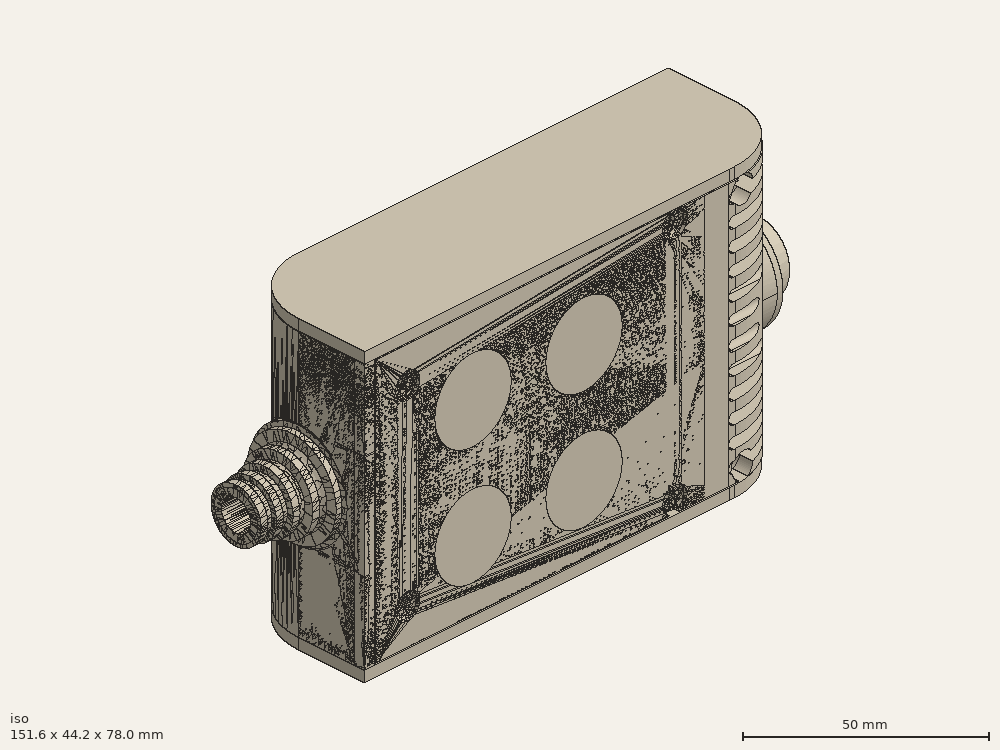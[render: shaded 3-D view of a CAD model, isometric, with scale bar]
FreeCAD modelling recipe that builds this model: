
FCSTD DOCUMENT  (FreeCAD 0.19R0.19.2)
Label: enclosure_184FCStd
License: All rights reserved
LicenseURL: http://en.wikipedia.org/wiki/All_rights_reserved
objects: Part::Revolution×152, Part::MultiFuse×146, Part::Feature×146, Sketcher::SketchObject×84, Part::Cut×70, Part::Cylinder×70, Part::Extrusion×67, Part::Fillet×58, Part::Box×36, App::MeasureDistance×4, PartDesign::Body×2, Image::ImagePlane×1
note: 831 computed .brp shape members not serialized (recipe doc carries the construction recipe); baked Part::Feature solids carry a one-line shape summary decoded from their .brp

FEATURE [Sketcher::SketchObject] Sketch  label="topSketch"
  FullyConstrained = true
  sketch-geometry (20):
    g0: LineSegment StartX=5.21097e-06 StartY=3 StartZ=0 EndX=5.21097e-06 EndY=19 EndZ=0
    g1: ArcOfCircle CenterX=19 CenterY=19 CenterZ=0 NormalX=0 NormalY=0 NormalZ=1 AngleXU=0 Radius=19 StartAngle=1.5708 EndAngle=3.14159
    g2: ArcOfCircle CenterX=19 CenterY=19 CenterZ=0 NormalX=0 NormalY=0 NormalZ=1 AngleXU=0 Radius=16 StartAngle=1.5708 EndAngle=3.14159
    g3: LineSegment StartX=114 StartY=35 StartZ=0 EndX=19 EndY=35 EndZ=0
    g4: LineSegment StartX=5.21097e-06 StartY=3 StartZ=0 EndX=5.21097e-06 EndY=0 EndZ=0
    g5: LineSegment StartX=3 StartY=0 StartZ=0 EndX=5.21097e-06 EndY=0 EndZ=0
    g6: LineSegment StartX=3 StartY=19 StartZ=0 EndX=3 EndY=0 EndZ=0
    g7: LineSegment StartX=19 StartY=38 StartZ=0 EndX=124 EndY=38 EndZ=0
    g8: Circle CenterX=119 CenterY=35 CenterZ=0 NormalX=0 NormalY=0 NormalZ=1 AngleXU=0 Radius=1
    g9: Circle CenterX=121 CenterY=35 CenterZ=0 NormalX=0 NormalY=0 NormalZ=1 AngleXU=0 Radius=1
    g10: Circle CenterX=121 CenterY=33 CenterZ=0 NormalX=0 NormalY=0 NormalZ=1 AngleXU=0 Radius=1
    g11: BSplineCurve PolesCount=3 KnotsCount=2 Degree=2 IsPeriodic=0
    g12: GeomPoint X=119 Y=35 Z=0
    g13: GeomPoint X=121 Y=33 Z=0
    g14: LineSegment StartX=119 StartY=35 StartZ=0 EndX=114 EndY=35 EndZ=0
    g15: ArcOfCircle CenterX=105 CenterY=19 CenterZ=0 NormalX=0 NormalY=0 NormalZ=1 AngleXU=0 Radius=19 StartAngle=5.7297 EndAngle=6.28319
    g16: ArcOfCircle CenterX=105 CenterY=19 CenterZ=0 NormalX=0 NormalY=0 NormalZ=1 AngleXU=0 Radius=16 StartAngle=5.60905 EndAngle=6.28319
    g17: LineSegment StartX=121 StartY=33 StartZ=0 EndX=121 EndY=19 EndZ=0
    g18: LineSegment StartX=124 StartY=38 StartZ=0 EndX=124 EndY=19 EndZ=0
    g19: LineSegment StartX=117.5 StartY=9.01251 StartZ=0 EndX=121.163 EndY=9.0125 EndZ=0
  constraints (46):
    c: Vertical(g0)
    c: Block(g0)
    c: Coincident(g1,g0)
    c: Block(g1)
    c: Coincident(g2,g1)
    c: Block(g2)
    c: Coincident(g3,g2)
    c: Horizontal(g3)
    c: Tangent(g3,g2)
    c: Coincident(g4,g0)
    c: Distance(g4) = 3
    c: Vertical(g4)
    c: Coincident(g5,g4)
    c: Horizontal(g5)
    c: Coincident(g6,g2)
    c: Coincident(g6,g5)
    c: Vertical(g6)
    c: Horizontal(g7)
    c: Distance(g7) = 105
    c: Coincident(g7,g1)
    c: Block(g3)
    c: Weight(g8) = 1
    c: Equal(g8,g9)
    c: Equal(g8,g10)
    c: InternalAlignment(g8,g11)
    c: InternalAlignment(g9,g11)
    c: InternalAlignment(g10,g11)
    c: InternalAlignment(g12,g11)
    c: InternalAlignment(g13,g11)
    c: Block(g11)
    c: Coincident(g14,g11)
    c: Coincident(g14,g3)
    c: Horizontal(g14)
    c: Block(g15)
    c: Coincident(g16,g15)
    c: Block(g16)
    c: Coincident(g17,g11)
    c: Coincident(g17,g16)
    c: Vertical(g17)
    c: Distance(g17) = 14
    c: Coincident(g18,g7)
    c: Coincident(g18,g15)
    c: Vertical(g18)
    c: Distance(g18) = 19
    c: Coincident(g19,g16)
    c: Coincident(g19,g15)
FEATURE [Sketcher::SketchObject] Sketch001  label="bottomSketch"
  FullyConstrained = true
  sketch-geometry (32):
    g0: LineSegment StartX=3.3 StartY=-6.03275e-07 StartZ=0 EndX=98 EndY=-6.03275e-07 EndZ=0
    g1: ArcOfCircle CenterX=98 CenterY=19 CenterZ=0 NormalX=0 NormalY=0 NormalZ=1 AngleXU=0 Radius=19 StartAngle=4.71239 EndAngle=5.71103
    g2: LineSegment StartX=6.3 StartY=8 StartZ=0 EndX=3.3 EndY=8 EndZ=0
    g3: LineSegment StartX=3.3 StartY=8 StartZ=0 EndX=3.3 EndY=-6.03275e-07 EndZ=0
    g4: ArcOfCircle CenterX=8.3 CenterY=5 CenterZ=0 NormalX=0 NormalY=0 NormalZ=1 AngleXU=0 Radius=2 StartAngle=3.14159 EndAngle=4.71239
    g5: LineSegment StartX=6.3 StartY=8 StartZ=0 EndX=6.3 EndY=5 EndZ=0
    g6: ArcOfCircle CenterX=98 CenterY=19 CenterZ=0 NormalX=0 NormalY=0 NormalZ=1 AngleXU=0 Radius=12.7 StartAngle=4.71239 EndAngle=6.28319
    g7: LineSegment StartX=94.7 StartY=3 StartZ=0 EndX=8.3 EndY=3 EndZ=0
    g8-g12: Circle x5 (B-spline internal-alignment scaffolding for g13; pole/knot coordinates omitted)
    g13: BSplineCurve PolesCount=5 KnotsCount=3 Degree=3 IsPeriodic=0
    g14: GeomPoint X=98 Y=6.3 Z=0
    g15: GeomPoint X=96.3938 Y=4.71946 Z=0
    g16: GeomPoint X=94.7 Y=3 Z=0
    g17-g23: Circle x7 (B-spline internal-alignment scaffolding for g24; pole/knot coordinates omitted)
    g24: BSplineCurve PolesCount=7 KnotsCount=5 Degree=3 IsPeriodic=0
    g25-g29: GeomPoint x5 (B-spline internal-alignment scaffolding for g24; pole/knot coordinates omitted)
    g30: ArcOfCircle CenterX=98 CenterY=19 CenterZ=0 NormalX=0 NormalY=0 NormalZ=1 AngleXU=0 Radius=15.7 StartAngle=5.81226 EndAngle=6.28319
    g31: LineSegment StartX=110.7 StartY=19 StartZ=0 EndX=113.7 EndY=19 EndZ=0
  constraints (41):
    c: Horizontal(g0)
    c: Coincident(g1,g0)
    c: Block(g1)
    c: Horizontal(g2)
    c: Distance(g2) = 3
    c: Coincident(g3,g2)
    c: Vertical(g3)
    c: Coincident(g3,g0)
    c: Block(g4)
    c: Block(g2)
    c: Coincident(g5,g2)
    c: Coincident(g5,g4)
    c: Vertical(g5)
    c: Coincident(g6,g1)
    c: Block(g6)
    c: Coincident(g7,g4)
    c: Horizontal(g7)
    c: Block(g0)
    c: Block(g7)
    c: Block(g3)
    c: Coincident(g13,g6)
    c: Weight(g8) = 1
    c: Equal(g8, g9-g12) x4
    c: Coincident(g13,g7)
    c: InternalAlignment(g8-g12 -> g13) x5
    c: InternalAlignment(g14,g13)
    c: InternalAlignment(g15,g13)
    c: InternalAlignment(g16,g13)
    c: Block(g13)
    c: Weight(g17) = 1
    c: Equal(g17, g18-g23) x6
    c: Coincident(g24,g1)
    c: InternalAlignment(g17-g23 -> g24) x7
    c: InternalAlignment(g25-g29 -> g24) x5
    c: Block(g24)
    c: Coincident(g30,g24)
    c: Coincident(g31,g6)
    c: Coincident(g31,g30)
    c: Horizontal(g31)
    c: Block(g31)
    c: Block(g30)
FEATURE [Part::Extrusion] Extrude  label="top"
  Base = -> Sketch
  Dir = (0,0,1)
  DirMode = 2
  FaceMakerClass = Part::FaceMakerBullseye
  LengthFwd = 72
  LengthRev = 0
  Solid = true
  Symmetric = false
FEATURE [Part::Extrusion] Extrude001  label="bottom"
  Base = -> Sketch001
  Dir = (0,0,1)
  DirMode = 2
  FaceMakerClass = Part::FaceMakerBullseye
  LengthFwd = 71.4
  LengthRev = 0
  Placement = pos=(0,0,0.3) rot=(0,0,1;0rad)
  Solid = true
  Symmetric = false
FEATURE [Sketcher::SketchObject] Sketch002  label="topSketch001"
  FullyConstrained = true
  sketch-geometry (8):
    g0: ArcOfCircle CenterX=19 CenterY=19.0975 CenterZ=0 NormalX=0 NormalY=0 NormalZ=1 AngleXU=0 Radius=18.9025 StartAngle=1.5708 EndAngle=3.14674
    g1: LineSegment StartX=0.0977805 StartY=19.0003 StartZ=0 EndX=0.0977805 EndY=0.000251602 EndZ=0
    g2: LineSegment StartX=19 StartY=38 StartZ=0 EndX=124 EndY=38 EndZ=0
    g3: LineSegment StartX=0.0977805 StartY=0.000251602 StartZ=0 EndX=105.098 EndY=0.000251602 EndZ=0
    g4: LineSegment StartX=124 StartY=38 StartZ=0 EndX=125.616 EndY=38 EndZ=0
    g5: LineSegment StartX=105.098 StartY=0.000251602 StartZ=0 EndX=106.713 EndY=0.000251602 EndZ=0
    g6: ArcOfCircle CenterX=106.616 CenterY=19 CenterZ=0 NormalX=0 NormalY=0 NormalZ=1 AngleXU=0 Radius=19 StartAngle=4.71754 EndAngle=6.28319
    g7: LineSegment StartX=125.616 StartY=38 StartZ=0 EndX=125.616 EndY=19 EndZ=0
  constraints (21):
    c: Block(g0)
    c: Coincident(g1,g0)
    c: Vertical(g1)
    c: Horizontal(g2)
    c: Distance(g2) = 105
    c: Coincident(g2,g0)
    c: Distance(g1) = 19
    c: Coincident(g3,g1)
    c: Horizontal(g3)
    c: Distance(g3) = 105
    c: Coincident(g4,g2)
    c: Horizontal(g4)
    c: Distance(g4) = 1.61553
    c: Horizontal(g5)
    c: Equal(g4,g5) = 1.61553
    c: Coincident(g5,g3)
    c: Block(g6)
    c: Coincident(g6,g5)
    c: Coincident(g7,g4)
    c: Coincident(g7,g6)
    c: Vertical(g7)
FEATURE [Part::Extrusion] Extrude002  label="sideA"
  Base = -> Sketch002
  Dir = (0,0,1)
  DirMode = 2
  FaceMakerClass = Part::FaceMakerBullseye
  LengthFwd = 3
  LengthRev = 0
  Placement = pos=(0,0,-3) rot=(0,0,1;0rad)
  Solid = true
  Symmetric = false
FEATURE [Sketcher::SketchObject] Sketch003  label="topSketch002"
  FullyConstrained = true
  sketch-geometry (6):
    g0: LineSegment StartX=19 StartY=38 StartZ=0 EndX=117 EndY=38 EndZ=0
    g1: ArcOfCircle CenterX=19 CenterY=19 CenterZ=0 NormalX=0 NormalY=0 NormalZ=1 AngleXU=0 Radius=19 StartAngle=1.5708 EndAngle=3.14159
    g2: LineSegment StartX=117 StartY=38 StartZ=0 EndX=117 EndY=19 EndZ=0
    g3: LineSegment StartX=98 StartY=1.0161e-12 StartZ=0 EndX=5.22862e-06 EndY=1.0161e-12 EndZ=0
    g4: LineSegment StartX=5.22862e-06 StartY=19 StartZ=0 EndX=5.22862e-06 EndY=1.0161e-12 EndZ=0
    g5: ArcOfCircle CenterX=98 CenterY=19 CenterZ=0 NormalX=0 NormalY=0 NormalZ=1 AngleXU=0 Radius=19 StartAngle=4.71239 EndAngle=6.28319
  constraints (16):
    c: Horizontal(g0)
    c: Distance(g0) = 98
    c: Coincident(g1,g0)
    c: Block(g1)
    c: Coincident(g2,g0)
    c: Vertical(g2)
    c: Distance(g2) = 19
    c: Horizontal(g3)
    c: Coincident(g4,g1)
    c: Vertical(g4)
    c: Coincident(g3,g4)
    c: Block(g3)
    c: Coincident(g5,g2)
    c: Coincident(g5,g3)
    c: Block(g0)
    c: Block(g5)
FEATURE [Sketcher::SketchObject] Sketch004
  FullyConstrained = true
  MapMode = 3
  Placement = pos=(0,0,0) rot=(1,0,0;1.5708rad)
  Support = -> [Extrude]
  sketch-geometry (8):
    g0: Circle CenterX=80.351 CenterY=-67.6202 CenterZ=0 NormalX=0 NormalY=0 NormalZ=1 AngleXU=0 Radius=2
    g1: Circle CenterX=80.351 CenterY=-67.6202 CenterZ=0 NormalX=0 NormalY=0 NormalZ=1 AngleXU=0 Radius=3
    g2: Circle CenterX=80.351 CenterY=-4.92017 CenterZ=0 NormalX=0 NormalY=0 NormalZ=1 AngleXU=0 Radius=2
    g3: Circle CenterX=80.351 CenterY=-4.92017 CenterZ=0 NormalX=0 NormalY=0 NormalZ=1 AngleXU=0 Radius=3
    g4: Circle CenterX=23.851 CenterY=-4.92017 CenterZ=0 NormalX=0 NormalY=0 NormalZ=1 AngleXU=0 Radius=2
    g5: Circle CenterX=23.851 CenterY=-4.92017 CenterZ=0 NormalX=0 NormalY=0 NormalZ=1 AngleXU=0 Radius=3
    g6: Circle CenterX=23.851 CenterY=-67.6202 CenterZ=0 NormalX=0 NormalY=0 NormalZ=1 AngleXU=0 Radius=2
    g7: Circle CenterX=23.851 CenterY=-67.6202 CenterZ=0 NormalX=0 NormalY=0 NormalZ=1 AngleXU=0 Radius=3
  constraints (8):
    c: Block(g3)
    c: Block(g2)
    c: Block(g1)
    c: Block(g0)
    c: Block(g6)
    c: Block(g7)
    c: Block(g4)
    c: Block(g5)
FEATURE [Part::Extrusion] Extrude004
  Base = -> Sketch004
  Dir = (0,-1,2e-16)
  DirMode = 2
  FaceMakerClass = Part::FaceMakerBullseye
  LengthFwd = 6
  LengthRev = 0
  Placement = pos=(0,9,0) rot=(0,0,1;0rad)
  Solid = true
  Symmetric = false
FEATURE [Sketcher::SketchObject] Sketch005
  FullyConstrained = true
  MapMode = 3
  Placement = pos=(0,0,0) rot=(1,0,0;1.5708rad)
  Support = -> [Extrude]
  sketch-geometry (8):
    g0: Circle CenterX=80.351 CenterY=-67.6202 CenterZ=0 NormalX=0 NormalY=0 NormalZ=1 AngleXU=0 Radius=3
    g1: Circle CenterX=80.351 CenterY=-4.92017 CenterZ=0 NormalX=0 NormalY=0 NormalZ=1 AngleXU=0 Radius=3
    g2: Circle CenterX=23.851 CenterY=-4.92017 CenterZ=0 NormalX=0 NormalY=0 NormalZ=1 AngleXU=0 Radius=3
    g3: Circle CenterX=23.851 CenterY=-67.6202 CenterZ=0 NormalX=0 NormalY=0 NormalZ=1 AngleXU=0 Radius=3
    g4: Circle CenterX=23.851 CenterY=-67.6202 CenterZ=0 NormalX=0 NormalY=0 NormalZ=1 AngleXU=0 Radius=5
    g5: Circle CenterX=80.351 CenterY=-67.6202 CenterZ=0 NormalX=0 NormalY=0 NormalZ=1 AngleXU=0 Radius=5
    g6: Circle CenterX=23.851 CenterY=-4.92017 CenterZ=0 NormalX=0 NormalY=0 NormalZ=1 AngleXU=0 Radius=5
    g7: Circle CenterX=80.351 CenterY=-4.92017 CenterZ=0 NormalX=0 NormalY=0 NormalZ=1 AngleXU=0 Radius=5
  constraints (8):
    c: Block(g1)
    c: Block(g0)
    c: Block(g3)
    c: Block(g2)
    c: Block(g5)
    c: Block(g4)
    c: Block(g6)
    c: Block(g7)
FEATURE [Part::Extrusion] Extrude005
  Base = -> Sketch005
  Dir = (0,-1,2e-16)
  DirMode = 2
  FaceMakerClass = Part::FaceMakerBullseye
  LengthFwd = 2
  LengthRev = 0
  Solid = true
  Symmetric = false
FEATURE [Sketcher::SketchObject] Sketch006
  FullyConstrained = true
  MapMode = 3
  Placement = pos=(0,0,0) rot=(1,0,0;1.5708rad)
  sketch-geometry (8):
    g0: Circle CenterX=80.351 CenterY=-67.6202 CenterZ=0 NormalX=0 NormalY=0 NormalZ=1 AngleXU=0 Radius=3
    g1: Circle CenterX=80.351 CenterY=-4.92017 CenterZ=0 NormalX=0 NormalY=0 NormalZ=1 AngleXU=0 Radius=3
    g2: Circle CenterX=23.851 CenterY=-4.92017 CenterZ=0 NormalX=0 NormalY=0 NormalZ=1 AngleXU=0 Radius=3
    g3: Circle CenterX=23.851 CenterY=-67.6202 CenterZ=0 NormalX=0 NormalY=0 NormalZ=1 AngleXU=0 Radius=3
    g4: Circle CenterX=23.851 CenterY=-67.6202 CenterZ=0 NormalX=0 NormalY=0 NormalZ=1 AngleXU=0 Radius=5
    g5: Circle CenterX=80.351 CenterY=-67.6202 CenterZ=0 NormalX=0 NormalY=0 NormalZ=1 AngleXU=0 Radius=5
    g6: Circle CenterX=23.851 CenterY=-4.92017 CenterZ=0 NormalX=0 NormalY=0 NormalZ=1 AngleXU=0 Radius=5
    g7: Circle CenterX=80.351 CenterY=-4.92017 CenterZ=0 NormalX=0 NormalY=0 NormalZ=1 AngleXU=0 Radius=5
  constraints (8):
    c: Block(g1)
    c: Block(g0)
    c: Block(g3)
    c: Block(g2)
    c: Block(g5)
    c: Block(g4)
    c: Block(g6)
    c: Block(g7)
FEATURE [Part::Extrusion] Extrude007
  Base = -> Sketch006
  Dir = (0,-1,2e-16)
  DirMode = 2
  FaceMakerClass = Part::FaceMakerBullseye
  LengthFwd = 2
  LengthRev = 0
  Solid = true
  Symmetric = false
FEATURE [Part::Fillet] Fillet
  Base = -> Extrude007
  Edges = 4 edges r=1.99: [Edge6,Edge12,Edge18,Edge24]
FEATURE [Part::Cut] Cut
  Base = -> Extrude005
  Placement = pos=(0,5,0) rot=(0,0,1;0rad)
  Tool = -> Fillet
FEATURE [Part::MultiFuse] Fusion  label="pCBScrews"
  Placement = pos=(-2.5,0,72.3) rot=(0,0,1;0rad)
  Shapes = -> [Extrude004,Cut]
FEATURE [App::MeasureDistance] Distance  label="Distance: 0.69 mm"
  Distance = 0.685967
  P1 = (24.0138,2.9647,0.3)
  P2 = (23.8901,3,-0.373787)
FEATURE [App::MeasureDistance] Distance001  label="Distance: 0.53 mm"
  Distance = 0.533607
  P1 = (80.2939,3,72.2334)
  P2 = (80.281,2.99661,71.7)
FEATURE [Part::Fillet] Fillet001
  Base = -> Extrude001
  Edges = 1 edges r=2.4: [Edge17]
FEATURE [Part::Fillet] Fillet002  label="bottom001"
  Base = -> Fillet001
  Edges = 1 edges r=2.4: [Edge36]
FEATURE [Part::Fillet] Fillet003  label="top001"
  Base = -> Extrude
  Edges = 1 edges r=2: [Edge1]
FEATURE [Sketcher::SketchObject] Sketch007
  FullyConstrained = true
  sketch-geometry (16):
    g0: LineSegment StartX=4 StartY=0 StartZ=0 EndX=4 EndY=2.4 EndZ=0
    g1: LineSegment StartX=4 StartY=2.4 StartZ=0 EndX=7 EndY=2.4 EndZ=0
    g2: LineSegment StartX=4 StartY=0 StartZ=0 EndX=5.7 EndY=0 EndZ=0
    g3: LineSegment StartX=5.7 StartY=0 StartZ=0 EndX=5.7 EndY=-5.6 EndZ=0
    g4-g8: Circle x5 (B-spline internal-alignment scaffolding for g9; pole/knot coordinates omitted)
    g9: BSplineCurve PolesCount=5 KnotsCount=3 Degree=3 IsPeriodic=0
    g10: GeomPoint X=7 Y=2.4 Z=0
    g11: GeomPoint X=10.4582 Y=-1.55472 Z=0
    g12: GeomPoint X=14 Y=-5.6 Z=0
    g13: LineSegment StartX=14 StartY=-5.6 StartZ=0 EndX=14 EndY=-14.1 EndZ=0
    g14: LineSegment StartX=14 StartY=-14.1 StartZ=0 EndX=6.5 EndY=-14.1 EndZ=0
    g15: LineSegment StartX=5.7 StartY=-5.6 StartZ=0 EndX=6.5 EndY=-14.1 EndZ=0
  constraints (28):
    c: Distance(g0) = 2.4
    c: Vertical(g0)
    c: Block(g0)
    c: Coincident(g1,g0)
    c: Horizontal(g1)
    c: Distance(g1) = 3
    c: Coincident(g2,g0)
    c: Horizontal(g2)
    c: Distance(g2) = 1.7
    c: Coincident(g3,g2)
    c: Vertical(g3)
    c: Distance(g3) = 5.6
    c: Coincident(g9,g1)
    c: Weight(g4) = 1
    c: Equal(g4, g5-g8) x4
    c: InternalAlignment(g4-g8 -> g9) x5
    c: InternalAlignment(g10,g9)
    c: InternalAlignment(g11,g9)
    c: InternalAlignment(g12,g9)
    c: Block(g9)
    c: Coincident(g13,g9)
    c: Vertical(g13)
    c: Distance(g13) = 8.5
    c: Coincident(g14,g13)
    c: Horizontal(g14)
    c: Distance(g14) = 7.5
    c: Coincident(g15,g3)
    c: Coincident(g15,g14)
FEATURE [Part::Feature] Face
  shape: bbox 10 x 16.5 x 2e-07 mm, 1 faces, 0 solids (baked)
FEATURE [Part::Revolution] Revolve  label="plugHousing"
  Angle = 360
  Axis = (0,1,0)
  Base = (0,0,0)
  FaceMakerClass = Part::FaceMakerBullseye
  Placement = pos=(0,0,36.15) rot=(0,0,1;0rad)
  Solid = false
  Source = -> Face
  Symmetric = false
FEATURE [Part::Feature] Face001
  shape: bbox 10 x 16.5 x 2e-07 mm, 1 faces, 0 solids (baked)
FEATURE [Part::Revolution] Revolve001  label="plugHousing001"
  Angle = 360
  Axis = (0,1,0)
  Base = (0,0,0)
  FaceMakerClass = Part::FaceMakerBullseye
  Placement = pos=(0,0,36.15) rot=(0,0,1;0rad)
  Solid = false
  Source = -> Face001
  Symmetric = false
FEATURE [Part::MultiFuse] Fusion001  label="plugHousing002"
  Placement = pos=(0,0,0) rot=(0,0,1;1.5708rad)
  Shapes = -> [Revolve001,Revolve]
FEATURE [Part::Feature] Face002
  shape: bbox 10 x 16.5 x 2e-07 mm, 1 faces, 0 solids (baked)
FEATURE [Part::Revolution] Revolve003  label="plugHousing005"
  Angle = 360
  Axis = (0,1,0)
  Base = (0,0,0)
  FaceMakerClass = Part::FaceMakerBullseye
  Placement = pos=(0,0,36.15) rot=(0,0,1;0rad)
  Solid = false
  Source = -> Face002
  Symmetric = false
FEATURE [Part::Feature] Face003
  shape: bbox 10 x 16.5 x 2e-07 mm, 1 faces, 0 solids (baked)
FEATURE [Part::Revolution] Revolve002  label="plugHousing003"
  Angle = 360
  Axis = (0,1,0)
  Base = (0,0,0)
  FaceMakerClass = Part::FaceMakerBullseye
  Placement = pos=(0,0,36.15) rot=(0,0,1;0rad)
  Solid = false
  Source = -> Face003
  Symmetric = false
FEATURE [Part::MultiFuse] Fusion002  label="plugHousing004"
  Placement = pos=(0,0,0) rot=(0,0,1;1.5708rad)
  Shapes = -> [Revolve002,Revolve003]
FEATURE [Part::MultiFuse] Fusion003  label="plugHousing006"
  Placement = pos=(0,19,0) rot=(0,0,1;3.14159rad)
  Shapes = -> [Fusion002,Fusion001]
FEATURE [Part::Feature] Face004
  shape: bbox 10 x 16.5 x 2e-07 mm, 1 faces, 0 solids (baked)
FEATURE [Part::Revolution] Revolve006  label="plugHousing010"
  Angle = 360
  Axis = (0,1,0)
  Base = (0,0,0)
  FaceMakerClass = Part::FaceMakerBullseye
  Placement = pos=(0,0,36.15) rot=(0,0,1;0rad)
  Solid = false
  Source = -> Face004
  Symmetric = false
FEATURE [Part::Feature] Face005
  shape: bbox 10 x 16.5 x 2e-07 mm, 1 faces, 0 solids (baked)
FEATURE [Part::Revolution] Revolve007  label="plugHousing011"
  Angle = 360
  Axis = (0,1,0)
  Base = (0,0,0)
  FaceMakerClass = Part::FaceMakerBullseye
  Placement = pos=(0,0,36.15) rot=(0,0,1;0rad)
  Solid = false
  Source = -> Face005
  Symmetric = false
FEATURE [Part::Feature] Face006
  shape: bbox 10 x 16.5 x 2e-07 mm, 1 faces, 0 solids (baked)
FEATURE [Part::Revolution] Revolve004  label="plugHousing007"
  Angle = 360
  Axis = (0,1,0)
  Base = (0,0,0)
  FaceMakerClass = Part::FaceMakerBullseye
  Placement = pos=(0,0,36.15) rot=(0,0,1;0rad)
  Solid = false
  Source = -> Face006
  Symmetric = false
FEATURE [Part::MultiFuse] Fusion004  label="plugHousing009"
  Placement = pos=(0,0,0) rot=(0,0,1;1.5708rad)
  Shapes = -> [Revolve004,Revolve007]
FEATURE [Part::Feature] Face007
  shape: bbox 10 x 16.5 x 2e-07 mm, 1 faces, 0 solids (baked)
FEATURE [Part::Revolution] Revolve005  label="plugHousing008"
  Angle = 360
  Axis = (0,1,0)
  Base = (0,0,0)
  FaceMakerClass = Part::FaceMakerBullseye
  Placement = pos=(0,0,36.15) rot=(0,0,1;0rad)
  Solid = false
  Source = -> Face007
  Symmetric = false
FEATURE [Part::MultiFuse] Fusion005  label="plugHousing012"
  Placement = pos=(0,0,0) rot=(0,0,1;1.5708rad)
  Shapes = -> [Revolve006,Revolve005]
FEATURE [Part::MultiFuse] Fusion006  label="plugHousing013"
  Placement = pos=(0,19,0) rot=(0,0,1;3.14159rad)
  Shapes = -> [Fusion005,Fusion004]
FEATURE [Part::MultiFuse] Fusion007  label="plugHousing014"
  Placement = pos=(122.621,0,-0.15) rot=(0,0,1;0rad)
  Shapes = -> [Fusion003,Fusion006]
FEATURE [Part::Cylinder] Cylinder002
  Angle = 360
  AttacherType = Attacher::AttachEngine3D
  Height = 20
  Placement = pos=(0,0,36.15) rot=(0,0,1;0rad)
  Radius = 4
FEATURE [Part::Cylinder] Cylinder003
  Angle = 360
  AttacherType = Attacher::AttachEngine3D
  Height = 10
  Placement = pos=(0,0,36.15) rot=(0,0,1;0rad)
  Radius = 4
FEATURE [Part::MultiFuse] Fusion009  label="removeToCreateHoleForPlugHousing"
  Placement = pos=(70,19,36.15) rot=(0,1,0;1.5708rad)
  Shapes = -> [Cylinder002,Cylinder003]
FEATURE [Part::Cylinder] Cylinder004
  Angle = 360
  AttacherType = Attacher::AttachEngine3D
  Height = 20
  Placement = pos=(0,0,36.15) rot=(0,0,1;0rad)
  Radius = 4
FEATURE [Part::Cylinder] Cylinder005
  Angle = 360
  AttacherType = Attacher::AttachEngine3D
  Height = 10
  Placement = pos=(0,0,36.15) rot=(0,0,1;0rad)
  Radius = 4
FEATURE [Part::MultiFuse] Fusion010  label="removeToCreateHoleForPlugHousing001"
  Placement = pos=(70,19,36.15) rot=(0,1,0;1.5708rad)
  Shapes = -> [Cylinder004,Cylinder005]
FEATURE [Part::Cut] Cut001
  Base = -> Fillet003
  Tool = -> Fusion010
FEATURE [Part::Cut] Cut002  label="Bottom"
  Base = -> Fillet002
  Tool = -> Fusion009
FEATURE [Part::Feature] Face008
  shape: bbox 10 x 16.5 x 2e-07 mm, 1 faces, 0 solids (baked)
FEATURE [Part::Revolution] Revolve011  label="plugHousing021"
  Angle = 360
  Axis = (0,1,0)
  Base = (0,0,0)
  FaceMakerClass = Part::FaceMakerBullseye
  Placement = pos=(0,0,36.15) rot=(0,0,1;0rad)
  Solid = false
  Source = -> Face008
  Symmetric = false
FEATURE [Part::Feature] Face009
  shape: bbox 10 x 16.5 x 2e-07 mm, 1 faces, 0 solids (baked)
FEATURE [Part::Revolution] Revolve012  label="plugHousing022"
  Angle = 360
  Axis = (0,1,0)
  Base = (0,0,0)
  FaceMakerClass = Part::FaceMakerBullseye
  Placement = pos=(0,0,36.15) rot=(0,0,1;0rad)
  Solid = false
  Source = -> Face009
  Symmetric = false
FEATURE [Part::Feature] Face010 .. Face013  x4 (patterned run collapsed; names and placements below)
  shape: bbox 10 x 16.5 x 2e-07 mm, 1 faces, 0 solids (baked)
FEATURE [Part::Revolution] Revolve015  label="plugHousing027"
  Angle = 360
  Axis = (0,1,0)
  Base = (0,0,0)
  FaceMakerClass = Part::FaceMakerBullseye
  Placement = pos=(0,0,36.15) rot=(0,0,1;0rad)
  Solid = false
  Source = -> Face013
  Symmetric = false
FEATURE [Part::Feature] Face014
  shape: bbox 10 x 16.5 x 2e-07 mm, 1 faces, 0 solids (baked)
FEATURE [Part::Feature] Face015
  shape: bbox 10 x 16.5 x 2e-07 mm, 1 faces, 0 solids (baked)
FEATURE [Part::Feature] Face016
  shape: bbox 10 x 16.5 x 2e-07 mm, 1 faces, 0 solids (baked)
FEATURE [Part::Revolution] Revolve019  label="plugHousing033"
  Angle = 360
  Axis = (0,1,0)
  Base = (0,0,0)
  FaceMakerClass = Part::FaceMakerBullseye
  Placement = pos=(0,0,36.15) rot=(0,0,1;0rad)
  Solid = false
  Source = -> Face016
  Symmetric = false
FEATURE [Part::Feature] Face017
  shape: bbox 10 x 16.5 x 2e-07 mm, 1 faces, 0 solids (baked)
FEATURE [Part::Revolution] Revolve020  label="plugHousing034"
  Angle = 360
  Axis = (0,1,0)
  Base = (0,0,0)
  FaceMakerClass = Part::FaceMakerBullseye
  Placement = pos=(0,0,36.15) rot=(0,0,1;0rad)
  Solid = false
  Source = -> Face017
  Symmetric = false
FEATURE [Part::Feature] Face018
  shape: bbox 10 x 16.5 x 2e-07 mm, 1 faces, 0 solids (baked)
FEATURE [Part::Revolution] Revolve016  label="plugHousing030"
  Angle = 360
  Axis = (0,1,0)
  Base = (0,0,0)
  FaceMakerClass = Part::FaceMakerBullseye
  Placement = pos=(0,0,36.15) rot=(0,0,1;0rad)
  Solid = false
  Source = -> Face018
  Symmetric = false
FEATURE [Part::MultiFuse] Fusion020  label="plugHousing038"
  Placement = pos=(0,0,0) rot=(0,0,1;1.5708rad)
  Shapes = -> [Revolve016,Revolve020]
FEATURE [Part::Feature] Face019
  shape: bbox 10 x 16.5 x 2e-07 mm, 1 faces, 0 solids (baked)
FEATURE [Part::Feature] Face020
  shape: bbox 10 x 16.5 x 2e-07 mm, 1 faces, 0 solids (baked)
FEATURE [Part::Revolution] Revolve017  label="plugHousing031"
  Angle = 360
  Axis = (0,1,0)
  Base = (0,0,0)
  FaceMakerClass = Part::FaceMakerBullseye
  Placement = pos=(0,0,36.15) rot=(0,0,1;0rad)
  Solid = false
  Source = -> Face020
  Symmetric = false
FEATURE [Part::MultiFuse] Fusion021  label="plugHousing039"
  Placement = pos=(0,0,0) rot=(0,0,1;1.5708rad)
  Shapes = -> [Revolve019,Revolve017]
FEATURE [Part::MultiFuse] Fusion023  label="plugHousing041"
  Placement = pos=(0,19,0) rot=(0,0,1;3.14159rad)
  Shapes = -> [Fusion021,Fusion020]
FEATURE [Part::Revolution] Revolve022  label="plugHousing043"
  Angle = 360
  Axis = (0,1,0)
  Base = (0,0,0)
  FaceMakerClass = Part::FaceMakerBullseye
  Placement = pos=(0,0,36.15) rot=(0,0,1;0rad)
  Solid = false
  Source = -> Face019
  Symmetric = false
FEATURE [Part::Feature] Face021
  shape: bbox 10 x 16.5 x 2e-07 mm, 1 faces, 0 solids (baked)
FEATURE [Part::Revolution] Revolve023  label="plugHousing044"
  Angle = 360
  Axis = (0,1,0)
  Base = (0,0,0)
  FaceMakerClass = Part::FaceMakerBullseye
  Placement = pos=(0,0,36.15) rot=(0,0,1;0rad)
  Solid = false
  Source = -> Face021
  Symmetric = false
FEATURE [Part::Feature] Face022
  shape: bbox 10 x 16.5 x 2e-07 mm, 1 faces, 0 solids (baked)
FEATURE [Part::Revolution] Revolve018  label="plugHousing032"
  Angle = 360
  Axis = (0,1,0)
  Base = (0,0,0)
  FaceMakerClass = Part::FaceMakerBullseye
  Placement = pos=(0,0,36.15) rot=(0,0,1;0rad)
  Solid = false
  Source = -> Face022
  Symmetric = false
FEATURE [Part::MultiFuse] Fusion022  label="plugHousing040"
  Placement = pos=(0,0,0) rot=(0,0,1;1.5708rad)
  Shapes = -> [Revolve018,Revolve023]
FEATURE [Part::Feature] Face023
  shape: bbox 10 x 16.5 x 2e-07 mm, 1 faces, 0 solids (baked)
FEATURE [Part::Revolution] Revolve021  label="plugHousing035"
  Angle = 360
  Axis = (0,1,0)
  Base = (0,0,0)
  FaceMakerClass = Part::FaceMakerBullseye
  Placement = pos=(0,0,36.15) rot=(0,0,1;0rad)
  Solid = false
  Source = -> Face023
  Symmetric = false
FEATURE [Part::MultiFuse] Fusion018  label="plugHousing036"
  Placement = pos=(0,0,0) rot=(0,0,1;1.5708rad)
  Shapes = -> [Revolve022,Revolve021]
FEATURE [Part::MultiFuse] Fusion019  label="plugHousing037"
  Placement = pos=(0,19,0) rot=(0,0,1;3.14159rad)
  Shapes = -> [Fusion018,Fusion022]
FEATURE [Part::MultiFuse] Fusion024  label="plugHousing042"
  Placement = pos=(122.621,0,-0.15) rot=(0,0,1;0rad)
  Shapes = -> [Fusion023,Fusion019]
FEATURE [Part::Cylinder] Cylinder006
  Angle = 360
  AttacherType = Attacher::AttachEngine3D
  Height = 20
  Placement = pos=(0,0,36.15) rot=(0,0,1;0rad)
  Radius = 14.3
FEATURE [Part::Cylinder] Cylinder007
  Angle = 360
  AttacherType = Attacher::AttachEngine3D
  Height = 10
  Placement = pos=(0,0,36.15) rot=(0,0,1;0rad)
  Radius = 4
FEATURE [Part::MultiFuse] Fusion026  label="removeToCreteHoleForPlugHousing"
  Placement = pos=(70,19,36) rot=(0,1,0;1.5708rad)
  Shapes = -> [Cylinder006,Cylinder007]
FEATURE [Part::Box] Box001  label="Cube001"
  AttacherType = Attacher::AttachEngine3D
  Height = 28
  Length = 3
  Placement = pos=(110.7,19,22) rot=(0,0,1;0rad)
  Width = 15.7
FEATURE [Part::Cut] Cut003  label="top002"
  Base = -> Cut001
  Tool = -> Fusion007
FEATURE [Part::Revolution] Revolve008  label="plugHousing015"
  Angle = 360
  Axis = (0,1,0)
  Base = (0,0,0)
  FaceMakerClass = Part::FaceMakerBullseye
  Placement = pos=(0,0,36.15) rot=(0,0,1;0rad)
  Solid = false
  Source = -> Face010
  Symmetric = false
FEATURE [Part::MultiFuse] Fusion013  label="plugHousing020"
  Placement = pos=(0,0,0) rot=(0,0,1;1.5708rad)
  Shapes = -> [Revolve008,Revolve012]
FEATURE [Part::Cut] Cut004  label="top003"
  Base = -> Cut003
  Placement = pos=(1,0,0) rot=(0,0,1;0rad)
  Tool = -> Fusion026
FEATURE [Part::Cylinder] Cylinder008
  Angle = 360
  AttacherType = Attacher::AttachEngine3D
  Height = 20
  Placement = pos=(0,0,36.15) rot=(0,0,1;0rad)
  Radius = 10.3
FEATURE [Part::Cylinder] Cylinder009
  Angle = 360
  AttacherType = Attacher::AttachEngine3D
  Height = 10
  Placement = pos=(0,0,36.15) rot=(0,0,1;0rad)
  Radius = 4
FEATURE [Part::MultiFuse] Fusion027  label="removeToCreteHoleForPlugHousing001"
  Placement = pos=(70,19,36) rot=(0,1,0;1.5708rad)
  Shapes = -> [Cylinder008,Cylinder009]
FEATURE [Part::Cut] Cut005  label="plugHousingTab"
  Base = -> Box001
  Tool = -> Fusion027
FEATURE [Part::MultiFuse] Fusion028  label="plugHousing045"
  Shapes = -> [Fusion024,Cut005]
FEATURE [Part::Box] Box002  label="Cube002"
  AttacherType = Attacher::AttachEngine3D
  Height = 28.8
  Length = 3
  Placement = pos=(107.3,28,21.6) rot=(0,0,1;0rad)
  Width = 7
FEATURE [Part::Box] Box003  label="Cube003"
  AttacherType = Attacher::AttachEngine3D
  Height = 3
  Length = 6.4
  Placement = pos=(107.3,28,18.6) rot=(0,0,1;0rad)
  Width = 7
FEATURE [Part::Box] Box004  label="Cube004"
  AttacherType = Attacher::AttachEngine3D
  Height = 3
  Length = 6.4
  Placement = pos=(107.3,28,50.4) rot=(0,0,1;0rad)
  Width = 7
FEATURE [Part::MultiFuse] Fusion029  label="plugHousingBracketHolder"
  Shapes = -> [Box004,Box002,Box003]
FEATURE [Part::Cylinder] Cylinder010
  Angle = 360
  AttacherType = Attacher::AttachEngine3D
  Height = 20
  Placement = pos=(0,0,36.15) rot=(0,0,1;0rad)
  Radius = 14.3
FEATURE [Part::Cylinder] Cylinder011
  Angle = 360
  AttacherType = Attacher::AttachEngine3D
  Height = 10
  Placement = pos=(0,0,36.15) rot=(0,0,1;0rad)
  Radius = 4
FEATURE [Part::MultiFuse] Fusion030  label="removeToCreteHoleForPlugHousing002"
  Placement = pos=(70,19,36) rot=(0,1,0;1.5708rad)
  Shapes = -> [Cylinder010,Cylinder011]
FEATURE [Part::Cut] Cut006  label="plugHousingBracketHolder001"
  Base = -> Fusion029
  Tool = -> Fusion030
FEATURE [Part::Cylinder] Cylinder012
  Angle = 360
  AttacherType = Attacher::AttachEngine3D
  Height = 20
  Placement = pos=(0,0,36.15) rot=(0,0,1;0rad)
  Radius = 7
FEATURE [Part::Cylinder] Cylinder013
  Angle = 360
  AttacherType = Attacher::AttachEngine3D
  Height = 10
  Placement = pos=(0,0,36.15) rot=(0,0,1;0rad)
  Radius = 4
FEATURE [Part::MultiFuse] Fusion032  label="removeToCreteHoleForPlugHousing003"
  Placement = pos=(70,19,36) rot=(0,1,0;1.5708rad)
  Shapes = -> [Cylinder012,Cylinder013]
FEATURE [Part::Cut] Cut007  label="bottom002"
  Base = -> Cut002
  Tool = -> Fusion032
FEATURE [Sketcher::SketchObject] Sketch008
  FullyConstrained = true
  sketch-geometry (54):
    g0: LineSegment StartX=-4.2 StartY=0 StartZ=0 EndX=-6.2 EndY=0 EndZ=0
    g1: LineSegment StartX=-14 StartY=-18 StartZ=0 EndX=-14 EndY=-26.5 EndZ=0
    g2: LineSegment StartX=-4.2 StartY=0 StartZ=0 EndX=-4.2 EndY=-13.4877 EndZ=0
    g3: Circle CenterX=-4.2 CenterY=-13.4877 CenterZ=0 NormalX=0 NormalY=0 NormalZ=1 AngleXU=0 Radius=1
    g4: Circle CenterX=-4.2 CenterY=-26.5 CenterZ=0 NormalX=0 NormalY=0 NormalZ=1 AngleXU=0 Radius=1
    g5: Circle CenterX=-8.2 CenterY=-26.5 CenterZ=0 NormalX=0 NormalY=0 NormalZ=1 AngleXU=0 Radius=1
    g6: BSplineCurve PolesCount=3 KnotsCount=2 Degree=2 IsPeriodic=0
    g7: GeomPoint X=-4.2 Y=-13.4877 Z=0
    g8: GeomPoint X=-8.2 Y=-26.5 Z=0
    g9: LineSegment StartX=-14 StartY=-26.5 StartZ=0 EndX=-8.2 EndY=-26.5 EndZ=0
    g10: LineSegment StartX=-10.15 StartY=-12 StartZ=0 EndX=-10.15 EndY=-14 EndZ=0
    g11: LineSegment StartX=-12.8401 StartY=-16 StartZ=0 EndX=-10.1571 EndY=-16 EndZ=0
    g12: LineSegment StartX=-10.15 StartY=-14 StartZ=0 EndX=-8.70761 EndY=-14 EndZ=0
    g13: LineSegment StartX=-12.8401 StartY=-16 StartZ=0 EndX=-12.8401 EndY=-17.6958 EndZ=0
    g14: LineSegment StartX=-10.15 StartY=-12 StartZ=0 EndX=-7.79258 EndY=-12 EndZ=0
    g15: Circle CenterX=-6.2215 CenterY=-2 CenterZ=0 NormalX=0 NormalY=0 NormalZ=1 AngleXU=0 Radius=1
    g16: Circle CenterX=-6.22762 CenterY=-2.58724 CenterZ=0 NormalX=0 NormalY=0 NormalZ=1 AngleXU=0 Radius=1
    g17: Circle CenterX=-6.32538 CenterY=-4 CenterZ=0 NormalX=0 NormalY=0 NormalZ=1 AngleXU=0 Radius=1
    g18: BSplineCurve PolesCount=3 KnotsCount=2 Degree=2 IsPeriodic=0
    g19: GeomPoint X=-6.2215 Y=-2 Z=0
    g20: GeomPoint X=-6.32538 Y=-4 Z=0
    g21: Circle CenterX=-6.48644 CenterY=-5.99526 CenterZ=0 NormalX=0 NormalY=0 NormalZ=1 AngleXU=0 Radius=1
    g22: Circle CenterX=-6.58486 CenterY=-6.99526 CenterZ=0 NormalX=0 NormalY=0 NormalZ=1 AngleXU=0 Radius=1
    g23: Circle CenterX=-6.77343 CenterY=-8 CenterZ=0 NormalX=0 NormalY=0 NormalZ=1 AngleXU=0 Radius=1
    g24: BSplineCurve PolesCount=3 KnotsCount=2 Degree=2 IsPeriodic=0
    g25: GeomPoint X=-6.48644 Y=-5.99526 Z=0
    g26: GeomPoint X=-6.77343 Y=-8 Z=0
    g27: Circle CenterX=-7.19003 CenterY=-10 CenterZ=0 NormalX=0 NormalY=0 NormalZ=1 AngleXU=0 Radius=1
    g28: Circle CenterX=-7.44407 CenterY=-11.0915 CenterZ=0 NormalX=0 NormalY=0 NormalZ=1 AngleXU=0 Radius=1
    g29: Circle CenterX=-7.79258 CenterY=-12 CenterZ=0 NormalX=0 NormalY=0 NormalZ=1 AngleXU=0 Radius=1
    g30: BSplineCurve PolesCount=3 KnotsCount=2 Degree=2 IsPeriodic=0
    g31: GeomPoint X=-7.19003 Y=-10 Z=0
    g32: GeomPoint X=-7.79258 Y=-12 Z=0
    g33: Circle CenterX=-8.70761 CenterY=-14 CenterZ=0 NormalX=0 NormalY=0 NormalZ=1 AngleXU=0 Radius=1
    g34: Circle CenterX=-9.33087 CenterY=-15.1837 CenterZ=0 NormalX=0 NormalY=0 NormalZ=1 AngleXU=0 Radius=1
    g35: Circle CenterX=-10.1571 CenterY=-16 CenterZ=0 NormalX=0 NormalY=0 NormalZ=1 AngleXU=0 Radius=1
    g36: BSplineCurve PolesCount=3 KnotsCount=2 Degree=2 IsPeriodic=0
    g37: GeomPoint X=-8.70761 Y=-14 Z=0
    g38: GeomPoint X=-10.1571 Y=-16 Z=0
    g39: Circle CenterX=-12.8401 CenterY=-17.6958 CenterZ=0 NormalX=0 NormalY=0 NormalZ=1 AngleXU=0 Radius=1
    g40: Circle CenterX=-13.3521 CenterY=-17.9027 CenterZ=0 NormalX=0 NormalY=0 NormalZ=1 AngleXU=0 Radius=1
    g41: Circle CenterX=-14 CenterY=-18 CenterZ=0 NormalX=0 NormalY=0 NormalZ=1 AngleXU=0 Radius=1
    g42: BSplineCurve PolesCount=3 KnotsCount=2 Degree=2 IsPeriodic=0
    g43: GeomPoint X=-12.8401 Y=-17.6958 Z=0
    g44: GeomPoint X=-14 Y=-18 Z=0
    g45: LineSegment StartX=-6.2 StartY=0 StartZ=0 EndX=-7.2 EndY=0 EndZ=0
    g46: LineSegment StartX=-7.2 StartY=0 StartZ=0 EndX=-7.2 EndY=-2 EndZ=0
    g47: LineSegment StartX=-7.2 StartY=-2 StartZ=0 EndX=-6.2215 EndY=-2 EndZ=0
    g48: LineSegment StartX=-6.32538 StartY=-4 StartZ=0 EndX=-7.65538 EndY=-4 EndZ=0
    g49: LineSegment StartX=-7.65538 StartY=-4 StartZ=0 EndX=-7.65538 EndY=-5.99526 EndZ=0
    g50: LineSegment StartX=-7.65538 StartY=-5.99526 StartZ=0 EndX=-6.48644 EndY=-5.99526 EndZ=0
    g51: LineSegment StartX=-6.77343 StartY=-8 StartZ=0 EndX=-8.43343 EndY=-8 EndZ=0
    g52: LineSegment StartX=-8.43343 StartY=-8 StartZ=0 EndX=-8.43343 EndY=-10 EndZ=0
    g53: LineSegment StartX=-8.43343 StartY=-10 StartZ=0 EndX=-7.19003 EndY=-10 EndZ=0
  constraints (112):
    c: Horizontal(g0)
    c: Distance(g0) = 2
    c: Block(g0)
    c: Vertical(g1)
    c: Coincident(g2,g0)
    c: Vertical(g2)
    c: Block(g2)
    c: Coincident(g6,g2)
    c: Weight(g3) = 1
    c: Equal(g3,g4)
    c: Equal(g3,g5)
    c: InternalAlignment(g3,g6)
    c: InternalAlignment(g4,g6)
    c: InternalAlignment(g5,g6)
    c: InternalAlignment(g7,g6)
    c: InternalAlignment(g8,g6)
    c: Block(g6)
    c: Coincident(g9,g1)
    c: Coincident(g9,g6)
    c: Horizontal(g9)
    c: Vertical(g10)
    c: Block(g10)
    c: Horizontal(g11)
    c: Block(g11)
    c: Coincident(g12,g10)
    c: Horizontal(g12)
    c: Block(g12)
    c: Coincident(g13,g11)
    c: Vertical(g13)
    c: Block(g13)
    c: Coincident(g14,g10)
    c: Horizontal(g14)
    c: Block(g14)
    c: Block(g9)
    c: Block(g1)
    c: Weight(g15) = 1
    c: Equal(g15,g16)
    c: Equal(g15,g17)
    c: InternalAlignment(g15,g18)
    c: InternalAlignment(g16,g18)
    c: InternalAlignment(g17,g18)
    c: InternalAlignment(g19,g18)
    c: InternalAlignment(g20,g18)
    c: Weight(g21) = 1
    c: Equal(g21,g22)
    c: Equal(g21,g23)
    c: InternalAlignment(g21,g24)
    c: InternalAlignment(g22,g24)
    c: InternalAlignment(g23,g24)
    c: InternalAlignment(g25,g24)
    c: InternalAlignment(g26,g24)
    c: Weight(g27) = 1
    c: Equal(g27,g28)
    c: Equal(g27,g29)
    c: Coincident(g30,g14)
    c: InternalAlignment(g27,g30)
    c: InternalAlignment(g28,g30)
    c: InternalAlignment(g29,g30)
    c: InternalAlignment(g31,g30)
    c: InternalAlignment(g32,g30)
    c: Coincident(g36,g12)
    c: Weight(g33) = 1
    c: Equal(g33,g34)
    c: Equal(g33,g35)
    c: Coincident(g36,g11)
    c: InternalAlignment(g33,g36)
    c: InternalAlignment(g34,g36)
    c: InternalAlignment(g35,g36)
    c: InternalAlignment(g37,g36)
    c: InternalAlignment(g38,g36)
    c: Coincident(g42,g13)
    c: Weight(g39) = 1
    c: Equal(g39,g40)
    c: Equal(g39,g41)
    c: Coincident(g42,g1)
    c: InternalAlignment(g39,g42)
    c: InternalAlignment(g40,g42)
    c: InternalAlignment(g41,g42)
    c: InternalAlignment(g43,g42)
    c: InternalAlignment(g44,g42)
    c: Block(g18)
    c: Block(g24)
    c: Block(g30)
    c: Block(g36)
    c: Block(g42)
    c: Horizontal(g45)
    c: Coincident(g45,g0)
    c: Vertical(g46)
    c: Coincident(g46,g45)
    c: Coincident(g47,g46)
    c: Coincident(g47,g18)
    c: Horizontal(g47)
    c: Block(g46)
    c: Coincident(g48,g18)
    c: Horizontal(g48)
    c: Distance(g48) = 1.33
    c: Vertical(g49)
    c: Coincident(g49,g48)
    c: Coincident(g50,g49)
    c: Coincident(g50,g24)
    c: Horizontal(g50)
    c: Tangent(g50,g22)
    c: Horizontal(g51)
    c: Coincident(g51,g24)
    c: Block(g51)
    c: Vertical(g52)
    c: Block(g52)
    c: Coincident(g52,g51)
    c: Coincident(g53,g52)
    c: Coincident(g53,g30)
    c: Horizontal(g53)
    c: Distance(g1) = 8.5
FEATURE [Part::Feature] Face024
  shape: bbox 9.8 x 26.5 x 2e-07 mm, 1 faces, 0 solids (baked)
FEATURE [Part::Revolution] Revolve024
  Angle = 360
  Axis = (0,1,0)
  Base = (0,0,0)
  FaceMakerClass = Part::FaceMakerBullseye
  Placement = pos=(0,0,0) rot=(0,0,1;1.5708rad)
  Solid = false
  Source = -> Face024
  Symmetric = false
FEATURE [Part::Feature] Face025
  shape: bbox 9.8 x 26.5 x 2e-07 mm, 1 faces, 0 solids (baked)
FEATURE [Part::Revolution] Revolve025
  Angle = 360
  Axis = (0,1,0)
  Base = (0,0,0)
  FaceMakerClass = Part::FaceMakerBullseye
  Placement = pos=(0,0,0) rot=(0,0,1;1.5708rad)
  Solid = false
  Source = -> Face025
  Symmetric = false
FEATURE [Part::MultiFuse] Fusion033
  Placement = pos=(-18,19,36) rot=(0,0,1;0rad)
  Shapes = -> [Revolve025,Revolve024]
FEATURE [Part::Cylinder] Cylinder014
  Angle = 360
  AttacherType = Attacher::AttachEngine3D
  Height = 20
  Placement = pos=(0,0,36.15) rot=(0,0,1;0rad)
  Radius = 14.3
FEATURE [Part::Cylinder] Cylinder015
  Angle = 360
  AttacherType = Attacher::AttachEngine3D
  Height = 10
  Placement = pos=(0,0,36.15) rot=(0,0,1;0rad)
  Radius = 4
FEATURE [Part::MultiFuse] Fusion034  label="removeToCreteHoleForPlugHousing004"
  Placement = pos=(-42,19,36) rot=(0,1,0;1.5708rad)
  Shapes = -> [Cylinder014,Cylinder015]
FEATURE [Part::Cut] Cut008  label="top004"
  Base = -> Cut004
  Placement = pos=(-1,0,0) rot=(0,0,1;0rad)
  Tool = -> Fusion034
FEATURE [Part::Box] Box005  label="Cube005"
  AttacherType = Attacher::AttachEngine3D
  Height = 28
  Length = 3
  Placement = pos=(110.7,19,22) rot=(0,0,1;0rad)
  Width = 15.7
FEATURE [Part::Cylinder] Cylinder016
  Angle = 360
  AttacherType = Attacher::AttachEngine3D
  Height = 10
  Placement = pos=(0,0,36.15) rot=(0,0,1;0rad)
  Radius = 4
FEATURE [Part::Cylinder] Cylinder017
  Angle = 360
  AttacherType = Attacher::AttachEngine3D
  Height = 20
  Placement = pos=(0,0,36.15) rot=(0,0,1;0rad)
  Radius = 10.3
FEATURE [Part::MultiFuse] Fusion035  label="removeToCreteHoleForPlugHousing005"
  Placement = pos=(70,19,36) rot=(0,1,0;1.5708rad)
  Shapes = -> [Cylinder017,Cylinder016]
FEATURE [Part::Cut] Cut009  label="plugHousingTab001"
  Base = -> Box005
  Placement = pos=(-107.4,-14,0) rot=(0,0,1;0rad)
  Tool = -> Fusion035
FEATURE [Part::Box] Box006  label="Cube006"
  AttacherType = Attacher::AttachEngine3D
  Height = 28
  Length = 3
  Placement = pos=(110.7,19,22) rot=(0,0,1;0rad)
  Width = 15.7
FEATURE [Part::Cylinder] Cylinder018
  Angle = 360
  AttacherType = Attacher::AttachEngine3D
  Height = 10
  Placement = pos=(0,0,36.15) rot=(0,0,1;0rad)
  Radius = 4
FEATURE [Part::Cylinder] Cylinder019
  Angle = 360
  AttacherType = Attacher::AttachEngine3D
  Height = 20
  Placement = pos=(0,0,36.15) rot=(0,0,1;0rad)
  Radius = 10.3
FEATURE [Part::MultiFuse] Fusion036  label="removeToCreteHoleForPlugHousing006"
  Placement = pos=(70,19,36) rot=(0,1,0;1.5708rad)
  Shapes = -> [Cylinder019,Cylinder018]
FEATURE [Part::Cut] Cut010  label="plugHousingTab002"
  Base = -> Box006
  Placement = pos=(-107.4,-14,0) rot=(0,0,1;0rad)
  Tool = -> Fusion036
FEATURE [Part::MultiFuse] Fusion037
  Placement = pos=(9.6,23,0) rot=(0,0,1;3.14159rad)
  Shapes = -> [Cut009,Cut010]
FEATURE [Part::Box] Box  label="Cube"
  AttacherType = Attacher::AttachEngine3D
  Height = 10
  Length = 3
  Placement = pos=(3.3,4,12) rot=(0,0,1;0rad)
  Width = 10
FEATURE [Part::Fillet] Fillet004
  Base = -> Fusion028
  Edges = 1 edges r=2: [Edge25]
FEATURE [Part::Fillet] Fillet005  label="plugHousing046"
  Base = -> Fillet004
  Edges = 1 edges r=2: [Edge8]
FEATURE [Part::Fillet] Fillet006
  Base = -> Box
  Edges = 1 edges r=2: [Edge11]
FEATURE [Part::Box] Box007  label="Cube007"
  AttacherType = Attacher::AttachEngine3D
  Height = 10
  Length = 3
  Placement = pos=(3.3,4,50) rot=(0,0,1;0rad)
  Width = 10
FEATURE [Part::Fillet] Fillet007
  Base = -> Box007
  Edges = 1 edges r=2: [Edge12]
FEATURE [Part::Box] Box008  label="Cube008"
  AttacherType = Attacher::AttachEngine3D
  Height = 28
  Length = 4
  Placement = pos=(5,0,22) rot=(0,0,1;0rad)
  Width = 10
FEATURE [Part::Fillet] Fillet008
  Base = -> Box008
  Edges = 1 edges r=1: [Edge7]
FEATURE [Part::Fillet] Fillet009
  Base = -> Fillet008
  Edges = 1 edges r=2: [Edge5]
FEATURE [Part::Fillet] Fillet010
  Base = -> Fillet009
  Edges = 1 edges r=2: [Edge2]
FEATURE [Sketcher::SketchObject] Sketch009  label="topSketch003"
  FullyConstrained = true
  sketch-geometry (4):
    g0: LineSegment StartX=16.8446 StartY=31.512 StartZ=0 EndX=16.3251 EndY=34.4666 EndZ=0
    g1: ArcOfCircle CenterX=19 CenterY=19.2524 CenterZ=0 NormalX=0 NormalY=0 NormalZ=1 AngleXU=0 Radius=15.4476 StartAngle=1.74483 EndAngle=2.72717
    g2: ArcOfCircle CenterX=19 CenterY=19.2524 CenterZ=0 NormalX=0 NormalY=0 NormalZ=1 AngleXU=0 Radius=12.4476 StartAngle=1.74483 EndAngle=2.73189
    g3: LineSegment StartX=4.86004 StartY=25.4725 StartZ=0 EndX=7.58253 EndY=24.2107 EndZ=0
  constraints (7):
    c: Block(g0)
    c: Coincident(g1,g0)
    c: Coincident(g2,g0)
    c: Coincident(g3,g1)
    c: Coincident(g3,g2)
    c: Block(g1)
    c: Block(g2)
FEATURE [Part::Extrusion] Extrude008
  Base = -> Sketch009
  Dir = (0,0,1)
  DirMode = 2
  FaceMakerClass = Part::FaceMakerBullseye
  LengthFwd = 10
  LengthRev = 0
  Placement = pos=(0,0,31) rot=(0,0,1;0rad)
  Solid = true
  Symmetric = false
FEATURE [Part::Cylinder] Cylinder020
  Angle = 360
  AttacherType = Attacher::AttachEngine3D
  Height = 20
  Placement = pos=(0,0,36.15) rot=(0,0,1;0rad)
  Radius = 8.2
FEATURE [Part::Cylinder] Cylinder021
  Angle = 360
  AttacherType = Attacher::AttachEngine3D
  Height = 10
  Placement = pos=(0,0,36.15) rot=(0,0,1;0rad)
  Radius = 4
FEATURE [Part::MultiFuse] Fusion038  label="removeToCreteHoleForPlugHousing007"
  Placement = pos=(-42,19,36) rot=(0,1,0;1.5708rad)
  Shapes = -> [Cylinder020,Cylinder021]
FEATURE [Part::Cut] Cut011
  Base = -> Extrude008
  Tool = -> Fusion038
FEATURE [Part::Fillet] Fillet011
  Base = -> Cut011
  Edges = 1 edges r=2: [Edge1]
FEATURE [Part::Fillet] Fillet012
  Base = -> Fillet011
  Edges = 1 edges r=2.5: [Edge1]
FEATURE [Part::Fillet] Fillet013
  Base = -> Fillet012
  Edges = 1 edges r=2.5: [Edge2]
FEATURE [Part::Box] Box010  label="Cube010"
  AttacherType = Attacher::AttachEngine3D
  Height = 16
  Length = 8
  Placement = pos=(12.7,31.52,28) rot=(0,0,1;0rad)
  Width = 4
FEATURE [Sketcher::SketchObject] Sketch010  label="topSketch004"
  FullyConstrained = true
  sketch-geometry (4):
    g0: LineSegment StartX=16.8446 StartY=31.512 StartZ=0 EndX=16.3251 EndY=34.4666 EndZ=0
    g1: ArcOfCircle CenterX=19 CenterY=19.2524 CenterZ=0 NormalX=0 NormalY=0 NormalZ=1 AngleXU=0 Radius=15.4476 StartAngle=1.74483 EndAngle=2.72717
    g2: ArcOfCircle CenterX=19 CenterY=19.2524 CenterZ=0 NormalX=0 NormalY=0 NormalZ=1 AngleXU=0 Radius=12.4476 StartAngle=1.74483 EndAngle=2.73189
    g3: LineSegment StartX=4.86004 StartY=25.4725 StartZ=0 EndX=7.58253 EndY=24.2107 EndZ=0
  constraints (7):
    c: Block(g0)
    c: Coincident(g1,g0)
    c: Coincident(g2,g0)
    c: Coincident(g3,g1)
    c: Coincident(g3,g2)
    c: Block(g1)
    c: Block(g2)
FEATURE [Part::Cylinder] Cylinder022
  Angle = 360
  AttacherType = Attacher::AttachEngine3D
  Height = 10
  Placement = pos=(0,0,36.15) rot=(0,0,1;0rad)
  Radius = 4
FEATURE [Sketcher::SketchObject] Sketch011  label="topSketch005"
  FullyConstrained = true
  sketch-geometry (4):
    g0: LineSegment StartX=16.8446 StartY=31.512 StartZ=0 EndX=16.3251 EndY=34.4666 EndZ=0
    g1: ArcOfCircle CenterX=19 CenterY=19.2524 CenterZ=0 NormalX=0 NormalY=0 NormalZ=1 AngleXU=0 Radius=15.4476 StartAngle=1.74483 EndAngle=2.72717
    g2: ArcOfCircle CenterX=19 CenterY=19.2524 CenterZ=0 NormalX=0 NormalY=0 NormalZ=1 AngleXU=0 Radius=12.4476 StartAngle=1.74483 EndAngle=2.73189
    g3: LineSegment StartX=4.86004 StartY=25.4725 StartZ=0 EndX=7.58253 EndY=24.2107 EndZ=0
  constraints (7):
    c: Block(g0)
    c: Coincident(g1,g0)
    c: Coincident(g2,g0)
    c: Coincident(g3,g1)
    c: Coincident(g3,g2)
    c: Block(g1)
    c: Block(g2)
FEATURE [Part::Extrusion] Extrude010
  Base = -> Sketch011
  Dir = (0,0,1)
  DirMode = 2
  FaceMakerClass = Part::FaceMakerBullseye
  LengthFwd = 10.6
  LengthRev = 0
  Placement = pos=(0,0,31) rot=(0,0,1;0rad)
  Solid = true
  Symmetric = false
FEATURE [Part::Cylinder] Cylinder023
  Angle = 360
  AttacherType = Attacher::AttachEngine3D
  Height = 20
  Placement = pos=(0,0,36.15) rot=(0,0,1;0rad)
  Radius = 8.2
FEATURE [Part::MultiFuse] Fusion039  label="removeToCreteHoleForPlugHousing008"
  Placement = pos=(-42,19,36) rot=(0,1,0;1.5708rad)
  Shapes = -> [Cylinder023,Cylinder022]
FEATURE [Part::Cut] Cut012
  Base = -> Extrude010
  Placement = pos=(0,0,-0.3) rot=(0,0,1;0rad)
  Tool = -> Fusion039
FEATURE [Part::Cut] Cut013
  Base = -> Box010
  Tool = -> Cut012
FEATURE [Part::Fillet] Fillet014
  Base = -> Cut013
  Edges = 1 edges r=0.7: [Edge13]
FEATURE [Part::Fillet] Fillet015
  Base = -> Fillet014
  Edges = 1 edges r=0.7: [Edge13]
FEATURE [Part::Fillet] Fillet016
  Base = -> Fillet015
  Edges = 1 edges r=0.7: [Edge16]
FEATURE [Part::Fillet] Fillet017
  Base = -> Fillet016
  Edges = 1 edges r=0.7: [Edge11]
FEATURE [Part::Fillet] Fillet018
  Base = -> Fillet017
  Edges = 1 edges r=0.7: [Edge10]
FEATURE [Part::Fillet] Fillet019
  Base = -> Fillet018
  Edges = 1 edges r=1.2: [Edge5]
FEATURE [Part::Fillet] Fillet020
  Base = -> Fillet019
  Edges = 1 edges r=1.2: [Edge12]
FEATURE [Part::Fillet] Fillet021
  Base = -> Fillet020
  Edges = 1 edges r=2: [Edge1]
  Placement = pos=(0.3,0,0) rot=(0,0,1;0rad)
FEATURE [Part::MultiFuse] Fusion040  label="top005"
  Shapes = -> [Cut008,Fillet021]
FEATURE [Part::MultiFuse] Fusion041  label="wireHolder"
  Shapes = -> [Fusion033,Fillet013]
FEATURE [Part::MultiFuse] Fusion042
  Shapes = -> [Fillet007,Fusion041]
FEATURE [Part::MultiFuse] Fusion043  label="wireHolder001"
  Shapes = -> [Fusion042,Fillet010]
FEATURE [Part::MultiFuse] Fusion044  label="wireHolder002"
  Shapes = -> [Fillet006,Fusion037,Fusion043]
FEATURE [Part::Feature] Face026
  shape: bbox 11 x 6 x 2e-07 mm, 1 faces, 0 solids (baked)
FEATURE [Part::Revolution] Revolve026
  Angle = 360
  Axis = (0,1,0)
  Base = (0,0,0)
  FaceMakerClass = Part::FaceMakerBullseye
  Placement = pos=(30.3,-1,19.7) rot=(0,0,1;0rad)
  Solid = false
  Source = -> Face026
  Symmetric = false
FEATURE [Sketcher::SketchObject] Sketch013  label="topSketch006"
  FullyConstrained = true
  sketch-geometry (13):
    g0: LineSegment StartX=117 StartY=19 StartZ=0 EndX=117 EndY=38 EndZ=0
    g1: ArcOfCircle CenterX=98 CenterY=19 CenterZ=0 NormalX=0 NormalY=0 NormalZ=1 AngleXU=0 Radius=19 StartAngle=5.7297 EndAngle=6.28319
    g2: LineSegment StartX=0 StartY=3 StartZ=0 EndX=0 EndY=19 EndZ=0
    g3: LineSegment StartX=19 StartY=38 StartZ=0 EndX=117 EndY=38 EndZ=0
    g4: ArcOfCircle CenterX=19 CenterY=19 CenterZ=0 NormalX=0 NormalY=0 NormalZ=1 AngleXU=0 Radius=19 StartAngle=1.5708 EndAngle=3.14159
    g5: ArcOfCircle CenterX=19 CenterY=19 CenterZ=0 NormalX=0 NormalY=0 NormalZ=1 AngleXU=0 Radius=16 StartAngle=1.5708 EndAngle=3.14159
    g6: ArcOfCircle CenterX=98 CenterY=19 CenterZ=0 NormalX=0 NormalY=0 NormalZ=1 AngleXU=0 Radius=16 StartAngle=5.60905 EndAngle=6.28319
    g7: LineSegment StartX=114 StartY=19 StartZ=0 EndX=114 EndY=35 EndZ=0
    g8: LineSegment StartX=110.5 StartY=9.01251 StartZ=0 EndX=114.163 EndY=9.01251 EndZ=0
    g9: LineSegment StartX=114 StartY=35 StartZ=0 EndX=19 EndY=35 EndZ=0
    g10: LineSegment StartX=0 StartY=3 StartZ=0 EndX=0 EndY=0 EndZ=0
    g11: LineSegment StartX=3 StartY=0 StartZ=0 EndX=0 EndY=0 EndZ=0
    g12: LineSegment StartX=3 StartY=19 StartZ=0 EndX=3 EndY=0 EndZ=0
  constraints (33):
    c: Vertical(g0)
    c: Distance(g0) = 19
    c: Block(g0)
    c: Coincident(g1,g0)
    c: Block(g1)
    c: Vertical(g2)
    c: Block(g2)
    c: Coincident(g3,g0)
    c: Horizontal(g3)
    c: Distance(g3) = 98
    c: Coincident(g4,g3)
    c: Coincident(g4,g2)
    c: Block(g4)
    c: Coincident(g5,g4)
    c: Coincident(g6,g1)
    c: Block(g6)
    c: Block(g5)
    c: Coincident(g7,g6)
    c: Vertical(g7)
    c: Coincident(g8,g6)
    c: Coincident(g8,g1)
    c: Coincident(g9,g7)
    c: Coincident(g9,g5)
    c: Horizontal(g9)
    c: Tangent(g9,g5)
    c: Coincident(g10,g2)
    c: Distance(g10) = 3
    c: Vertical(g10)
    c: Coincident(g11,g10)
    c: Horizontal(g11)
    c: Coincident(g12,g5)
    c: Coincident(g12,g11)
    c: Vertical(g12)
FEATURE [Part::Extrusion] Extrude011  label="top006"
  Base = -> Sketch013
  Dir = (0,0,1)
  DirMode = 2
  FaceMakerClass = Part::FaceMakerBullseye
  LengthFwd = 72
  LengthRev = 0
  Solid = true
  Symmetric = false
FEATURE [Sketcher::SketchObject] Sketch014
  FullyConstrained = true
  MapMode = 3
  Placement = pos=(0,0,0) rot=(1,0,0;1.5708rad)
  Support = -> [Extrude011]
  sketch-geometry (8):
    g0: Circle CenterX=80.351 CenterY=-67.6202 CenterZ=0 NormalX=0 NormalY=0 NormalZ=1 AngleXU=0 Radius=2
    g1: Circle CenterX=80.351 CenterY=-67.6202 CenterZ=0 NormalX=0 NormalY=0 NormalZ=1 AngleXU=0 Radius=3
    g2: Circle CenterX=80.351 CenterY=-4.92017 CenterZ=0 NormalX=0 NormalY=0 NormalZ=1 AngleXU=0 Radius=2
    g3: Circle CenterX=80.351 CenterY=-4.92017 CenterZ=0 NormalX=0 NormalY=0 NormalZ=1 AngleXU=0 Radius=3
    g4: Circle CenterX=23.851 CenterY=-4.92017 CenterZ=0 NormalX=0 NormalY=0 NormalZ=1 AngleXU=0 Radius=2
    g5: Circle CenterX=23.851 CenterY=-4.92017 CenterZ=0 NormalX=0 NormalY=0 NormalZ=1 AngleXU=0 Radius=3
    g6: Circle CenterX=23.851 CenterY=-67.6202 CenterZ=0 NormalX=0 NormalY=0 NormalZ=1 AngleXU=0 Radius=2
    g7: Circle CenterX=23.851 CenterY=-67.6202 CenterZ=0 NormalX=0 NormalY=0 NormalZ=1 AngleXU=0 Radius=3
  constraints (8):
    c: Block(g3)
    c: Block(g2)
    c: Block(g1)
    c: Block(g0)
    c: Block(g6)
    c: Block(g7)
    c: Block(g4)
    c: Block(g5)
FEATURE [Part::Feature] Face027
  shape: bbox 11 x 6 x 2e-07 mm, 1 faces, 0 solids (baked)
FEATURE [Part::Revolution] Revolve027
  Angle = 360
  Axis = (0,1,0)
  Base = (0,0,0)
  FaceMakerClass = Part::FaceMakerBullseye
  Placement = pos=(30.3,-1,51.7) rot=(0,0,1;0rad)
  Solid = false
  Source = -> Face027
  Symmetric = false
FEATURE [Part::Feature] Face028
  shape: bbox 11 x 6 x 2e-07 mm, 1 faces, 0 solids (baked)
FEATURE [Part::Revolution] Revolve028
  Angle = 360
  Axis = (0,1,0)
  Base = (0,0,0)
  FaceMakerClass = Part::FaceMakerBullseye
  Placement = pos=(62.3,-1,19.7) rot=(0,0,1;0rad)
  Solid = false
  Source = -> Face028
  Symmetric = false
FEATURE [Part::Feature] Face029
  shape: bbox 11 x 6 x 2e-07 mm, 1 faces, 0 solids (baked)
FEATURE [Part::Revolution] Revolve029
  Angle = 360
  Axis = (0,1,0)
  Base = (0,0,0)
  FaceMakerClass = Part::FaceMakerBullseye
  Placement = pos=(62.3,-1,51.7) rot=(0,0,1;0rad)
  Solid = false
  Source = -> Face029
  Symmetric = false
FEATURE [Part::Feature] Wire
  shape: bbox 11 x 5.2 x 2e-07 mm, 0 faces, 0 solids (baked)
FEATURE [Part::Revolution] Revolve030
  Angle = 360
  Axis = (0,1,0)
  Base = (0,0,0)
  FaceMakerClass = Part::FaceMakerBullseye
  Placement = pos=(30.3,38,19.7) rot=(0,0,1;0rad)
  Solid = true
  Source = -> Wire
  Symmetric = false
FEATURE [Part::Feature] Wire001
  shape: bbox 11 x 5.2 x 2e-07 mm, 0 faces, 0 solids (baked)
FEATURE [Part::Revolution] Revolve031
  Angle = 360
  Axis = (0,1,0)
  Base = (0,0,0)
  FaceMakerClass = Part::FaceMakerBullseye
  Placement = pos=(30.3,38,51.7) rot=(0,0,1;0rad)
  Solid = true
  Source = -> Wire001
  Symmetric = false
FEATURE [Part::Feature] Wire002
  shape: bbox 11 x 5.2 x 2e-07 mm, 0 faces, 0 solids (baked)
FEATURE [Part::Revolution] Revolve032
  Angle = 360
  Axis = (0,1,0)
  Base = (0,0,0)
  FaceMakerClass = Part::FaceMakerBullseye
  Placement = pos=(62.3,38,51.7) rot=(0,0,1;0rad)
  Solid = true
  Source = -> Wire002
  Symmetric = false
FEATURE [Part::Feature] Wire003
  shape: bbox 11 x 5.2 x 2e-07 mm, 0 faces, 0 solids (baked)
FEATURE [Part::Revolution] Revolve033
  Angle = 360
  Axis = (0,1,0)
  Base = (0,0,0)
  FaceMakerClass = Part::FaceMakerBullseye
  Placement = pos=(62.3,38,19.7) rot=(0,0,1;0rad)
  Solid = true
  Source = -> Wire003
  Symmetric = false
FEATURE [Part::MultiFuse] Fusion045  label="altRandScrewHousing"
  Shapes = -> [Revolve029,Revolve027,Revolve028,Revolve026]
FEATURE [Part::MultiFuse] Fusion046  label="fanScrewHousing"
  Shapes = -> [Revolve033,Revolve032,Revolve031,Revolve030]
FEATURE [Sketcher::SketchObject] Sketch015
  FullyConstrained = true
  sketch-geometry (17):
    g0: Circle CenterX=-3.5 CenterY=23.5 CenterZ=0 NormalX=0 NormalY=0 NormalZ=1 AngleXU=0 Radius=1
    g1: Circle CenterX=-1 CenterY=15.25 CenterZ=0 NormalX=0 NormalY=0 NormalZ=1 AngleXU=0 Radius=1
    g2: Circle CenterX=-3.5 CenterY=7 CenterZ=0 NormalX=0 NormalY=0 NormalZ=1 AngleXU=0 Radius=1
    g3: BSplineCurve PolesCount=3 KnotsCount=2 Degree=2 IsPeriodic=0
    g4: GeomPoint X=-3.5 Y=23.5 Z=0
    g5: GeomPoint X=-3.5 Y=7 Z=0
    g6: Circle CenterX=-4.8 CenterY=30.5 CenterZ=0 NormalX=0 NormalY=0 NormalZ=1 AngleXU=0 Radius=1
    g7: Circle CenterX=-3.5 CenterY=30.5 CenterZ=0 NormalX=0 NormalY=0 NormalZ=1 AngleXU=0 Radius=1
    g8: Circle CenterX=-3.5 CenterY=29.2 CenterZ=0 NormalX=0 NormalY=0 NormalZ=1 AngleXU=0 Radius=1
    g9: BSplineCurve PolesCount=3 KnotsCount=2 Degree=2 IsPeriodic=0
    g10: GeomPoint X=-4.8 Y=30.5 Z=0
    g11: GeomPoint X=-3.5 Y=29.2 Z=0
    g12: LineSegment StartX=-3.5 StartY=29.2 StartZ=0 EndX=-3.5 EndY=23.5 EndZ=0
    g13: LineSegment StartX=-4.8 StartY=30.5 StartZ=0 EndX=0 EndY=30.5 EndZ=0
    g14: LineSegment StartX=-3.5 StartY=0.3 StartZ=0 EndX=0 EndY=0.3 EndZ=0
    g15: LineSegment StartX=-3.5 StartY=0.3 StartZ=0 EndX=-3.5 EndY=7 EndZ=0
    g16: LineSegment StartX=0 StartY=0.3 StartZ=0 EndX=0 EndY=30.5 EndZ=0
  constraints (33):
    c: Weight(g0) = 1
    c: Equal(g0,g1)
    c: Equal(g0,g2)
    c: InternalAlignment(g0,g3)
    c: InternalAlignment(g1,g3)
    c: InternalAlignment(g2,g3)
    c: InternalAlignment(g4,g3)
    c: InternalAlignment(g5,g3)
    c: Block(g3)
    c: Weight(g6) = 1
    c: Equal(g6,g7)
    c: Equal(g6,g8)
    c: InternalAlignment(g6,g9)
    c: InternalAlignment(g7,g9)
    c: InternalAlignment(g8,g9)
    c: InternalAlignment(g10,g9)
    c: InternalAlignment(g11,g9)
    c: Block(g9)
    c: Coincident(g12,g9)
    c: Coincident(g12,g3)
    c: Vertical(g12)
    c: Coincident(g13,g9)
    c: Horizontal(g13)
    c: Distance(g13) = 4.8
    c: Horizontal(g14)
    c: Block(g14)
    c: Coincident(g15,g14)
    c: Coincident(g15,g3)
    c: Vertical(g15)
    c: Coincident(g16,g14)
    c: Coincident(g16,g13)
    c: Vertical(g16)
    c: Tangent(g16,g1)
FEATURE [Sketcher::SketchObject] Sketch016
  FullyConstrained = true
  sketch-geometry (16):
    g0: Circle CenterX=-3.5 CenterY=23.5 CenterZ=0 NormalX=0 NormalY=0 NormalZ=1 AngleXU=0 Radius=1
    g1: Circle CenterX=-1 CenterY=15.25 CenterZ=0 NormalX=0 NormalY=0 NormalZ=1 AngleXU=0 Radius=1
    g2: Circle CenterX=-3.5 CenterY=7 CenterZ=0 NormalX=0 NormalY=0 NormalZ=1 AngleXU=0 Radius=1
    g3: BSplineCurve PolesCount=3 KnotsCount=2 Degree=2 IsPeriodic=0
    g4: GeomPoint X=-3.5 Y=23.5 Z=0
    g5: GeomPoint X=-3.5 Y=7 Z=0
    g6: LineSegment StartX=-3.5 StartY=28.2 StartZ=0 EndX=-3.5 EndY=23.5 EndZ=0
    g7: LineSegment StartX=0 StartY=29.5 StartZ=0 EndX=0 EndY=30 EndZ=0
    g8: LineSegment StartX=-3.5 StartY=28.2 StartZ=0 EndX=-3.5 EndY=30 EndZ=0
    g9: LineSegment StartX=0 StartY=30 StartZ=0 EndX=0 EndY=30.5 EndZ=0
    g10: LineSegment StartX=0 StartY=30.5 StartZ=0 EndX=-3.5 EndY=30.5 EndZ=0
    g11: LineSegment StartX=-3.5 StartY=30.5 StartZ=0 EndX=-3.5 EndY=30 EndZ=0
    g12: LineSegment StartX=0 StartY=29.5 StartZ=0 EndX=0 EndY=5 EndZ=0
    g13: LineSegment StartX=-3.5 StartY=0.3 StartZ=0 EndX=-3.5 EndY=7 EndZ=0
    g14: LineSegment StartX=-3.5 StartY=0.3 StartZ=0 EndX=0 EndY=0.3 EndZ=0
    g15: LineSegment StartX=0 StartY=5 StartZ=0 EndX=0 EndY=0.3 EndZ=0
  constraints (39):
    c: Weight(g0) = 1
    c: Equal(g0,g1)
    c: Equal(g0,g2)
    c: InternalAlignment(g0,g3)
    c: InternalAlignment(g1,g3)
    c: InternalAlignment(g2,g3)
    c: InternalAlignment(g4,g3)
    c: InternalAlignment(g5,g3)
    c: Block(g3)
    c: Coincident(g6,g3)
    c: Vertical(g6)
    c: Vertical(g7)
    c: Distance(g7) = 0.5
    c: Coincident(g8,g6)
    c: Vertical(g8)
    c: Block(g6)
    c: Block(g7)
    c: Vertical(g9)
    c: Equal(g7,g9) = 0.5
    c: Block(g9)
    c: Coincident(g9,g7)
    c: Horizontal(g10)
    c: Coincident(g10,g9)
    c: Coincident(g11,g10)
    c: Coincident(g11,g8)
    c: Vertical(g11)
    c: Block(g11)
    c: Coincident(g12,g7)
    c: Vertical(g12)
    c: Coincident(g13,g3)
    c: Vertical(g13)
    c: Distance(g13) = 6.7
    c: Coincident(g14,g13)
    c: Horizontal(g14)
    c: Block(g14)
    c: Coincident(g15,g12)
    c: Coincident(g15,g14)
    c: Vertical(g15)
    c: Block(g15)
FEATURE [Sketcher::SketchObject] Sketch017
  FullyConstrained = true
  sketch-geometry (11):
    g0: LineSegment StartX=-3.5 StartY=1e-16 StartZ=0 EndX=-1.6 EndY=1e-16 EndZ=0
    g1: LineSegment StartX=-1.6 StartY=1e-16 StartZ=0 EndX=-1.6 EndY=1.5 EndZ=0
    g2: LineSegment StartX=-3.5 StartY=1.5 StartZ=0 EndX=-1.6 EndY=1.5 EndZ=0
    g3: LineSegment StartX=-3.5 StartY=1e-16 StartZ=0 EndX=-4.8 EndY=1e-16 EndZ=0
    g4: Circle CenterX=-3.5 CenterY=1.3 CenterZ=0 NormalX=0 NormalY=0 NormalZ=1 AngleXU=0 Radius=1
    g5: Circle CenterX=-3.5 CenterY=1e-16 CenterZ=0 NormalX=0 NormalY=0 NormalZ=1 AngleXU=0 Radius=1
    g6: Circle CenterX=-4.8 CenterY=1e-16 CenterZ=0 NormalX=0 NormalY=0 NormalZ=1 AngleXU=0 Radius=1
    g7: BSplineCurve PolesCount=3 KnotsCount=2 Degree=2 IsPeriodic=0
    g8: GeomPoint X=-3.5 Y=1.3 Z=0
    g9: GeomPoint X=-4.8 Y=1e-16 Z=0
    g10: LineSegment StartX=-3.5 StartY=1.3 StartZ=0 EndX=-3.5 EndY=1.5 EndZ=0
  constraints (24):
    c: Horizontal(g0)
    c: Distance(g0) = 1.9
    c: Block(g0)
    c: Coincident(g1,g0)
    c: Vertical(g1)
    c: Coincident(g2,g1)
    c: Horizontal(g2)
    c: Coincident(g3,g0)
    c: Horizontal(g3)
    c: Distance(g3) = 1.3
    c: Weight(g4) = 1
    c: Equal(g4,g5)
    c: Coincident(g5,g0)
    c: Equal(g4,g6)
    c: Coincident(g7,g3)
    c: InternalAlignment(g4,g7)
    c: InternalAlignment(g5,g7)
    c: InternalAlignment(g6,g7)
    c: InternalAlignment(g8,g7)
    c: InternalAlignment(g9,g7)
    c: Coincident(g10,g7)
    c: Coincident(g10,g2)
    c: Vertical(g10)
    c: Block(g10)
FEATURE [Part::Feature] Face035
  shape: bbox 3.2 x 1.5 x 2e-07 mm, 1 faces, 0 solids (baked)
FEATURE [Part::Revolution] Revolve039  label="backCaseScrewRetainer"
  Angle = 360
  Axis = (0,1,0)
  Base = (0,0,0)
  FaceMakerClass = Part::FaceMakerBullseye
  Placement = pos=(12.5,3,62) rot=(0,0,1;0rad)
  Solid = false
  Source = -> Face035
  Symmetric = false
FEATURE [Part::Feature] Face036
  shape: bbox 3.2 x 1.5 x 2e-07 mm, 1 faces, 0 solids (baked)
FEATURE [Part::Feature] Face039
  shape: bbox 4.8 x 30.2 x 2e-07 mm, 1 faces, 0 solids (baked)
FEATURE [Part::Revolution] Revolve043  label="frontCaseScrewPost002"
  Angle = 360
  Axis = (0,1,0)
  Base = (0,0,0)
  FaceMakerClass = Part::FaceMakerBullseye
  Placement = pos=(89.5,4.5,3.5) rot=(0,0,1;0rad)
  Solid = false
  Source = -> Face039
  Symmetric = false
FEATURE [Part::Feature] Face042
  shape: bbox 4.8 x 30.2 x 2e-07 mm, 1 faces, 0 solids (baked)
FEATURE [Part::Revolution] Revolve046  label="frontCaseScrewPost003"
  Angle = 360
  Axis = (0,1,0)
  Base = (0,0,0)
  FaceMakerClass = Part::FaceMakerBullseye
  Placement = pos=(89.5,4.5,68.5) rot=(0,0,1;0rad)
  Solid = false
  Source = -> Face042
  Symmetric = false
FEATURE [Part::Feature] Face043
  shape: bbox 3.2 x 1.5 x 2e-07 mm, 1 faces, 0 solids (baked)
FEATURE [Part::Revolution] Revolve047  label="frontCaseScrewRetainer002"
  Angle = 360
  Axis = (0,1,0)
  Base = (0,0,0)
  FaceMakerClass = Part::FaceMakerBullseye
  Placement = pos=(89.5,3,68.5) rot=(0,0,1;0rad)
  Solid = false
  Source = -> Face043
  Symmetric = false
FEATURE [Part::Feature] Face044
  shape: bbox 3.2 x 1.5 x 2e-07 mm, 1 faces, 0 solids (baked)
FEATURE [Part::Revolution] Revolve048  label="frontCaseScrewRetainer003"
  Angle = 360
  Axis = (0,1,0)
  Base = (0,0,0)
  FaceMakerClass = Part::FaceMakerBullseye
  Placement = pos=(89.5,3,3.5) rot=(0,0,1;0rad)
  Solid = false
  Source = -> Face044
  Symmetric = false
FEATURE [App::MeasureDistance] Distance002  label="Distance: 1.67 mm"
  Distance = 1.66921
  P1 = (99.2361,4.7524,71.7)
  P2 = (99.2347,6.42161,71.7)
FEATURE [Sketcher::SketchObject] Sketch018
  FullyConstrained = true
  sketch-geometry (7):
    g0: LineSegment StartX=0 StartY=0 StartZ=0 EndX=0 EndY=6 EndZ=0
    g1: Circle CenterX=0 CenterY=0 CenterZ=0 NormalX=0 NormalY=0 NormalZ=1 AngleXU=0 Radius=1
    g2: Circle CenterX=8 CenterY=6 CenterZ=0 NormalX=0 NormalY=0 NormalZ=1 AngleXU=0 Radius=1
    g3: BSplineCurve PolesCount=3 KnotsCount=2 Degree=2 IsPeriodic=0
    g4: GeomPoint X=0 Y=0 Z=0
    g5: GeomPoint X=8 Y=6 Z=0
    g6: LineSegment StartX=0 StartY=6 StartZ=0 EndX=8 EndY=6 EndZ=0
  constraints (14):
    c: Coincident(g0,g-1)
    c: Distance(g0) = 6
    c: Vertical(g0)
    c: Coincident(g3,g0)
    c: Weight(g1) = 1
    c: Equal(g1,g2)
    c: InternalAlignment(g1,g3)
    c: InternalAlignment(g2,g3)
    c: InternalAlignment(g4,g3)
    c: InternalAlignment(g5,g3)
    c: Block(g3)
    c: Coincident(g6,g0)
    c: Coincident(g6,g3)
    c: Horizontal(g6)
FEATURE [Part::Extrusion] Extrude012  label="caseScrewPillarBracket"
  Base = -> Sketch018
  Dir = (0,0,1)
  DirMode = 2
  FaceMakerClass = Part::FaceMakerBullseye
  LengthFwd = 2.4
  LengthRev = 0
  Placement = pos=(15.76,29,8.8) rot=(0,1,0;0rad)
  Solid = true
  Symmetric = false
FEATURE [Sketcher::SketchObject] Sketch019
  FullyConstrained = true
  sketch-geometry (7):
    g0: LineSegment StartX=0 StartY=0 StartZ=0 EndX=0 EndY=6 EndZ=0
    g1: Circle CenterX=0 CenterY=0 CenterZ=0 NormalX=0 NormalY=0 NormalZ=1 AngleXU=0 Radius=1
    g2: Circle CenterX=8 CenterY=6 CenterZ=0 NormalX=0 NormalY=0 NormalZ=1 AngleXU=0 Radius=1
    g3: BSplineCurve PolesCount=3 KnotsCount=2 Degree=2 IsPeriodic=0
    g4: GeomPoint X=0 Y=0 Z=0
    g5: GeomPoint X=8 Y=6 Z=0
    g6: LineSegment StartX=0 StartY=6 StartZ=0 EndX=8 EndY=6 EndZ=0
  constraints (14):
    c: Coincident(g0,g-1)
    c: Distance(g0) = 6
    c: Vertical(g0)
    c: Coincident(g3,g0)
    c: Weight(g1) = 1
    c: Equal(g1,g2)
    c: InternalAlignment(g1,g3)
    c: InternalAlignment(g2,g3)
    c: InternalAlignment(g4,g3)
    c: InternalAlignment(g5,g3)
    c: Block(g3)
    c: Coincident(g6,g0)
    c: Coincident(g6,g3)
    c: Horizontal(g6)
FEATURE [Part::Extrusion] Extrude013  label="caseScrewPillarBracket001"
  Base = -> Sketch019
  Dir = (0,0,1)
  DirMode = 2
  FaceMakerClass = Part::FaceMakerBullseye
  LengthFwd = 2.4
  LengthRev = 0
  Placement = pos=(15.76,29,60.8) rot=(0,0,1;0rad)
  Solid = true
  Symmetric = false
FEATURE [Sketcher::SketchObject] Sketch020
  FullyConstrained = true
  sketch-geometry (7):
    g0: LineSegment StartX=0 StartY=0 StartZ=0 EndX=0 EndY=6 EndZ=0
    g1: Circle CenterX=0 CenterY=0 CenterZ=0 NormalX=0 NormalY=0 NormalZ=1 AngleXU=0 Radius=1
    g2: Circle CenterX=8 CenterY=6 CenterZ=0 NormalX=0 NormalY=0 NormalZ=1 AngleXU=0 Radius=1
    g3: BSplineCurve PolesCount=3 KnotsCount=2 Degree=2 IsPeriodic=0
    g4: GeomPoint X=0 Y=0 Z=0
    g5: GeomPoint X=8 Y=6 Z=0
    g6: LineSegment StartX=0 StartY=6 StartZ=0 EndX=8 EndY=6 EndZ=0
  constraints (14):
    c: Coincident(g0,g-1)
    c: Distance(g0) = 6
    c: Vertical(g0)
    c: Coincident(g3,g0)
    c: Weight(g1) = 1
    c: Equal(g1,g2)
    c: InternalAlignment(g1,g3)
    c: InternalAlignment(g2,g3)
    c: InternalAlignment(g4,g3)
    c: InternalAlignment(g5,g3)
    c: Block(g3)
    c: Coincident(g6,g0)
    c: Coincident(g6,g3)
    c: Horizontal(g6)
FEATURE [Part::Extrusion] Extrude014  label="caseScrewPillarBracket002"
  Base = -> Sketch020
  Dir = (0,0,1)
  DirMode = 2
  FaceMakerClass = Part::FaceMakerBullseye
  LengthFwd = 2.4
  LengthRev = 0
  Placement = pos=(13.7,29,13.26) rot=(0,-1,0;1.5708rad)
  Solid = true
  Symmetric = false
FEATURE [Sketcher::SketchObject] Sketch021
  FullyConstrained = true
  sketch-geometry (7):
    g0: LineSegment StartX=0 StartY=0 StartZ=0 EndX=0 EndY=6 EndZ=0
    g1: Circle CenterX=0 CenterY=0 CenterZ=0 NormalX=0 NormalY=0 NormalZ=1 AngleXU=0 Radius=1
    g2: Circle CenterX=8 CenterY=6 CenterZ=0 NormalX=0 NormalY=0 NormalZ=1 AngleXU=0 Radius=1
    g3: BSplineCurve PolesCount=3 KnotsCount=2 Degree=2 IsPeriodic=0
    g4: GeomPoint X=0 Y=0 Z=0
    g5: GeomPoint X=8 Y=6 Z=0
    g6: LineSegment StartX=0 StartY=6 StartZ=0 EndX=8 EndY=6 EndZ=0
  constraints (14):
    c: Coincident(g0,g-1)
    c: Distance(g0) = 6
    c: Vertical(g0)
    c: Coincident(g3,g0)
    c: Weight(g1) = 1
    c: Equal(g1,g2)
    c: InternalAlignment(g1,g3)
    c: InternalAlignment(g2,g3)
    c: InternalAlignment(g4,g3)
    c: InternalAlignment(g5,g3)
    c: Block(g3)
    c: Coincident(g6,g0)
    c: Coincident(g6,g3)
    c: Horizontal(g6)
FEATURE [Part::Extrusion] Extrude015  label="caseScrewPillarBracket003"
  Base = -> Sketch021
  Dir = (0,0,1)
  DirMode = 2
  FaceMakerClass = Part::FaceMakerBullseye
  LengthFwd = 2.4
  LengthRev = 0
  Placement = pos=(11.3,29,58.74) rot=(0,1,0;1.5708rad)
  Solid = true
  Symmetric = false
FEATURE [Sketcher::SketchObject] Sketch022
  FullyConstrained = true
  sketch-geometry (7):
    g0: LineSegment StartX=0 StartY=0 StartZ=0 EndX=0 EndY=6 EndZ=0
    g1: Circle CenterX=0 CenterY=0 CenterZ=0 NormalX=0 NormalY=0 NormalZ=1 AngleXU=0 Radius=1
    g2: Circle CenterX=8 CenterY=6 CenterZ=0 NormalX=0 NormalY=0 NormalZ=1 AngleXU=0 Radius=1
    g3: BSplineCurve PolesCount=3 KnotsCount=2 Degree=2 IsPeriodic=0
    g4: GeomPoint X=0 Y=0 Z=0
    g5: GeomPoint X=8 Y=6 Z=0
    g6: LineSegment StartX=0 StartY=6 StartZ=0 EndX=8 EndY=6 EndZ=0
  constraints (14):
    c: Coincident(g0,g-1)
    c: Distance(g0) = 6
    c: Vertical(g0)
    c: Coincident(g3,g0)
    c: Weight(g1) = 1
    c: Equal(g1,g2)
    c: InternalAlignment(g1,g3)
    c: InternalAlignment(g2,g3)
    c: InternalAlignment(g4,g3)
    c: InternalAlignment(g5,g3)
    c: Block(g3)
    c: Coincident(g6,g0)
    c: Coincident(g6,g3)
    c: Horizontal(g6)
FEATURE [Part::Extrusion] Extrude016  label="caseScrewPillarBracket004"
  Base = -> Sketch022
  Dir = (0,0,1)
  DirMode = 2
  FaceMakerClass = Part::FaceMakerBullseye
  LengthFwd = 2.4
  LengthRev = 0
  Placement = pos=(88.3,29,65.23) rot=(0,1,0;1.5708rad)
  Solid = true
  Symmetric = false
FEATURE [Sketcher::SketchObject] Sketch023
  FullyConstrained = true
  sketch-geometry (7):
    g0: LineSegment StartX=0 StartY=0 StartZ=0 EndX=0 EndY=6 EndZ=0
    g1: Circle CenterX=0 CenterY=0 CenterZ=0 NormalX=0 NormalY=0 NormalZ=1 AngleXU=0 Radius=1
    g2: Circle CenterX=8 CenterY=6 CenterZ=0 NormalX=0 NormalY=0 NormalZ=1 AngleXU=0 Radius=1
    g3: BSplineCurve PolesCount=3 KnotsCount=2 Degree=2 IsPeriodic=0
    g4: GeomPoint X=0 Y=0 Z=0
    g5: GeomPoint X=8 Y=6 Z=0
    g6: LineSegment StartX=0 StartY=6 StartZ=0 EndX=8 EndY=6 EndZ=0
  constraints (14):
    c: Coincident(g0,g-1)
    c: Distance(g0) = 6
    c: Vertical(g0)
    c: Coincident(g3,g0)
    c: Weight(g1) = 1
    c: Equal(g1,g2)
    c: InternalAlignment(g1,g3)
    c: InternalAlignment(g2,g3)
    c: InternalAlignment(g4,g3)
    c: InternalAlignment(g5,g3)
    c: Block(g3)
    c: Coincident(g6,g0)
    c: Coincident(g6,g3)
    c: Horizontal(g6)
FEATURE [Part::Extrusion] Extrude017  label="caseScrewPillarBracket005"
  Base = -> Sketch023
  Dir = (0,0,1)
  DirMode = 2
  FaceMakerClass = Part::FaceMakerBullseye
  LengthFwd = 2.4
  LengthRev = 0
  Placement = pos=(90.7,29,6.77) rot=(0,-1,0;1.5708rad)
  Solid = true
  Symmetric = false
FEATURE [Sketcher::SketchObject] Sketch024
  FullyConstrained = true
  sketch-geometry (7):
    g0: LineSegment StartX=0 StartY=0 StartZ=0 EndX=0 EndY=6 EndZ=0
    g1: Circle CenterX=0 CenterY=0 CenterZ=0 NormalX=0 NormalY=0 NormalZ=1 AngleXU=0 Radius=1
    g2: Circle CenterX=8 CenterY=6 CenterZ=0 NormalX=0 NormalY=0 NormalZ=1 AngleXU=0 Radius=1
    g3: BSplineCurve PolesCount=3 KnotsCount=2 Degree=2 IsPeriodic=0
    g4: GeomPoint X=0 Y=0 Z=0
    g5: GeomPoint X=8 Y=6 Z=0
    g6: LineSegment StartX=0 StartY=6 StartZ=0 EndX=8 EndY=6 EndZ=0
  constraints (14):
    c: Coincident(g0,g-1)
    c: Distance(g0) = 6
    c: Vertical(g0)
    c: Coincident(g3,g0)
    c: Weight(g1) = 1
    c: Equal(g1,g2)
    c: InternalAlignment(g1,g3)
    c: InternalAlignment(g2,g3)
    c: InternalAlignment(g4,g3)
    c: InternalAlignment(g5,g3)
    c: Block(g3)
    c: Coincident(g6,g0)
    c: Coincident(g6,g3)
    c: Horizontal(g6)
FEATURE [Part::Extrusion] Extrude018  label="caseScrewPillarBracket006"
  Base = -> Sketch024
  Dir = (0,0,1)
  DirMode = 2
  FaceMakerClass = Part::FaceMakerBullseye
  LengthFwd = 2.4
  LengthRev = 0
  Placement = pos=(103.7,29,6.77) rot=(0,-1,0;1.5708rad)
  Solid = true
  Symmetric = false
FEATURE [Sketcher::SketchObject] Sketch025
  FullyConstrained = true
  sketch-geometry (7):
    g0: LineSegment StartX=0 StartY=0 StartZ=0 EndX=0 EndY=6 EndZ=0
    g1: Circle CenterX=0 CenterY=0 CenterZ=0 NormalX=0 NormalY=0 NormalZ=1 AngleXU=0 Radius=1
    g2: Circle CenterX=8 CenterY=6 CenterZ=0 NormalX=0 NormalY=0 NormalZ=1 AngleXU=0 Radius=1
    g3: BSplineCurve PolesCount=3 KnotsCount=2 Degree=2 IsPeriodic=0
    g4: GeomPoint X=0 Y=0 Z=0
    g5: GeomPoint X=8 Y=6 Z=0
    g6: LineSegment StartX=0 StartY=6 StartZ=0 EndX=8 EndY=6 EndZ=0
  constraints (14):
    c: Coincident(g0,g-1)
    c: Distance(g0) = 6
    c: Vertical(g0)
    c: Coincident(g3,g0)
    c: Weight(g1) = 1
    c: Equal(g1,g2)
    c: InternalAlignment(g1,g3)
    c: InternalAlignment(g2,g3)
    c: InternalAlignment(g4,g3)
    c: InternalAlignment(g5,g3)
    c: Block(g3)
    c: Coincident(g6,g0)
    c: Coincident(g6,g3)
    c: Horizontal(g6)
FEATURE [Part::Extrusion] Extrude019  label="caseScrewPillarBracket007"
  Base = -> Sketch025
  Dir = (0,0,1)
  DirMode = 2
  FaceMakerClass = Part::FaceMakerBullseye
  LengthFwd = 2.4
  LengthRev = 0
  Placement = pos=(101.3,29,65.23) rot=(0,1,0;1.5708rad)
  Solid = true
  Symmetric = false
FEATURE [Part::Box] Box011  label="frontCaseScrewPillarBracket"
  AttacherType = Attacher::AttachEngine3D
  Height = 2.4
  Length = 16
  Placement = pos=(87,28,2.3) rot=(0,0,1;0rad)
  Width = 7
FEATURE [Part::Box] Box012  label="frontCaseScrewPillarBracket001"
  AttacherType = Attacher::AttachEngine3D
  Height = 2.4
  Length = 16
  Placement = pos=(87,28,67.3) rot=(0,0,1;0rad)
  Width = 7
FEATURE [Sketcher::SketchObject] Sketch026
  FullyConstrained = true
  sketch-geometry (17):
    g0: Circle CenterX=-3.5 CenterY=23.5 CenterZ=0 NormalX=0 NormalY=0 NormalZ=1 AngleXU=0 Radius=1
    g1: Circle CenterX=-1 CenterY=15.25 CenterZ=0 NormalX=0 NormalY=0 NormalZ=1 AngleXU=0 Radius=1
    g2: Circle CenterX=-3.5 CenterY=7 CenterZ=0 NormalX=0 NormalY=0 NormalZ=1 AngleXU=0 Radius=1
    g3: BSplineCurve PolesCount=3 KnotsCount=2 Degree=2 IsPeriodic=0
    g4: GeomPoint X=-3.5 Y=23.5 Z=0
    g5: GeomPoint X=-3.5 Y=7 Z=0
    g6: Circle CenterX=-4.8 CenterY=30.5 CenterZ=0 NormalX=0 NormalY=0 NormalZ=1 AngleXU=0 Radius=1
    g7: Circle CenterX=-3.5 CenterY=30.5 CenterZ=0 NormalX=0 NormalY=0 NormalZ=1 AngleXU=0 Radius=1
    g8: Circle CenterX=-3.5 CenterY=29.2 CenterZ=0 NormalX=0 NormalY=0 NormalZ=1 AngleXU=0 Radius=1
    g9: BSplineCurve PolesCount=3 KnotsCount=2 Degree=2 IsPeriodic=0
    g10: GeomPoint X=-4.8 Y=30.5 Z=0
    g11: GeomPoint X=-3.5 Y=29.2 Z=0
    g12: LineSegment StartX=-3.5 StartY=29.2 StartZ=0 EndX=-3.5 EndY=23.5 EndZ=0
    g13: LineSegment StartX=-4.8 StartY=30.5 StartZ=0 EndX=0 EndY=30.5 EndZ=0
    g14: LineSegment StartX=-3.5 StartY=5 StartZ=0 EndX=-3.5 EndY=7 EndZ=0
    g15: LineSegment StartX=0 StartY=5 StartZ=0 EndX=0 EndY=30.5 EndZ=0
    g16: LineSegment StartX=-3.5 StartY=5 StartZ=0 EndX=0 EndY=5 EndZ=0
  constraints (33):
    c: Weight(g0) = 1
    c: Equal(g0,g1)
    c: Equal(g0,g2)
    c: InternalAlignment(g0,g3)
    c: InternalAlignment(g1,g3)
    c: InternalAlignment(g2,g3)
    c: InternalAlignment(g4,g3)
    c: InternalAlignment(g5,g3)
    c: Block(g3)
    c: Weight(g6) = 1
    c: Equal(g6,g7)
    c: Equal(g6,g8)
    c: InternalAlignment(g6,g9)
    c: InternalAlignment(g7,g9)
    c: InternalAlignment(g8,g9)
    c: InternalAlignment(g10,g9)
    c: InternalAlignment(g11,g9)
    c: Block(g9)
    c: Coincident(g12,g9)
    c: Coincident(g12,g3)
    c: Vertical(g12)
    c: Coincident(g13,g9)
    c: Horizontal(g13)
    c: Distance(g13) = 4.8
    c: Coincident(g14,g3)
    c: Vertical(g14)
    c: Coincident(g15,g13)
    c: Vertical(g15)
    c: Tangent(g15,g1)
    c: Distance(g14) = 2
    c: Coincident(g16,g14)
    c: Horizontal(g16)
    c: Coincident(g15,g16)
FEATURE [Part::Feature] Face050
  shape: bbox 4.8 x 25.5 x 2e-07 mm, 1 faces, 0 solids (baked)
FEATURE [Part::Revolution] Revolve054  label="moreFrontCaseScrewPost001"
  Angle = 360
  Axis = (0,1,0)
  Base = (0,0,0)
  FaceMakerClass = Part::FaceMakerBullseye
  Placement = pos=(102.5,4.5,3.5) rot=(0,0,1;0rad)
  Solid = false
  Source = -> Face050
  Symmetric = false
FEATURE [Part::Feature] Face051
  shape: bbox 4.8 x 25.5 x 2e-07 mm, 1 faces, 0 solids (baked)
FEATURE [Part::Revolution] Revolve055  label="moreFrontCaseScrewPost002"
  Angle = 360
  Axis = (0,1,0)
  Base = (0,0,0)
  FaceMakerClass = Part::FaceMakerBullseye
  Placement = pos=(102.5,4.5,68.5) rot=(0,0,1;0rad)
  Solid = false
  Source = -> Face051
  Symmetric = false
FEATURE [Sketcher::SketchObject] Sketch027
  FullyConstrained = true
  sketch-geometry (10):
    g0: LineSegment StartX=-1.6 StartY=4.7 StartZ=0 EndX=-1.6 EndY=1.7 EndZ=0
    g1: LineSegment StartX=-3.5 StartY=4.7 StartZ=0 EndX=-1.6 EndY=4.7 EndZ=0
    g2: LineSegment StartX=-1.6 StartY=1.7 StartZ=0 EndX=-1.6 EndY=1.5 EndZ=0
    g3: LineSegment StartX=-1.6 StartY=1.5 StartZ=0 EndX=-5.2 EndY=1.5 EndZ=0
    g4: Circle CenterX=-3.5 CenterY=4.7 CenterZ=0 NormalX=0 NormalY=0 NormalZ=1 AngleXU=0 Radius=1
    g5: Circle CenterX=-3.59627 CenterY=2.99743 CenterZ=0 NormalX=0 NormalY=0 NormalZ=1 AngleXU=0 Radius=1
    g6: Circle CenterX=-5.2 CenterY=1.5 CenterZ=0 NormalX=0 NormalY=0 NormalZ=1 AngleXU=0 Radius=1
    g7: BSplineCurve PolesCount=3 KnotsCount=2 Degree=2 IsPeriodic=0
    g8: GeomPoint X=-3.5 Y=4.7 Z=0
    g9: GeomPoint X=-5.2 Y=1.5 Z=0
  constraints (23):
    c: Vertical(g0)
    c: Distance(g0) = 3
    c: Coincident(g1,g0)
    c: Horizontal(g1)
    c: Block(g0)
    c: Block(g1)
    c: Coincident(g2,g0)
    c: Vertical(g2)
    c: Distance(g2) = 0.2
    c: Coincident(g3,g2)
    c: Horizontal(g3)
    c: Block(g3)
    c: Coincident(g7,g1)
    c: Weight(g4) = 1
    c: Equal(g4,g5)
    c: Equal(g4,g6)
    c: Coincident(g7,g3)
    c: InternalAlignment(g4,g7)
    c: InternalAlignment(g5,g7)
    c: InternalAlignment(g6,g7)
    c: InternalAlignment(g8,g7)
    c: InternalAlignment(g9,g7)
    c: Block(g7)
FEATURE [Sketcher::SketchObject] Sketch028
  FullyConstrained = true
  sketch-geometry (18):
    g0: LineSegment StartX=0 StartY=3e-16 StartZ=0 EndX=0 EndY=1.7 EndZ=0
    g1: LineSegment StartX=-3.5 StartY=0 StartZ=0 EndX=-3.5 EndY=0.9 EndZ=0
    g2: Circle CenterX=-2.7 CenterY=1.7 CenterZ=0 NormalX=0 NormalY=0 NormalZ=1 AngleXU=0 Radius=1
    g3: Circle CenterX=-3.5 CenterY=1.7 CenterZ=0 NormalX=0 NormalY=0 NormalZ=1 AngleXU=0 Radius=1
    g4: Circle CenterX=-3.5 CenterY=0.9 CenterZ=0 NormalX=0 NormalY=0 NormalZ=1 AngleXU=0 Radius=1
    g5: BSplineCurve PolesCount=3 KnotsCount=2 Degree=2 IsPeriodic=0
    g6: GeomPoint X=-2.7 Y=1.7 Z=0
    g7: GeomPoint X=-3.5 Y=0.9 Z=0
    g8: LineSegment StartX=-3.5 StartY=0 StartZ=0 EndX=-3.5 EndY=-7 EndZ=0
    g9: LineSegment StartX=0 StartY=3e-16 StartZ=0 EndX=0 EndY=-7 EndZ=0
    g10: LineSegment StartX=-3.5 StartY=-7 StartZ=0 EndX=0 EndY=-7 EndZ=0
    g11: LineSegment StartX=-2.7 StartY=1.7 StartZ=0 EndX=-1.6 EndY=1.7 EndZ=0
    g12: LineSegment StartX=0 StartY=1.7 StartZ=0 EndX=0 EndY=4.5 EndZ=0
    g13: LineSegment StartX=0 StartY=4.5 StartZ=0 EndX=0 EndY=10.8 EndZ=0
    g14: LineSegment StartX=0 StartY=10.8 StartZ=0 EndX=-2 EndY=10.8 EndZ=0
    g15: LineSegment StartX=-1.6 StartY=4.7 StartZ=0 EndX=-1.6 EndY=1.7 EndZ=0
    g16: LineSegment StartX=-1.6 StartY=4.7 StartZ=0 EndX=-2 EndY=4.7 EndZ=0
    g17: LineSegment StartX=-2 StartY=4.7 StartZ=0 EndX=-2 EndY=10.8 EndZ=0
  constraints (44):
    c: Vertical(g0)
    c: Vertical(g1)
    c: Distance(g1) = 0.9
    c: Block(g0)
    c: Distance(g0) = 1.7
    c: Weight(g2) = 1
    c: Equal(g2,g3)
    c: Equal(g2,g4)
    c: Coincident(g5,g1)
    c: InternalAlignment(g2,g5)
    c: InternalAlignment(g3,g5)
    c: InternalAlignment(g4,g5)
    c: InternalAlignment(g6,g5)
    c: InternalAlignment(g7,g5)
    c: Block(g5)
    c: Coincident(g8,g1)
    c: Vertical(g8)
    c: Distance(g8) = 7
    c: Vertical(g9)
    c: Equal(g8,g9) = 7
    c: Coincident(g9,g0)
    c: Coincident(g10,g8)
    c: Coincident(g10,g9)
    c: Horizontal(g10)
    c: Coincident(g11,g5)
    c: Horizontal(g11)
    c: Coincident(g12,g0)
    c: Vertical(g12)
    c: Distance(g12) = 2.8
    c: Coincident(g13,g12)
    c: Vertical(g13)
    c: Distance(g13) = 6.3
    c: Coincident(g14,g13)
    c: Horizontal(g14)
    c: Distance(g14) = 2
    c: Vertical(g15)
    c: Distance(g15) = 3
    c: Block(g11)
    c: Coincident(g15,g11)
    c: Coincident(g16,g15)
    c: Horizontal(g16)
    c: Coincident(g17,g16)
    c: Coincident(g17,g14)
    c: Vertical(g17)
FEATURE [Part::Revolution] Revolve040  label="backCaseScrewRetainer001"
  Angle = 360
  Axis = (0,1,0)
  Base = (0,0,0)
  FaceMakerClass = Part::FaceMakerBullseye
  Placement = pos=(12.5,3,10) rot=(0,0,1;0rad)
  Solid = false
  Source = -> Face036
  Symmetric = false
FEATURE [Part::Feature] Face055
  shape: bbox 3.5 x 30.2 x 2e-07 mm, 1 faces, 0 solids (baked)
FEATURE [Part::Revolution] Revolve059  label="backCaseScrewPost"
  Angle = 360
  Axis = (0,1,0)
  Base = (0,0,0)
  FaceMakerClass = Part::FaceMakerBullseye
  Placement = pos=(12.5,4.5,10) rot=(0,0,1;0rad)
  Solid = false
  Source = -> Face055
  Symmetric = false
FEATURE [Part::Feature] Face056
  shape: bbox 3.5 x 30.2 x 2e-07 mm, 1 faces, 0 solids (baked)
FEATURE [Part::Revolution] Revolve060  label="backCaseScrewPost001"
  Angle = 360
  Axis = (0,1,0)
  Base = (0,0,0)
  FaceMakerClass = Part::FaceMakerBullseye
  Placement = pos=(12.5,4.5,62) rot=(0,0,1;0rad)
  Solid = false
  Source = -> Face056
  Symmetric = false
FEATURE [Part::Feature] Face057
  shape: bbox 3.5 x 17.8 x 2e-07 mm, 1 faces, 0 solids (baked)
FEATURE [Part::Revolution] Revolve061  label="removeToCreateScrewAndThreadedInsertHole"
  Angle = 360
  Axis = (0,1,0)
  Base = (0,0,0)
  FaceMakerClass = Part::FaceMakerBullseye
  Placement = pos=(12.5,0,10) rot=(0,0,1;0rad)
  Solid = false
  Source = -> Face057
  Symmetric = false
FEATURE [Part::Feature] Face058
  shape: bbox 3.5 x 17.8 x 2e-07 mm, 1 faces, 0 solids (baked)
FEATURE [Part::Revolution] Revolve062  label="removeToCreateScrewAndThreadedInsertHole001"
  Angle = 360
  Axis = (0,1,0)
  Base = (0,0,0)
  FaceMakerClass = Part::FaceMakerBullseye
  Placement = pos=(12.5,0,62) rot=(0,0,1;0rad)
  Solid = false
  Source = -> Face058
  Symmetric = false
FEATURE [Part::Feature] Face059
  shape: bbox 3.5 x 17.8 x 2e-07 mm, 1 faces, 0 solids (baked)
FEATURE [Part::Revolution] Revolve063  label="removeToCreateScrewAndThreadedInsertHole002"
  Angle = 360
  Axis = (0,1,0)
  Base = (0,0,0)
  FaceMakerClass = Part::FaceMakerBullseye
  Placement = pos=(89.5,0,68.5) rot=(0,0,1;0rad)
  Solid = false
  Source = -> Face059
  Symmetric = false
FEATURE [Part::Feature] Face060
  shape: bbox 3.5 x 17.8 x 2e-07 mm, 1 faces, 0 solids (baked)
FEATURE [Part::Revolution] Revolve064  label="removeToCreateScrewAndThreadedInsertHole003"
  Angle = 360
  Axis = (0,1,0)
  Base = (0,0,0)
  FaceMakerClass = Part::FaceMakerBullseye
  Placement = pos=(89.5,0,3.5) rot=(0,0,1;0rad)
  Solid = false
  Source = -> Face060
  Symmetric = false
FEATURE [Part::Feature] Face061
  shape: bbox 3.5 x 17.8 x 2e-07 mm, 1 faces, 0 solids (baked)
FEATURE [Part::Revolution] Revolve065  label="removeToCreateScrewAndThreadedInsertHole004"
  Angle = 360
  Axis = (0,1,0)
  Base = (0,0,0)
  FaceMakerClass = Part::FaceMakerBullseye
  Placement = pos=(102.5,4.7,3.5) rot=(0,0,1;0rad)
  Solid = false
  Source = -> Face061
  Symmetric = false
FEATURE [Part::Feature] Face062
  shape: bbox 3.5 x 17.8 x 2e-07 mm, 1 faces, 0 solids (baked)
FEATURE [Part::Revolution] Revolve066  label="removeToCreateScrewAndThreadedInsertHole005"
  Angle = 360
  Axis = (0,1,0)
  Base = (0,0,0)
  FaceMakerClass = Part::FaceMakerBullseye
  Placement = pos=(102.5,4.7,68.5) rot=(0,0,1;0rad)
  Solid = false
  Source = -> Face062
  Symmetric = false
FEATURE [Part::MultiFuse] Fusion047  label="makeHoles"
  Shapes = -> [Revolve066,Revolve065,Revolve064,Revolve063,Revolve062,Revolve061]
FEATURE [Part::Feature] Face063
  shape: bbox 3.6 x 3.2 x 2e-07 mm, 1 faces, 0 solids (baked)
FEATURE [Part::Revolution] Revolve067  label="moreFrontCaseScrewRetainer002"
  Angle = 360
  Axis = (0,1,0)
  Base = (0,0,0)
  FaceMakerClass = Part::FaceMakerBullseye
  Placement = pos=(102.5,4.5,68.5) rot=(0,0,1;0rad)
  Solid = false
  Source = -> Face063
  Symmetric = false
FEATURE [Part::Feature] Face064
  shape: bbox 3.6 x 3.2 x 2e-07 mm, 1 faces, 0 solids (baked)
FEATURE [Part::Revolution] Revolve068  label="moreFrontCaseScrewRetainer003"
  Angle = 360
  Axis = (0,1,0)
  Base = (0,0,0)
  FaceMakerClass = Part::FaceMakerBullseye
  Placement = pos=(102.5,4.5,3.5) rot=(0,0,1;0rad)
  Solid = false
  Source = -> Face064
  Symmetric = false
FEATURE [Part::Feature] Face065
  shape: bbox 3.5 x 17.8 x 2e-07 mm, 1 faces, 0 solids (baked)
FEATURE [Part::Revolution] Revolve069  label="removeToCreateScrewAndThreadedInsertHole006"
  Angle = 360
  Axis = (0,1,0)
  Base = (0,0,0)
  FaceMakerClass = Part::FaceMakerBullseye
  Placement = pos=(12.5,0,10) rot=(0,0,1;0rad)
  Solid = false
  Source = -> Face065
  Symmetric = false
FEATURE [Part::Feature] Face066
  shape: bbox 3.5 x 17.8 x 2e-07 mm, 1 faces, 0 solids (baked)
FEATURE [Part::Revolution] Revolve070  label="removeToCreateScrewAndThreadedInsertHole007"
  Angle = 360
  Axis = (0,1,0)
  Base = (0,0,0)
  FaceMakerClass = Part::FaceMakerBullseye
  Placement = pos=(12.5,0,62) rot=(0,0,1;0rad)
  Solid = false
  Source = -> Face066
  Symmetric = false
FEATURE [Part::Feature] Face067
  shape: bbox 3.5 x 17.8 x 2e-07 mm, 1 faces, 0 solids (baked)
FEATURE [Part::Revolution] Revolve071  label="removeToCreateScrewAndThreadedInsertHole008"
  Angle = 360
  Axis = (0,1,0)
  Base = (0,0,0)
  FaceMakerClass = Part::FaceMakerBullseye
  Placement = pos=(89.5,0,68.5) rot=(0,0,1;0rad)
  Solid = false
  Source = -> Face067
  Symmetric = false
FEATURE [Part::Feature] Face068
  shape: bbox 3.5 x 17.8 x 2e-07 mm, 1 faces, 0 solids (baked)
FEATURE [Part::Revolution] Revolve072  label="removeToCreateScrewAndThreadedInsertHole009"
  Angle = 360
  Axis = (0,1,0)
  Base = (0,0,0)
  FaceMakerClass = Part::FaceMakerBullseye
  Placement = pos=(89.5,0,3.5) rot=(0,0,1;0rad)
  Solid = false
  Source = -> Face068
  Symmetric = false
FEATURE [Part::Feature] Face069
  shape: bbox 3.5 x 17.8 x 2e-07 mm, 1 faces, 0 solids (baked)
FEATURE [Part::Feature] Face070
  shape: bbox 3.5 x 17.8 x 2e-07 mm, 1 faces, 0 solids (baked)
FEATURE [Part::Revolution] Revolve073  label="removeToCreateScrewAndThreadedInsertHole010"
  Angle = 360
  Axis = (0,1,0)
  Base = (0,0,0)
  FaceMakerClass = Part::FaceMakerBullseye
  Placement = pos=(102.5,4.7,3.5) rot=(0,0,1;0rad)
  Solid = false
  Source = -> Face069
  Symmetric = false
FEATURE [Part::Revolution] Revolve074  label="removeToCreateScrewAndThreadedInsertHole011"
  Angle = 360
  Axis = (0,1,0)
  Base = (0,0,0)
  FaceMakerClass = Part::FaceMakerBullseye
  Placement = pos=(102.5,4.7,68.5) rot=(0,0,1;0rad)
  Solid = false
  Source = -> Face070
  Symmetric = false
FEATURE [Part::MultiFuse] Fusion048  label="makeHoles001"
  Shapes = -> [Revolve074,Revolve073,Revolve072,Revolve071,Revolve070,Revolve069]
FEATURE [Part::MultiFuse] Fusion049  label="caseScrewRetainers"
  Shapes = -> [Revolve067,Revolve068,Revolve048,Revolve047,Revolve039,Revolve040]
FEATURE [Part::Cut] Cut015  label="caseScrewRetainers001"
  Base = -> Fusion049
  Tool = -> Fusion048
FEATURE [Part::MultiFuse] Fusion050  label="casePillars"
  Shapes = -> [Revolve055,Revolve054,Revolve043,Revolve046,Revolve059,Revolve060]
FEATURE [Part::Feature] Face071 .. Face076  x6 (patterned run collapsed; names and placements below)
  shape: bbox 3.5 x 17.8 x 2e-07 mm, 1 faces, 0 solids (baked)
FEATURE [Part::Revolution] Revolve075  label="removeToCreateScrewAndThreadedInsertHole012"
  Angle = 360
  Axis = (0,1,0)
  Base = (0,0,0)
  FaceMakerClass = Part::FaceMakerBullseye
  Placement = pos=(12.5,0,10) rot=(0,0,1;0rad)
  Solid = false
  Source = -> Face071
  Symmetric = false
FEATURE [Part::Revolution] Revolve076  label="removeToCreateScrewAndThreadedInsertHole013"
  Angle = 360
  Axis = (0,1,0)
  Base = (0,0,0)
  FaceMakerClass = Part::FaceMakerBullseye
  Placement = pos=(12.5,0,62) rot=(0,0,1;0rad)
  Solid = false
  Source = -> Face072
  Symmetric = false
FEATURE [Part::Revolution] Revolve077  label="removeToCreateScrewAndThreadedInsertHole014"
  Angle = 360
  Axis = (0,1,0)
  Base = (0,0,0)
  FaceMakerClass = Part::FaceMakerBullseye
  Placement = pos=(89.5,0,68.5) rot=(0,0,1;0rad)
  Solid = false
  Source = -> Face073
  Symmetric = false
FEATURE [Part::Revolution] Revolve078  label="removeToCreateScrewAndThreadedInsertHole015"
  Angle = 360
  Axis = (0,1,0)
  Base = (0,0,0)
  FaceMakerClass = Part::FaceMakerBullseye
  Placement = pos=(89.5,0,3.5) rot=(0,0,1;0rad)
  Solid = false
  Source = -> Face074
  Symmetric = false
FEATURE [Part::Revolution] Revolve079  label="removeToCreateScrewAndThreadedInsertHole016"
  Angle = 360
  Axis = (0,1,0)
  Base = (0,0,0)
  FaceMakerClass = Part::FaceMakerBullseye
  Placement = pos=(102.5,4.7,3.5) rot=(0,0,1;0rad)
  Solid = false
  Source = -> Face075
  Symmetric = false
FEATURE [Part::Revolution] Revolve080  label="removeToCreateScrewAndThreadedInsertHole017"
  Angle = 360
  Axis = (0,1,0)
  Base = (0,0,0)
  FaceMakerClass = Part::FaceMakerBullseye
  Placement = pos=(102.5,4.7,68.5) rot=(0,0,1;0rad)
  Solid = false
  Source = -> Face076
  Symmetric = false
FEATURE [Part::MultiFuse] Fusion051  label="makeHoles002"
  Shapes = -> [Revolve080,Revolve079,Revolve078,Revolve077,Revolve076,Revolve075]
FEATURE [Part::Cut] Cut016  label="caesPillars"
  Base = -> Fusion050
  Tool = -> Fusion051
FEATURE [Part::Revolution] Revolve009  label="plugHousing016"
  Angle = 360
  Axis = (0,1,0)
  Base = (0,0,0)
  FaceMakerClass = Part::FaceMakerBullseye
  Placement = pos=(0,0,36.15) rot=(0,0,1;0rad)
  Solid = false
  Source = -> Face012
  Symmetric = false
FEATURE [Part::MultiFuse] Fusion014  label="plugHousing023"
  Placement = pos=(0,0,0) rot=(0,0,1;1.5708rad)
  Shapes = -> [Revolve011,Revolve009]
FEATURE [Part::Revolution] Revolve010  label="plugHousing017"
  Angle = 360
  Axis = (0,1,0)
  Base = (0,0,0)
  FaceMakerClass = Part::FaceMakerBullseye
  Placement = pos=(0,0,36.15) rot=(0,0,1;0rad)
  Solid = false
  Source = -> Face014
  Symmetric = false
FEATURE [Part::MultiFuse] Fusion015  label="plugHousing024"
  Placement = pos=(0,0,0) rot=(0,0,1;1.5708rad)
  Shapes = -> [Revolve010,Revolve015]
FEATURE [Part::Revolution] Revolve014  label="plugHousing026"
  Angle = 360
  Axis = (0,1,0)
  Base = (0,0,0)
  FaceMakerClass = Part::FaceMakerBullseye
  Placement = pos=(0,0,36.15) rot=(0,0,1;0rad)
  Solid = false
  Source = -> Face011
  Symmetric = false
FEATURE [Part::Revolution] Revolve013  label="plugHousing025"
  Angle = 360
  Axis = (0,1,0)
  Base = (0,0,0)
  FaceMakerClass = Part::FaceMakerBullseye
  Placement = pos=(0,0,36.15) rot=(0,0,1;0rad)
  Solid = false
  Source = -> Face015
  Symmetric = false
FEATURE [Part::MultiFuse] Fusion016  label="plugHousing028"
  Placement = pos=(0,19,0) rot=(0,0,1;3.14159rad)
  Shapes = -> [Fusion014,Fusion013]
FEATURE [Part::MultiFuse] Fusion011  label="plugHousing018"
  Placement = pos=(0,0,0) rot=(0,0,1;1.5708rad)
  Shapes = -> [Revolve014,Revolve013]
FEATURE [Part::MultiFuse] Fusion012  label="plugHousing019"
  Placement = pos=(0,19,0) rot=(0,0,1;3.14159rad)
  Shapes = -> [Fusion011,Fusion015]
FEATURE [Part::MultiFuse] Fusion017  label="plugHousing029"
  Placement = pos=(122.621,0,-0.15) rot=(0,0,1;0rad)
  Shapes = -> [Fusion016,Fusion012]
FEATURE [Part::MultiFuse] Fusion052  label="casePillarRetainers"
  Shapes = -> [Extrude012,Extrude013,Extrude014,Extrude015,Extrude016,Extrude017,Extrude018,Extrude019,Box011,Box012]
FEATURE [Part::Feature] Face077
  shape: bbox 3.5 x 17.8 x 2e-07 mm, 1 faces, 0 solids (baked)
FEATURE [Part::Revolution] Revolve081  label="removeToCreateScrewAndThreadedInsertHole018"
  Angle = 360
  Axis = (0,1,0)
  Base = (0,0,0)
  FaceMakerClass = Part::FaceMakerBullseye
  Placement = pos=(62.3,30.3,19.7) rot=(0,0,1;0rad)
  Solid = false
  Source = -> Face077
  Symmetric = false
FEATURE [Part::Feature] Face078
  shape: bbox 3.5 x 17.8 x 2e-07 mm, 1 faces, 0 solids (baked)
FEATURE [Part::Revolution] Revolve082  label="removeToCreateScrewAndThreadedInsertHole019"
  Angle = 360
  Axis = (0,1,0)
  Base = (0,0,0)
  FaceMakerClass = Part::FaceMakerBullseye
  Placement = pos=(62.3,30.3,51.7) rot=(0,0,1;0rad)
  Solid = false
  Source = -> Face078
  Symmetric = false
FEATURE [Part::Feature] Face079
  shape: bbox 3.5 x 17.8 x 2e-07 mm, 1 faces, 0 solids (baked)
FEATURE [Part::Revolution] Revolve083  label="removeToCreateScrewAndThreadedInsertHole020"
  Angle = 360
  Axis = (0,1,0)
  Base = (0,0,0)
  FaceMakerClass = Part::FaceMakerBullseye
  Placement = pos=(30.3,30.3,19.7) rot=(0,0,1;0rad)
  Solid = false
  Source = -> Face079
  Symmetric = false
FEATURE [Part::Feature] Face080
  shape: bbox 3.5 x 17.8 x 2e-07 mm, 1 faces, 0 solids (baked)
FEATURE [Part::Revolution] Revolve084  label="removeToCreateScrewAndThreadedInsertHole021"
  Angle = 360
  Axis = (0,1,0)
  Base = (0,0,0)
  FaceMakerClass = Part::FaceMakerBullseye
  Placement = pos=(30.3,30.3,51.7) rot=(0,0,1;0rad)
  Solid = false
  Source = -> Face080
  Symmetric = false
FEATURE [Part::MultiFuse] Fusion053  label="createThreadedInsertHolesForFan"
  Shapes = -> [Revolve081,Revolve082,Revolve083,Revolve084]
FEATURE [Part::Cut] Cut017  label="fanScrewHousing001"
  Base = -> Fusion046
  Tool = -> Fusion053
FEATURE [Part::Feature] Face081
  shape: bbox 3.5 x 17.8 x 2e-07 mm, 1 faces, 0 solids (baked)
FEATURE [Part::Revolution] Revolve085  label="removeToCreateScrewAndThreadedInsertHole022"
  Angle = 360
  Axis = (0,1,0)
  Base = (0,0,0)
  FaceMakerClass = Part::FaceMakerBullseye
  Placement = pos=(62.3,30.3,19.7) rot=(0,0,1;0rad)
  Solid = false
  Source = -> Face081
  Symmetric = false
FEATURE [Part::Feature] Face082
  shape: bbox 3.5 x 17.8 x 2e-07 mm, 1 faces, 0 solids (baked)
FEATURE [Part::Revolution] Revolve086  label="removeToCreateScrewAndThreadedInsertHole023"
  Angle = 360
  Axis = (0,1,0)
  Base = (0,0,0)
  FaceMakerClass = Part::FaceMakerBullseye
  Placement = pos=(62.3,30.3,51.7) rot=(0,0,1;0rad)
  Solid = false
  Source = -> Face082
  Symmetric = false
FEATURE [Part::Feature] Face083
  shape: bbox 3.5 x 17.8 x 2e-07 mm, 1 faces, 0 solids (baked)
FEATURE [Part::Revolution] Revolve087  label="removeToCreateScrewAndThreadedInsertHole024"
  Angle = 360
  Axis = (0,1,0)
  Base = (0,0,0)
  FaceMakerClass = Part::FaceMakerBullseye
  Placement = pos=(30.3,30.3,19.7) rot=(0,0,1;0rad)
  Solid = false
  Source = -> Face083
  Symmetric = false
FEATURE [Part::Feature] Face084
  shape: bbox 3.5 x 17.8 x 2e-07 mm, 1 faces, 0 solids (baked)
FEATURE [Part::Revolution] Revolve088  label="removeToCreateScrewAndThreadedInsertHole025"
  Angle = 360
  Axis = (0,1,0)
  Base = (0,0,0)
  FaceMakerClass = Part::FaceMakerBullseye
  Placement = pos=(30.3,30.3,51.7) rot=(0,0,1;0rad)
  Solid = false
  Source = -> Face084
  Symmetric = false
FEATURE [Part::MultiFuse] Fusion054  label="createThreadedInsertHolesForFan001"
  Shapes = -> [Revolve085,Revolve086,Revolve087,Revolve088]
FEATURE [Part::Cut] Cut018  label="top007"
  Base = -> Fusion040
  Tool = -> Fusion054
FEATURE [Sketcher::SketchObject] Sketch029
  FullyConstrained = false
  Placement = pos=(0,0,0) rot=(1,0,0;1.5708rad)
  sketch-geometry (24):
    g0: ArcOfCircle CenterX=-4 CenterY=-10.5 CenterZ=0 NormalX=0 NormalY=0 NormalZ=1 AngleXU=0 Radius=1.5 StartAngle=6e-16 EndAngle=3.14159
    g1: ArcOfCircle CenterX=-34.2 CenterY=-10.5 CenterZ=0 NormalX=0 NormalY=0 NormalZ=1 AngleXU=0 Radius=1.5 StartAngle=0 EndAngle=3.14159
    g2: ArcOfCircle CenterX=-34.2 CenterY=-27.7 CenterZ=0 NormalX=0 NormalY=0 NormalZ=1 AngleXU=0 Radius=1.5 StartAngle=3.14159 EndAngle=6.28319
    g3: ArcOfCircle CenterX=-4 CenterY=-27.7 CenterZ=0 NormalX=0 NormalY=0 NormalZ=1 AngleXU=0 Radius=1.5 StartAngle=3.1416 EndAngle=6.28319
    g4: ArcOfCircle CenterX=-10 CenterY=-4.3 CenterZ=0 NormalX=0 NormalY=0 NormalZ=1 AngleXU=0 Radius=1.5 StartAngle=2e-16 EndAngle=3.14159
    g5: ArcOfCircle CenterX=-16.1 CenterY=-1.8 CenterZ=0 NormalX=0 NormalY=0 NormalZ=1 AngleXU=0 Radius=1.5 StartAngle=5e-16 EndAngle=3.14159
    g6: ArcOfCircle CenterX=-22.1 CenterY=-1.8 CenterZ=0 NormalX=0 NormalY=0 NormalZ=1 AngleXU=0 Radius=1.5 StartAngle=5e-16 EndAngle=3.14159
    g7: ArcOfCircle CenterX=-28.2 CenterY=-4.3 CenterZ=0 NormalX=0 NormalY=0 NormalZ=1 AngleXU=0 Radius=1.5 StartAngle=2e-16 EndAngle=3.14159
    g8: ArcOfCircle CenterX=-10 CenterY=-33.9 CenterZ=0 NormalX=0 NormalY=0 NormalZ=1 AngleXU=0 Radius=1.5 StartAngle=3.14159 EndAngle=6.28319
    g9: ArcOfCircle CenterX=-16.1 CenterY=-36.4 CenterZ=0 NormalX=0 NormalY=0 NormalZ=1 AngleXU=0 Radius=1.5 StartAngle=3.14159 EndAngle=6.28319
    g10: ArcOfCircle CenterX=-22.1 CenterY=-36.4 CenterZ=0 NormalX=0 NormalY=0 NormalZ=1 AngleXU=0 Radius=1.5 StartAngle=3.14159 EndAngle=6.28319
    g11: ArcOfCircle CenterX=-28.2 CenterY=-33.9 CenterZ=0 NormalX=0 NormalY=0 NormalZ=1 AngleXU=0 Radius=1.5 StartAngle=3.14159 EndAngle=6.28319
    g12: LineSegment StartX=-35.7 StartY=-10.5 StartZ=0 EndX=-35.7 EndY=-27.7 EndZ=0
    g13: LineSegment StartX=-32.7 StartY=-10.5 StartZ=0 EndX=-32.7 EndY=-27.7 EndZ=0
    g14: LineSegment StartX=-29.7 StartY=-33.9 StartZ=0 EndX=-29.7 EndY=-4.3 EndZ=0
    g15: LineSegment StartX=-26.7 StartY=-33.9 StartZ=0 EndX=-26.7 EndY=-4.3 EndZ=0
    g16: LineSegment StartX=-2.5 StartY=-10.5 StartZ=0 EndX=-2.5 EndY=-27.7 EndZ=0
    g17: LineSegment StartX=-8.5 StartY=-4.3 StartZ=0 EndX=-8.5 EndY=-33.9 EndZ=0
    g18: LineSegment StartX=-5.5 StartY=-10.5 StartZ=0 EndX=-5.5 EndY=-27.7 EndZ=0
    g19: LineSegment StartX=-11.5 StartY=-4.3 StartZ=0 EndX=-11.5 EndY=-33.9 EndZ=0
    g20: LineSegment StartX=-14.6 StartY=-1.8 StartZ=0 EndX=-14.6 EndY=-36.4 EndZ=0
    g21: LineSegment StartX=-17.6 StartY=-1.8 StartZ=0 EndX=-17.6 EndY=-36.4 EndZ=0
    g22: LineSegment StartX=-20.6 StartY=-36.4 StartZ=0 EndX=-20.6 EndY=-1.8 EndZ=0
    g23: LineSegment StartX=-23.6 StartY=-1.8 StartZ=0 EndX=-23.6 EndY=-36.4 EndZ=0
  constraints (48):
    c: Block(g0)
    c: Block(g1)
    c: Block(g2)
    c: Block(g3)
    c: Block(g4)
    c: Block(g5)
    c: Block(g6)
    c: Block(g7)
    c: Block(g8)
    c: Block(g9)
    c: Block(g10)
    c: Block(g11)
    c: Coincident(g12,g1)
    c: Coincident(g12,g2)
    c: Vertical(g12)
    c: Coincident(g13,g1)
    c: Coincident(g13,g2)
    c: Vertical(g13)
    c: Coincident(g14,g11)
    c: Coincident(g14,g7)
    c: Vertical(g14)
    c: Coincident(g15,g11)
    c: Coincident(g15,g7)
    c: Vertical(g15)
    c: Coincident(g16,g0)
    c: Coincident(g16,g3)
    c: Vertical(g16)
    c: Coincident(g17,g4)
    c: Coincident(g17,g8)
    c: Vertical(g17)
    c: Coincident(g18,g0)
    c: Coincident(g18,g3)
    c: Vertical(g18)
    c: Coincident(g19,g4)
    c: Coincident(g19,g8)
    c: Vertical(g19)
    c: Coincident(g20,g5)
    c: Coincident(g20,g9)
    c: Vertical(g20)
    c: Coincident(g21,g5)
    c: Coincident(g21,g9)
    c: Vertical(g21)
    c: Coincident(g22,g10)
    c: Coincident(g22,g6)
    c: Vertical(g22)
    c: Coincident(g23,g6)
    c: Coincident(g23,g10)
    c: Vertical(g23)
FEATURE [Part::Extrusion] Extrude020  label="removeToCreateFanGrillHoles"
  Base = -> Sketch029
  Dir = (0,-1,6e-16)
  DirMode = 2
  FaceMakerClass = Part::FaceMakerBullseye
  LengthFwd = 10
  LengthRev = 0
  Placement = pos=(65.4,44,54.82) rot=(0,0,1;0rad)
  Solid = true
  Symmetric = false
FEATURE [Part::MultiFuse] Fusion055  label="top008"
  Shapes = -> [Cut017,Cut018]
FEATURE [Part::Cut] Cut019  label="top009"
  Base = -> Fusion055
  Tool = -> Extrude020
FEATURE [App::MeasureDistance] Distance003  label="Distance: 71.95 mm"
  Distance = 71.9513
  P1 = (117,38,72)
  P2 = (117,38,0.0487319)
FEATURE [Sketcher::SketchObject] Sketch030
  FullyConstrained = true
  Placement = pos=(117,19,0) rot=(0.57735,0.57735,0.57735;2.0944rad)
  sketch-geometry (48):
    g0: LineSegment StartX=-49.19 StartY=69.25 StartZ=0 EndX=-49.19 EndY=66.25 EndZ=0
    g1: LineSegment StartX=-49.19 StartY=63.5 StartZ=0 EndX=-49.19 EndY=60.5 EndZ=0
    g2: LineSegment StartX=-49.19 StartY=57.75 StartZ=0 EndX=-49.19 EndY=54.75 EndZ=0
    g3: LineSegment StartX=-49.19 StartY=52 StartZ=0 EndX=-49.19 EndY=49 EndZ=0
    g4: LineSegment StartX=-49.19 StartY=46.25 StartZ=0 EndX=-49.19 EndY=43.25 EndZ=0
    g5: LineSegment StartX=-49.19 StartY=40.5 StartZ=0 EndX=-49.19 EndY=37.5 EndZ=0
    g6: LineSegment StartX=-49.19 StartY=34.5 StartZ=0 EndX=-49.19 EndY=31.5 EndZ=0
    g7: LineSegment StartX=-49.19 StartY=28.75 StartZ=0 EndX=-49.19 EndY=25.75 EndZ=0
    g8: LineSegment StartX=-49.19 StartY=23 StartZ=0 EndX=-49.19 EndY=20 EndZ=0
    g9: LineSegment StartX=-49.19 StartY=17.25 StartZ=0 EndX=-49.19 EndY=14.25 EndZ=0
    g10: LineSegment StartX=-49.19 StartY=11.5 StartZ=0 EndX=-49.19 EndY=8.5 EndZ=0
    g11: LineSegment StartX=-49.19 StartY=5.75 StartZ=0 EndX=-49.19 EndY=2.75 EndZ=0
    g12: ArcOfCircle CenterX=-1.5 CenterY=67.75 CenterZ=0 NormalX=0 NormalY=0 NormalZ=1 AngleXU=0 Radius=1.5 StartAngle=4.71239 EndAngle=7.85398
    g13: ArcOfCircle CenterX=-1.5 CenterY=62 CenterZ=0 NormalX=0 NormalY=0 NormalZ=1 AngleXU=0 Radius=1.5 StartAngle=4.71239 EndAngle=7.85398
    g14: ArcOfCircle CenterX=-1.5 CenterY=56.25 CenterZ=0 NormalX=0 NormalY=0 NormalZ=1 AngleXU=0 Radius=1.5 StartAngle=4.71239 EndAngle=7.85398
    g15: ArcOfCircle CenterX=-11.49 CenterY=50.5 CenterZ=0 NormalX=0 NormalY=0 NormalZ=1 AngleXU=0 Radius=1.5 StartAngle=4.71239 EndAngle=7.85398
    g16: ArcOfCircle CenterX=-16.28 CenterY=44.75 CenterZ=0 NormalX=0 NormalY=0 NormalZ=1 AngleXU=0 Radius=1.5 StartAngle=4.71239 EndAngle=7.85398
    g17: ArcOfCircle CenterX=-18.2337 CenterY=39 CenterZ=0 NormalX=0 NormalY=0 NormalZ=1 AngleXU=0 Radius=1.5 StartAngle=4.71485 EndAngle=7.85398
    g18: ArcOfCircle CenterX=-16.2837 CenterY=27.25 CenterZ=0 NormalX=0 NormalY=0 NormalZ=1 AngleXU=0 Radius=1.5 StartAngle=4.71485 EndAngle=7.85398
    g19: ArcOfCircle CenterX=-18.2337 CenterY=33 CenterZ=0 NormalX=0 NormalY=0 NormalZ=1 AngleXU=0 Radius=1.5 StartAngle=4.71485 EndAngle=7.85398
    g20: ArcOfCircle CenterX=-11.49 CenterY=21.5 CenterZ=0 NormalX=0 NormalY=0 NormalZ=1 AngleXU=0 Radius=1.5 StartAngle=4.71239 EndAngle=7.85398
    g21: ArcOfCircle CenterX=-1.5 CenterY=4.25 CenterZ=0 NormalX=0 NormalY=0 NormalZ=1 AngleXU=0 Radius=1.5 StartAngle=4.71239 EndAngle=7.85398
    g22: ArcOfCircle CenterX=-1.5 CenterY=10 CenterZ=0 NormalX=0 NormalY=0 NormalZ=1 AngleXU=0 Radius=1.5 StartAngle=4.71239 EndAngle=7.85398
    g23: ArcOfCircle CenterX=-1.5 CenterY=15.75 CenterZ=0 NormalX=0 NormalY=0 NormalZ=1 AngleXU=0 Radius=1.5 StartAngle=4.71239 EndAngle=7.85398
    g24: LineSegment StartX=-49.19 StartY=69.25 StartZ=0 EndX=-1.5 EndY=69.25 EndZ=0
    g25: LineSegment StartX=-49.19 StartY=66.25 StartZ=0 EndX=-1.5 EndY=66.25 EndZ=0
    g26: LineSegment StartX=-49.19 StartY=63.5 StartZ=0 EndX=-1.5 EndY=63.5 EndZ=0
    g27: LineSegment StartX=-49.19 StartY=60.5 StartZ=0 EndX=-1.5 EndY=60.5 EndZ=0
    g28: LineSegment StartX=-49.19 StartY=57.75 StartZ=0 EndX=-1.5 EndY=57.75 EndZ=0
    g29: LineSegment StartX=-49.19 StartY=54.75 StartZ=0 EndX=-1.5 EndY=54.75 EndZ=0
    g30: LineSegment StartX=-49.19 StartY=52 StartZ=0 EndX=-11.49 EndY=52 EndZ=0
    g31: LineSegment StartX=-49.19 StartY=49 StartZ=0 EndX=-11.49 EndY=49 EndZ=0
    g32: LineSegment StartX=-49.19 StartY=46.25 StartZ=0 EndX=-16.28 EndY=46.25 EndZ=0
    g33: LineSegment StartX=-49.19 StartY=43.25 StartZ=0 EndX=-16.28 EndY=43.25 EndZ=0
    g34: LineSegment StartX=-49.19 StartY=40.5 StartZ=0 EndX=-18.2337 EndY=40.5 EndZ=0
    g35: LineSegment StartX=-49.19 StartY=37.5 StartZ=0 EndX=-18.23 EndY=37.5 EndZ=0
    g36: LineSegment StartX=-49.19 StartY=34.5 StartZ=0 EndX=-18.2337 EndY=34.5 EndZ=0
    g37: LineSegment StartX=-49.19 StartY=31.5 StartZ=0 EndX=-18.23 EndY=31.5 EndZ=0
    g38: LineSegment StartX=-49.19 StartY=28.75 StartZ=0 EndX=-16.2837 EndY=28.75 EndZ=0
    g39: LineSegment StartX=-49.19 StartY=25.75 StartZ=0 EndX=-16.28 EndY=25.75 EndZ=0
    g40: LineSegment StartX=-49.19 StartY=23 StartZ=0 EndX=-11.49 EndY=23 EndZ=0
    g41: LineSegment StartX=-49.19 StartY=20 StartZ=0 EndX=-11.49 EndY=20 EndZ=0
    g42: LineSegment StartX=-49.19 StartY=17.25 StartZ=0 EndX=-1.5 EndY=17.25 EndZ=0
    g43: LineSegment StartX=-49.19 StartY=14.25 StartZ=0 EndX=-1.5 EndY=14.25 EndZ=0
    g44: LineSegment StartX=-49.19 StartY=11.5 StartZ=0 EndX=-1.5 EndY=11.5 EndZ=0
    g45: LineSegment StartX=-49.19 StartY=8.5 StartZ=0 EndX=-1.5 EndY=8.5 EndZ=0
    g46: LineSegment StartX=-49.19 StartY=5.75 StartZ=0 EndX=-1.5 EndY=5.75 EndZ=0
    g47: LineSegment StartX=-49.19 StartY=2.75 StartZ=0 EndX=-1.5 EndY=2.75 EndZ=0
  constraints (120):
    c: Vertical(g0)
    c: Distance(g0) = 3
    c: Block(g0)
    c: Vertical(g1)
    c: Distance(g1) = 3
    c: Vertical(g2)
    c: Equal(g0,g2) = 3
    c: Block(g2)
    c: Vertical(g3)
    c: Equal(g1,g3) = 3
    c: Vertical(g4)
    c: Equal(g0,g4) = 3
    c: Block(g4)
    c: Vertical(g5)
    c: Equal(g1,g5) = 3
    c: Vertical(g6)
    c: Equal(g0,g6) = 3
    c: Block(g6)
    c: Vertical(g7)
    c: Equal(g1,g7) = 3
    c: Vertical(g8)
    c: Equal(g0,g8) = 3
    c: Block(g8)
    c: Vertical(g9)
    c: Equal(g1,g9) = 3
    c: Vertical(g10)
    c: Equal(g0,g10) = 3
    c: Block(g10)
    c: Vertical(g11)
    c: Equal(g1,g11) = 3
    c: Block(g12)
    c: Block(g13)
    c: Block(g14)
    c: Block(g15)
    c: Block(g16)
    c: Block(g17)
    c: Block(g18)
    c: Block(g19)
    c: Block(g20)
    c: Block(g21)
    c: Block(g22)
    c: Block(g23)
    c: Block(g11)
    c: Block(g9)
    c: Block(g7)
    c: Block(g5)
    c: Block(g3)
    c: Block(g1)
    c: Coincident(g24,g0)
    c: Coincident(g24,g12)
    c: Horizontal(g24)
    c: Coincident(g25,g0)
    c: Coincident(g25,g12)
    c: Horizontal(g25)
    c: Coincident(g26,g1)
    c: Coincident(g26,g13)
    c: Horizontal(g26)
    c: Coincident(g27,g1)
    c: Coincident(g27,g13)
    c: Horizontal(g27)
    c: Coincident(g28,g2)
    c: Coincident(g28,g14)
    c: Horizontal(g28)
    c: Coincident(g29,g2)
    c: Coincident(g29,g14)
    c: Horizontal(g29)
    c: Coincident(g30,g3)
    c: Coincident(g30,g15)
    c: Horizontal(g30)
    c: Coincident(g31,g3)
    c: Coincident(g31,g15)
    c: Horizontal(g31)
    c: Coincident(g32,g4)
    c: Coincident(g32,g16)
    c: Horizontal(g32)
    c: Coincident(g33,g4)
    c: Coincident(g33,g16)
    c: Horizontal(g33)
    c: Coincident(g34,g5)
    c: Coincident(g34,g17)
    c: Horizontal(g34)
    c: Coincident(g35,g5)
    c: Coincident(g35,g17)
    c: Horizontal(g35)
    c: Coincident(g36,g6)
    c: Coincident(g36,g19)
    c: Horizontal(g36)
    c: Coincident(g37,g6)
    c: Coincident(g37,g19)
    c: Horizontal(g37)
    c: Coincident(g38,g7)
    c: Coincident(g38,g18)
    c: Horizontal(g38)
    c: Coincident(g39,g7)
    c: Coincident(g39,g18)
    c: Horizontal(g39)
    c: Coincident(g40,g8)
    c: Coincident(g40,g20)
    c: Horizontal(g40)
    c: Coincident(g41,g8)
    c: Coincident(g41,g20)
    c: Horizontal(g41)
    c: Coincident(g42,g9)
    c: Coincident(g42,g23)
    c: Horizontal(g42)
    c: Coincident(g43,g9)
    c: Coincident(g43,g23)
    c: Horizontal(g43)
    c: Coincident(g44,g10)
    c: Coincident(g44,g22)
    c: Horizontal(g44)
    c: Coincident(g45,g10)
    c: Coincident(g45,g22)
    c: Horizontal(g45)
    c: Coincident(g46,g11)
    c: Coincident(g46,g21)
    c: Horizontal(g46)
    c: Coincident(g47,g11)
    c: Coincident(g47,g21)
    c: Horizontal(g47)
FEATURE [Sketcher::SketchObject] Sketch031
  FullyConstrained = true
  Placement = pos=(117,19,0) rot=(0.57735,0.57735,0.57735;2.0944rad)
  sketch-geometry (24):
    g0: ArcOfCircle CenterX=-49.19 CenterY=67.75 CenterZ=0 NormalX=0 NormalY=0 NormalZ=1 AngleXU=0 Radius=1.5 StartAngle=1.5708 EndAngle=4.71239
    g1: ArcOfCircle CenterX=-49.19 CenterY=62 CenterZ=0 NormalX=0 NormalY=0 NormalZ=1 AngleXU=0 Radius=1.5 StartAngle=1.5708 EndAngle=4.71239
    g2: ArcOfCircle CenterX=-49.19 CenterY=56.25 CenterZ=0 NormalX=0 NormalY=0 NormalZ=1 AngleXU=0 Radius=1.5 StartAngle=1.5708 EndAngle=4.71239
    g3: ArcOfCircle CenterX=-49.19 CenterY=50.5 CenterZ=0 NormalX=0 NormalY=0 NormalZ=1 AngleXU=0 Radius=1.5 StartAngle=1.5708 EndAngle=4.71239
    g4: ArcOfCircle CenterX=-49.19 CenterY=44.75 CenterZ=0 NormalX=0 NormalY=0 NormalZ=1 AngleXU=0 Radius=1.5 StartAngle=1.5708 EndAngle=4.71239
    g5: ArcOfCircle CenterX=-49.19 CenterY=39 CenterZ=0 NormalX=0 NormalY=0 NormalZ=1 AngleXU=0 Radius=1.5 StartAngle=1.5708 EndAngle=4.71239
    g6: ArcOfCircle CenterX=-49.19 CenterY=33 CenterZ=0 NormalX=0 NormalY=0 NormalZ=1 AngleXU=0 Radius=1.5 StartAngle=1.5708 EndAngle=4.71239
    g7: ArcOfCircle CenterX=-49.19 CenterY=27.25 CenterZ=0 NormalX=0 NormalY=0 NormalZ=1 AngleXU=0 Radius=1.5 StartAngle=1.5708 EndAngle=4.71239
    g8: ArcOfCircle CenterX=-49.19 CenterY=21.5 CenterZ=0 NormalX=0 NormalY=0 NormalZ=1 AngleXU=0 Radius=1.5 StartAngle=1.5708 EndAngle=4.71239
    g9: ArcOfCircle CenterX=-49.19 CenterY=15.75 CenterZ=0 NormalX=0 NormalY=0 NormalZ=1 AngleXU=0 Radius=1.5 StartAngle=1.5708 EndAngle=4.71239
    g10: ArcOfCircle CenterX=-49.19 CenterY=10 CenterZ=0 NormalX=0 NormalY=0 NormalZ=1 AngleXU=0 Radius=1.5 StartAngle=1.5708 EndAngle=4.71239
    g11: ArcOfCircle CenterX=-49.19 CenterY=4.25 CenterZ=0 NormalX=0 NormalY=0 NormalZ=1 AngleXU=0 Radius=1.5 StartAngle=1.5708 EndAngle=4.71239
    g12: LineSegment StartX=-49.19 StartY=69.25 StartZ=0 EndX=-49.19 EndY=66.25 EndZ=0
    g13: LineSegment StartX=-49.19 StartY=63.5 StartZ=0 EndX=-49.19 EndY=60.5 EndZ=0
    g14: LineSegment StartX=-49.19 StartY=57.75 StartZ=0 EndX=-49.19 EndY=54.75 EndZ=0
    g15: LineSegment StartX=-49.19 StartY=52 StartZ=0 EndX=-49.19 EndY=49 EndZ=0
    g16: LineSegment StartX=-49.19 StartY=46.25 StartZ=0 EndX=-49.19 EndY=43.25 EndZ=0
    g17: LineSegment StartX=-49.19 StartY=40.5 StartZ=0 EndX=-49.19 EndY=37.5 EndZ=0
    g18: LineSegment StartX=-49.19 StartY=34.5 StartZ=0 EndX=-49.19 EndY=31.5 EndZ=0
    g19: LineSegment StartX=-49.19 StartY=28.75 StartZ=0 EndX=-49.19 EndY=25.75 EndZ=0
    g20: LineSegment StartX=-49.19 StartY=23 StartZ=0 EndX=-49.19 EndY=20 EndZ=0
    g21: LineSegment StartX=-49.19 StartY=17.25 StartZ=0 EndX=-49.19 EndY=14.25 EndZ=0
    g22: LineSegment StartX=-49.19 StartY=11.5 StartZ=0 EndX=-49.19 EndY=8.5 EndZ=0
    g23: LineSegment StartX=-49.19 StartY=5.75 StartZ=0 EndX=-49.19 EndY=2.75 EndZ=0
  constraints (48):
    c: Block(g0)
    c: Block(g1)
    c: Block(g2)
    c: Block(g3)
    c: Block(g4)
    c: Block(g5)
    c: Block(g6)
    c: Block(g7)
    c: Block(g8)
    c: Block(g9)
    c: Block(g10)
    c: Block(g11)
    c: Coincident(g12,g0)
    c: Coincident(g12,g0)
    c: Vertical(g12)
    c: Vertical(g13)
    c: Coincident(g13,g1)
    c: Vertical(g14)
    c: Coincident(g14,g2)
    c: Vertical(g15)
    c: Coincident(g15,g3)
    c: Vertical(g16)
    c: Coincident(g16,g4)
    c: Vertical(g17)
    c: Coincident(g17,g5)
    c: Vertical(g18)
    c: Coincident(g18,g6)
    c: Vertical(g19)
    c: Coincident(g19,g7)
    c: Vertical(g20)
    c: Coincident(g20,g8)
    c: Vertical(g21)
    c: Coincident(g21,g9)
    c: Vertical(g22)
    c: Coincident(g22,g10)
    c: Vertical(g23)
    c: Coincident(g23,g11)
    c: Block(g23)
    c: Block(g22)
    c: Block(g21)
    c: Block(g20)
    c: Block(g13)
    c: Block(g14)
    c: Block(g15)
    c: Block(g16)
    c: Block(g17)
    c: Block(g18)
    c: Block(g19)
FEATURE [Part::Extrusion] Extrude022
  Base = -> Sketch030
  Dir = (1,-2e-16,2e-16)
  DirMode = 2
  FaceMakerClass = Part::FaceMakerBullseye
  LengthFwd = 19
  LengthRev = 0
  Placement = pos=(-19,0,0) rot=(0,0,1;0rad)
  Solid = true
  Symmetric = false
FEATURE [Part::Fillet] Fillet022
  Base = -> Extrude022
  Edges = 24 edges r=1.49: [Edge6,Edge11,Edge18,Edge23,Edge30,Edge35,Edge42,Edge47,Edge54,Edge59,Edge66,Edge71,Edge78,Edge83,Edge90,Edge95,Edge102,Edge107,Edge114,Edge119,Edge126,Edge131,Edge138,Edge143]
FEATURE [Part::Cut] Cut020  label="top010"
  Base = -> Cut019
  Tool = -> Fillet022
FEATURE [Sketcher::SketchObject] Sketch032
  FullyConstrained = true
  Placement = pos=(117,19,0) rot=(0.57735,0.57735,0.57735;2.0944rad)
  sketch-geometry (48):
    g0: LineSegment StartX=-49.19 StartY=69.25 StartZ=0 EndX=-49.19 EndY=66.25 EndZ=0
    g1: LineSegment StartX=-49.19 StartY=63.5 StartZ=0 EndX=-49.19 EndY=60.5 EndZ=0
    g2: LineSegment StartX=-49.19 StartY=57.75 StartZ=0 EndX=-49.19 EndY=54.75 EndZ=0
    g3: LineSegment StartX=-49.19 StartY=52 StartZ=0 EndX=-49.19 EndY=49 EndZ=0
    g4: LineSegment StartX=-49.19 StartY=46.25 StartZ=0 EndX=-49.19 EndY=43.25 EndZ=0
    g5: LineSegment StartX=-49.19 StartY=40.5 StartZ=0 EndX=-49.19 EndY=37.5 EndZ=0
    g6: LineSegment StartX=-49.19 StartY=34.5 StartZ=0 EndX=-49.19 EndY=31.5 EndZ=0
    g7: LineSegment StartX=-49.19 StartY=28.75 StartZ=0 EndX=-49.19 EndY=25.75 EndZ=0
    g8: LineSegment StartX=-49.19 StartY=23 StartZ=0 EndX=-49.19 EndY=20 EndZ=0
    g9: LineSegment StartX=-49.19 StartY=17.25 StartZ=0 EndX=-49.19 EndY=14.25 EndZ=0
    g10: LineSegment StartX=-49.19 StartY=11.5 StartZ=0 EndX=-49.19 EndY=8.5 EndZ=0
    g11: LineSegment StartX=-49.19 StartY=5.75 StartZ=0 EndX=-49.19 EndY=2.75 EndZ=0
    g12: ArcOfCircle CenterX=-1.5 CenterY=67.75 CenterZ=0 NormalX=0 NormalY=0 NormalZ=1 AngleXU=0 Radius=1.5 StartAngle=4.71239 EndAngle=7.85398
    g13: ArcOfCircle CenterX=-1.5 CenterY=62 CenterZ=0 NormalX=0 NormalY=0 NormalZ=1 AngleXU=0 Radius=1.5 StartAngle=4.71239 EndAngle=7.85398
    g14: ArcOfCircle CenterX=-1.5 CenterY=56.25 CenterZ=0 NormalX=0 NormalY=0 NormalZ=1 AngleXU=0 Radius=1.5 StartAngle=4.71239 EndAngle=7.85398
    g15: ArcOfCircle CenterX=-11.49 CenterY=50.5 CenterZ=0 NormalX=0 NormalY=0 NormalZ=1 AngleXU=0 Radius=1.5 StartAngle=4.71239 EndAngle=7.85398
    g16: ArcOfCircle CenterX=-16.28 CenterY=44.75 CenterZ=0 NormalX=0 NormalY=0 NormalZ=1 AngleXU=0 Radius=1.5 StartAngle=4.71239 EndAngle=7.85398
    g17: ArcOfCircle CenterX=-18.2337 CenterY=39 CenterZ=0 NormalX=0 NormalY=0 NormalZ=1 AngleXU=0 Radius=1.5 StartAngle=4.71485 EndAngle=7.85398
    g18: ArcOfCircle CenterX=-16.2837 CenterY=27.25 CenterZ=0 NormalX=0 NormalY=0 NormalZ=1 AngleXU=0 Radius=1.5 StartAngle=4.71485 EndAngle=7.85398
    g19: ArcOfCircle CenterX=-18.2337 CenterY=33 CenterZ=0 NormalX=0 NormalY=0 NormalZ=1 AngleXU=0 Radius=1.5 StartAngle=4.71485 EndAngle=7.85398
    g20: ArcOfCircle CenterX=-11.49 CenterY=21.5 CenterZ=0 NormalX=0 NormalY=0 NormalZ=1 AngleXU=0 Radius=1.5 StartAngle=4.71239 EndAngle=7.85398
    g21: ArcOfCircle CenterX=-1.5 CenterY=4.25 CenterZ=0 NormalX=0 NormalY=0 NormalZ=1 AngleXU=0 Radius=1.5 StartAngle=4.71239 EndAngle=7.85398
    g22: ArcOfCircle CenterX=-1.5 CenterY=10 CenterZ=0 NormalX=0 NormalY=0 NormalZ=1 AngleXU=0 Radius=1.5 StartAngle=4.71239 EndAngle=7.85398
    g23: ArcOfCircle CenterX=-1.5 CenterY=15.75 CenterZ=0 NormalX=0 NormalY=0 NormalZ=1 AngleXU=0 Radius=1.5 StartAngle=4.71239 EndAngle=7.85398
    g24: LineSegment StartX=-49.19 StartY=69.25 StartZ=0 EndX=-1.5 EndY=69.25 EndZ=0
    g25: LineSegment StartX=-49.19 StartY=66.25 StartZ=0 EndX=-1.5 EndY=66.25 EndZ=0
    g26: LineSegment StartX=-49.19 StartY=63.5 StartZ=0 EndX=-1.5 EndY=63.5 EndZ=0
    g27: LineSegment StartX=-49.19 StartY=60.5 StartZ=0 EndX=-1.5 EndY=60.5 EndZ=0
    g28: LineSegment StartX=-49.19 StartY=57.75 StartZ=0 EndX=-1.5 EndY=57.75 EndZ=0
    g29: LineSegment StartX=-49.19 StartY=54.75 StartZ=0 EndX=-1.5 EndY=54.75 EndZ=0
    g30: LineSegment StartX=-49.19 StartY=52 StartZ=0 EndX=-11.49 EndY=52 EndZ=0
    g31: LineSegment StartX=-49.19 StartY=49 StartZ=0 EndX=-11.49 EndY=49 EndZ=0
    g32: LineSegment StartX=-49.19 StartY=46.25 StartZ=0 EndX=-16.28 EndY=46.25 EndZ=0
    g33: LineSegment StartX=-49.19 StartY=43.25 StartZ=0 EndX=-16.28 EndY=43.25 EndZ=0
    g34: LineSegment StartX=-49.19 StartY=40.5 StartZ=0 EndX=-18.2337 EndY=40.5 EndZ=0
    g35: LineSegment StartX=-49.19 StartY=37.5 StartZ=0 EndX=-18.23 EndY=37.5 EndZ=0
    g36: LineSegment StartX=-49.19 StartY=34.5 StartZ=0 EndX=-18.2337 EndY=34.5 EndZ=0
    g37: LineSegment StartX=-49.19 StartY=31.5 StartZ=0 EndX=-18.23 EndY=31.5 EndZ=0
    g38: LineSegment StartX=-49.19 StartY=28.75 StartZ=0 EndX=-16.2837 EndY=28.75 EndZ=0
    g39: LineSegment StartX=-49.19 StartY=25.75 StartZ=0 EndX=-16.28 EndY=25.75 EndZ=0
    g40: LineSegment StartX=-49.19 StartY=23 StartZ=0 EndX=-11.49 EndY=23 EndZ=0
    g41: LineSegment StartX=-49.19 StartY=20 StartZ=0 EndX=-11.49 EndY=20 EndZ=0
    g42: LineSegment StartX=-49.19 StartY=17.25 StartZ=0 EndX=-1.5 EndY=17.25 EndZ=0
    g43: LineSegment StartX=-49.19 StartY=14.25 StartZ=0 EndX=-1.5 EndY=14.25 EndZ=0
    g44: LineSegment StartX=-49.19 StartY=11.5 StartZ=0 EndX=-1.5 EndY=11.5 EndZ=0
    g45: LineSegment StartX=-49.19 StartY=8.5 StartZ=0 EndX=-1.5 EndY=8.5 EndZ=0
    g46: LineSegment StartX=-49.19 StartY=5.75 StartZ=0 EndX=-1.5 EndY=5.75 EndZ=0
    g47: LineSegment StartX=-49.19 StartY=2.75 StartZ=0 EndX=-1.5 EndY=2.75 EndZ=0
  constraints (120):
    c: Vertical(g0)
    c: Distance(g0) = 3
    c: Block(g0)
    c: Vertical(g1)
    c: Distance(g1) = 3
    c: Vertical(g2)
    c: Equal(g0,g2) = 3
    c: Block(g2)
    c: Vertical(g3)
    c: Equal(g1,g3) = 3
    c: Vertical(g4)
    c: Equal(g0,g4) = 3
    c: Block(g4)
    c: Vertical(g5)
    c: Equal(g1,g5) = 3
    c: Vertical(g6)
    c: Equal(g0,g6) = 3
    c: Block(g6)
    c: Vertical(g7)
    c: Equal(g1,g7) = 3
    c: Vertical(g8)
    c: Equal(g0,g8) = 3
    c: Block(g8)
    c: Vertical(g9)
    c: Equal(g1,g9) = 3
    c: Vertical(g10)
    c: Equal(g0,g10) = 3
    c: Block(g10)
    c: Vertical(g11)
    c: Equal(g1,g11) = 3
    c: Block(g12)
    c: Block(g13)
    c: Block(g14)
    c: Block(g15)
    c: Block(g16)
    c: Block(g17)
    c: Block(g18)
    c: Block(g19)
    c: Block(g20)
    c: Block(g21)
    c: Block(g22)
    c: Block(g23)
    c: Block(g11)
    c: Block(g9)
    c: Block(g7)
    c: Block(g5)
    c: Block(g3)
    c: Block(g1)
    c: Coincident(g24,g0)
    c: Coincident(g24,g12)
    c: Horizontal(g24)
    c: Coincident(g25,g0)
    c: Coincident(g25,g12)
    c: Horizontal(g25)
    c: Coincident(g26,g1)
    c: Coincident(g26,g13)
    c: Horizontal(g26)
    c: Coincident(g27,g1)
    c: Coincident(g27,g13)
    c: Horizontal(g27)
    c: Coincident(g28,g2)
    c: Coincident(g28,g14)
    c: Horizontal(g28)
    c: Coincident(g29,g2)
    c: Coincident(g29,g14)
    c: Horizontal(g29)
    c: Coincident(g30,g3)
    c: Coincident(g30,g15)
    c: Horizontal(g30)
    c: Coincident(g31,g3)
    c: Coincident(g31,g15)
    c: Horizontal(g31)
    c: Coincident(g32,g4)
    c: Coincident(g32,g16)
    c: Horizontal(g32)
    c: Coincident(g33,g4)
    c: Coincident(g33,g16)
    c: Horizontal(g33)
    c: Coincident(g34,g5)
    c: Coincident(g34,g17)
    c: Horizontal(g34)
    c: Coincident(g35,g5)
    c: Coincident(g35,g17)
    c: Horizontal(g35)
    c: Coincident(g36,g6)
    c: Coincident(g36,g19)
    c: Horizontal(g36)
    c: Coincident(g37,g6)
    c: Coincident(g37,g19)
    c: Horizontal(g37)
    c: Coincident(g38,g7)
    c: Coincident(g38,g18)
    c: Horizontal(g38)
    c: Coincident(g39,g7)
    c: Coincident(g39,g18)
    c: Horizontal(g39)
    c: Coincident(g40,g8)
    c: Coincident(g40,g20)
    c: Horizontal(g40)
    c: Coincident(g41,g8)
    c: Coincident(g41,g20)
    c: Horizontal(g41)
    c: Coincident(g42,g9)
    c: Coincident(g42,g23)
    c: Horizontal(g42)
    c: Coincident(g43,g9)
    c: Coincident(g43,g23)
    c: Horizontal(g43)
    c: Coincident(g44,g10)
    c: Coincident(g44,g22)
    c: Horizontal(g44)
    c: Coincident(g45,g10)
    c: Coincident(g45,g22)
    c: Horizontal(g45)
    c: Coincident(g46,g11)
    c: Coincident(g46,g21)
    c: Horizontal(g46)
    c: Coincident(g47,g11)
    c: Coincident(g47,g21)
    c: Horizontal(g47)
FEATURE [Part::Extrusion] Extrude023
  Base = -> Sketch032
  Dir = (1,-2e-16,2e-16)
  DirMode = 2
  FaceMakerClass = Part::FaceMakerBullseye
  LengthFwd = 19
  LengthRev = 0
  Placement = pos=(-19,0,0) rot=(0,0,1;0rad)
  Solid = true
  Symmetric = false
FEATURE [Part::Fillet] Fillet023
  Base = -> Extrude023
  Edges = <same value as first occurrence — deduplicated (x6 in doc)>
  Placement = pos=(0,0.05,0) rot=(0,0,1;0rad)
FEATURE [Part::Cut] Cut014  label="bottom003"
  Base = -> Cut007
  Tool = -> Fusion047
FEATURE [Part::Cut] Cut021  label="bottom004"
  Base = -> Cut014
  Tool = -> Fillet023
FEATURE [Sketcher::SketchObject] Sketch033
  FullyConstrained = true
  Placement = pos=(117,19,0) rot=(0.57735,0.57735,0.57735;2.0944rad)
  sketch-geometry (8):
    g0: LineSegment StartX=-49.19 StartY=69.25 StartZ=0 EndX=-49.19 EndY=66.25 EndZ=0
    g1: LineSegment StartX=-49.19 StartY=5.75 StartZ=0 EndX=-49.19 EndY=2.75 EndZ=0
    g2: ArcOfCircle CenterX=-1.5 CenterY=67.75 CenterZ=0 NormalX=0 NormalY=0 NormalZ=1 AngleXU=0 Radius=1.5 StartAngle=4.71239 EndAngle=7.85398
    g3: ArcOfCircle CenterX=-1.5 CenterY=4.25 CenterZ=0 NormalX=0 NormalY=0 NormalZ=1 AngleXU=0 Radius=1.5 StartAngle=4.71239 EndAngle=7.85398
    g4: LineSegment StartX=-49.19 StartY=69.25 StartZ=0 EndX=-1.5 EndY=69.25 EndZ=0
    g5: LineSegment StartX=-49.19 StartY=66.25 StartZ=0 EndX=-1.5 EndY=66.25 EndZ=0
    g6: LineSegment StartX=-49.19 StartY=5.75 StartZ=0 EndX=-1.5 EndY=5.75 EndZ=0
    g7: LineSegment StartX=-49.19 StartY=2.75 StartZ=0 EndX=-1.5 EndY=2.75 EndZ=0
  constraints (19):
    c: Vertical(g0)
    c: Distance(g0) = 3
    c: Block(g0)
    c: Vertical(g1)
    c: Block(g2)
    c: Block(g3)
    c: Block(g1)
    c: Coincident(g4,g0)
    c: Coincident(g4,g2)
    c: Horizontal(g4)
    c: Coincident(g5,g0)
    c: Coincident(g5,g2)
    c: Horizontal(g5)
    c: Coincident(g6,g1)
    c: Coincident(g6,g3)
    c: Horizontal(g6)
    c: Coincident(g7,g1)
    c: Coincident(g7,g3)
    c: Horizontal(g7)
FEATURE [Sketcher::SketchObject] Sketch034
  FullyConstrained = true
  Placement = pos=(117,19,0) rot=(0.57735,0.57735,0.57735;2.0944rad)
  sketch-geometry (8):
    g0: LineSegment StartX=-49.19 StartY=63.5 StartZ=0 EndX=-49.19 EndY=60.5 EndZ=0
    g1: LineSegment StartX=-49.19 StartY=11.5 StartZ=0 EndX=-49.19 EndY=8.5 EndZ=0
    g2: ArcOfCircle CenterX=-1.5 CenterY=62 CenterZ=0 NormalX=0 NormalY=0 NormalZ=1 AngleXU=0 Radius=1.5 StartAngle=4.71239 EndAngle=7.85398
    g3: ArcOfCircle CenterX=-1.5 CenterY=10 CenterZ=0 NormalX=0 NormalY=0 NormalZ=1 AngleXU=0 Radius=1.5 StartAngle=4.71239 EndAngle=7.85398
    g4: LineSegment StartX=-49.19 StartY=63.5 StartZ=0 EndX=-1.5 EndY=63.5 EndZ=0
    g5: LineSegment StartX=-49.19 StartY=60.5 StartZ=0 EndX=-1.5 EndY=60.5 EndZ=0
    g6: LineSegment StartX=-49.19 StartY=11.5 StartZ=0 EndX=-1.5 EndY=11.5 EndZ=0
    g7: LineSegment StartX=-49.19 StartY=8.5 StartZ=0 EndX=-1.5 EndY=8.5 EndZ=0
  constraints (19):
    c: Vertical(g0)
    c: Distance(g0) = 3
    c: Vertical(g1)
    c: Block(g1)
    c: Block(g2)
    c: Block(g3)
    c: Block(g0)
    c: Coincident(g4,g0)
    c: Coincident(g4,g2)
    c: Horizontal(g4)
    c: Coincident(g5,g0)
    c: Coincident(g5,g2)
    c: Horizontal(g5)
    c: Coincident(g6,g1)
    c: Coincident(g6,g3)
    c: Horizontal(g6)
    c: Coincident(g7,g1)
    c: Coincident(g7,g3)
    c: Horizontal(g7)
FEATURE [Part::Extrusion] Extrude024
  Base = -> Sketch033
  Dir = (1,0,0)
  DirMode = 2
  FaceMakerClass = Part::FaceMakerBullseye
  LengthFwd = 10
  LengthRev = 0
  Solid = true
  Symmetric = false
FEATURE [Part::Extrusion] Extrude025
  Base = -> Sketch034
  Dir = (1,0,0)
  DirMode = 2
  FaceMakerClass = Part::FaceMakerBullseye
  LengthFwd = 10
  LengthRev = 0
  Solid = true
  Symmetric = false
FEATURE [Part::Fillet] Fillet024  label="removeFromtMoreFrontCaseScrewRetainers"
  Base = -> Extrude024
  Edges = 4 edges r=1.49: [Edge6,Edge11,Edge18,Edge23]
  Placement = pos=(-11,0,0) rot=(0,0,1;0rad)
FEATURE [Part::Fillet] Fillet025  label="removeFromtMoreFrontCaseScrewRetainers001"
  Base = -> Extrude025
  Edges = 4 edges r=1.49: [Edge6,Edge11,Edge18,Edge23]
  Placement = pos=(-19,0,0) rot=(0,0,1;0rad)
FEATURE [Part::Cut] Cut022
  Base = -> Cut015
  Tool = -> Fillet025
FEATURE [Part::Cut] Cut023  label="screwRetainers"
  Base = -> Cut022
  Tool = -> Fillet024
FEATURE [Part::MultiFuse] Fusion056  label="bottom005"
  Shapes = -> [Fusion044,Cut021]
FEATURE [Part::MultiFuse] Fusion057  label="casePillars001"
  Shapes = -> [Cut016,Fusion052]
FEATURE [Part::MultiFuse] Fusion058  label="bottom006"
  Shapes = -> [Fusion056,Cut023]
FEATURE [Part::MultiFuse] Fusion059  label="bottom007"
  Shapes = -> [Fusion058,Fillet005]
FEATURE [Part::MultiFuse] Fusion060  label="bottom008"
  Shapes = -> [Fusion059,Fusion]
FEATURE [Part::MultiFuse] Fusion061  label="top011"
  Shapes = -> [Cut006,Cut020]
FEATURE [Part::MultiFuse] Fusion062  label="top012"
  Shapes = -> [Fusion057,Fusion061]
FEATURE [Sketcher::SketchObject] Sketch035  label="topSketch007"
  FullyConstrained = true
  sketch-geometry (6):
    g0: LineSegment StartX=19 StartY=38 StartZ=0 EndX=117 EndY=38 EndZ=0
    g1: ArcOfCircle CenterX=19 CenterY=19 CenterZ=0 NormalX=0 NormalY=0 NormalZ=1 AngleXU=0 Radius=19 StartAngle=1.5708 EndAngle=3.14159
    g2: LineSegment StartX=117 StartY=38 StartZ=0 EndX=117 EndY=19 EndZ=0
    g3: LineSegment StartX=98 StartY=1.0161e-12 StartZ=0 EndX=5.22862e-06 EndY=1.0161e-12 EndZ=0
    g4: LineSegment StartX=5.22862e-06 StartY=19 StartZ=0 EndX=5.22862e-06 EndY=1.0161e-12 EndZ=0
    g5: ArcOfCircle CenterX=98 CenterY=19 CenterZ=0 NormalX=0 NormalY=0 NormalZ=1 AngleXU=0 Radius=19 StartAngle=4.71239 EndAngle=6.28319
  constraints (16):
    c: Horizontal(g0)
    c: Distance(g0) = 98
    c: Coincident(g1,g0)
    c: Block(g1)
    c: Coincident(g2,g0)
    c: Vertical(g2)
    c: Distance(g2) = 19
    c: Horizontal(g3)
    c: Coincident(g4,g1)
    c: Vertical(g4)
    c: Coincident(g3,g4)
    c: Block(g3)
    c: Coincident(g5,g2)
    c: Coincident(g5,g3)
    c: Block(g0)
    c: Block(g5)
FEATURE [Part::Extrusion] Extrude026  label="sideA001"
  Base = -> Sketch035
  Dir = (0,0,1)
  DirMode = 2
  FaceMakerClass = Part::FaceMakerBullseye
  LengthFwd = 3
  LengthRev = 0
  Placement = pos=(0,0,-2.7) rot=(0,0,1;0rad)
  Solid = true
  Symmetric = false
FEATURE [Sketcher::SketchObject] Sketch036  label="topSketch008"
  FullyConstrained = true
  sketch-geometry (6):
    g0: LineSegment StartX=19 StartY=38 StartZ=0 EndX=117 EndY=38 EndZ=0
    g1: ArcOfCircle CenterX=19 CenterY=19 CenterZ=0 NormalX=0 NormalY=0 NormalZ=1 AngleXU=0 Radius=19 StartAngle=1.5708 EndAngle=3.14159
    g2: LineSegment StartX=117 StartY=38 StartZ=0 EndX=117 EndY=19 EndZ=0
    g3: LineSegment StartX=98 StartY=1.0161e-12 StartZ=0 EndX=5.22862e-06 EndY=1.0161e-12 EndZ=0
    g4: LineSegment StartX=5.22862e-06 StartY=19 StartZ=0 EndX=5.22862e-06 EndY=1.0161e-12 EndZ=0
    g5: ArcOfCircle CenterX=98 CenterY=19 CenterZ=0 NormalX=0 NormalY=0 NormalZ=1 AngleXU=0 Radius=19 StartAngle=4.71239 EndAngle=6.28319
  constraints (16):
    c: Horizontal(g0)
    c: Distance(g0) = 98
    c: Coincident(g1,g0)
    c: Block(g1)
    c: Coincident(g2,g0)
    c: Vertical(g2)
    c: Distance(g2) = 19
    c: Horizontal(g3)
    c: Coincident(g4,g1)
    c: Vertical(g4)
    c: Coincident(g3,g4)
    c: Block(g3)
    c: Coincident(g5,g2)
    c: Coincident(g5,g3)
    c: Block(g0)
    c: Block(g5)
FEATURE [Part::Extrusion] Extrude027  label="sideB001"
  Base = -> Sketch036
  Dir = (0,0,1)
  DirMode = 2
  FaceMakerClass = Part::FaceMakerBullseye
  LengthFwd = 3
  LengthRev = 0
  Placement = pos=(0,0,71.7) rot=(0,0,1;0rad)
  Solid = true
  Symmetric = false
FEATURE [Part::MultiFuse] Fusion064  label="removeFromBottom"
  Shapes = -> [Extrude026,Extrude027]
FEATURE [Part::Cut] Cut024  label="bottom009"
  Base = -> Fusion060
  Tool = -> Fusion064
FEATURE [Sketcher::SketchObject] Sketch037  label="topSketch009"
  FullyConstrained = true
  sketch-geometry (8):
    g0: ArcOfCircle CenterX=19 CenterY=19.1201 CenterZ=0 NormalX=0 NormalY=0 NormalZ=1 AngleXU=0 Radius=18.8799 StartAngle=1.5708 EndAngle=3.14793
    g1: LineSegment StartX=0.120501 StartY=19.0004 StartZ=0 EndX=0.120501 EndY=0.000382114 EndZ=0
    g2: LineSegment StartX=19 StartY=38 StartZ=0 EndX=124 EndY=38 EndZ=0
    g3: LineSegment StartX=0.120501 StartY=0.000382114 StartZ=0 EndX=105.121 EndY=0.000382114 EndZ=0
    g4: LineSegment StartX=124 StartY=38 StartZ=0 EndX=125.616 EndY=38 EndZ=0
    g5: LineSegment StartX=105.121 StartY=0.000382114 StartZ=0 EndX=106.736 EndY=0.000382114 EndZ=0
    g6: ArcOfCircle CenterX=106.616 CenterY=19 CenterZ=0 NormalX=0 NormalY=0 NormalZ=1 AngleXU=0 Radius=19 StartAngle=4.71873 EndAngle=6.28319
    g7: LineSegment StartX=125.616 StartY=38 StartZ=0 EndX=125.616 EndY=19 EndZ=0
  constraints (21):
    c: Block(g0)
    c: Coincident(g1,g0)
    c: Vertical(g1)
    c: Horizontal(g2)
    c: Distance(g2) = 105
    c: Coincident(g2,g0)
    c: Distance(g1) = 19
    c: Coincident(g3,g1)
    c: Horizontal(g3)
    c: Distance(g3) = 105
    c: Coincident(g4,g2)
    c: Horizontal(g4)
    c: Distance(g4) = 1.61553
    c: Horizontal(g5)
    c: Equal(g4,g5) = 1.61553
    c: Coincident(g5,g3)
    c: Block(g6)
    c: Coincident(g6,g5)
    c: Coincident(g7,g4)
    c: Coincident(g7,g6)
    c: Vertical(g7)
FEATURE [Part::Extrusion] Extrude028  label="sideB"
  Base = -> Sketch037
  Dir = (0,0,1)
  DirMode = 2
  FaceMakerClass = Part::FaceMakerBullseye
  LengthFwd = 3
  LengthRev = 0
  Placement = pos=(0,0,72) rot=(0,0,1;0rad)
  Solid = true
  Symmetric = false
FEATURE [Sketcher::SketchObject] Sketch038  label="topSketch010"
  FullyConstrained = true
  sketch-geometry (22):
    g0: LineSegment StartX=5.21097e-06 StartY=3 StartZ=0 EndX=5.21097e-06 EndY=19 EndZ=0
    g1: ArcOfCircle CenterX=19 CenterY=19 CenterZ=0 NormalX=0 NormalY=0 NormalZ=1 AngleXU=0 Radius=19 StartAngle=1.5708 EndAngle=3.14159
    g2: ArcOfCircle CenterX=19 CenterY=19 CenterZ=0 NormalX=0 NormalY=0 NormalZ=1 AngleXU=0 Radius=16 StartAngle=1.5708 EndAngle=3.14159
    g3: LineSegment StartX=114 StartY=35 StartZ=0 EndX=19 EndY=35 EndZ=0
    g4: LineSegment StartX=5.21097e-06 StartY=3 StartZ=0 EndX=5.21097e-06 EndY=0 EndZ=0
    g5: LineSegment StartX=3 StartY=0 StartZ=0 EndX=5.21097e-06 EndY=0 EndZ=0
    g6: LineSegment StartX=3 StartY=19 StartZ=0 EndX=3 EndY=0 EndZ=0
    g7: LineSegment StartX=19 StartY=38 StartZ=0 EndX=124 EndY=38 EndZ=0
    g8: Circle CenterX=119 CenterY=35 CenterZ=0 NormalX=0 NormalY=0 NormalZ=1 AngleXU=0 Radius=1
    g9: Circle CenterX=121 CenterY=35 CenterZ=0 NormalX=0 NormalY=0 NormalZ=1 AngleXU=0 Radius=1
    g10: Circle CenterX=121 CenterY=33 CenterZ=0 NormalX=0 NormalY=0 NormalZ=1 AngleXU=0 Radius=1
    g11: BSplineCurve PolesCount=3 KnotsCount=2 Degree=2 IsPeriodic=0
    g12: GeomPoint X=119 Y=35 Z=0
    g13: GeomPoint X=121 Y=33 Z=0
    g14: LineSegment StartX=119 StartY=35 StartZ=0 EndX=114 EndY=35 EndZ=0
    g15: ArcOfCircle CenterX=105 CenterY=19 CenterZ=0 NormalX=0 NormalY=0 NormalZ=1 AngleXU=0 Radius=16 StartAngle=5.60905 EndAngle=6.28319
    g16: LineSegment StartX=121 StartY=33 StartZ=0 EndX=121 EndY=19 EndZ=0
    g17: LineSegment StartX=117.5 StartY=9.01251 StartZ=0 EndX=121.163 EndY=9.0125 EndZ=0
    g18: ArcOfCircle CenterX=105 CenterY=19 CenterZ=0 NormalX=0 NormalY=0 NormalZ=1 AngleXU=0 Radius=20.6155 StartAngle=5.7297 EndAngle=6.28319
    g19: LineSegment StartX=121.163 StartY=9.0125 StartZ=0 EndX=122.538 EndY=8.16329 EndZ=0
    g20: LineSegment StartX=124 StartY=38 StartZ=0 EndX=125.616 EndY=38 EndZ=0
    g21: LineSegment StartX=125.616 StartY=19 StartZ=0 EndX=125.616 EndY=38 EndZ=0
  constraints (49):
    c: Vertical(g0)
    c: Block(g0)
    c: Coincident(g1,g0)
    c: Block(g1)
    c: Coincident(g2,g1)
    c: Block(g2)
    c: Coincident(g3,g2)
    c: Horizontal(g3)
    c: Tangent(g3,g2)
    c: Coincident(g4,g0)
    c: Distance(g4) = 3
    c: Vertical(g4)
    c: Coincident(g5,g4)
    c: Horizontal(g5)
    c: Coincident(g6,g2)
    c: Coincident(g6,g5)
    c: Vertical(g6)
    c: Horizontal(g7)
    c: Distance(g7) = 105
    c: Coincident(g7,g1)
    c: Block(g3)
    c: Weight(g8) = 1
    c: Equal(g8,g9)
    c: Equal(g8,g10)
    c: InternalAlignment(g8,g11)
    c: InternalAlignment(g9,g11)
    c: InternalAlignment(g10,g11)
    c: InternalAlignment(g12,g11)
    c: InternalAlignment(g13,g11)
    c: Block(g11)
    c: Coincident(g14,g11)
    c: Coincident(g14,g3)
    c: Horizontal(g14)
    c: Block(g15)
    c: Coincident(g16,g11)
    c: Coincident(g16,g15)
    c: Vertical(g16)
    c: Distance(g16) = 14
    c: Coincident(g17,g15)
    c: Block(g18)
    c: Coincident(g19,g18)
    c: Coincident(g20,g7)
    c: Horizontal(g20)
    c: Vertical(g21)
    c: Coincident(g20,g21)
    c: Block(g20)
    c: Block(g21)
    c: Block(g19)
    c: Block(g17)
FEATURE [Part::Extrusion] Extrude029
  Base = -> Sketch038
  Dir = (0,0,1)
  DirMode = 2
  FaceMakerClass = Part::FaceMakerBullseye
  LengthFwd = 72
  LengthRev = 0
  Solid = true
  Symmetric = false
FEATURE [Part::Feature] Face085
  shape: bbox 4.8 x 25.5 x 2e-07 mm, 1 faces, 0 solids (baked)
FEATURE [Part::Revolution] Revolve089  label="moreFrontCaseScrewPost003"
  Angle = 360
  Axis = (0,1,0)
  Base = (0,0,0)
  FaceMakerClass = Part::FaceMakerBullseye
  Placement = pos=(109.5,4.5,3.5) rot=(0,0,1;0rad)
  Solid = false
  Source = -> Face085
  Symmetric = false
FEATURE [Part::Feature] Face086
  shape: bbox 4.8 x 25.5 x 2e-07 mm, 1 faces, 0 solids (baked)
FEATURE [Part::Revolution] Revolve090  label="moreFrontCaseScrewPost004"
  Angle = 360
  Axis = (0,1,0)
  Base = (0,0,0)
  FaceMakerClass = Part::FaceMakerBullseye
  Placement = pos=(109.5,4.5,68.5) rot=(0,0,1;0rad)
  Solid = false
  Source = -> Face086
  Symmetric = false
FEATURE [Part::Fillet] Fillet026  label="top013"
  Base = -> Extrude029
  Edges = 1 edges r=2: [Edge35]
FEATURE [Sketcher::SketchObject] Sketch039
  FullyConstrained = true
  sketch-geometry (7):
    g0: LineSegment StartX=0 StartY=0 StartZ=0 EndX=0 EndY=6 EndZ=0
    g1: Circle CenterX=0 CenterY=0 CenterZ=0 NormalX=0 NormalY=0 NormalZ=1 AngleXU=0 Radius=1
    g2: Circle CenterX=8 CenterY=6 CenterZ=0 NormalX=0 NormalY=0 NormalZ=1 AngleXU=0 Radius=1
    g3: BSplineCurve PolesCount=3 KnotsCount=2 Degree=2 IsPeriodic=0
    g4: GeomPoint X=0 Y=0 Z=0
    g5: GeomPoint X=8 Y=6 Z=0
    g6: LineSegment StartX=0 StartY=6 StartZ=0 EndX=8 EndY=6 EndZ=0
  constraints (14):
    c: Coincident(g0,g-1)
    c: Distance(g0) = 6
    c: Vertical(g0)
    c: Coincident(g3,g0)
    c: Weight(g1) = 1
    c: Equal(g1,g2)
    c: InternalAlignment(g1,g3)
    c: InternalAlignment(g2,g3)
    c: InternalAlignment(g4,g3)
    c: InternalAlignment(g5,g3)
    c: Block(g3)
    c: Coincident(g6,g0)
    c: Coincident(g6,g3)
    c: Horizontal(g6)
FEATURE [Sketcher::SketchObject] Sketch040
  FullyConstrained = true
  sketch-geometry (7):
    g0: LineSegment StartX=0 StartY=0 StartZ=0 EndX=0 EndY=6 EndZ=0
    g1: Circle CenterX=0 CenterY=0 CenterZ=0 NormalX=0 NormalY=0 NormalZ=1 AngleXU=0 Radius=1
    g2: Circle CenterX=8 CenterY=6 CenterZ=0 NormalX=0 NormalY=0 NormalZ=1 AngleXU=0 Radius=1
    g3: BSplineCurve PolesCount=3 KnotsCount=2 Degree=2 IsPeriodic=0
    g4: GeomPoint X=0 Y=0 Z=0
    g5: GeomPoint X=8 Y=6 Z=0
    g6: LineSegment StartX=0 StartY=6 StartZ=0 EndX=8 EndY=6 EndZ=0
  constraints (14):
    c: Coincident(g0,g-1)
    c: Distance(g0) = 6
    c: Vertical(g0)
    c: Coincident(g3,g0)
    c: Weight(g1) = 1
    c: Equal(g1,g2)
    c: InternalAlignment(g1,g3)
    c: InternalAlignment(g2,g3)
    c: InternalAlignment(g4,g3)
    c: InternalAlignment(g5,g3)
    c: Block(g3)
    c: Coincident(g6,g0)
    c: Coincident(g6,g3)
    c: Horizontal(g6)
FEATURE [Sketcher::SketchObject] Sketch041
  FullyConstrained = true
  sketch-geometry (7):
    g0: LineSegment StartX=0 StartY=0 StartZ=0 EndX=0 EndY=6 EndZ=0
    g1: Circle CenterX=0 CenterY=0 CenterZ=0 NormalX=0 NormalY=0 NormalZ=1 AngleXU=0 Radius=1
    g2: Circle CenterX=8 CenterY=6 CenterZ=0 NormalX=0 NormalY=0 NormalZ=1 AngleXU=0 Radius=1
    g3: BSplineCurve PolesCount=3 KnotsCount=2 Degree=2 IsPeriodic=0
    g4: GeomPoint X=0 Y=0 Z=0
    g5: GeomPoint X=8 Y=6 Z=0
    g6: LineSegment StartX=0 StartY=6 StartZ=0 EndX=8 EndY=6 EndZ=0
  constraints (14):
    c: Coincident(g0,g-1)
    c: Distance(g0) = 6
    c: Vertical(g0)
    c: Coincident(g3,g0)
    c: Weight(g1) = 1
    c: Equal(g1,g2)
    c: InternalAlignment(g1,g3)
    c: InternalAlignment(g2,g3)
    c: InternalAlignment(g4,g3)
    c: InternalAlignment(g5,g3)
    c: Block(g3)
    c: Coincident(g6,g0)
    c: Coincident(g6,g3)
    c: Horizontal(g6)
FEATURE [Sketcher::SketchObject] Sketch042
  FullyConstrained = true
  sketch-geometry (7):
    g0: LineSegment StartX=0 StartY=0 StartZ=0 EndX=0 EndY=6 EndZ=0
    g1: Circle CenterX=0 CenterY=0 CenterZ=0 NormalX=0 NormalY=0 NormalZ=1 AngleXU=0 Radius=1
    g2: Circle CenterX=8 CenterY=6 CenterZ=0 NormalX=0 NormalY=0 NormalZ=1 AngleXU=0 Radius=1
    g3: BSplineCurve PolesCount=3 KnotsCount=2 Degree=2 IsPeriodic=0
    g4: GeomPoint X=0 Y=0 Z=0
    g5: GeomPoint X=8 Y=6 Z=0
    g6: LineSegment StartX=0 StartY=6 StartZ=0 EndX=8 EndY=6 EndZ=0
  constraints (14):
    c: Coincident(g0,g-1)
    c: Distance(g0) = 6
    c: Vertical(g0)
    c: Coincident(g3,g0)
    c: Weight(g1) = 1
    c: Equal(g1,g2)
    c: InternalAlignment(g1,g3)
    c: InternalAlignment(g2,g3)
    c: InternalAlignment(g4,g3)
    c: InternalAlignment(g5,g3)
    c: Block(g3)
    c: Coincident(g6,g0)
    c: Coincident(g6,g3)
    c: Horizontal(g6)
FEATURE [Part::Extrusion] Extrude030  label="caseScrewPillarBracket008"
  Base = -> Sketch039
  Dir = (0,0,1)
  DirMode = 2
  FaceMakerClass = Part::FaceMakerBullseye
  LengthFwd = 2.4
  LengthRev = 0
  Placement = pos=(15.76,29,8.8) rot=(0,1,0;0rad)
  Solid = true
  Symmetric = false
FEATURE [Part::Extrusion] Extrude031  label="caseScrewPillarBracket009"
  Base = -> Sketch040
  Dir = (0,0,1)
  DirMode = 2
  FaceMakerClass = Part::FaceMakerBullseye
  LengthFwd = 2.4
  LengthRev = 0
  Placement = pos=(15.76,29,60.8) rot=(0,0,1;0rad)
  Solid = true
  Symmetric = false
FEATURE [Part::Extrusion] Extrude032  label="caseScrewPillarBracket010"
  Base = -> Sketch041
  Dir = (0,0,1)
  DirMode = 2
  FaceMakerClass = Part::FaceMakerBullseye
  LengthFwd = 2.4
  LengthRev = 0
  Placement = pos=(13.7,29,13.26) rot=(0,-1,0;1.5708rad)
  Solid = true
  Symmetric = false
FEATURE [Part::Extrusion] Extrude033  label="caseScrewPillarBracket011"
  Base = -> Sketch042
  Dir = (0,0,1)
  DirMode = 2
  FaceMakerClass = Part::FaceMakerBullseye
  LengthFwd = 2.4
  LengthRev = 0
  Placement = pos=(11.3,29,58.74) rot=(0,1,0;1.5708rad)
  Solid = true
  Symmetric = false
FEATURE [Sketcher::SketchObject] Sketch043
  FullyConstrained = true
  sketch-geometry (7):
    g0: LineSegment StartX=0 StartY=0 StartZ=0 EndX=0 EndY=6 EndZ=0
    g1: Circle CenterX=0 CenterY=0 CenterZ=0 NormalX=0 NormalY=0 NormalZ=1 AngleXU=0 Radius=1
    g2: Circle CenterX=8 CenterY=6 CenterZ=0 NormalX=0 NormalY=0 NormalZ=1 AngleXU=0 Radius=1
    g3: BSplineCurve PolesCount=3 KnotsCount=2 Degree=2 IsPeriodic=0
    g4: GeomPoint X=0 Y=0 Z=0
    g5: GeomPoint X=8 Y=6 Z=0
    g6: LineSegment StartX=0 StartY=6 StartZ=0 EndX=8 EndY=6 EndZ=0
  constraints (14):
    c: Coincident(g0,g-1)
    c: Distance(g0) = 6
    c: Vertical(g0)
    c: Coincident(g3,g0)
    c: Weight(g1) = 1
    c: Equal(g1,g2)
    c: InternalAlignment(g1,g3)
    c: InternalAlignment(g2,g3)
    c: InternalAlignment(g4,g3)
    c: InternalAlignment(g5,g3)
    c: Block(g3)
    c: Coincident(g6,g0)
    c: Coincident(g6,g3)
    c: Horizontal(g6)
FEATURE [Part::Extrusion] Extrude034  label="caseScrewPillarBracket012"
  Base = -> Sketch043
  Dir = (0,0,1)
  DirMode = 2
  FaceMakerClass = Part::FaceMakerBullseye
  LengthFwd = 2.4
  LengthRev = 0
  Placement = pos=(88.3,29,65.23) rot=(0,1,0;1.5708rad)
  Solid = true
  Symmetric = false
FEATURE [Sketcher::SketchObject] Sketch044
  FullyConstrained = true
  sketch-geometry (7):
    g0: LineSegment StartX=0 StartY=0 StartZ=0 EndX=0 EndY=6 EndZ=0
    g1: Circle CenterX=0 CenterY=0 CenterZ=0 NormalX=0 NormalY=0 NormalZ=1 AngleXU=0 Radius=1
    g2: Circle CenterX=8 CenterY=6 CenterZ=0 NormalX=0 NormalY=0 NormalZ=1 AngleXU=0 Radius=1
    g3: BSplineCurve PolesCount=3 KnotsCount=2 Degree=2 IsPeriodic=0
    g4: GeomPoint X=0 Y=0 Z=0
    g5: GeomPoint X=8 Y=6 Z=0
    g6: LineSegment StartX=0 StartY=6 StartZ=0 EndX=8 EndY=6 EndZ=0
  constraints (14):
    c: Coincident(g0,g-1)
    c: Distance(g0) = 6
    c: Vertical(g0)
    c: Coincident(g3,g0)
    c: Weight(g1) = 1
    c: Equal(g1,g2)
    c: InternalAlignment(g1,g3)
    c: InternalAlignment(g2,g3)
    c: InternalAlignment(g4,g3)
    c: InternalAlignment(g5,g3)
    c: Block(g3)
    c: Coincident(g6,g0)
    c: Coincident(g6,g3)
    c: Horizontal(g6)
FEATURE [Part::Extrusion] Extrude035  label="caseScrewPillarBracket013"
  Base = -> Sketch044
  Dir = (0,0,1)
  DirMode = 2
  FaceMakerClass = Part::FaceMakerBullseye
  LengthFwd = 2.4
  LengthRev = 0
  Placement = pos=(90.7,29,6.77) rot=(0,-1,0;1.5708rad)
  Solid = true
  Symmetric = false
FEATURE [Sketcher::SketchObject] Sketch045
  FullyConstrained = true
  sketch-geometry (7):
    g0: LineSegment StartX=0 StartY=0 StartZ=0 EndX=0 EndY=6 EndZ=0
    g1: Circle CenterX=0 CenterY=0 CenterZ=0 NormalX=0 NormalY=0 NormalZ=1 AngleXU=0 Radius=1
    g2: Circle CenterX=8 CenterY=6 CenterZ=0 NormalX=0 NormalY=0 NormalZ=1 AngleXU=0 Radius=1
    g3: BSplineCurve PolesCount=3 KnotsCount=2 Degree=2 IsPeriodic=0
    g4: GeomPoint X=0 Y=0 Z=0
    g5: GeomPoint X=8 Y=6 Z=0
    g6: LineSegment StartX=0 StartY=6 StartZ=0 EndX=8 EndY=6 EndZ=0
  constraints (14):
    c: Coincident(g0,g-1)
    c: Distance(g0) = 6
    c: Vertical(g0)
    c: Coincident(g3,g0)
    c: Weight(g1) = 1
    c: Equal(g1,g2)
    c: InternalAlignment(g1,g3)
    c: InternalAlignment(g2,g3)
    c: InternalAlignment(g4,g3)
    c: InternalAlignment(g5,g3)
    c: Block(g3)
    c: Coincident(g6,g0)
    c: Coincident(g6,g3)
    c: Horizontal(g6)
FEATURE [Sketcher::SketchObject] Sketch046
  FullyConstrained = true
  sketch-geometry (7):
    g0: LineSegment StartX=0 StartY=0 StartZ=0 EndX=0 EndY=6 EndZ=0
    g1: Circle CenterX=0 CenterY=0 CenterZ=0 NormalX=0 NormalY=0 NormalZ=1 AngleXU=0 Radius=1
    g2: Circle CenterX=8 CenterY=6 CenterZ=0 NormalX=0 NormalY=0 NormalZ=1 AngleXU=0 Radius=1
    g3: BSplineCurve PolesCount=3 KnotsCount=2 Degree=2 IsPeriodic=0
    g4: GeomPoint X=0 Y=0 Z=0
    g5: GeomPoint X=8 Y=6 Z=0
    g6: LineSegment StartX=0 StartY=6 StartZ=0 EndX=8 EndY=6 EndZ=0
  constraints (14):
    c: Coincident(g0,g-1)
    c: Distance(g0) = 6
    c: Vertical(g0)
    c: Coincident(g3,g0)
    c: Weight(g1) = 1
    c: Equal(g1,g2)
    c: InternalAlignment(g1,g3)
    c: InternalAlignment(g2,g3)
    c: InternalAlignment(g4,g3)
    c: InternalAlignment(g5,g3)
    c: Block(g3)
    c: Coincident(g6,g0)
    c: Coincident(g6,g3)
    c: Horizontal(g6)
FEATURE [Part::Extrusion] Extrude036  label="caseScrewPillarBracket014"
  Base = -> Sketch045
  Dir = (0,0,1)
  DirMode = 2
  FaceMakerClass = Part::FaceMakerBullseye
  LengthFwd = 2.4
  LengthRev = 0
  Placement = pos=(110.7,29,6.77) rot=(0,-1,0;1.5708rad)
  Solid = true
  Symmetric = false
FEATURE [Part::Extrusion] Extrude037  label="caseScrewPillarBracket015"
  Base = -> Sketch046
  Dir = (0,0,1)
  DirMode = 2
  FaceMakerClass = Part::FaceMakerBullseye
  LengthFwd = 2.4
  LengthRev = 0
  Placement = pos=(108.3,29,65.23) rot=(0,1,0;1.5708rad)
  Solid = true
  Symmetric = false
FEATURE [Part::Box] Box013  label="frontCaseScrewPillarBracket002"
  AttacherType = Attacher::AttachEngine3D
  Height = 2.4
  Length = 22
  Placement = pos=(87,28,2.3) rot=(0,0,1;0rad)
  Width = 7
FEATURE [Part::Box] Box014  label="frontCaseScrewPillarBracket003"
  AttacherType = Attacher::AttachEngine3D
  Height = 2.4
  Length = 22
  Placement = pos=(87,28,67.3) rot=(0,0,1;0rad)
  Width = 7
FEATURE [Part::Feature] Face087
  shape: bbox 4.8 x 30.2 x 2e-07 mm, 1 faces, 0 solids (baked)
FEATURE [Part::Revolution] Revolve091  label="frontCaseScrewPost004"
  Angle = 360
  Axis = (0,1,0)
  Base = (0,0,0)
  FaceMakerClass = Part::FaceMakerBullseye
  Placement = pos=(89.5,4.5,3.5) rot=(0,0,1;0rad)
  Solid = false
  Source = -> Face087
  Symmetric = false
FEATURE [Part::Feature] Face088
  shape: bbox 4.8 x 30.2 x 2e-07 mm, 1 faces, 0 solids (baked)
FEATURE [Part::Revolution] Revolve092  label="frontCaseScrewPost005"
  Angle = 360
  Axis = (0,1,0)
  Base = (0,0,0)
  FaceMakerClass = Part::FaceMakerBullseye
  Placement = pos=(89.5,4.5,68.5) rot=(0,0,1;0rad)
  Solid = false
  Source = -> Face088
  Symmetric = false
FEATURE [Part::Feature] Face089
  shape: bbox 3.5 x 30.2 x 2e-07 mm, 1 faces, 0 solids (baked)
FEATURE [Part::Revolution] Revolve093  label="backCaseScrewPost002"
  Angle = 360
  Axis = (0,1,0)
  Base = (0,0,0)
  FaceMakerClass = Part::FaceMakerBullseye
  Placement = pos=(12.5,4.5,10) rot=(0,0,1;0rad)
  Solid = false
  Source = -> Face089
  Symmetric = false
FEATURE [Part::Feature] Face090
  shape: bbox 3.5 x 30.2 x 2e-07 mm, 1 faces, 0 solids (baked)
FEATURE [Part::Revolution] Revolve094  label="backCaseScrewPost003"
  Angle = 360
  Axis = (0,1,0)
  Base = (0,0,0)
  FaceMakerClass = Part::FaceMakerBullseye
  Placement = pos=(12.5,4.5,62) rot=(0,0,1;0rad)
  Solid = false
  Source = -> Face090
  Symmetric = false
FEATURE [Part::Box] Box015  label="Cube011"
  AttacherType = Attacher::AttachEngine3D
  Height = 28.8
  Length = 3
  Placement = pos=(107.3,28,21.6) rot=(0,0,1;0rad)
  Width = 7
FEATURE [Part::Box] Box016  label="Cube012"
  AttacherType = Attacher::AttachEngine3D
  Height = 3
  Length = 7.4
  Placement = pos=(107.3,28,18.6) rot=(0,0,1;0rad)
  Width = 7
FEATURE [Part::Box] Box017  label="Cube013"
  AttacherType = Attacher::AttachEngine3D
  Height = 3
  Length = 7.4
  Placement = pos=(107.3,28,50.4) rot=(0,0,1;0rad)
  Width = 7
FEATURE [Part::Cylinder] Cylinder024
  Angle = 360
  AttacherType = Attacher::AttachEngine3D
  Height = 20
  Placement = pos=(0,0,36.15) rot=(0,0,1;0rad)
  Radius = 14.3
FEATURE [Part::Cylinder] Cylinder025
  Angle = 360
  AttacherType = Attacher::AttachEngine3D
  Height = 10
  Placement = pos=(0,0,36.15) rot=(0,0,1;0rad)
  Radius = 4
FEATURE [Part::MultiFuse] Fusion066  label="removeToCreteHoleForPlugHousing009"
  Placement = pos=(70,19,36) rot=(0,1,0;1.5708rad)
  Shapes = -> [Cylinder024,Cylinder025]
FEATURE [Part::MultiFuse] Fusion065  label="plugHousingBracketHolder002"
  Shapes = -> [Box017,Box015,Box016]
FEATURE [Part::Cut] Cut025  label="plugHousingBracketHolder003"
  Base = -> Fusion065
  Placement = pos=(7,0,0) rot=(0,0,1;0rad)
  Tool = -> Fusion066
FEATURE [Sketcher::SketchObject] Sketch047
  FullyConstrained = false
  Placement = pos=(0,0,0) rot=(1,0,0;1.5708rad)
  sketch-geometry (24):
    g0: ArcOfCircle CenterX=-4 CenterY=-10.5 CenterZ=0 NormalX=0 NormalY=0 NormalZ=1 AngleXU=0 Radius=1.5 StartAngle=6e-16 EndAngle=3.14159
    g1: ArcOfCircle CenterX=-34.2 CenterY=-10.5 CenterZ=0 NormalX=0 NormalY=0 NormalZ=1 AngleXU=0 Radius=1.5 StartAngle=0 EndAngle=3.14159
    g2: ArcOfCircle CenterX=-34.2 CenterY=-27.7 CenterZ=0 NormalX=0 NormalY=0 NormalZ=1 AngleXU=0 Radius=1.5 StartAngle=3.14159 EndAngle=6.28319
    g3: ArcOfCircle CenterX=-4 CenterY=-27.7 CenterZ=0 NormalX=0 NormalY=0 NormalZ=1 AngleXU=0 Radius=1.5 StartAngle=3.1416 EndAngle=6.28319
    g4: ArcOfCircle CenterX=-10 CenterY=-4.3 CenterZ=0 NormalX=0 NormalY=0 NormalZ=1 AngleXU=0 Radius=1.5 StartAngle=2e-16 EndAngle=3.14159
    g5: ArcOfCircle CenterX=-16.1 CenterY=-1.8 CenterZ=0 NormalX=0 NormalY=0 NormalZ=1 AngleXU=0 Radius=1.5 StartAngle=5e-16 EndAngle=3.14159
    g6: ArcOfCircle CenterX=-22.1 CenterY=-1.8 CenterZ=0 NormalX=0 NormalY=0 NormalZ=1 AngleXU=0 Radius=1.5 StartAngle=5e-16 EndAngle=3.14159
    g7: ArcOfCircle CenterX=-28.2 CenterY=-4.3 CenterZ=0 NormalX=0 NormalY=0 NormalZ=1 AngleXU=0 Radius=1.5 StartAngle=2e-16 EndAngle=3.14159
    g8: ArcOfCircle CenterX=-10 CenterY=-33.9 CenterZ=0 NormalX=0 NormalY=0 NormalZ=1 AngleXU=0 Radius=1.5 StartAngle=3.14159 EndAngle=6.28319
    g9: ArcOfCircle CenterX=-16.1 CenterY=-36.4 CenterZ=0 NormalX=0 NormalY=0 NormalZ=1 AngleXU=0 Radius=1.5 StartAngle=3.14159 EndAngle=6.28319
    g10: ArcOfCircle CenterX=-22.1 CenterY=-36.4 CenterZ=0 NormalX=0 NormalY=0 NormalZ=1 AngleXU=0 Radius=1.5 StartAngle=3.14159 EndAngle=6.28319
    g11: ArcOfCircle CenterX=-28.2 CenterY=-33.9 CenterZ=0 NormalX=0 NormalY=0 NormalZ=1 AngleXU=0 Radius=1.5 StartAngle=3.14159 EndAngle=6.28319
    g12: LineSegment StartX=-35.7 StartY=-10.5 StartZ=0 EndX=-35.7 EndY=-27.7 EndZ=0
    g13: LineSegment StartX=-32.7 StartY=-10.5 StartZ=0 EndX=-32.7 EndY=-27.7 EndZ=0
    g14: LineSegment StartX=-29.7 StartY=-33.9 StartZ=0 EndX=-29.7 EndY=-4.3 EndZ=0
    g15: LineSegment StartX=-26.7 StartY=-33.9 StartZ=0 EndX=-26.7 EndY=-4.3 EndZ=0
    g16: LineSegment StartX=-2.5 StartY=-10.5 StartZ=0 EndX=-2.5 EndY=-27.7 EndZ=0
    g17: LineSegment StartX=-8.5 StartY=-4.3 StartZ=0 EndX=-8.5 EndY=-33.9 EndZ=0
    g18: LineSegment StartX=-5.5 StartY=-10.5 StartZ=0 EndX=-5.5 EndY=-27.7 EndZ=0
    g19: LineSegment StartX=-11.5 StartY=-4.3 StartZ=0 EndX=-11.5 EndY=-33.9 EndZ=0
    g20: LineSegment StartX=-14.6 StartY=-1.8 StartZ=0 EndX=-14.6 EndY=-36.4 EndZ=0
    g21: LineSegment StartX=-17.6 StartY=-1.8 StartZ=0 EndX=-17.6 EndY=-36.4 EndZ=0
    g22: LineSegment StartX=-20.6 StartY=-36.4 StartZ=0 EndX=-20.6 EndY=-1.8 EndZ=0
    g23: LineSegment StartX=-23.6 StartY=-1.8 StartZ=0 EndX=-23.6 EndY=-36.4 EndZ=0
  constraints (48):
    c: Block(g0)
    c: Block(g1)
    c: Block(g2)
    c: Block(g3)
    c: Block(g4)
    c: Block(g5)
    c: Block(g6)
    c: Block(g7)
    c: Block(g8)
    c: Block(g9)
    c: Block(g10)
    c: Block(g11)
    c: Coincident(g12,g1)
    c: Coincident(g12,g2)
    c: Vertical(g12)
    c: Coincident(g13,g1)
    c: Coincident(g13,g2)
    c: Vertical(g13)
    c: Coincident(g14,g11)
    c: Coincident(g14,g7)
    c: Vertical(g14)
    c: Coincident(g15,g11)
    c: Coincident(g15,g7)
    c: Vertical(g15)
    c: Coincident(g16,g0)
    c: Coincident(g16,g3)
    c: Vertical(g16)
    c: Coincident(g17,g4)
    c: Coincident(g17,g8)
    c: Vertical(g17)
    c: Coincident(g18,g0)
    c: Coincident(g18,g3)
    c: Vertical(g18)
    c: Coincident(g19,g4)
    c: Coincident(g19,g8)
    c: Vertical(g19)
    c: Coincident(g20,g5)
    c: Coincident(g20,g9)
    c: Vertical(g20)
    c: Coincident(g21,g5)
    c: Coincident(g21,g9)
    c: Vertical(g21)
    c: Coincident(g22,g10)
    c: Coincident(g22,g6)
    c: Vertical(g22)
    c: Coincident(g23,g6)
    c: Coincident(g23,g10)
    c: Vertical(g23)
FEATURE [Part::Extrusion] Extrude038  label="removeToCreateFanGrillHoles001"
  Base = -> Sketch047
  Dir = (0,-1,6e-16)
  DirMode = 2
  FaceMakerClass = Part::FaceMakerBullseye
  LengthFwd = 10
  LengthRev = 0
  Placement = pos=(65.4,44,54.82) rot=(0,0,1;0rad)
  Solid = true
  Symmetric = false
FEATURE [Part::Feature] Wire004
  shape: bbox 11 x 5.2 x 2e-07 mm, 0 faces, 0 solids (baked)
FEATURE [Part::Revolution] Revolve095
  Angle = 360
  Axis = (0,1,0)
  Base = (0,0,0)
  FaceMakerClass = Part::FaceMakerBullseye
  Placement = pos=(30.3,38,19.7) rot=(0,0,1;0rad)
  Solid = true
  Source = -> Wire004
  Symmetric = false
FEATURE [Part::Feature] Wire005
  shape: bbox 11 x 5.2 x 2e-07 mm, 0 faces, 0 solids (baked)
FEATURE [Part::Revolution] Revolve096
  Angle = 360
  Axis = (0,1,0)
  Base = (0,0,0)
  FaceMakerClass = Part::FaceMakerBullseye
  Placement = pos=(30.3,38,51.7) rot=(0,0,1;0rad)
  Solid = true
  Source = -> Wire005
  Symmetric = false
FEATURE [Part::Feature] Wire006
  shape: bbox 11 x 5.2 x 2e-07 mm, 0 faces, 0 solids (baked)
FEATURE [Part::Revolution] Revolve097
  Angle = 360
  Axis = (0,1,0)
  Base = (0,0,0)
  FaceMakerClass = Part::FaceMakerBullseye
  Placement = pos=(62.3,38,51.7) rot=(0,0,1;0rad)
  Solid = true
  Source = -> Wire006
  Symmetric = false
FEATURE [Part::Feature] Wire007
  shape: bbox 11 x 5.2 x 2e-07 mm, 0 faces, 0 solids (baked)
FEATURE [Part::Revolution] Revolve098
  Angle = 360
  Axis = (0,1,0)
  Base = (0,0,0)
  FaceMakerClass = Part::FaceMakerBullseye
  Placement = pos=(62.3,38,19.7) rot=(0,0,1;0rad)
  Solid = true
  Source = -> Wire007
  Symmetric = false
FEATURE [Part::MultiFuse] Fusion067  label="fanScrewHousing002"
  Shapes = -> [Revolve098,Revolve097,Revolve096,Revolve095]
FEATURE [Part::Feature] Face091 .. Face094  x4 (patterned run collapsed; names and placements below)
  shape: bbox 3.5 x 17.8 x 2e-07 mm, 1 faces, 0 solids (baked)
FEATURE [Part::Revolution] Revolve099  label="removeToCreateScrewAndThreadedInsertHole026"
  Angle = 360
  Axis = (0,1,0)
  Base = (0,0,0)
  FaceMakerClass = Part::FaceMakerBullseye
  Placement = pos=(62.3,30.3,19.7) rot=(0,0,1;0rad)
  Solid = false
  Source = -> Face091
  Symmetric = false
FEATURE [Part::Revolution] Revolve100  label="removeToCreateScrewAndThreadedInsertHole027"
  Angle = 360
  Axis = (0,1,0)
  Base = (0,0,0)
  FaceMakerClass = Part::FaceMakerBullseye
  Placement = pos=(62.3,30.3,51.7) rot=(0,0,1;0rad)
  Solid = false
  Source = -> Face092
  Symmetric = false
FEATURE [Part::Revolution] Revolve101  label="removeToCreateScrewAndThreadedInsertHole028"
  Angle = 360
  Axis = (0,1,0)
  Base = (0,0,0)
  FaceMakerClass = Part::FaceMakerBullseye
  Placement = pos=(30.3,30.3,19.7) rot=(0,0,1;0rad)
  Solid = false
  Source = -> Face093
  Symmetric = false
FEATURE [Part::Revolution] Revolve102  label="removeToCreateScrewAndThreadedInsertHole029"
  Angle = 360
  Axis = (0,1,0)
  Base = (0,0,0)
  FaceMakerClass = Part::FaceMakerBullseye
  Placement = pos=(30.3,30.3,51.7) rot=(0,0,1;0rad)
  Solid = false
  Source = -> Face094
  Symmetric = false
FEATURE [Part::MultiFuse] Fusion068  label="createThreadedInsertHolesForFan002"
  Shapes = -> [Revolve099,Revolve100,Revolve101,Revolve102]
FEATURE [Part::Cut] Cut026  label="fanScrewHousing003"
  Base = -> Fusion067
  Tool = -> Fusion068
FEATURE [Sketcher::SketchObject] Sketch048
  FullyConstrained = false
  Placement = pos=(0,0,0) rot=(1,0,0;1.5708rad)
  sketch-geometry (24):
    g0: ArcOfCircle CenterX=-4 CenterY=-10.5 CenterZ=0 NormalX=0 NormalY=0 NormalZ=1 AngleXU=0 Radius=1.5 StartAngle=6e-16 EndAngle=3.14159
    g1: ArcOfCircle CenterX=-34.2 CenterY=-10.5 CenterZ=0 NormalX=0 NormalY=0 NormalZ=1 AngleXU=0 Radius=1.5 StartAngle=0 EndAngle=3.14159
    g2: ArcOfCircle CenterX=-34.2 CenterY=-27.7 CenterZ=0 NormalX=0 NormalY=0 NormalZ=1 AngleXU=0 Radius=1.5 StartAngle=3.14159 EndAngle=6.28319
    g3: ArcOfCircle CenterX=-4 CenterY=-27.7 CenterZ=0 NormalX=0 NormalY=0 NormalZ=1 AngleXU=0 Radius=1.5 StartAngle=3.1416 EndAngle=6.28319
    g4: ArcOfCircle CenterX=-10 CenterY=-4.3 CenterZ=0 NormalX=0 NormalY=0 NormalZ=1 AngleXU=0 Radius=1.5 StartAngle=2e-16 EndAngle=3.14159
    g5: ArcOfCircle CenterX=-16.1 CenterY=-1.8 CenterZ=0 NormalX=0 NormalY=0 NormalZ=1 AngleXU=0 Radius=1.5 StartAngle=5e-16 EndAngle=3.14159
    g6: ArcOfCircle CenterX=-22.1 CenterY=-1.8 CenterZ=0 NormalX=0 NormalY=0 NormalZ=1 AngleXU=0 Radius=1.5 StartAngle=5e-16 EndAngle=3.14159
    g7: ArcOfCircle CenterX=-28.2 CenterY=-4.3 CenterZ=0 NormalX=0 NormalY=0 NormalZ=1 AngleXU=0 Radius=1.5 StartAngle=2e-16 EndAngle=3.14159
    g8: ArcOfCircle CenterX=-10 CenterY=-33.9 CenterZ=0 NormalX=0 NormalY=0 NormalZ=1 AngleXU=0 Radius=1.5 StartAngle=3.14159 EndAngle=6.28319
    g9: ArcOfCircle CenterX=-16.1 CenterY=-36.4 CenterZ=0 NormalX=0 NormalY=0 NormalZ=1 AngleXU=0 Radius=1.5 StartAngle=3.14159 EndAngle=6.28319
    g10: ArcOfCircle CenterX=-22.1 CenterY=-36.4 CenterZ=0 NormalX=0 NormalY=0 NormalZ=1 AngleXU=0 Radius=1.5 StartAngle=3.14159 EndAngle=6.28319
    g11: ArcOfCircle CenterX=-28.2 CenterY=-33.9 CenterZ=0 NormalX=0 NormalY=0 NormalZ=1 AngleXU=0 Radius=1.5 StartAngle=3.14159 EndAngle=6.28319
    g12: LineSegment StartX=-35.7 StartY=-10.5 StartZ=0 EndX=-35.7 EndY=-27.7 EndZ=0
    g13: LineSegment StartX=-32.7 StartY=-10.5 StartZ=0 EndX=-32.7 EndY=-27.7 EndZ=0
    g14: LineSegment StartX=-29.7 StartY=-33.9 StartZ=0 EndX=-29.7 EndY=-4.3 EndZ=0
    g15: LineSegment StartX=-26.7 StartY=-33.9 StartZ=0 EndX=-26.7 EndY=-4.3 EndZ=0
    g16: LineSegment StartX=-2.5 StartY=-10.5 StartZ=0 EndX=-2.5 EndY=-27.7 EndZ=0
    g17: LineSegment StartX=-8.5 StartY=-4.3 StartZ=0 EndX=-8.5 EndY=-33.9 EndZ=0
    g18: LineSegment StartX=-5.5 StartY=-10.5 StartZ=0 EndX=-5.5 EndY=-27.7 EndZ=0
    g19: LineSegment StartX=-11.5 StartY=-4.3 StartZ=0 EndX=-11.5 EndY=-33.9 EndZ=0
    g20: LineSegment StartX=-14.6 StartY=-1.8 StartZ=0 EndX=-14.6 EndY=-36.4 EndZ=0
    g21: LineSegment StartX=-17.6 StartY=-1.8 StartZ=0 EndX=-17.6 EndY=-36.4 EndZ=0
    g22: LineSegment StartX=-20.6 StartY=-36.4 StartZ=0 EndX=-20.6 EndY=-1.8 EndZ=0
    g23: LineSegment StartX=-23.6 StartY=-1.8 StartZ=0 EndX=-23.6 EndY=-36.4 EndZ=0
  constraints (48):
    c: Block(g0)
    c: Block(g1)
    c: Block(g2)
    c: Block(g3)
    c: Block(g4)
    c: Block(g5)
    c: Block(g6)
    c: Block(g7)
    c: Block(g8)
    c: Block(g9)
    c: Block(g10)
    c: Block(g11)
    c: Coincident(g12,g1)
    c: Coincident(g12,g2)
    c: Vertical(g12)
    c: Coincident(g13,g1)
    c: Coincident(g13,g2)
    c: Vertical(g13)
    c: Coincident(g14,g11)
    c: Coincident(g14,g7)
    c: Vertical(g14)
    c: Coincident(g15,g11)
    c: Coincident(g15,g7)
    c: Vertical(g15)
    c: Coincident(g16,g0)
    c: Coincident(g16,g3)
    c: Vertical(g16)
    c: Coincident(g17,g4)
    c: Coincident(g17,g8)
    c: Vertical(g17)
    c: Coincident(g18,g0)
    c: Coincident(g18,g3)
    c: Vertical(g18)
    c: Coincident(g19,g4)
    c: Coincident(g19,g8)
    c: Vertical(g19)
    c: Coincident(g20,g5)
    c: Coincident(g20,g9)
    c: Vertical(g20)
    c: Coincident(g21,g5)
    c: Coincident(g21,g9)
    c: Vertical(g21)
    c: Coincident(g22,g10)
    c: Coincident(g22,g6)
    c: Vertical(g22)
    c: Coincident(g23,g6)
    c: Coincident(g23,g10)
    c: Vertical(g23)
FEATURE [Part::Extrusion] Extrude039  label="removeToCreateFanGrillHoles002"
  Base = -> Sketch048
  Dir = (0,-1,6e-16)
  DirMode = 2
  FaceMakerClass = Part::FaceMakerBullseye
  LengthFwd = 10
  LengthRev = 0
  Placement = pos=(65.4,44,54.82) rot=(0,0,1;0rad)
  Solid = true
  Symmetric = false
FEATURE [Part::Cut] Cut027  label="fanScrewHousing004"
  Base = -> Cut026
  Tool = -> Extrude038
FEATURE [Part::Cut] Cut028  label="top014"
  Base = -> Fillet026
  Tool = -> Extrude039
FEATURE [Part::Feature] Face095 .. Face098  x4 (patterned run collapsed; names and placements below)
  shape: bbox 3.5 x 17.8 x 2e-07 mm, 1 faces, 0 solids (baked)
FEATURE [Part::Revolution] Revolve103  label="removeToCreateScrewAndThreadedInsertHole030"
  Angle = 360
  Axis = (0,1,0)
  Base = (0,0,0)
  FaceMakerClass = Part::FaceMakerBullseye
  Placement = pos=(62.3,30.3,19.7) rot=(0,0,1;0rad)
  Solid = false
  Source = -> Face095
  Symmetric = false
FEATURE [Part::Revolution] Revolve104  label="removeToCreateScrewAndThreadedInsertHole031"
  Angle = 360
  Axis = (0,1,0)
  Base = (0,0,0)
  FaceMakerClass = Part::FaceMakerBullseye
  Placement = pos=(62.3,30.3,51.7) rot=(0,0,1;0rad)
  Solid = false
  Source = -> Face096
  Symmetric = false
FEATURE [Part::Revolution] Revolve105  label="removeToCreateScrewAndThreadedInsertHole032"
  Angle = 360
  Axis = (0,1,0)
  Base = (0,0,0)
  FaceMakerClass = Part::FaceMakerBullseye
  Placement = pos=(30.3,30.3,19.7) rot=(0,0,1;0rad)
  Solid = false
  Source = -> Face097
  Symmetric = false
FEATURE [Part::Revolution] Revolve106  label="removeToCreateScrewAndThreadedInsertHole033"
  Angle = 360
  Axis = (0,1,0)
  Base = (0,0,0)
  FaceMakerClass = Part::FaceMakerBullseye
  Placement = pos=(30.3,30.3,51.7) rot=(0,0,1;0rad)
  Solid = false
  Source = -> Face098
  Symmetric = false
FEATURE [Part::MultiFuse] Fusion069  label="createThreadedInsertHolesForFan003"
  Shapes = -> [Revolve103,Revolve104,Revolve105,Revolve106]
FEATURE [Part::Cut] Cut029  label="top015"
  Base = -> Cut028
  Tool = -> Fusion054
FEATURE [Part::Cut] Cut030  label="fanScrewHousing005"
  Base = -> Cut027
  Tool = -> Fusion069
FEATURE [Part::Cylinder] Cylinder026  label="removeToCreteHoleForPlugHousing010"
  Angle = 360
  AttacherType = Attacher::AttachEngine3D
  Height = 20
  Placement = pos=(-2,19,36) rot=(0,1,0;1.5708rad)
  Radius = 14.3
FEATURE [Part::Box] Box018  label="removeToCreteHoleForPlugHousing011"
  AttacherType = Attacher::AttachEngine3D
  Height = 28.6
  Length = 10
  Placement = pos=(-2,0,21.7) rot=(0,0,1;0rad)
  Width = 19
FEATURE [Part::Box] Box019  label="wireHolderBottomCaseBit"
  AttacherType = Attacher::AttachEngine3D
  Height = 28
  Length = 3
  Placement = pos=(0,0,22) rot=(0,0,1;0rad)
  Width = 21
FEATURE [Part::Cylinder] Cylinder027  label="removeToCreteHoleForPlugHousing012"
  Angle = 360
  AttacherType = Attacher::AttachEngine3D
  Height = 20
  Placement = pos=(-2,19,36) rot=(0,1,0;1.5708rad)
  Radius = 14.3
FEATURE [Part::Cut] Cut031  label="wireHolderBottomCaseBit001"
  Base = -> Box019
  Tool = -> Cylinder027
FEATURE [Part::MultiFuse] Fusion070  label="removeToCreteHoleForPlugHousing013"
  Shapes = -> [Box018,Cylinder026]
FEATURE [Part::Cut] Cut032  label="top016"
  Base = -> Cut029
  Tool = -> Fusion070
FEATURE [Part::Cylinder] Cylinder028
  Angle = 360
  AttacherType = Attacher::AttachEngine3D
  Height = 20
  Placement = pos=(0,0,36.15) rot=(0,0,1;0rad)
  Radius = 14.3
FEATURE [Part::Cylinder] Cylinder029
  Angle = 360
  AttacherType = Attacher::AttachEngine3D
  Height = 10
  Placement = pos=(0,0,36.15) rot=(0,0,1;0rad)
  Radius = 4
FEATURE [Part::MultiFuse] Fusion071  label="removeToCreteHoleForPlugHousing014"
  Placement = pos=(70,19,36) rot=(0,1,0;1.5708rad)
  Shapes = -> [Cylinder028,Cylinder029]
FEATURE [Sketcher::SketchObject] Sketch049  label="topSketch011"
  FullyConstrained = true
  sketch-geometry (4):
    g0: ArcOfCircle CenterX=105 CenterY=19 CenterZ=0 NormalX=0 NormalY=0 NormalZ=1 AngleXU=0 Radius=20.6155 StartAngle=5.54125 EndAngle=6.28319
    g1: ArcOfCircle CenterX=105 CenterY=19 CenterZ=0 NormalX=0 NormalY=0 NormalZ=1 AngleXU=0 Radius=13 StartAngle=5.54125 EndAngle=6.28319
    g2: LineSegment StartX=118 StartY=19 StartZ=0 EndX=125.616 EndY=19 EndZ=0
    g3: LineSegment StartX=114.583 StartY=10.2157 StartZ=0 EndX=120.197 EndY=5.06982 EndZ=0
  constraints (7):
    c: Block(g0)
    c: Block(g1)
    c: Coincident(g2,g1)
    c: Coincident(g2,g0)
    c: Horizontal(g2)
    c: Coincident(g3,g1)
    c: Coincident(g3,g0)
FEATURE [Part::Box] Box020  label="removeToCreteHoleForPlugHousing015"
  AttacherType = Attacher::AttachEngine3D
  Height = 28.6
  Length = 20
  Placement = pos=(106.15,0,21.7) rot=(0,0,1;0rad)
  Width = 19
FEATURE [Part::MultiFuse] Fusion072  label="removeToCreteHoleForPlugHousing016"
  Shapes = -> [Box020,Fusion071]
FEATURE [Part::Cut] Cut033  label="removeToCreteHoleForPlugHousing017"
  Base = -> Cut032
  Tool = -> Fusion072
FEATURE [Part::Cylinder] Cylinder030
  Angle = 360
  AttacherType = Attacher::AttachEngine3D
  Height = 20
  Placement = pos=(0,0,36.15) rot=(0,0,1;0rad)
  Radius = 14.3
FEATURE [Part::Cylinder] Cylinder031
  Angle = 360
  AttacherType = Attacher::AttachEngine3D
  Height = 10
  Placement = pos=(0,0,36.15) rot=(0,0,1;0rad)
  Radius = 4
FEATURE [Part::Box] Box021  label="removeToCreteHoleForPlugHousing019"
  AttacherType = Attacher::AttachEngine3D
  Height = 28.6
  Length = 20
  Placement = pos=(106.15,0,21.7) rot=(0,0,1;0rad)
  Width = 19
FEATURE [Part::MultiFuse] Fusion074  label="removeToCreteHoleForPlugHousing020"
  Placement = pos=(70,19,36) rot=(0,1,0;1.5708rad)
  Shapes = -> [Cylinder030,Cylinder031]
FEATURE [Part::MultiFuse] Fusion073  label="removeToCreteHoleForPlugHousing018"
  Placement = pos=(0,0,28.3) rot=(0,0,1;0rad)
  Shapes = -> [Box021,Fusion074]
FEATURE [Part::Cylinder] Cylinder032
  Angle = 360
  AttacherType = Attacher::AttachEngine3D
  Height = 20
  Placement = pos=(0,0,36.15) rot=(0,0,1;0rad)
  Radius = 14.3
FEATURE [Part::Cylinder] Cylinder033
  Angle = 360
  AttacherType = Attacher::AttachEngine3D
  Height = 10
  Placement = pos=(0,0,36.15) rot=(0,0,1;0rad)
  Radius = 4
FEATURE [Part::Box] Box022  label="removeToCreteHoleForPlugHousing021"
  AttacherType = Attacher::AttachEngine3D
  Height = 28.6
  Length = 20
  Placement = pos=(106.15,0,21.7) rot=(0,0,1;0rad)
  Width = 19
FEATURE [Part::MultiFuse] Fusion076  label="removeToCreteHoleForPlugHousing023"
  Placement = pos=(70,19,36) rot=(0,1,0;1.5708rad)
  Shapes = -> [Cylinder032,Cylinder033]
FEATURE [Part::MultiFuse] Fusion075  label="removeToCreteHoleForPlugHousing022"
  Placement = pos=(0,0,-28.3) rot=(0,0,1;0rad)
  Shapes = -> [Box022,Fusion076]
FEATURE [Part::MultiFuse] Fusion077  label="removeToCreatePlugHousingBottomBit"
  Shapes = -> [Fusion075,Fusion073]
FEATURE [Part::Cylinder] Cylinder034
  Angle = 360
  AttacherType = Attacher::AttachEngine3D
  Height = 20
  Placement = pos=(0,0,36.15) rot=(0,0,1;0rad)
  Radius = 14
FEATURE [Part::Cylinder] Cylinder035
  Angle = 360
  AttacherType = Attacher::AttachEngine3D
  Height = 10
  Placement = pos=(0,0,36.15) rot=(0,0,1;0rad)
  Radius = 4
FEATURE [Part::MultiFuse] Fusion078  label="removeToCreteHoleForPlugHousing024"
  Placement = pos=(70,19,36) rot=(0,1,0;1.5708rad)
  Shapes = -> [Cylinder034,Cylinder035]
FEATURE [Part::MultiFuse] Fusion079  label="removeToCreatePlugHousingBottomBit001"
  Shapes = -> [Fusion078,Fusion077]
FEATURE [Part::Extrusion] Extrude040  label="bottomPlugHousingBit"
  Base = -> Sketch049
  Dir = (0,0,1)
  DirMode = 2
  FaceMakerClass = Part::FaceMakerBullseye
  LengthFwd = 72
  LengthRev = 0
  Solid = true
  Symmetric = false
FEATURE [Part::Cut] Cut034  label="bottomPlugHousingBit001"
  Base = -> Extrude040
  Placement = pos=(-0.09,0,0) rot=(0,0,1;0rad)
  Tool = -> Fusion079
FEATURE [Part::Box] Box023  label="Cube014"
  AttacherType = Attacher::AttachEngine3D
  Height = 16
  Length = 8
  Placement = pos=(12.7,31.52,28) rot=(0,0,1;0rad)
  Width = 4
FEATURE [Part::Cylinder] Cylinder036
  Angle = 360
  AttacherType = Attacher::AttachEngine3D
  Height = 10
  Placement = pos=(0,0,36.15) rot=(0,0,1;0rad)
  Radius = 4
FEATURE [Part::Cylinder] Cylinder037
  Angle = 360
  AttacherType = Attacher::AttachEngine3D
  Height = 20
  Placement = pos=(0,0,36.15) rot=(0,0,1;0rad)
  Radius = 8.2
FEATURE [Part::MultiFuse] Fusion080  label="removeToCreteHoleForPlugHousing025"
  Placement = pos=(-42,19,36) rot=(0,1,0;1.5708rad)
  Shapes = -> [Cylinder037,Cylinder036]
FEATURE [Sketcher::SketchObject] Sketch050  label="topSketch012"
  FullyConstrained = true
  sketch-geometry (4):
    g0: LineSegment StartX=16.8446 StartY=31.512 StartZ=0 EndX=16.3251 EndY=34.4666 EndZ=0
    g1: ArcOfCircle CenterX=19 CenterY=19.2524 CenterZ=0 NormalX=0 NormalY=0 NormalZ=1 AngleXU=0 Radius=15.4476 StartAngle=1.74483 EndAngle=2.72717
    g2: ArcOfCircle CenterX=19 CenterY=19.2524 CenterZ=0 NormalX=0 NormalY=0 NormalZ=1 AngleXU=0 Radius=12.4476 StartAngle=1.74483 EndAngle=2.73189
    g3: LineSegment StartX=4.86004 StartY=25.4725 StartZ=0 EndX=7.58253 EndY=24.2107 EndZ=0
  constraints (7):
    c: Block(g0)
    c: Coincident(g1,g0)
    c: Coincident(g2,g0)
    c: Coincident(g3,g1)
    c: Coincident(g3,g2)
    c: Block(g1)
    c: Block(g2)
FEATURE [Part::Extrusion] Extrude041
  Base = -> Sketch050
  Dir = (0,0,1)
  DirMode = 2
  FaceMakerClass = Part::FaceMakerBullseye
  LengthFwd = 10.6
  LengthRev = 0
  Placement = pos=(0,0,31) rot=(0,0,1;0rad)
  Solid = true
  Symmetric = false
FEATURE [Part::Cut] Cut035
  Base = -> Extrude041
  Placement = pos=(0,0,-0.3) rot=(0,0,1;0rad)
  Tool = -> Fusion080
FEATURE [Part::Cut] Cut036
  Base = -> Box023
  Tool = -> Cut035
FEATURE [Part::Fillet] Fillet027
  Base = -> Cut036
  Edges = 1 edges r=0.7: [Edge13]
FEATURE [Part::Fillet] Fillet028
  Base = -> Fillet027
  Edges = 1 edges r=0.7: [Edge13]
FEATURE [Part::Fillet] Fillet029
  Base = -> Fillet028
  Edges = 1 edges r=0.7: [Edge16]
FEATURE [Part::Fillet] Fillet030
  Base = -> Fillet029
  Edges = 1 edges r=0.7: [Edge11]
FEATURE [Part::Fillet] Fillet031
  Base = -> Fillet030
  Edges = 1 edges r=0.7: [Edge10]
FEATURE [Part::Fillet] Fillet032
  Base = -> Fillet031
  Edges = 1 edges r=1.2: [Edge5]
FEATURE [Part::Fillet] Fillet033
  Base = -> Fillet032
  Edges = 1 edges r=1.2: [Edge12]
FEATURE [Part::Fillet] Fillet034  label="wireHousingRetainer"
  Base = -> Fillet033
  Edges = 1 edges r=2: [Edge1]
  Placement = pos=(0.3,0,0) rot=(0,0,1;0rad)
FEATURE [Part::Feature] Face099
  shape: bbox 3.5 x 17.8 x 2e-07 mm, 1 faces, 0 solids (baked)
FEATURE [Part::Revolution] Revolve107  label="removeToCreateScrewAndThreadedInsertHole034"
  Angle = 360
  Axis = (0,1,0)
  Base = (0,0,0)
  FaceMakerClass = Part::FaceMakerBullseye
  Placement = pos=(12.5,0,10) rot=(0,0,1;0rad)
  Solid = false
  Source = -> Face099
  Symmetric = false
FEATURE [Part::Feature] Face100
  shape: bbox 3.5 x 17.8 x 2e-07 mm, 1 faces, 0 solids (baked)
FEATURE [Part::Revolution] Revolve108  label="removeToCreateScrewAndThreadedInsertHole035"
  Angle = 360
  Axis = (0,1,0)
  Base = (0,0,0)
  FaceMakerClass = Part::FaceMakerBullseye
  Placement = pos=(12.5,0,62) rot=(0,0,1;0rad)
  Solid = false
  Source = -> Face100
  Symmetric = false
FEATURE [Part::Feature] Face101
  shape: bbox 3.5 x 17.8 x 2e-07 mm, 1 faces, 0 solids (baked)
FEATURE [Part::Revolution] Revolve109  label="removeToCreateScrewAndThreadedInsertHole036"
  Angle = 360
  Axis = (0,1,0)
  Base = (0,0,0)
  FaceMakerClass = Part::FaceMakerBullseye
  Placement = pos=(89.5,0,68.5) rot=(0,0,1;0rad)
  Solid = false
  Source = -> Face101
  Symmetric = false
FEATURE [Part::Feature] Face102
  shape: bbox 3.5 x 17.8 x 2e-07 mm, 1 faces, 0 solids (baked)
FEATURE [Part::Revolution] Revolve110  label="removeToCreateScrewAndThreadedInsertHole037"
  Angle = 360
  Axis = (0,1,0)
  Base = (0,0,0)
  FaceMakerClass = Part::FaceMakerBullseye
  Placement = pos=(89.5,0,3.5) rot=(0,0,1;0rad)
  Solid = false
  Source = -> Face102
  Symmetric = false
FEATURE [Part::Feature] Face103
  shape: bbox 3.5 x 17.8 x 2e-07 mm, 1 faces, 0 solids (baked)
FEATURE [Part::Revolution] Revolve111  label="removeToCreateScrewAndThreadedInsertHole038"
  Angle = 360
  Axis = (0,1,0)
  Base = (0,0,0)
  FaceMakerClass = Part::FaceMakerBullseye
  Placement = pos=(109.5,4.7,3.5) rot=(0,0,1;0rad)
  Solid = false
  Source = -> Face103
  Symmetric = false
FEATURE [Part::Feature] Face104
  shape: bbox 3.5 x 17.8 x 2e-07 mm, 1 faces, 0 solids (baked)
FEATURE [Part::Revolution] Revolve112  label="removeToCreateScrewAndThreadedInsertHole039"
  Angle = 360
  Axis = (0,1,0)
  Base = (0,0,0)
  FaceMakerClass = Part::FaceMakerBullseye
  Placement = pos=(109.5,4.7,68.5) rot=(0,0,1;0rad)
  Solid = false
  Source = -> Face104
  Symmetric = false
FEATURE [Part::MultiFuse] Fusion081  label="removeToCreateScrewAndThreadedInsertHole040"
  Shapes = -> [Revolve107,Revolve108,Revolve109,Revolve110,Revolve111,Revolve112]
FEATURE [Part::MultiFuse] Fusion082  label="casePillars002"
  Shapes = -> [Revolve094,Revolve092,Revolve090,Revolve089,Revolve091,Revolve093]
FEATURE [Part::Cut] Cut037  label="casePillars003"
  Base = -> Fusion082
  Tool = -> Fusion081
FEATURE [Sketcher::SketchObject] Sketch051
  FullyConstrained = true
  Placement = pos=(117,19,0) rot=(0.57735,0.57735,0.57735;2.0944rad)
  sketch-geometry (48):
    g0: LineSegment StartX=-49.19 StartY=69.25 StartZ=0 EndX=-49.19 EndY=66.25 EndZ=0
    g1: LineSegment StartX=-49.19 StartY=63.5 StartZ=0 EndX=-49.19 EndY=60.5 EndZ=0
    g2: LineSegment StartX=-49.19 StartY=57.75 StartZ=0 EndX=-49.19 EndY=54.75 EndZ=0
    g3: LineSegment StartX=-49.19 StartY=52 StartZ=0 EndX=-49.19 EndY=49 EndZ=0
    g4: LineSegment StartX=-49.19 StartY=46.25 StartZ=0 EndX=-49.19 EndY=43.25 EndZ=0
    g5: LineSegment StartX=-49.19 StartY=40.5 StartZ=0 EndX=-49.19 EndY=37.5 EndZ=0
    g6: LineSegment StartX=-49.19 StartY=34.5 StartZ=0 EndX=-49.19 EndY=31.5 EndZ=0
    g7: LineSegment StartX=-49.19 StartY=28.75 StartZ=0 EndX=-49.19 EndY=25.75 EndZ=0
    g8: LineSegment StartX=-49.19 StartY=23 StartZ=0 EndX=-49.19 EndY=20 EndZ=0
    g9: LineSegment StartX=-49.19 StartY=17.25 StartZ=0 EndX=-49.19 EndY=14.25 EndZ=0
    g10: LineSegment StartX=-49.19 StartY=11.5 StartZ=0 EndX=-49.19 EndY=8.5 EndZ=0
    g11: LineSegment StartX=-49.19 StartY=5.75 StartZ=0 EndX=-49.19 EndY=2.75 EndZ=0
    g12: ArcOfCircle CenterX=-1.5 CenterY=67.75 CenterZ=0 NormalX=0 NormalY=0 NormalZ=1 AngleXU=0 Radius=1.5 StartAngle=4.71239 EndAngle=7.85398
    g13: ArcOfCircle CenterX=-1.5 CenterY=62 CenterZ=0 NormalX=0 NormalY=0 NormalZ=1 AngleXU=0 Radius=1.5 StartAngle=4.71239 EndAngle=7.85398
    g14: ArcOfCircle CenterX=-1.5 CenterY=56.25 CenterZ=0 NormalX=0 NormalY=0 NormalZ=1 AngleXU=0 Radius=1.5 StartAngle=4.71239 EndAngle=7.85398
    g15: ArcOfCircle CenterX=-11.49 CenterY=50.5 CenterZ=0 NormalX=0 NormalY=0 NormalZ=1 AngleXU=0 Radius=1.5 StartAngle=4.71239 EndAngle=7.85398
    g16: ArcOfCircle CenterX=-16.28 CenterY=44.75 CenterZ=0 NormalX=0 NormalY=0 NormalZ=1 AngleXU=0 Radius=1.5 StartAngle=4.71239 EndAngle=7.85398
    g17: ArcOfCircle CenterX=-18.2337 CenterY=39 CenterZ=0 NormalX=0 NormalY=0 NormalZ=1 AngleXU=0 Radius=1.5 StartAngle=4.71485 EndAngle=7.85398
    g18: ArcOfCircle CenterX=-16.2837 CenterY=27.25 CenterZ=0 NormalX=0 NormalY=0 NormalZ=1 AngleXU=0 Radius=1.5 StartAngle=4.71485 EndAngle=7.85398
    g19: ArcOfCircle CenterX=-18.2337 CenterY=33 CenterZ=0 NormalX=0 NormalY=0 NormalZ=1 AngleXU=0 Radius=1.5 StartAngle=4.71485 EndAngle=7.85398
    g20: ArcOfCircle CenterX=-11.49 CenterY=21.5 CenterZ=0 NormalX=0 NormalY=0 NormalZ=1 AngleXU=0 Radius=1.5 StartAngle=4.71239 EndAngle=7.85398
    g21: ArcOfCircle CenterX=-1.5 CenterY=4.25 CenterZ=0 NormalX=0 NormalY=0 NormalZ=1 AngleXU=0 Radius=1.5 StartAngle=4.71239 EndAngle=7.85398
    g22: ArcOfCircle CenterX=-1.5 CenterY=10 CenterZ=0 NormalX=0 NormalY=0 NormalZ=1 AngleXU=0 Radius=1.5 StartAngle=4.71239 EndAngle=7.85398
    g23: ArcOfCircle CenterX=-1.5 CenterY=15.75 CenterZ=0 NormalX=0 NormalY=0 NormalZ=1 AngleXU=0 Radius=1.5 StartAngle=4.71239 EndAngle=7.85398
    g24: LineSegment StartX=-49.19 StartY=69.25 StartZ=0 EndX=-1.5 EndY=69.25 EndZ=0
    g25: LineSegment StartX=-49.19 StartY=66.25 StartZ=0 EndX=-1.5 EndY=66.25 EndZ=0
    g26: LineSegment StartX=-49.19 StartY=63.5 StartZ=0 EndX=-1.5 EndY=63.5 EndZ=0
    g27: LineSegment StartX=-49.19 StartY=60.5 StartZ=0 EndX=-1.5 EndY=60.5 EndZ=0
    g28: LineSegment StartX=-49.19 StartY=57.75 StartZ=0 EndX=-1.5 EndY=57.75 EndZ=0
    g29: LineSegment StartX=-49.19 StartY=54.75 StartZ=0 EndX=-1.5 EndY=54.75 EndZ=0
    g30: LineSegment StartX=-49.19 StartY=52 StartZ=0 EndX=-11.49 EndY=52 EndZ=0
    g31: LineSegment StartX=-49.19 StartY=49 StartZ=0 EndX=-11.49 EndY=49 EndZ=0
    g32: LineSegment StartX=-49.19 StartY=46.25 StartZ=0 EndX=-16.28 EndY=46.25 EndZ=0
    g33: LineSegment StartX=-49.19 StartY=43.25 StartZ=0 EndX=-16.28 EndY=43.25 EndZ=0
    g34: LineSegment StartX=-49.19 StartY=40.5 StartZ=0 EndX=-18.2337 EndY=40.5 EndZ=0
    g35: LineSegment StartX=-49.19 StartY=37.5 StartZ=0 EndX=-18.23 EndY=37.5 EndZ=0
    g36: LineSegment StartX=-49.19 StartY=34.5 StartZ=0 EndX=-18.2337 EndY=34.5 EndZ=0
    g37: LineSegment StartX=-49.19 StartY=31.5 StartZ=0 EndX=-18.23 EndY=31.5 EndZ=0
    g38: LineSegment StartX=-49.19 StartY=28.75 StartZ=0 EndX=-16.2837 EndY=28.75 EndZ=0
    g39: LineSegment StartX=-49.19 StartY=25.75 StartZ=0 EndX=-16.28 EndY=25.75 EndZ=0
    g40: LineSegment StartX=-49.19 StartY=23 StartZ=0 EndX=-11.49 EndY=23 EndZ=0
    g41: LineSegment StartX=-49.19 StartY=20 StartZ=0 EndX=-11.49 EndY=20 EndZ=0
    g42: LineSegment StartX=-49.19 StartY=17.25 StartZ=0 EndX=-1.5 EndY=17.25 EndZ=0
    g43: LineSegment StartX=-49.19 StartY=14.25 StartZ=0 EndX=-1.5 EndY=14.25 EndZ=0
    g44: LineSegment StartX=-49.19 StartY=11.5 StartZ=0 EndX=-1.5 EndY=11.5 EndZ=0
    g45: LineSegment StartX=-49.19 StartY=8.5 StartZ=0 EndX=-1.5 EndY=8.5 EndZ=0
    g46: LineSegment StartX=-49.19 StartY=5.75 StartZ=0 EndX=-1.5 EndY=5.75 EndZ=0
    g47: LineSegment StartX=-49.19 StartY=2.75 StartZ=0 EndX=-1.5 EndY=2.75 EndZ=0
  constraints (120):
    c: Vertical(g0)
    c: Distance(g0) = 3
    c: Block(g0)
    c: Vertical(g1)
    c: Distance(g1) = 3
    c: Vertical(g2)
    c: Equal(g0,g2) = 3
    c: Block(g2)
    c: Vertical(g3)
    c: Equal(g1,g3) = 3
    c: Vertical(g4)
    c: Equal(g0,g4) = 3
    c: Block(g4)
    c: Vertical(g5)
    c: Equal(g1,g5) = 3
    c: Vertical(g6)
    c: Equal(g0,g6) = 3
    c: Block(g6)
    c: Vertical(g7)
    c: Equal(g1,g7) = 3
    c: Vertical(g8)
    c: Equal(g0,g8) = 3
    c: Block(g8)
    c: Vertical(g9)
    c: Equal(g1,g9) = 3
    c: Vertical(g10)
    c: Equal(g0,g10) = 3
    c: Block(g10)
    c: Vertical(g11)
    c: Equal(g1,g11) = 3
    c: Block(g12)
    c: Block(g13)
    c: Block(g14)
    c: Block(g15)
    c: Block(g16)
    c: Block(g17)
    c: Block(g18)
    c: Block(g19)
    c: Block(g20)
    c: Block(g21)
    c: Block(g22)
    c: Block(g23)
    c: Block(g11)
    c: Block(g9)
    c: Block(g7)
    c: Block(g5)
    c: Block(g3)
    c: Block(g1)
    c: Coincident(g24,g0)
    c: Coincident(g24,g12)
    c: Horizontal(g24)
    c: Coincident(g25,g0)
    c: Coincident(g25,g12)
    c: Horizontal(g25)
    c: Coincident(g26,g1)
    c: Coincident(g26,g13)
    c: Horizontal(g26)
    c: Coincident(g27,g1)
    c: Coincident(g27,g13)
    c: Horizontal(g27)
    c: Coincident(g28,g2)
    c: Coincident(g28,g14)
    c: Horizontal(g28)
    c: Coincident(g29,g2)
    c: Coincident(g29,g14)
    c: Horizontal(g29)
    c: Coincident(g30,g3)
    c: Coincident(g30,g15)
    c: Horizontal(g30)
    c: Coincident(g31,g3)
    c: Coincident(g31,g15)
    c: Horizontal(g31)
    c: Coincident(g32,g4)
    c: Coincident(g32,g16)
    c: Horizontal(g32)
    c: Coincident(g33,g4)
    c: Coincident(g33,g16)
    c: Horizontal(g33)
    c: Coincident(g34,g5)
    c: Coincident(g34,g17)
    c: Horizontal(g34)
    c: Coincident(g35,g5)
    c: Coincident(g35,g17)
    c: Horizontal(g35)
    c: Coincident(g36,g6)
    c: Coincident(g36,g19)
    c: Horizontal(g36)
    c: Coincident(g37,g6)
    c: Coincident(g37,g19)
    c: Horizontal(g37)
    c: Coincident(g38,g7)
    c: Coincident(g38,g18)
    c: Horizontal(g38)
    c: Coincident(g39,g7)
    c: Coincident(g39,g18)
    c: Horizontal(g39)
    c: Coincident(g40,g8)
    c: Coincident(g40,g20)
    c: Horizontal(g40)
    c: Coincident(g41,g8)
    c: Coincident(g41,g20)
    c: Horizontal(g41)
    c: Coincident(g42,g9)
    c: Coincident(g42,g23)
    c: Horizontal(g42)
    c: Coincident(g43,g9)
    c: Coincident(g43,g23)
    c: Horizontal(g43)
    c: Coincident(g44,g10)
    c: Coincident(g44,g22)
    c: Horizontal(g44)
    c: Coincident(g45,g10)
    c: Coincident(g45,g22)
    c: Horizontal(g45)
    c: Coincident(g46,g11)
    c: Coincident(g46,g21)
    c: Horizontal(g46)
    c: Coincident(g47,g11)
    c: Coincident(g47,g21)
    c: Horizontal(g47)
FEATURE [Part::Extrusion] Extrude042
  Base = -> Sketch051
  Dir = (1,-2e-16,2e-16)
  DirMode = 2
  FaceMakerClass = Part::FaceMakerBullseye
  LengthFwd = 19
  LengthRev = 0
  Placement = pos=(-19,0,0) rot=(0,0,1;0rad)
  Solid = true
  Symmetric = false
FEATURE [Part::Fillet] Fillet035  label="removeToCreateVentalationHoles"
  Base = -> Extrude042
  Edges = <same value as first occurrence — deduplicated (x6 in doc)>
  Placement = pos=(7,0,0) rot=(0,0,1;0rad)
FEATURE [Part::Cut] Cut038  label="top017"
  Base = -> Cut033
  Tool = -> Fillet035
FEATURE [Sketcher::SketchObject] Sketch052  label="bottomSketch001"
  FullyConstrained = true
  sketch-geometry (45):
    g0: LineSegment StartX=6.29999 StartY=8 StartZ=0 EndX=3.29999 EndY=8 EndZ=0
    g1: LineSegment StartX=3.29999 StartY=8 StartZ=0 EndX=3.29999 EndY=-6.03275e-07 EndZ=0
    g2: ArcOfCircle CenterX=8.29999 CenterY=5 CenterZ=0 NormalX=0 NormalY=0 NormalZ=1 AngleXU=0 Radius=2 StartAngle=3.14159 EndAngle=4.71239
    g3: LineSegment StartX=6.29999 StartY=8 StartZ=0 EndX=6.29999 EndY=5 EndZ=0
    g4: ArcOfCircle CenterX=105 CenterY=19 CenterZ=0 NormalX=0 NormalY=0 NormalZ=1 AngleXU=0 Radius=12.7 StartAngle=4.71239 EndAngle=5.94289
    g5-g11: Circle x7 (B-spline internal-alignment scaffolding for g12; pole/knot coordinates omitted)
    g12: BSplineCurve PolesCount=7 KnotsCount=5 Degree=3 IsPeriodic=0
    g13-g17: GeomPoint x5 (B-spline internal-alignment scaffolding for g12; pole/knot coordinates omitted)
    g18: ArcOfCircle CenterX=105 CenterY=19 CenterZ=0 NormalX=0 NormalY=0 NormalZ=1 AngleXU=0 Radius=15.7 StartAngle=5.81226 EndAngle=6.28319
    g19: BSplineCurve PolesCount=5 KnotsCount=3 Degree=3 IsPeriodic=0
    g20: LineSegment StartX=8.29999 StartY=3 StartZ=0 EndX=101.7 EndY=3 EndZ=0
    g21: LineSegment StartX=3.29999 StartY=-6.03275e-07 StartZ=0 EndX=105 EndY=-6.03275e-07 EndZ=0
    g22: LineSegment StartX=120.974 StartY=8.71251 StartZ=0 EndX=122.332 EndY=7.83778 EndZ=0
    g23: LineSegment StartX=105 StartY=-6.03274e-07 StartZ=0 EndX=113 EndY=-6.03274e-07 EndZ=0
    g24: ArcOfCircle CenterX=105 CenterY=19 CenterZ=0 NormalX=0 NormalY=0 NormalZ=1 AngleXU=0 Radius=20.6155 StartAngle=5.11091 EndAngle=5.71103
    g25: ArcOfCircle CenterX=117.7 CenterY=19 CenterZ=0 NormalX=0 NormalY=0 NormalZ=1 AngleXU=0 Radius=3 StartAngle=1.2e-15 EndAngle=2.10468
    g26: Circle CenterX=116.345 CenterY=16.3232 CenterZ=0 NormalX=0 NormalY=0 NormalZ=1 AngleXU=0 Radius=1
    g27: Circle CenterX=117.24 CenterY=15.7584 CenterZ=0 NormalX=0 NormalY=0 NormalZ=1 AngleXU=0 Radius=1
    g28: Circle CenterX=116.972 CenterY=14.7612 CenterZ=0 NormalX=0 NormalY=0 NormalZ=1 AngleXU=0 Radius=1
    g29: BSplineCurve PolesCount=3 KnotsCount=2 Degree=2 IsPeriodic=0
    g30: GeomPoint X=116.345 Y=16.3232 Z=0
    g31: GeomPoint X=116.972 Y=14.7612 Z=0
    g32: Circle CenterX=115.828 CenterY=17.157 CenterZ=0 NormalX=0 NormalY=0 NormalZ=1 AngleXU=0 Radius=1
    g33: Circle CenterX=115.841 CenterY=16.639 CenterZ=0 NormalX=0 NormalY=0 NormalZ=1 AngleXU=0 Radius=1
    g34: Circle CenterX=116.345 CenterY=16.3232 CenterZ=0 NormalX=0 NormalY=0 NormalZ=1 AngleXU=0 Radius=1
    g35: BSplineCurve PolesCount=3 KnotsCount=2 Degree=2 IsPeriodic=0
    g36: GeomPoint X=115.828 Y=17.157 Z=0
    g37: GeomPoint X=116.345 Y=16.3232 Z=0
    g38: LineSegment StartX=115.828 StartY=17.157 StartZ=0 EndX=115.828 EndY=20.8307 EndZ=0
    g39: Circle CenterX=115.828 CenterY=20.8307 CenterZ=0 NormalX=0 NormalY=0 NormalZ=1 AngleXU=0 Radius=1
    g40: Circle CenterX=115.831 CenterY=21.3396 CenterZ=0 NormalX=0 NormalY=0 NormalZ=1 AngleXU=0 Radius=1
    g41: Circle CenterX=116.173 CenterY=21.5825 CenterZ=0 NormalX=0 NormalY=0 NormalZ=1 AngleXU=0 Radius=1
    g42: BSplineCurve PolesCount=3 KnotsCount=2 Degree=2 IsPeriodic=0
    g43: GeomPoint X=115.828 Y=20.8307 Z=0
    g44: GeomPoint X=116.173 Y=21.5825 Z=0
  constraints (70):
    c: Horizontal(g0)
    c: Distance(g0) = 3
    c: Coincident(g1,g0)
    c: Vertical(g1)
    c: Block(g2)
    c: Block(g0)
    c: Coincident(g3,g0)
    c: Coincident(g3,g2)
    c: Vertical(g3)
    c: Block(g1)
    c: Block(g4)
    c: Coincident(g19,g4)
    c: Block(g19)
    c: Equal(g5, g6-g11) x6
    c: InternalAlignment(g5-g11 -> g12) x7
    c: InternalAlignment(g13-g17 -> g12) x5
    c: Block(g12)
    c: Coincident(g18,g12)
    c: Block(g18)
    c: Coincident(g20,g2)
    c: Coincident(g20,g19)
    c: Horizontal(g20)
    c: Distance(g20) = 93.4
    c: Coincident(g21,g1)
    c: Horizontal(g21)
    c: Distance(g21) = 101.7
    c: Horizontal(g23)
    c: Distance(g23) = 8
    c: Coincident(g24,g23)
    c: Block(g23)
    c: Coincident(g22,g24)
    c: Block(g24)
    c: Block(g22)
    c: Distance(g22) = 1.61553
    c: Coincident(g25,g18)
    c: Block(g25)
    c: Weight(g26) = 1
    c: Equal(g26,g27)
    c: Equal(g26,g28)
    c: Coincident(g29,g4)
    c: InternalAlignment(g26,g29)
    c: InternalAlignment(g27,g29)
    c: InternalAlignment(g28,g29)
    c: InternalAlignment(g30,g29)
    c: InternalAlignment(g31,g29)
    c: Block(g29)
    c: Weight(g32) = 1
    c: Equal(g32,g33)
    c: Equal(g32,g34)
    c: Coincident(g35,g29)
    c: InternalAlignment(g32,g35)
    c: InternalAlignment(g33,g35)
    c: InternalAlignment(g34,g35)
    c: InternalAlignment(g36,g35)
    c: InternalAlignment(g37,g35)
    c: Block(g35)
    c: Coincident(g38,g35)
    c: Vertical(g38)
    c: Block(g38)
    c: Coincident(g42,g38)
    c: Weight(g39) = 1
    c: Equal(g39,g40)
    c: Equal(g39,g41)
    c: Coincident(g42,g25)
    c: InternalAlignment(g39,g42)
    c: InternalAlignment(g40,g42)
    c: InternalAlignment(g41,g42)
    c: InternalAlignment(g43,g42)
    c: InternalAlignment(g44,g42)
    c: Block(g42)
FEATURE [Part::Extrusion] Extrude043  label="bottom010"
  Base = -> Sketch052
  Dir = (0,0,1)
  DirMode = 2
  FaceMakerClass = Part::FaceMakerBullseye
  LengthFwd = 71.4
  LengthRev = 0
  Placement = pos=(0,0,0.3) rot=(0,0,1;0rad)
  Solid = true
  Symmetric = false
FEATURE [Sketcher::SketchObject] Sketch053  label="topSketch013"
  FullyConstrained = true
  sketch-geometry (22):
    g0: LineSegment StartX=5.21097e-06 StartY=3 StartZ=0 EndX=5.21097e-06 EndY=19 EndZ=0
    g1: ArcOfCircle CenterX=19 CenterY=19 CenterZ=0 NormalX=0 NormalY=0 NormalZ=1 AngleXU=0 Radius=19 StartAngle=1.5708 EndAngle=3.14159
    g2: ArcOfCircle CenterX=19 CenterY=19 CenterZ=0 NormalX=0 NormalY=0 NormalZ=1 AngleXU=0 Radius=16 StartAngle=1.5708 EndAngle=3.14159
    g3: LineSegment StartX=114 StartY=35 StartZ=0 EndX=19 EndY=35 EndZ=0
    g4: LineSegment StartX=5.21097e-06 StartY=3 StartZ=0 EndX=5.21097e-06 EndY=0 EndZ=0
    g5: LineSegment StartX=3 StartY=0 StartZ=0 EndX=5.21097e-06 EndY=0 EndZ=0
    g6: LineSegment StartX=3 StartY=19 StartZ=0 EndX=3 EndY=0 EndZ=0
    g7: LineSegment StartX=19 StartY=38 StartZ=0 EndX=124 EndY=38 EndZ=0
    g8: Circle CenterX=119 CenterY=35 CenterZ=0 NormalX=0 NormalY=0 NormalZ=1 AngleXU=0 Radius=1
    g9: Circle CenterX=121 CenterY=35 CenterZ=0 NormalX=0 NormalY=0 NormalZ=1 AngleXU=0 Radius=1
    g10: Circle CenterX=121 CenterY=33 CenterZ=0 NormalX=0 NormalY=0 NormalZ=1 AngleXU=0 Radius=1
    g11: BSplineCurve PolesCount=3 KnotsCount=2 Degree=2 IsPeriodic=0
    g12: GeomPoint X=119 Y=35 Z=0
    g13: GeomPoint X=121 Y=33 Z=0
    g14: LineSegment StartX=119 StartY=35 StartZ=0 EndX=114 EndY=35 EndZ=0
    g15: ArcOfCircle CenterX=105 CenterY=19 CenterZ=0 NormalX=0 NormalY=0 NormalZ=1 AngleXU=0 Radius=16 StartAngle=5.60905 EndAngle=6.28319
    g16: LineSegment StartX=121 StartY=33 StartZ=0 EndX=121 EndY=19 EndZ=0
    g17: LineSegment StartX=117.5 StartY=9.01251 StartZ=0 EndX=121.163 EndY=9.0125 EndZ=0
    g18: ArcOfCircle CenterX=105 CenterY=19 CenterZ=0 NormalX=0 NormalY=0 NormalZ=1 AngleXU=0 Radius=20.6155 StartAngle=5.7297 EndAngle=6.28319
    g19: LineSegment StartX=121.163 StartY=9.0125 StartZ=0 EndX=122.538 EndY=8.16329 EndZ=0
    g20: LineSegment StartX=124 StartY=38 StartZ=0 EndX=125.616 EndY=38 EndZ=0
    g21: LineSegment StartX=125.616 StartY=19 StartZ=0 EndX=125.616 EndY=38 EndZ=0
  constraints (50):
    c: Vertical(g0)
    c: Block(g0)
    c: Coincident(g1,g0)
    c: Block(g1)
    c: Coincident(g2,g1)
    c: Block(g2)
    c: Coincident(g3,g2)
    c: Horizontal(g3)
    c: Tangent(g3,g2)
    c: Coincident(g4,g0)
    c: Distance(g4) = 3
    c: Vertical(g4)
    c: Coincident(g5,g4)
    c: Horizontal(g5)
    c: Coincident(g6,g2)
    c: Coincident(g6,g5)
    c: Vertical(g6)
    c: Horizontal(g7)
    c: Distance(g7) = 105
    c: Coincident(g7,g1)
    c: Block(g3)
    c: Weight(g8) = 1
    c: Equal(g8,g9)
    c: Equal(g8,g10)
    c: InternalAlignment(g8,g11)
    c: InternalAlignment(g9,g11)
    c: InternalAlignment(g10,g11)
    c: InternalAlignment(g12,g11)
    c: InternalAlignment(g13,g11)
    c: Block(g11)
    c: Coincident(g14,g11)
    c: Coincident(g14,g3)
    c: Horizontal(g14)
    c: Block(g15)
    c: Coincident(g16,g11)
    c: Coincident(g16,g15)
    c: Vertical(g16)
    c: Distance(g16) = 14
    c: Coincident(g17,g15)
    c: Block(g18)
    c: Coincident(g19,g18)
    c: Coincident(g20,g7)
    c: Horizontal(g20)
    c: Vertical(g21)
    c: Coincident(g20,g21)
    c: Block(g20)
    c: Block(g21)
    c: Block(g19)
    c: Block(g17)
    c: Distance(g20) = 1.61553
FEATURE [Part::Extrusion] Extrude044
  Base = -> Sketch053
  Dir = (0,0,1)
  DirMode = 2
  FaceMakerClass = Part::FaceMakerBullseye
  LengthFwd = 72
  LengthRev = 0
  Solid = true
  Symmetric = false
FEATURE [Part::Fillet] Fillet036  label="top018"
  Base = -> Extrude044
  Edges = 1 edges r=2: [Edge41]
FEATURE [Sketcher::SketchObject] Sketch054
  FullyConstrained = false
  Placement = pos=(0,0,0) rot=(1,0,0;1.5708rad)
  sketch-geometry (24):
    g0: ArcOfCircle CenterX=-4 CenterY=-10.5 CenterZ=0 NormalX=0 NormalY=0 NormalZ=1 AngleXU=0 Radius=1.5 StartAngle=6e-16 EndAngle=3.14159
    g1: ArcOfCircle CenterX=-34.2 CenterY=-10.5 CenterZ=0 NormalX=0 NormalY=0 NormalZ=1 AngleXU=0 Radius=1.5 StartAngle=0 EndAngle=3.14159
    g2: ArcOfCircle CenterX=-34.2 CenterY=-27.7 CenterZ=0 NormalX=0 NormalY=0 NormalZ=1 AngleXU=0 Radius=1.5 StartAngle=3.14159 EndAngle=6.28319
    g3: ArcOfCircle CenterX=-4 CenterY=-27.7 CenterZ=0 NormalX=0 NormalY=0 NormalZ=1 AngleXU=0 Radius=1.5 StartAngle=3.1416 EndAngle=6.28319
    g4: ArcOfCircle CenterX=-10 CenterY=-4.3 CenterZ=0 NormalX=0 NormalY=0 NormalZ=1 AngleXU=0 Radius=1.5 StartAngle=2e-16 EndAngle=3.14159
    g5: ArcOfCircle CenterX=-16.1 CenterY=-1.8 CenterZ=0 NormalX=0 NormalY=0 NormalZ=1 AngleXU=0 Radius=1.5 StartAngle=5e-16 EndAngle=3.14159
    g6: ArcOfCircle CenterX=-22.1 CenterY=-1.8 CenterZ=0 NormalX=0 NormalY=0 NormalZ=1 AngleXU=0 Radius=1.5 StartAngle=5e-16 EndAngle=3.14159
    g7: ArcOfCircle CenterX=-28.2 CenterY=-4.3 CenterZ=0 NormalX=0 NormalY=0 NormalZ=1 AngleXU=0 Radius=1.5 StartAngle=2e-16 EndAngle=3.14159
    g8: ArcOfCircle CenterX=-10 CenterY=-33.9 CenterZ=0 NormalX=0 NormalY=0 NormalZ=1 AngleXU=0 Radius=1.5 StartAngle=3.14159 EndAngle=6.28319
    g9: ArcOfCircle CenterX=-16.1 CenterY=-36.4 CenterZ=0 NormalX=0 NormalY=0 NormalZ=1 AngleXU=0 Radius=1.5 StartAngle=3.14159 EndAngle=6.28319
    g10: ArcOfCircle CenterX=-22.1 CenterY=-36.4 CenterZ=0 NormalX=0 NormalY=0 NormalZ=1 AngleXU=0 Radius=1.5 StartAngle=3.14159 EndAngle=6.28319
    g11: ArcOfCircle CenterX=-28.2 CenterY=-33.9 CenterZ=0 NormalX=0 NormalY=0 NormalZ=1 AngleXU=0 Radius=1.5 StartAngle=3.14159 EndAngle=6.28319
    g12: LineSegment StartX=-35.7 StartY=-10.5 StartZ=0 EndX=-35.7 EndY=-27.7 EndZ=0
    g13: LineSegment StartX=-32.7 StartY=-10.5 StartZ=0 EndX=-32.7 EndY=-27.7 EndZ=0
    g14: LineSegment StartX=-29.7 StartY=-33.9 StartZ=0 EndX=-29.7 EndY=-4.3 EndZ=0
    g15: LineSegment StartX=-26.7 StartY=-33.9 StartZ=0 EndX=-26.7 EndY=-4.3 EndZ=0
    g16: LineSegment StartX=-2.5 StartY=-10.5 StartZ=0 EndX=-2.5 EndY=-27.7 EndZ=0
    g17: LineSegment StartX=-8.5 StartY=-4.3 StartZ=0 EndX=-8.5 EndY=-33.9 EndZ=0
    g18: LineSegment StartX=-5.5 StartY=-10.5 StartZ=0 EndX=-5.5 EndY=-27.7 EndZ=0
    g19: LineSegment StartX=-11.5 StartY=-4.3 StartZ=0 EndX=-11.5 EndY=-33.9 EndZ=0
    g20: LineSegment StartX=-14.6 StartY=-1.8 StartZ=0 EndX=-14.6 EndY=-36.4 EndZ=0
    g21: LineSegment StartX=-17.6 StartY=-1.8 StartZ=0 EndX=-17.6 EndY=-36.4 EndZ=0
    g22: LineSegment StartX=-20.6 StartY=-36.4 StartZ=0 EndX=-20.6 EndY=-1.8 EndZ=0
    g23: LineSegment StartX=-23.6 StartY=-1.8 StartZ=0 EndX=-23.6 EndY=-36.4 EndZ=0
  constraints (48):
    c: Block(g0)
    c: Block(g1)
    c: Block(g2)
    c: Block(g3)
    c: Block(g4)
    c: Block(g5)
    c: Block(g6)
    c: Block(g7)
    c: Block(g8)
    c: Block(g9)
    c: Block(g10)
    c: Block(g11)
    c: Coincident(g12,g1)
    c: Coincident(g12,g2)
    c: Vertical(g12)
    c: Coincident(g13,g1)
    c: Coincident(g13,g2)
    c: Vertical(g13)
    c: Coincident(g14,g11)
    c: Coincident(g14,g7)
    c: Vertical(g14)
    c: Coincident(g15,g11)
    c: Coincident(g15,g7)
    c: Vertical(g15)
    c: Coincident(g16,g0)
    c: Coincident(g16,g3)
    c: Vertical(g16)
    c: Coincident(g17,g4)
    c: Coincident(g17,g8)
    c: Vertical(g17)
    c: Coincident(g18,g0)
    c: Coincident(g18,g3)
    c: Vertical(g18)
    c: Coincident(g19,g4)
    c: Coincident(g19,g8)
    c: Vertical(g19)
    c: Coincident(g20,g5)
    c: Coincident(g20,g9)
    c: Vertical(g20)
    c: Coincident(g21,g5)
    c: Coincident(g21,g9)
    c: Vertical(g21)
    c: Coincident(g22,g10)
    c: Coincident(g22,g6)
    c: Vertical(g22)
    c: Coincident(g23,g6)
    c: Coincident(g23,g10)
    c: Vertical(g23)
FEATURE [Part::Extrusion] Extrude045  label="removeToCreateFanGrillHoles003"
  Base = -> Sketch054
  Dir = (0,-1,6e-16)
  DirMode = 2
  FaceMakerClass = Part::FaceMakerBullseye
  LengthFwd = 10
  LengthRev = 0
  Placement = pos=(65.4,44,54.82) rot=(0,0,1;0rad)
  Solid = true
  Symmetric = false
FEATURE [Part::Feature] Face105 .. Face108  x4 (patterned run collapsed; names and placements below)
  shape: bbox 3.5 x 17.8 x 2e-07 mm, 1 faces, 0 solids (baked)
FEATURE [Part::Revolution] Revolve113  label="removeToCreateScrewAndThreadedInsertHole041"
  Angle = 360
  Axis = (0,1,0)
  Base = (0,0,0)
  FaceMakerClass = Part::FaceMakerBullseye
  Placement = pos=(62.3,30.3,19.7) rot=(0,0,1;0rad)
  Solid = false
  Source = -> Face105
  Symmetric = false
FEATURE [Part::Revolution] Revolve114  label="removeToCreateScrewAndThreadedInsertHole042"
  Angle = 360
  Axis = (0,1,0)
  Base = (0,0,0)
  FaceMakerClass = Part::FaceMakerBullseye
  Placement = pos=(62.3,30.3,51.7) rot=(0,0,1;0rad)
  Solid = false
  Source = -> Face106
  Symmetric = false
FEATURE [Part::Revolution] Revolve115  label="removeToCreateScrewAndThreadedInsertHole043"
  Angle = 360
  Axis = (0,1,0)
  Base = (0,0,0)
  FaceMakerClass = Part::FaceMakerBullseye
  Placement = pos=(30.3,30.3,19.7) rot=(0,0,1;0rad)
  Solid = false
  Source = -> Face107
  Symmetric = false
FEATURE [Part::Revolution] Revolve116  label="removeToCreateScrewAndThreadedInsertHole044"
  Angle = 360
  Axis = (0,1,0)
  Base = (0,0,0)
  FaceMakerClass = Part::FaceMakerBullseye
  Placement = pos=(30.3,30.3,51.7) rot=(0,0,1;0rad)
  Solid = false
  Source = -> Face108
  Symmetric = false
FEATURE [Part::MultiFuse] Fusion083  label="createThreadedInsertHolesForFan004"
  Shapes = -> [Revolve113,Revolve114,Revolve115,Revolve116]
FEATURE [Part::Box] Box024  label="removeToCreteHoleForPlugHousing026"
  AttacherType = Attacher::AttachEngine3D
  Height = 28.6
  Length = 10
  Placement = pos=(-2,0,21.7) rot=(0,0,1;0rad)
  Width = 19
FEATURE [Part::Cylinder] Cylinder038  label="removeToCreteHoleForPlugHousing027"
  Angle = 360
  AttacherType = Attacher::AttachEngine3D
  Height = 20
  Placement = pos=(-2,19,36) rot=(0,1,0;1.5708rad)
  Radius = 14.3
FEATURE [Part::MultiFuse] Fusion084  label="removeToCreteHoleForPlugHousing028"
  Shapes = -> [Box024,Cylinder038]
FEATURE [Part::Cylinder] Cylinder039
  Angle = 360
  AttacherType = Attacher::AttachEngine3D
  Height = 20
  Placement = pos=(0,0,36.15) rot=(0,0,1;0rad)
  Radius = 14.3
FEATURE [Part::Cylinder] Cylinder040
  Angle = 360
  AttacherType = Attacher::AttachEngine3D
  Height = 10
  Placement = pos=(0,0,36.15) rot=(0,0,1;0rad)
  Radius = 4
FEATURE [Part::Box] Box025  label="removeToCreteHoleForPlugHousing030"
  AttacherType = Attacher::AttachEngine3D
  Height = 28.6
  Length = 20
  Placement = pos=(106.15,0,21.7) rot=(0,0,1;0rad)
  Width = 19
FEATURE [Part::MultiFuse] Fusion086  label="removeToCreteHoleForPlugHousing031"
  Placement = pos=(70,19,36) rot=(0,1,0;1.5708rad)
  Shapes = -> [Cylinder039,Cylinder040]
FEATURE [Part::MultiFuse] Fusion085  label="removeToCreteHoleForPlugHousing029"
  Shapes = -> [Box025,Fusion086]
FEATURE [Sketcher::SketchObject] Sketch055
  FullyConstrained = true
  Placement = pos=(117,19,0) rot=(0.57735,0.57735,0.57735;2.0944rad)
  sketch-geometry (48):
    g0: LineSegment StartX=-49.19 StartY=69.25 StartZ=0 EndX=-49.19 EndY=66.25 EndZ=0
    g1: LineSegment StartX=-49.19 StartY=63.5 StartZ=0 EndX=-49.19 EndY=60.5 EndZ=0
    g2: LineSegment StartX=-49.19 StartY=57.75 StartZ=0 EndX=-49.19 EndY=54.75 EndZ=0
    g3: LineSegment StartX=-49.19 StartY=52 StartZ=0 EndX=-49.19 EndY=49 EndZ=0
    g4: LineSegment StartX=-49.19 StartY=46.25 StartZ=0 EndX=-49.19 EndY=43.25 EndZ=0
    g5: LineSegment StartX=-49.19 StartY=40.5 StartZ=0 EndX=-49.19 EndY=37.5 EndZ=0
    g6: LineSegment StartX=-49.19 StartY=34.5 StartZ=0 EndX=-49.19 EndY=31.5 EndZ=0
    g7: LineSegment StartX=-49.19 StartY=28.75 StartZ=0 EndX=-49.19 EndY=25.75 EndZ=0
    g8: LineSegment StartX=-49.19 StartY=23 StartZ=0 EndX=-49.19 EndY=20 EndZ=0
    g9: LineSegment StartX=-49.19 StartY=17.25 StartZ=0 EndX=-49.19 EndY=14.25 EndZ=0
    g10: LineSegment StartX=-49.19 StartY=11.5 StartZ=0 EndX=-49.19 EndY=8.5 EndZ=0
    g11: LineSegment StartX=-49.19 StartY=5.75 StartZ=0 EndX=-49.19 EndY=2.75 EndZ=0
    g12: ArcOfCircle CenterX=-1.5 CenterY=67.75 CenterZ=0 NormalX=0 NormalY=0 NormalZ=1 AngleXU=0 Radius=1.5 StartAngle=4.71239 EndAngle=7.85398
    g13: ArcOfCircle CenterX=-1.5 CenterY=62 CenterZ=0 NormalX=0 NormalY=0 NormalZ=1 AngleXU=0 Radius=1.5 StartAngle=4.71239 EndAngle=7.85398
    g14: ArcOfCircle CenterX=-1.5 CenterY=56.25 CenterZ=0 NormalX=0 NormalY=0 NormalZ=1 AngleXU=0 Radius=1.5 StartAngle=4.71239 EndAngle=7.85398
    g15: ArcOfCircle CenterX=-11.49 CenterY=50.5 CenterZ=0 NormalX=0 NormalY=0 NormalZ=1 AngleXU=0 Radius=1.5 StartAngle=4.71239 EndAngle=7.85398
    g16: ArcOfCircle CenterX=-16.28 CenterY=44.75 CenterZ=0 NormalX=0 NormalY=0 NormalZ=1 AngleXU=0 Radius=1.5 StartAngle=4.71239 EndAngle=7.85398
    g17: ArcOfCircle CenterX=-18.2337 CenterY=39 CenterZ=0 NormalX=0 NormalY=0 NormalZ=1 AngleXU=0 Radius=1.5 StartAngle=4.71485 EndAngle=7.85398
    g18: ArcOfCircle CenterX=-16.2837 CenterY=27.25 CenterZ=0 NormalX=0 NormalY=0 NormalZ=1 AngleXU=0 Radius=1.5 StartAngle=4.71485 EndAngle=7.85398
    g19: ArcOfCircle CenterX=-18.2337 CenterY=33 CenterZ=0 NormalX=0 NormalY=0 NormalZ=1 AngleXU=0 Radius=1.5 StartAngle=4.71485 EndAngle=7.85398
    g20: ArcOfCircle CenterX=-11.49 CenterY=21.5 CenterZ=0 NormalX=0 NormalY=0 NormalZ=1 AngleXU=0 Radius=1.5 StartAngle=4.71239 EndAngle=7.85398
    g21: ArcOfCircle CenterX=-1.5 CenterY=4.25 CenterZ=0 NormalX=0 NormalY=0 NormalZ=1 AngleXU=0 Radius=1.5 StartAngle=4.71239 EndAngle=7.85398
    g22: ArcOfCircle CenterX=-1.5 CenterY=10 CenterZ=0 NormalX=0 NormalY=0 NormalZ=1 AngleXU=0 Radius=1.5 StartAngle=4.71239 EndAngle=7.85398
    g23: ArcOfCircle CenterX=-1.5 CenterY=15.75 CenterZ=0 NormalX=0 NormalY=0 NormalZ=1 AngleXU=0 Radius=1.5 StartAngle=4.71239 EndAngle=7.85398
    g24: LineSegment StartX=-49.19 StartY=69.25 StartZ=0 EndX=-1.5 EndY=69.25 EndZ=0
    g25: LineSegment StartX=-49.19 StartY=66.25 StartZ=0 EndX=-1.5 EndY=66.25 EndZ=0
    g26: LineSegment StartX=-49.19 StartY=63.5 StartZ=0 EndX=-1.5 EndY=63.5 EndZ=0
    g27: LineSegment StartX=-49.19 StartY=60.5 StartZ=0 EndX=-1.5 EndY=60.5 EndZ=0
    g28: LineSegment StartX=-49.19 StartY=57.75 StartZ=0 EndX=-1.5 EndY=57.75 EndZ=0
    g29: LineSegment StartX=-49.19 StartY=54.75 StartZ=0 EndX=-1.5 EndY=54.75 EndZ=0
    g30: LineSegment StartX=-49.19 StartY=52 StartZ=0 EndX=-11.49 EndY=52 EndZ=0
    g31: LineSegment StartX=-49.19 StartY=49 StartZ=0 EndX=-11.49 EndY=49 EndZ=0
    g32: LineSegment StartX=-49.19 StartY=46.25 StartZ=0 EndX=-16.28 EndY=46.25 EndZ=0
    g33: LineSegment StartX=-49.19 StartY=43.25 StartZ=0 EndX=-16.28 EndY=43.25 EndZ=0
    g34: LineSegment StartX=-49.19 StartY=40.5 StartZ=0 EndX=-18.2337 EndY=40.5 EndZ=0
    g35: LineSegment StartX=-49.19 StartY=37.5 StartZ=0 EndX=-18.23 EndY=37.5 EndZ=0
    g36: LineSegment StartX=-49.19 StartY=34.5 StartZ=0 EndX=-18.2337 EndY=34.5 EndZ=0
    g37: LineSegment StartX=-49.19 StartY=31.5 StartZ=0 EndX=-18.23 EndY=31.5 EndZ=0
    g38: LineSegment StartX=-49.19 StartY=28.75 StartZ=0 EndX=-16.2837 EndY=28.75 EndZ=0
    g39: LineSegment StartX=-49.19 StartY=25.75 StartZ=0 EndX=-16.28 EndY=25.75 EndZ=0
    g40: LineSegment StartX=-49.19 StartY=23 StartZ=0 EndX=-11.49 EndY=23 EndZ=0
    g41: LineSegment StartX=-49.19 StartY=20 StartZ=0 EndX=-11.49 EndY=20 EndZ=0
    g42: LineSegment StartX=-49.19 StartY=17.25 StartZ=0 EndX=-1.5 EndY=17.25 EndZ=0
    g43: LineSegment StartX=-49.19 StartY=14.25 StartZ=0 EndX=-1.5 EndY=14.25 EndZ=0
    g44: LineSegment StartX=-49.19 StartY=11.5 StartZ=0 EndX=-1.5 EndY=11.5 EndZ=0
    g45: LineSegment StartX=-49.19 StartY=8.5 StartZ=0 EndX=-1.5 EndY=8.5 EndZ=0
    g46: LineSegment StartX=-49.19 StartY=5.75 StartZ=0 EndX=-1.5 EndY=5.75 EndZ=0
    g47: LineSegment StartX=-49.19 StartY=2.75 StartZ=0 EndX=-1.5 EndY=2.75 EndZ=0
  constraints (120):
    c: Vertical(g0)
    c: Distance(g0) = 3
    c: Block(g0)
    c: Vertical(g1)
    c: Distance(g1) = 3
    c: Vertical(g2)
    c: Equal(g0,g2) = 3
    c: Block(g2)
    c: Vertical(g3)
    c: Equal(g1,g3) = 3
    c: Vertical(g4)
    c: Equal(g0,g4) = 3
    c: Block(g4)
    c: Vertical(g5)
    c: Equal(g1,g5) = 3
    c: Vertical(g6)
    c: Equal(g0,g6) = 3
    c: Block(g6)
    c: Vertical(g7)
    c: Equal(g1,g7) = 3
    c: Vertical(g8)
    c: Equal(g0,g8) = 3
    c: Block(g8)
    c: Vertical(g9)
    c: Equal(g1,g9) = 3
    c: Vertical(g10)
    c: Equal(g0,g10) = 3
    c: Block(g10)
    c: Vertical(g11)
    c: Equal(g1,g11) = 3
    c: Block(g12)
    c: Block(g13)
    c: Block(g14)
    c: Block(g15)
    c: Block(g16)
    c: Block(g17)
    c: Block(g18)
    c: Block(g19)
    c: Block(g20)
    c: Block(g21)
    c: Block(g22)
    c: Block(g23)
    c: Block(g11)
    c: Block(g9)
    c: Block(g7)
    c: Block(g5)
    c: Block(g3)
    c: Block(g1)
    c: Coincident(g24,g0)
    c: Coincident(g24,g12)
    c: Horizontal(g24)
    c: Coincident(g25,g0)
    c: Coincident(g25,g12)
    c: Horizontal(g25)
    c: Coincident(g26,g1)
    c: Coincident(g26,g13)
    c: Horizontal(g26)
    c: Coincident(g27,g1)
    c: Coincident(g27,g13)
    c: Horizontal(g27)
    c: Coincident(g28,g2)
    c: Coincident(g28,g14)
    c: Horizontal(g28)
    c: Coincident(g29,g2)
    c: Coincident(g29,g14)
    c: Horizontal(g29)
    c: Coincident(g30,g3)
    c: Coincident(g30,g15)
    c: Horizontal(g30)
    c: Coincident(g31,g3)
    c: Coincident(g31,g15)
    c: Horizontal(g31)
    c: Coincident(g32,g4)
    c: Coincident(g32,g16)
    c: Horizontal(g32)
    c: Coincident(g33,g4)
    c: Coincident(g33,g16)
    c: Horizontal(g33)
    c: Coincident(g34,g5)
    c: Coincident(g34,g17)
    c: Horizontal(g34)
    c: Coincident(g35,g5)
    c: Coincident(g35,g17)
    c: Horizontal(g35)
    c: Coincident(g36,g6)
    c: Coincident(g36,g19)
    c: Horizontal(g36)
    c: Coincident(g37,g6)
    c: Coincident(g37,g19)
    c: Horizontal(g37)
    c: Coincident(g38,g7)
    c: Coincident(g38,g18)
    c: Horizontal(g38)
    c: Coincident(g39,g7)
    c: Coincident(g39,g18)
    c: Horizontal(g39)
    c: Coincident(g40,g8)
    c: Coincident(g40,g20)
    c: Horizontal(g40)
    c: Coincident(g41,g8)
    c: Coincident(g41,g20)
    c: Horizontal(g41)
    c: Coincident(g42,g9)
    c: Coincident(g42,g23)
    c: Horizontal(g42)
    c: Coincident(g43,g9)
    c: Coincident(g43,g23)
    c: Horizontal(g43)
    c: Coincident(g44,g10)
    c: Coincident(g44,g22)
    c: Horizontal(g44)
    c: Coincident(g45,g10)
    c: Coincident(g45,g22)
    c: Horizontal(g45)
    c: Coincident(g46,g11)
    c: Coincident(g46,g21)
    c: Horizontal(g46)
    c: Coincident(g47,g11)
    c: Coincident(g47,g21)
    c: Horizontal(g47)
FEATURE [Part::Extrusion] Extrude046
  Base = -> Sketch055
  Dir = (1,0,0)
  DirMode = 2
  FaceMakerClass = Part::FaceMakerBullseye
  LengthFwd = 23
  LengthRev = 0
  Placement = pos=(-19,0,0) rot=(0,0,1;0rad)
  Solid = true
  Symmetric = false
FEATURE [Part::Fillet] Fillet038  label="removeToCreateVentalationHoles001"
  Base = -> Extrude046
  Edges = <same value as first occurrence — deduplicated (x6 in doc)>
  Placement = pos=(7,0,0) rot=(0,0,1;0rad)
FEATURE [Sketcher::SketchObject] Sketch056  label="topSketch014"
  FullyConstrained = true
  sketch-geometry (22):
    g0: LineSegment StartX=5.21097e-06 StartY=3 StartZ=0 EndX=5.21097e-06 EndY=19 EndZ=0
    g1: ArcOfCircle CenterX=19 CenterY=19 CenterZ=0 NormalX=0 NormalY=0 NormalZ=1 AngleXU=0 Radius=19 StartAngle=1.5708 EndAngle=3.14159
    g2: ArcOfCircle CenterX=19 CenterY=19 CenterZ=0 NormalX=0 NormalY=0 NormalZ=1 AngleXU=0 Radius=16 StartAngle=1.5708 EndAngle=3.14159
    g3: LineSegment StartX=114 StartY=35 StartZ=0 EndX=19 EndY=35 EndZ=0
    g4: LineSegment StartX=5.21097e-06 StartY=3 StartZ=0 EndX=5.21097e-06 EndY=0 EndZ=0
    g5: LineSegment StartX=3 StartY=0 StartZ=0 EndX=5.21097e-06 EndY=0 EndZ=0
    g6: LineSegment StartX=3 StartY=19 StartZ=0 EndX=3 EndY=0 EndZ=0
    g7: LineSegment StartX=19 StartY=38 StartZ=0 EndX=124 EndY=38 EndZ=0
    g8: Circle CenterX=119 CenterY=35 CenterZ=0 NormalX=0 NormalY=0 NormalZ=1 AngleXU=0 Radius=1
    g9: Circle CenterX=121 CenterY=35 CenterZ=0 NormalX=0 NormalY=0 NormalZ=1 AngleXU=0 Radius=1
    g10: Circle CenterX=121 CenterY=33 CenterZ=0 NormalX=0 NormalY=0 NormalZ=1 AngleXU=0 Radius=1
    g11: BSplineCurve PolesCount=3 KnotsCount=2 Degree=2 IsPeriodic=0
    g12: GeomPoint X=119 Y=35 Z=0
    g13: GeomPoint X=121 Y=33 Z=0
    g14: LineSegment StartX=119 StartY=35 StartZ=0 EndX=114 EndY=35 EndZ=0
    g15: ArcOfCircle CenterX=105 CenterY=19 CenterZ=0 NormalX=0 NormalY=0 NormalZ=1 AngleXU=0 Radius=16 StartAngle=5.60905 EndAngle=6.28319
    g16: LineSegment StartX=121 StartY=33 StartZ=0 EndX=121 EndY=19 EndZ=0
    g17: LineSegment StartX=117.5 StartY=9.01251 StartZ=0 EndX=121.163 EndY=9.0125 EndZ=0
    g18: ArcOfCircle CenterX=105 CenterY=19 CenterZ=0 NormalX=0 NormalY=0 NormalZ=1 AngleXU=0 Radius=20.6155 StartAngle=5.7297 EndAngle=6.28319
    g19: LineSegment StartX=121.163 StartY=9.0125 StartZ=0 EndX=122.538 EndY=8.16329 EndZ=0
    g20: LineSegment StartX=124 StartY=38 StartZ=0 EndX=125.616 EndY=38 EndZ=0
    g21: LineSegment StartX=125.616 StartY=19 StartZ=0 EndX=125.616 EndY=38 EndZ=0
  constraints (49):
    c: Vertical(g0)
    c: Block(g0)
    c: Coincident(g1,g0)
    c: Block(g1)
    c: Coincident(g2,g1)
    c: Block(g2)
    c: Coincident(g3,g2)
    c: Horizontal(g3)
    c: Tangent(g3,g2)
    c: Coincident(g4,g0)
    c: Distance(g4) = 3
    c: Vertical(g4)
    c: Coincident(g5,g4)
    c: Horizontal(g5)
    c: Coincident(g6,g2)
    c: Coincident(g6,g5)
    c: Vertical(g6)
    c: Horizontal(g7)
    c: Distance(g7) = 105
    c: Coincident(g7,g1)
    c: Block(g3)
    c: Weight(g8) = 1
    c: Equal(g8,g9)
    c: Equal(g8,g10)
    c: InternalAlignment(g8,g11)
    c: InternalAlignment(g9,g11)
    c: InternalAlignment(g10,g11)
    c: InternalAlignment(g12,g11)
    c: InternalAlignment(g13,g11)
    c: Block(g11)
    c: Coincident(g14,g11)
    c: Coincident(g14,g3)
    c: Horizontal(g14)
    c: Block(g15)
    c: Coincident(g16,g11)
    c: Coincident(g16,g15)
    c: Vertical(g16)
    c: Distance(g16) = 14
    c: Coincident(g17,g15)
    c: Block(g18)
    c: Coincident(g19,g18)
    c: Coincident(g20,g7)
    c: Horizontal(g20)
    c: Vertical(g21)
    c: Coincident(g20,g21)
    c: Block(g20)
    c: Block(g21)
    c: Block(g19)
    c: Block(g17)
FEATURE [Part::Box] Box026  label="removeToCreteHoleForPlugHousing032"
  AttacherType = Attacher::AttachEngine3D
  Height = 28.6
  Length = 10
  Placement = pos=(-2,0,21.7) rot=(0,0,1;0rad)
  Width = 19
FEATURE [Part::Feature] Face109 .. Face112  x4 (patterned run collapsed; names and placements below)
  shape: bbox 3.5 x 17.8 x 2e-07 mm, 1 faces, 0 solids (baked)
FEATURE [Part::Revolution] Revolve117  label="removeToCreateScrewAndThreadedInsertHole045"
  Angle = 360
  Axis = (0,1,0)
  Base = (0,0,0)
  FaceMakerClass = Part::FaceMakerBullseye
  Placement = pos=(62.3,30.3,19.7) rot=(0,0,1;0rad)
  Solid = false
  Source = -> Face109
  Symmetric = false
FEATURE [Part::Revolution] Revolve118  label="removeToCreateScrewAndThreadedInsertHole046"
  Angle = 360
  Axis = (0,1,0)
  Base = (0,0,0)
  FaceMakerClass = Part::FaceMakerBullseye
  Placement = pos=(62.3,30.3,51.7) rot=(0,0,1;0rad)
  Solid = false
  Source = -> Face110
  Symmetric = false
FEATURE [Part::Revolution] Revolve119  label="removeToCreateScrewAndThreadedInsertHole047"
  Angle = 360
  Axis = (0,1,0)
  Base = (0,0,0)
  FaceMakerClass = Part::FaceMakerBullseye
  Placement = pos=(30.3,30.3,19.7) rot=(0,0,1;0rad)
  Solid = false
  Source = -> Face111
  Symmetric = false
FEATURE [Part::Revolution] Revolve120  label="removeToCreateScrewAndThreadedInsertHole048"
  Angle = 360
  Axis = (0,1,0)
  Base = (0,0,0)
  FaceMakerClass = Part::FaceMakerBullseye
  Placement = pos=(30.3,30.3,51.7) rot=(0,0,1;0rad)
  Solid = false
  Source = -> Face112
  Symmetric = false
FEATURE [Part::MultiFuse] Fusion087  label="createThreadedInsertHolesForFan005"
  Shapes = -> [Revolve117,Revolve118,Revolve119,Revolve120]
FEATURE [Part::Extrusion] Extrude047
  Base = -> Sketch056
  Dir = (0,0,1)
  DirMode = 2
  FaceMakerClass = Part::FaceMakerBullseye
  LengthFwd = 72
  LengthRev = 0
  Solid = true
  Symmetric = false
FEATURE [Part::Fillet] Fillet039  label="top019"
  Base = -> Extrude047
  Edges = 1 edges r=2: [Edge35]
FEATURE [Sketcher::SketchObject] Sketch057
  FullyConstrained = false
  Placement = pos=(0,0,0) rot=(1,0,0;1.5708rad)
  sketch-geometry (24):
    g0: ArcOfCircle CenterX=-4 CenterY=-10.5 CenterZ=0 NormalX=0 NormalY=0 NormalZ=1 AngleXU=0 Radius=1.5 StartAngle=6e-16 EndAngle=3.14159
    g1: ArcOfCircle CenterX=-34.2 CenterY=-10.5 CenterZ=0 NormalX=0 NormalY=0 NormalZ=1 AngleXU=0 Radius=1.5 StartAngle=0 EndAngle=3.14159
    g2: ArcOfCircle CenterX=-34.2 CenterY=-27.7 CenterZ=0 NormalX=0 NormalY=0 NormalZ=1 AngleXU=0 Radius=1.5 StartAngle=3.14159 EndAngle=6.28319
    g3: ArcOfCircle CenterX=-4 CenterY=-27.7 CenterZ=0 NormalX=0 NormalY=0 NormalZ=1 AngleXU=0 Radius=1.5 StartAngle=3.1416 EndAngle=6.28319
    g4: ArcOfCircle CenterX=-10 CenterY=-4.3 CenterZ=0 NormalX=0 NormalY=0 NormalZ=1 AngleXU=0 Radius=1.5 StartAngle=2e-16 EndAngle=3.14159
    g5: ArcOfCircle CenterX=-16.1 CenterY=-1.8 CenterZ=0 NormalX=0 NormalY=0 NormalZ=1 AngleXU=0 Radius=1.5 StartAngle=5e-16 EndAngle=3.14159
    g6: ArcOfCircle CenterX=-22.1 CenterY=-1.8 CenterZ=0 NormalX=0 NormalY=0 NormalZ=1 AngleXU=0 Radius=1.5 StartAngle=5e-16 EndAngle=3.14159
    g7: ArcOfCircle CenterX=-28.2 CenterY=-4.3 CenterZ=0 NormalX=0 NormalY=0 NormalZ=1 AngleXU=0 Radius=1.5 StartAngle=2e-16 EndAngle=3.14159
    g8: ArcOfCircle CenterX=-10 CenterY=-33.9 CenterZ=0 NormalX=0 NormalY=0 NormalZ=1 AngleXU=0 Radius=1.5 StartAngle=3.14159 EndAngle=6.28319
    g9: ArcOfCircle CenterX=-16.1 CenterY=-36.4 CenterZ=0 NormalX=0 NormalY=0 NormalZ=1 AngleXU=0 Radius=1.5 StartAngle=3.14159 EndAngle=6.28319
    g10: ArcOfCircle CenterX=-22.1 CenterY=-36.4 CenterZ=0 NormalX=0 NormalY=0 NormalZ=1 AngleXU=0 Radius=1.5 StartAngle=3.14159 EndAngle=6.28319
    g11: ArcOfCircle CenterX=-28.2 CenterY=-33.9 CenterZ=0 NormalX=0 NormalY=0 NormalZ=1 AngleXU=0 Radius=1.5 StartAngle=3.14159 EndAngle=6.28319
    g12: LineSegment StartX=-35.7 StartY=-10.5 StartZ=0 EndX=-35.7 EndY=-27.7 EndZ=0
    g13: LineSegment StartX=-32.7 StartY=-10.5 StartZ=0 EndX=-32.7 EndY=-27.7 EndZ=0
    g14: LineSegment StartX=-29.7 StartY=-33.9 StartZ=0 EndX=-29.7 EndY=-4.3 EndZ=0
    g15: LineSegment StartX=-26.7 StartY=-33.9 StartZ=0 EndX=-26.7 EndY=-4.3 EndZ=0
    g16: LineSegment StartX=-2.5 StartY=-10.5 StartZ=0 EndX=-2.5 EndY=-27.7 EndZ=0
    g17: LineSegment StartX=-8.5 StartY=-4.3 StartZ=0 EndX=-8.5 EndY=-33.9 EndZ=0
    g18: LineSegment StartX=-5.5 StartY=-10.5 StartZ=0 EndX=-5.5 EndY=-27.7 EndZ=0
    g19: LineSegment StartX=-11.5 StartY=-4.3 StartZ=0 EndX=-11.5 EndY=-33.9 EndZ=0
    g20: LineSegment StartX=-14.6 StartY=-1.8 StartZ=0 EndX=-14.6 EndY=-36.4 EndZ=0
    g21: LineSegment StartX=-17.6 StartY=-1.8 StartZ=0 EndX=-17.6 EndY=-36.4 EndZ=0
    g22: LineSegment StartX=-20.6 StartY=-36.4 StartZ=0 EndX=-20.6 EndY=-1.8 EndZ=0
    g23: LineSegment StartX=-23.6 StartY=-1.8 StartZ=0 EndX=-23.6 EndY=-36.4 EndZ=0
  constraints (48):
    c: Block(g0)
    c: Block(g1)
    c: Block(g2)
    c: Block(g3)
    c: Block(g4)
    c: Block(g5)
    c: Block(g6)
    c: Block(g7)
    c: Block(g8)
    c: Block(g9)
    c: Block(g10)
    c: Block(g11)
    c: Coincident(g12,g1)
    c: Coincident(g12,g2)
    c: Vertical(g12)
    c: Coincident(g13,g1)
    c: Coincident(g13,g2)
    c: Vertical(g13)
    c: Coincident(g14,g11)
    c: Coincident(g14,g7)
    c: Vertical(g14)
    c: Coincident(g15,g11)
    c: Coincident(g15,g7)
    c: Vertical(g15)
    c: Coincident(g16,g0)
    c: Coincident(g16,g3)
    c: Vertical(g16)
    c: Coincident(g17,g4)
    c: Coincident(g17,g8)
    c: Vertical(g17)
    c: Coincident(g18,g0)
    c: Coincident(g18,g3)
    c: Vertical(g18)
    c: Coincident(g19,g4)
    c: Coincident(g19,g8)
    c: Vertical(g19)
    c: Coincident(g20,g5)
    c: Coincident(g20,g9)
    c: Vertical(g20)
    c: Coincident(g21,g5)
    c: Coincident(g21,g9)
    c: Vertical(g21)
    c: Coincident(g22,g10)
    c: Coincident(g22,g6)
    c: Vertical(g22)
    c: Coincident(g23,g6)
    c: Coincident(g23,g10)
    c: Vertical(g23)
FEATURE [Part::Extrusion] Extrude048  label="removeToCreateFanGrillHoles004"
  Base = -> Sketch057
  Dir = (0,-1,6e-16)
  DirMode = 2
  FaceMakerClass = Part::FaceMakerBullseye
  LengthFwd = 10
  LengthRev = 0
  Placement = pos=(65.4,44,54.82) rot=(0,0,1;0rad)
  Solid = true
  Symmetric = false
FEATURE [Part::Cut] Cut040  label="top021"
  Base = -> Fillet039
  Tool = -> Extrude048
FEATURE [Part::Cylinder] Cylinder041  label="removeToCreteHoleForPlugHousing034"
  Angle = 360
  AttacherType = Attacher::AttachEngine3D
  Height = 20
  Placement = pos=(-2,19,36) rot=(0,1,0;1.5708rad)
  Radius = 14.3
FEATURE [Part::MultiFuse] Fusion089  label="removeToCreteHoleForPlugHousing035"
  Shapes = -> [Box026,Cylinder041]
FEATURE [Part::Cylinder] Cylinder042
  Angle = 360
  AttacherType = Attacher::AttachEngine3D
  Height = 20
  Placement = pos=(0,0,36.15) rot=(0,0,1;0rad)
  Radius = 14.3
FEATURE [Part::Cylinder] Cylinder043
  Angle = 360
  AttacherType = Attacher::AttachEngine3D
  Height = 10
  Placement = pos=(0,0,36.15) rot=(0,0,1;0rad)
  Radius = 4
FEATURE [Part::Box] Box027  label="removeToCreteHoleForPlugHousing036"
  AttacherType = Attacher::AttachEngine3D
  Height = 28.6
  Length = 20
  Placement = pos=(106.15,0,21.7) rot=(0,0,1;0rad)
  Width = 19
FEATURE [Part::Cut] Cut041  label="top022"
  Base = -> Cut040
  Tool = -> Fusion087
FEATURE [Part::Cut] Cut039  label="top020"
  Base = -> Cut041
  Tool = -> Fusion089
FEATURE [Part::MultiFuse] Fusion090  label="removeToCreteHoleForPlugHousing037"
  Placement = pos=(70,19,36) rot=(0,1,0;1.5708rad)
  Shapes = -> [Cylinder042,Cylinder043]
FEATURE [Part::MultiFuse] Fusion088  label="removeToCreteHoleForPlugHousing033"
  Shapes = -> [Box027,Fusion090]
FEATURE [Part::Cut] Cut042  label="removeToCreteHoleForPlugHousing038"
  Base = -> Cut039
  Tool = -> Fusion088
FEATURE [Part::MultiFuse] Fusion091  label="removeFromTop"
  Shapes = -> [Fillet038,Fusion085,Fusion084,Fusion083,Extrude045]
FEATURE [Part::Cut] Cut043  label="REAL TOP ====="
  Base = -> Fillet036
  Tool = -> Fusion091
FEATURE [Part::MultiFuse] Fusion092  label="caseScrewPillarBracket016"
  Shapes = -> [Extrude030,Extrude031,Extrude032,Extrude033,Extrude034,Extrude035,Extrude036,Extrude037,Box013,Box014]
FEATURE [Sketcher::SketchObject] Sketch058  label="topSketch015"
  FullyConstrained = true
  sketch-geometry (20):
    g0: LineSegment StartX=5.21097e-06 StartY=3 StartZ=0 EndX=5.21097e-06 EndY=19 EndZ=0
    g1: ArcOfCircle CenterX=19 CenterY=19 CenterZ=0 NormalX=0 NormalY=0 NormalZ=1 AngleXU=0 Radius=19 StartAngle=1.5708 EndAngle=3.14159
    g2: ArcOfCircle CenterX=19 CenterY=19 CenterZ=0 NormalX=0 NormalY=0 NormalZ=1 AngleXU=0 Radius=16 StartAngle=1.5708 EndAngle=3.14159
    g3: LineSegment StartX=114 StartY=35 StartZ=0 EndX=19 EndY=35 EndZ=0
    g4: LineSegment StartX=5.21097e-06 StartY=3 StartZ=0 EndX=5.21097e-06 EndY=0 EndZ=0
    g5: LineSegment StartX=3 StartY=0 StartZ=0 EndX=5.21097e-06 EndY=0 EndZ=0
    g6: LineSegment StartX=3 StartY=19 StartZ=0 EndX=3 EndY=0 EndZ=0
    g7: LineSegment StartX=19 StartY=38 StartZ=0 EndX=124 EndY=38 EndZ=0
    g8: Circle CenterX=119 CenterY=35 CenterZ=0 NormalX=0 NormalY=0 NormalZ=1 AngleXU=0 Radius=1
    g9: Circle CenterX=121 CenterY=35 CenterZ=0 NormalX=0 NormalY=0 NormalZ=1 AngleXU=0 Radius=1
    g10: Circle CenterX=121 CenterY=33 CenterZ=0 NormalX=0 NormalY=0 NormalZ=1 AngleXU=0 Radius=1
    g11: BSplineCurve PolesCount=3 KnotsCount=2 Degree=2 IsPeriodic=0
    g12: GeomPoint X=119 Y=35 Z=0
    g13: GeomPoint X=121 Y=33 Z=0
    g14: LineSegment StartX=119 StartY=35 StartZ=0 EndX=114 EndY=35 EndZ=0
    g15: ArcOfCircle CenterX=105 CenterY=19 CenterZ=0 NormalX=0 NormalY=0 NormalZ=1 AngleXU=0 Radius=19 StartAngle=5.7297 EndAngle=6.28319
    g16: ArcOfCircle CenterX=105 CenterY=19 CenterZ=0 NormalX=0 NormalY=0 NormalZ=1 AngleXU=0 Radius=16 StartAngle=5.60905 EndAngle=6.28319
    g17: LineSegment StartX=121 StartY=33 StartZ=0 EndX=121 EndY=19 EndZ=0
    g18: LineSegment StartX=124 StartY=38 StartZ=0 EndX=124 EndY=19 EndZ=0
    g19: LineSegment StartX=117.5 StartY=9.01251 StartZ=0 EndX=121.163 EndY=9.0125 EndZ=0
  constraints (46):
    c: Vertical(g0)
    c: Block(g0)
    c: Coincident(g1,g0)
    c: Block(g1)
    c: Coincident(g2,g1)
    c: Block(g2)
    c: Coincident(g3,g2)
    c: Horizontal(g3)
    c: Tangent(g3,g2)
    c: Coincident(g4,g0)
    c: Distance(g4) = 3
    c: Vertical(g4)
    c: Coincident(g5,g4)
    c: Horizontal(g5)
    c: Coincident(g6,g2)
    c: Coincident(g6,g5)
    c: Vertical(g6)
    c: Horizontal(g7)
    c: Distance(g7) = 105
    c: Coincident(g7,g1)
    c: Block(g3)
    c: Weight(g8) = 1
    c: Equal(g8,g9)
    c: Equal(g8,g10)
    c: InternalAlignment(g8,g11)
    c: InternalAlignment(g9,g11)
    c: InternalAlignment(g10,g11)
    c: InternalAlignment(g12,g11)
    c: InternalAlignment(g13,g11)
    c: Block(g11)
    c: Coincident(g14,g11)
    c: Coincident(g14,g3)
    c: Horizontal(g14)
    c: Block(g15)
    c: Coincident(g16,g15)
    c: Block(g16)
    c: Coincident(g17,g11)
    c: Coincident(g17,g16)
    c: Vertical(g17)
    c: Distance(g17) = 14
    c: Coincident(g18,g7)
    c: Coincident(g18,g15)
    c: Vertical(g18)
    c: Distance(g18) = 19
    c: Coincident(g19,g16)
    c: Coincident(g19,g15)
FEATURE [Part::Extrusion] Extrude049  label="top023"
  Base = -> Sketch058
  Dir = (0,0,1)
  DirMode = 2
  FaceMakerClass = Part::FaceMakerBullseye
  LengthFwd = 72
  LengthRev = 0
  Solid = true
  Symmetric = false
FEATURE [Sketcher::SketchObject] Sketch059
  FullyConstrained = true
  MapMode = 3
  Placement = pos=(0,0,0) rot=(1,0,0;1.5708rad)
  Support = -> [Extrude049]
  sketch-geometry (8):
    g0: Circle CenterX=80.351 CenterY=-67.6202 CenterZ=0 NormalX=0 NormalY=0 NormalZ=1 AngleXU=0 Radius=2
    g1: Circle CenterX=80.351 CenterY=-67.6202 CenterZ=0 NormalX=0 NormalY=0 NormalZ=1 AngleXU=0 Radius=3
    g2: Circle CenterX=80.351 CenterY=-4.92017 CenterZ=0 NormalX=0 NormalY=0 NormalZ=1 AngleXU=0 Radius=2
    g3: Circle CenterX=80.351 CenterY=-4.92017 CenterZ=0 NormalX=0 NormalY=0 NormalZ=1 AngleXU=0 Radius=3
    g4: Circle CenterX=23.851 CenterY=-4.92017 CenterZ=0 NormalX=0 NormalY=0 NormalZ=1 AngleXU=0 Radius=2
    g5: Circle CenterX=23.851 CenterY=-4.92017 CenterZ=0 NormalX=0 NormalY=0 NormalZ=1 AngleXU=0 Radius=3
    g6: Circle CenterX=23.851 CenterY=-67.6202 CenterZ=0 NormalX=0 NormalY=0 NormalZ=1 AngleXU=0 Radius=2
    g7: Circle CenterX=23.851 CenterY=-67.6202 CenterZ=0 NormalX=0 NormalY=0 NormalZ=1 AngleXU=0 Radius=3
  constraints (8):
    c: Block(g3)
    c: Block(g2)
    c: Block(g1)
    c: Block(g0)
    c: Block(g6)
    c: Block(g7)
    c: Block(g4)
    c: Block(g5)
FEATURE [Sketcher::SketchObject] Sketch060
  FullyConstrained = true
  MapMode = 3
  Placement = pos=(0,0,0) rot=(1,0,0;1.5708rad)
  Support = -> [Extrude049]
  sketch-geometry (8):
    g0: Circle CenterX=80.351 CenterY=-67.6202 CenterZ=0 NormalX=0 NormalY=0 NormalZ=1 AngleXU=0 Radius=3
    g1: Circle CenterX=80.351 CenterY=-4.92017 CenterZ=0 NormalX=0 NormalY=0 NormalZ=1 AngleXU=0 Radius=3
    g2: Circle CenterX=23.851 CenterY=-4.92017 CenterZ=0 NormalX=0 NormalY=0 NormalZ=1 AngleXU=0 Radius=3
    g3: Circle CenterX=23.851 CenterY=-67.6202 CenterZ=0 NormalX=0 NormalY=0 NormalZ=1 AngleXU=0 Radius=3
    g4: Circle CenterX=23.851 CenterY=-67.6202 CenterZ=0 NormalX=0 NormalY=0 NormalZ=1 AngleXU=0 Radius=5
    g5: Circle CenterX=80.351 CenterY=-67.6202 CenterZ=0 NormalX=0 NormalY=0 NormalZ=1 AngleXU=0 Radius=5
    g6: Circle CenterX=23.851 CenterY=-4.92017 CenterZ=0 NormalX=0 NormalY=0 NormalZ=1 AngleXU=0 Radius=5
    g7: Circle CenterX=80.351 CenterY=-4.92017 CenterZ=0 NormalX=0 NormalY=0 NormalZ=1 AngleXU=0 Radius=5
  constraints (8):
    c: Block(g1)
    c: Block(g0)
    c: Block(g3)
    c: Block(g2)
    c: Block(g5)
    c: Block(g4)
    c: Block(g6)
    c: Block(g7)
FEATURE [Sketcher::SketchObject] Sketch061
  FullyConstrained = true
  MapMode = 3
  Placement = pos=(0,0,0) rot=(1,0,0;1.5708rad)
  sketch-geometry (8):
    g0: Circle CenterX=80.351 CenterY=-67.6202 CenterZ=0 NormalX=0 NormalY=0 NormalZ=1 AngleXU=0 Radius=3
    g1: Circle CenterX=80.351 CenterY=-4.92017 CenterZ=0 NormalX=0 NormalY=0 NormalZ=1 AngleXU=0 Radius=3
    g2: Circle CenterX=23.851 CenterY=-4.92017 CenterZ=0 NormalX=0 NormalY=0 NormalZ=1 AngleXU=0 Radius=3
    g3: Circle CenterX=23.851 CenterY=-67.6202 CenterZ=0 NormalX=0 NormalY=0 NormalZ=1 AngleXU=0 Radius=3
    g4: Circle CenterX=23.851 CenterY=-67.6202 CenterZ=0 NormalX=0 NormalY=0 NormalZ=1 AngleXU=0 Radius=5
    g5: Circle CenterX=80.351 CenterY=-67.6202 CenterZ=0 NormalX=0 NormalY=0 NormalZ=1 AngleXU=0 Radius=5
    g6: Circle CenterX=23.851 CenterY=-4.92017 CenterZ=0 NormalX=0 NormalY=0 NormalZ=1 AngleXU=0 Radius=5
    g7: Circle CenterX=80.351 CenterY=-4.92017 CenterZ=0 NormalX=0 NormalY=0 NormalZ=1 AngleXU=0 Radius=5
  constraints (8):
    c: Block(g1)
    c: Block(g0)
    c: Block(g3)
    c: Block(g2)
    c: Block(g5)
    c: Block(g4)
    c: Block(g6)
    c: Block(g7)
FEATURE [Sketcher::SketchObject] Sketch062  label="topSketch016"
  FullyConstrained = true
  sketch-geometry (20):
    g0: LineSegment StartX=5.21097e-06 StartY=3 StartZ=0 EndX=5.21097e-06 EndY=19 EndZ=0
    g1: ArcOfCircle CenterX=19 CenterY=19 CenterZ=0 NormalX=0 NormalY=0 NormalZ=1 AngleXU=0 Radius=19 StartAngle=1.5708 EndAngle=3.14159
    g2: ArcOfCircle CenterX=19 CenterY=19 CenterZ=0 NormalX=0 NormalY=0 NormalZ=1 AngleXU=0 Radius=16 StartAngle=1.5708 EndAngle=3.14159
    g3: LineSegment StartX=114 StartY=35 StartZ=0 EndX=19 EndY=35 EndZ=0
    g4: LineSegment StartX=5.21097e-06 StartY=3 StartZ=0 EndX=5.21097e-06 EndY=0 EndZ=0
    g5: LineSegment StartX=3 StartY=0 StartZ=0 EndX=5.21097e-06 EndY=0 EndZ=0
    g6: LineSegment StartX=3 StartY=19 StartZ=0 EndX=3 EndY=0 EndZ=0
    g7: LineSegment StartX=19 StartY=38 StartZ=0 EndX=124 EndY=38 EndZ=0
    g8: Circle CenterX=119 CenterY=35 CenterZ=0 NormalX=0 NormalY=0 NormalZ=1 AngleXU=0 Radius=1
    g9: Circle CenterX=121 CenterY=35 CenterZ=0 NormalX=0 NormalY=0 NormalZ=1 AngleXU=0 Radius=1
    g10: Circle CenterX=121 CenterY=33 CenterZ=0 NormalX=0 NormalY=0 NormalZ=1 AngleXU=0 Radius=1
    g11: BSplineCurve PolesCount=3 KnotsCount=2 Degree=2 IsPeriodic=0
    g12: GeomPoint X=119 Y=35 Z=0
    g13: GeomPoint X=121 Y=33 Z=0
    g14: LineSegment StartX=119 StartY=35 StartZ=0 EndX=114 EndY=35 EndZ=0
    g15: ArcOfCircle CenterX=105 CenterY=19 CenterZ=0 NormalX=0 NormalY=0 NormalZ=1 AngleXU=0 Radius=19 StartAngle=5.7297 EndAngle=6.28319
    g16: ArcOfCircle CenterX=105 CenterY=19 CenterZ=0 NormalX=0 NormalY=0 NormalZ=1 AngleXU=0 Radius=16 StartAngle=5.60905 EndAngle=6.28319
    g17: LineSegment StartX=121 StartY=33 StartZ=0 EndX=121 EndY=19 EndZ=0
    g18: LineSegment StartX=124 StartY=38 StartZ=0 EndX=124 EndY=19 EndZ=0
    g19: LineSegment StartX=117.5 StartY=9.01251 StartZ=0 EndX=121.163 EndY=9.0125 EndZ=0
  constraints (46):
    c: Vertical(g0)
    c: Block(g0)
    c: Coincident(g1,g0)
    c: Block(g1)
    c: Coincident(g2,g1)
    c: Block(g2)
    c: Coincident(g3,g2)
    c: Horizontal(g3)
    c: Tangent(g3,g2)
    c: Coincident(g4,g0)
    c: Distance(g4) = 3
    c: Vertical(g4)
    c: Coincident(g5,g4)
    c: Horizontal(g5)
    c: Coincident(g6,g2)
    c: Coincident(g6,g5)
    c: Vertical(g6)
    c: Horizontal(g7)
    c: Distance(g7) = 105
    c: Coincident(g7,g1)
    c: Block(g3)
    c: Weight(g8) = 1
    c: Equal(g8,g9)
    c: Equal(g8,g10)
    c: InternalAlignment(g8,g11)
    c: InternalAlignment(g9,g11)
    c: InternalAlignment(g10,g11)
    c: InternalAlignment(g12,g11)
    c: InternalAlignment(g13,g11)
    c: Block(g11)
    c: Coincident(g14,g11)
    c: Coincident(g14,g3)
    c: Horizontal(g14)
    c: Block(g15)
    c: Coincident(g16,g15)
    c: Block(g16)
    c: Coincident(g17,g11)
    c: Coincident(g17,g16)
    c: Vertical(g17)
    c: Distance(g17) = 14
    c: Coincident(g18,g7)
    c: Coincident(g18,g15)
    c: Vertical(g18)
    c: Distance(g18) = 19
    c: Coincident(g19,g16)
    c: Coincident(g19,g15)
FEATURE [Part::Extrusion] Extrude053  label="top024"
  Base = -> Sketch062
  Dir = (0,0,1)
  DirMode = 2
  FaceMakerClass = Part::FaceMakerBullseye
  LengthFwd = 72
  LengthRev = 0
  Solid = true
  Symmetric = false
FEATURE [Sketcher::SketchObject] Sketch063
  FullyConstrained = true
  MapMode = 3
  Placement = pos=(0,0,0) rot=(1,0,0;1.5708rad)
  Support = -> [Extrude053]
  sketch-geometry (8):
    g0: Circle CenterX=80.351 CenterY=-67.6202 CenterZ=0 NormalX=0 NormalY=0 NormalZ=1 AngleXU=0 Radius=2
    g1: Circle CenterX=80.351 CenterY=-67.6202 CenterZ=0 NormalX=0 NormalY=0 NormalZ=1 AngleXU=0 Radius=3
    g2: Circle CenterX=80.351 CenterY=-4.92017 CenterZ=0 NormalX=0 NormalY=0 NormalZ=1 AngleXU=0 Radius=2
    g3: Circle CenterX=80.351 CenterY=-4.92017 CenterZ=0 NormalX=0 NormalY=0 NormalZ=1 AngleXU=0 Radius=3
    g4: Circle CenterX=23.851 CenterY=-4.92017 CenterZ=0 NormalX=0 NormalY=0 NormalZ=1 AngleXU=0 Radius=2
    g5: Circle CenterX=23.851 CenterY=-4.92017 CenterZ=0 NormalX=0 NormalY=0 NormalZ=1 AngleXU=0 Radius=3
    g6: Circle CenterX=23.851 CenterY=-67.6202 CenterZ=0 NormalX=0 NormalY=0 NormalZ=1 AngleXU=0 Radius=2
    g7: Circle CenterX=23.851 CenterY=-67.6202 CenterZ=0 NormalX=0 NormalY=0 NormalZ=1 AngleXU=0 Radius=3
  constraints (8):
    c: Block(g3)
    c: Block(g2)
    c: Block(g1)
    c: Block(g0)
    c: Block(g6)
    c: Block(g7)
    c: Block(g4)
    c: Block(g5)
FEATURE [Part::Extrusion] Extrude054
  Base = -> Sketch063
  Dir = (0,-1,2e-16)
  DirMode = 2
  FaceMakerClass = Part::FaceMakerBullseye
  LengthFwd = 6
  LengthRev = 0
  Placement = pos=(0,9,0) rot=(0,0,1;0rad)
  Solid = true
  Symmetric = false
FEATURE [Sketcher::SketchObject] Sketch064  label="topSketch017"
  FullyConstrained = true
  sketch-geometry (20):
    g0: LineSegment StartX=5.21097e-06 StartY=3 StartZ=0 EndX=5.21097e-06 EndY=19 EndZ=0
    g1: ArcOfCircle CenterX=19 CenterY=19 CenterZ=0 NormalX=0 NormalY=0 NormalZ=1 AngleXU=0 Radius=19 StartAngle=1.5708 EndAngle=3.14159
    g2: ArcOfCircle CenterX=19 CenterY=19 CenterZ=0 NormalX=0 NormalY=0 NormalZ=1 AngleXU=0 Radius=16 StartAngle=1.5708 EndAngle=3.14159
    g3: LineSegment StartX=114 StartY=35 StartZ=0 EndX=19 EndY=35 EndZ=0
    g4: LineSegment StartX=5.21097e-06 StartY=3 StartZ=0 EndX=5.21097e-06 EndY=0 EndZ=0
    g5: LineSegment StartX=3 StartY=0 StartZ=0 EndX=5.21097e-06 EndY=0 EndZ=0
    g6: LineSegment StartX=3 StartY=19 StartZ=0 EndX=3 EndY=0 EndZ=0
    g7: LineSegment StartX=19 StartY=38 StartZ=0 EndX=124 EndY=38 EndZ=0
    g8: Circle CenterX=119 CenterY=35 CenterZ=0 NormalX=0 NormalY=0 NormalZ=1 AngleXU=0 Radius=1
    g9: Circle CenterX=121 CenterY=35 CenterZ=0 NormalX=0 NormalY=0 NormalZ=1 AngleXU=0 Radius=1
    g10: Circle CenterX=121 CenterY=33 CenterZ=0 NormalX=0 NormalY=0 NormalZ=1 AngleXU=0 Radius=1
    g11: BSplineCurve PolesCount=3 KnotsCount=2 Degree=2 IsPeriodic=0
    g12: GeomPoint X=119 Y=35 Z=0
    g13: GeomPoint X=121 Y=33 Z=0
    g14: LineSegment StartX=119 StartY=35 StartZ=0 EndX=114 EndY=35 EndZ=0
    g15: ArcOfCircle CenterX=105 CenterY=19 CenterZ=0 NormalX=0 NormalY=0 NormalZ=1 AngleXU=0 Radius=19 StartAngle=5.7297 EndAngle=6.28319
    g16: ArcOfCircle CenterX=105 CenterY=19 CenterZ=0 NormalX=0 NormalY=0 NormalZ=1 AngleXU=0 Radius=16 StartAngle=5.60905 EndAngle=6.28319
    g17: LineSegment StartX=121 StartY=33 StartZ=0 EndX=121 EndY=19 EndZ=0
    g18: LineSegment StartX=124 StartY=38 StartZ=0 EndX=124 EndY=19 EndZ=0
    g19: LineSegment StartX=117.5 StartY=9.01251 StartZ=0 EndX=121.163 EndY=9.0125 EndZ=0
  constraints (46):
    c: Vertical(g0)
    c: Block(g0)
    c: Coincident(g1,g0)
    c: Block(g1)
    c: Coincident(g2,g1)
    c: Block(g2)
    c: Coincident(g3,g2)
    c: Horizontal(g3)
    c: Tangent(g3,g2)
    c: Coincident(g4,g0)
    c: Distance(g4) = 3
    c: Vertical(g4)
    c: Coincident(g5,g4)
    c: Horizontal(g5)
    c: Coincident(g6,g2)
    c: Coincident(g6,g5)
    c: Vertical(g6)
    c: Horizontal(g7)
    c: Distance(g7) = 105
    c: Coincident(g7,g1)
    c: Block(g3)
    c: Weight(g8) = 1
    c: Equal(g8,g9)
    c: Equal(g8,g10)
    c: InternalAlignment(g8,g11)
    c: InternalAlignment(g9,g11)
    c: InternalAlignment(g10,g11)
    c: InternalAlignment(g12,g11)
    c: InternalAlignment(g13,g11)
    c: Block(g11)
    c: Coincident(g14,g11)
    c: Coincident(g14,g3)
    c: Horizontal(g14)
    c: Block(g15)
    c: Coincident(g16,g15)
    c: Block(g16)
    c: Coincident(g17,g11)
    c: Coincident(g17,g16)
    c: Vertical(g17)
    c: Distance(g17) = 14
    c: Coincident(g18,g7)
    c: Coincident(g18,g15)
    c: Vertical(g18)
    c: Distance(g18) = 19
    c: Coincident(g19,g16)
    c: Coincident(g19,g15)
FEATURE [Sketcher::SketchObject] Sketch065
  FullyConstrained = true
  MapMode = 3
  Placement = pos=(0,0,0) rot=(1,0,0;1.5708rad)
  sketch-geometry (8):
    g0: Circle CenterX=80.351 CenterY=-67.6202 CenterZ=0 NormalX=0 NormalY=0 NormalZ=1 AngleXU=0 Radius=3
    g1: Circle CenterX=80.351 CenterY=-4.92017 CenterZ=0 NormalX=0 NormalY=0 NormalZ=1 AngleXU=0 Radius=3
    g2: Circle CenterX=23.851 CenterY=-4.92017 CenterZ=0 NormalX=0 NormalY=0 NormalZ=1 AngleXU=0 Radius=3
    g3: Circle CenterX=23.851 CenterY=-67.6202 CenterZ=0 NormalX=0 NormalY=0 NormalZ=1 AngleXU=0 Radius=3
    g4: Circle CenterX=23.851 CenterY=-67.6202 CenterZ=0 NormalX=0 NormalY=0 NormalZ=1 AngleXU=0 Radius=5
    g5: Circle CenterX=80.351 CenterY=-67.6202 CenterZ=0 NormalX=0 NormalY=0 NormalZ=1 AngleXU=0 Radius=5
    g6: Circle CenterX=23.851 CenterY=-4.92017 CenterZ=0 NormalX=0 NormalY=0 NormalZ=1 AngleXU=0 Radius=5
    g7: Circle CenterX=80.351 CenterY=-4.92017 CenterZ=0 NormalX=0 NormalY=0 NormalZ=1 AngleXU=0 Radius=5
  constraints (8):
    c: Block(g1)
    c: Block(g0)
    c: Block(g3)
    c: Block(g2)
    c: Block(g5)
    c: Block(g4)
    c: Block(g6)
    c: Block(g7)
FEATURE [Part::Extrusion] Extrude056
  Base = -> Sketch065
  Dir = (0,-1,2e-16)
  DirMode = 2
  FaceMakerClass = Part::FaceMakerBullseye
  LengthFwd = 2
  LengthRev = 0
  Solid = true
  Symmetric = false
FEATURE [Part::Extrusion] Extrude057  label="top025"
  Base = -> Sketch064
  Dir = (0,0,1)
  DirMode = 2
  FaceMakerClass = Part::FaceMakerBullseye
  LengthFwd = 72
  LengthRev = 0
  Solid = true
  Symmetric = false
FEATURE [Sketcher::SketchObject] Sketch066
  FullyConstrained = true
  MapMode = 3
  Placement = pos=(0,0,0) rot=(1,0,0;1.5708rad)
  Support = -> [Extrude057]
  sketch-geometry (8):
    g0: Circle CenterX=80.351 CenterY=-67.6202 CenterZ=0 NormalX=0 NormalY=0 NormalZ=1 AngleXU=0 Radius=3
    g1: Circle CenterX=80.351 CenterY=-4.92017 CenterZ=0 NormalX=0 NormalY=0 NormalZ=1 AngleXU=0 Radius=3
    g2: Circle CenterX=23.851 CenterY=-4.92017 CenterZ=0 NormalX=0 NormalY=0 NormalZ=1 AngleXU=0 Radius=3
    g3: Circle CenterX=23.851 CenterY=-67.6202 CenterZ=0 NormalX=0 NormalY=0 NormalZ=1 AngleXU=0 Radius=3
    g4: Circle CenterX=23.851 CenterY=-67.6202 CenterZ=0 NormalX=0 NormalY=0 NormalZ=1 AngleXU=0 Radius=5
    g5: Circle CenterX=80.351 CenterY=-67.6202 CenterZ=0 NormalX=0 NormalY=0 NormalZ=1 AngleXU=0 Radius=5
    g6: Circle CenterX=23.851 CenterY=-4.92017 CenterZ=0 NormalX=0 NormalY=0 NormalZ=1 AngleXU=0 Radius=5
    g7: Circle CenterX=80.351 CenterY=-4.92017 CenterZ=0 NormalX=0 NormalY=0 NormalZ=1 AngleXU=0 Radius=5
  constraints (8):
    c: Block(g1)
    c: Block(g0)
    c: Block(g3)
    c: Block(g2)
    c: Block(g5)
    c: Block(g4)
    c: Block(g6)
    c: Block(g7)
FEATURE [Part::Extrusion] Extrude055
  Base = -> Sketch066
  Dir = (0,-1,2e-16)
  DirMode = 2
  FaceMakerClass = Part::FaceMakerBullseye
  LengthFwd = 2
  LengthRev = 0
  Solid = true
  Symmetric = false
FEATURE [Part::Fillet] Fillet041
  Base = -> Extrude056
  Edges = 4 edges r=1.99: [Edge6,Edge12,Edge18,Edge24]
FEATURE [Part::Cut] Cut045
  Base = -> Extrude055
  Placement = pos=(0,6,0) rot=(0,0,1;0rad)
  Tool = -> Fillet041
FEATURE [Part::MultiFuse] Fusion095  label="pcbScrewPillars"
  Placement = pos=(-3.2,-1,72.3) rot=(0,0,1;0rad)
  Shapes = -> [Cut045,Extrude054]
FEATURE [Part::Feature] Face113
  shape: bbox 3.2 x 1.5 x 2e-07 mm, 1 faces, 0 solids (baked)
FEATURE [Part::Revolution] Revolve121  label="backCaseScrewRetainer002"
  Angle = 360
  Axis = (0,1,0)
  Base = (0,0,0)
  FaceMakerClass = Part::FaceMakerBullseye
  Placement = pos=(12.5,3,62) rot=(0,0,1;0rad)
  Solid = false
  Source = -> Face113
  Symmetric = false
FEATURE [Part::Feature] Face114
  shape: bbox 3.2 x 1.5 x 2e-07 mm, 1 faces, 0 solids (baked)
FEATURE [Part::Feature] Face115
  shape: bbox 3.2 x 1.5 x 2e-07 mm, 1 faces, 0 solids (baked)
FEATURE [Part::Feature] Face116
  shape: bbox 3.2 x 1.5 x 2e-07 mm, 1 faces, 0 solids (baked)
FEATURE [Part::Revolution] Revolve122  label="frontCaseScrewRetainer004"
  Angle = 360
  Axis = (0,1,0)
  Base = (0,0,0)
  FaceMakerClass = Part::FaceMakerBullseye
  Placement = pos=(89.5,3,68.5) rot=(0,0,1;0rad)
  Solid = false
  Source = -> Face115
  Symmetric = false
FEATURE [Part::Revolution] Revolve123  label="frontCaseScrewRetainer005"
  Angle = 360
  Axis = (0,1,0)
  Base = (0,0,0)
  FaceMakerClass = Part::FaceMakerBullseye
  Placement = pos=(89.5,3,3.5) rot=(0,0,1;0rad)
  Solid = false
  Source = -> Face116
  Symmetric = false
FEATURE [Part::Revolution] Revolve124  label="backCaseScrewRetainer003"
  Angle = 360
  Axis = (0,1,0)
  Base = (0,0,0)
  FaceMakerClass = Part::FaceMakerBullseye
  Placement = pos=(12.5,3,10) rot=(0,0,1;0rad)
  Solid = false
  Source = -> Face114
  Symmetric = false
FEATURE [Part::Feature] Face117
  shape: bbox 3.6 x 3.2 x 2e-07 mm, 1 faces, 0 solids (baked)
FEATURE [Part::Revolution] Revolve125  label="moreFrontCaseScrewRetainer004"
  Angle = 360
  Axis = (0,1,0)
  Base = (0,0,0)
  FaceMakerClass = Part::FaceMakerBullseye
  Placement = pos=(109.5,4.5,68.5) rot=(0,0,1;0rad)
  Solid = false
  Source = -> Face117
  Symmetric = false
FEATURE [Part::Feature] Face118
  shape: bbox 3.6 x 3.2 x 2e-07 mm, 1 faces, 0 solids (baked)
FEATURE [Part::Revolution] Revolve126  label="moreFrontCaseScrewRetainer005"
  Angle = 360
  Axis = (0,1,0)
  Base = (0,0,0)
  FaceMakerClass = Part::FaceMakerBullseye
  Placement = pos=(109.5,4.5,3.5) rot=(0,0,1;0rad)
  Solid = false
  Source = -> Face118
  Symmetric = false
FEATURE [Part::MultiFuse] Fusion096  label="screwRetainers001"
  Shapes = -> [Revolve126,Revolve125,Revolve124,Revolve123,Revolve122,Revolve121]
FEATURE [Part::Feature] Face119
  shape: bbox 10 x 16.5 x 2e-07 mm, 1 faces, 0 solids (baked)
FEATURE [Part::Revolution] Revolve130  label="plugHousing050"
  Angle = 360
  Axis = (0,1,0)
  Base = (0,0,0)
  FaceMakerClass = Part::FaceMakerBullseye
  Placement = pos=(0,0,36.15) rot=(0,0,1;0rad)
  Solid = false
  Source = -> Face119
  Symmetric = false
FEATURE [Part::Feature] Face120
  shape: bbox 10 x 16.5 x 2e-07 mm, 1 faces, 0 solids (baked)
FEATURE [Part::Feature] Face121
  shape: bbox 10 x 16.5 x 2e-07 mm, 1 faces, 0 solids (baked)
FEATURE [Part::Revolution] Revolve127  label="plugHousing047"
  Angle = 360
  Axis = (0,1,0)
  Base = (0,0,0)
  FaceMakerClass = Part::FaceMakerBullseye
  Placement = pos=(0,0,36.15) rot=(0,0,1;0rad)
  Solid = false
  Source = -> Face121
  Symmetric = false
FEATURE [Part::Feature] Face122
  shape: bbox 10 x 16.5 x 2e-07 mm, 1 faces, 0 solids (baked)
FEATURE [Part::Feature] Face123
  shape: bbox 10 x 16.5 x 2e-07 mm, 1 faces, 0 solids (baked)
FEATURE [Part::Revolution] Revolve128  label="plugHousing048"
  Angle = 360
  Axis = (0,1,0)
  Base = (0,0,0)
  FaceMakerClass = Part::FaceMakerBullseye
  Placement = pos=(0,0,36.15) rot=(0,0,1;0rad)
  Solid = false
  Source = -> Face123
  Symmetric = false
FEATURE [Part::MultiFuse] Fusion100  label="plugHousing054"
  Placement = pos=(0,0,0) rot=(0,0,1;1.5708rad)
  Shapes = -> [Revolve130,Revolve128]
FEATURE [Part::Feature] Face124
  shape: bbox 10 x 16.5 x 2e-07 mm, 1 faces, 0 solids (baked)
FEATURE [Part::Feature] Face125
  shape: bbox 10 x 16.5 x 2e-07 mm, 1 faces, 0 solids (baked)
FEATURE [Part::Revolution] Revolve129  label="plugHousing049"
  Angle = 360
  Axis = (0,1,0)
  Base = (0,0,0)
  FaceMakerClass = Part::FaceMakerBullseye
  Placement = pos=(0,0,36.15) rot=(0,0,1;0rad)
  Solid = false
  Source = -> Face125
  Symmetric = false
FEATURE [Part::Feature] Face126
  shape: bbox 10 x 16.5 x 2e-07 mm, 1 faces, 0 solids (baked)
FEATURE [Part::Revolution] Revolve131  label="plugHousing058"
  Angle = 360
  Axis = (0,1,0)
  Base = (0,0,0)
  FaceMakerClass = Part::FaceMakerBullseye
  Placement = pos=(0,0,36.15) rot=(0,0,1;0rad)
  Solid = false
  Source = -> Face120
  Symmetric = false
FEATURE [Part::MultiFuse] Fusion099  label="plugHousing053"
  Placement = pos=(0,0,0) rot=(0,0,1;1.5708rad)
  Shapes = -> [Revolve127,Revolve131]
FEATURE [Part::MultiFuse] Fusion102  label="plugHousing056"
  Placement = pos=(0,19,0) rot=(0,0,1;3.14159rad)
  Shapes = -> [Fusion100,Fusion099]
FEATURE [Part::Revolution] Revolve132  label="plugHousing059"
  Angle = 360
  Axis = (0,1,0)
  Base = (0,0,0)
  FaceMakerClass = Part::FaceMakerBullseye
  Placement = pos=(0,0,36.15) rot=(0,0,1;0rad)
  Solid = false
  Source = -> Face126
  Symmetric = false
FEATURE [Part::Revolution] Revolve133  label="plugHousing060"
  Angle = 360
  Axis = (0,1,0)
  Base = (0,0,0)
  FaceMakerClass = Part::FaceMakerBullseye
  Placement = pos=(0,0,36.15) rot=(0,0,1;0rad)
  Solid = false
  Source = -> Face122
  Symmetric = false
FEATURE [Part::MultiFuse] Fusion097  label="plugHousing051"
  Placement = pos=(0,0,0) rot=(0,0,1;1.5708rad)
  Shapes = -> [Revolve133,Revolve132]
FEATURE [Part::Revolution] Revolve134  label="plugHousing061"
  Angle = 360
  Axis = (0,1,0)
  Base = (0,0,0)
  FaceMakerClass = Part::FaceMakerBullseye
  Placement = pos=(0,0,36.15) rot=(0,0,1;0rad)
  Solid = false
  Source = -> Face124
  Symmetric = false
FEATURE [Part::MultiFuse] Fusion101  label="plugHousing055"
  Placement = pos=(0,0,0) rot=(0,0,1;1.5708rad)
  Shapes = -> [Revolve129,Revolve134]
FEATURE [Part::MultiFuse] Fusion098  label="plugHousing052"
  Placement = pos=(0,19,0) rot=(0,0,1;3.14159rad)
  Shapes = -> [Fusion097,Fusion101]
FEATURE [Part::MultiFuse] Fusion103  label="plugHousing057"
  Placement = pos=(122.621,0,-0.15) rot=(0,0,1;0rad)
  Shapes = -> [Fusion102,Fusion098]
FEATURE [Part::Box] Box028  label="Cube015"
  AttacherType = Attacher::AttachEngine3D
  Height = 28
  Length = 3
  Placement = pos=(110.7,19,22) rot=(0,0,1;0rad)
  Width = 15.7
FEATURE [Part::Cylinder] Cylinder044
  Angle = 360
  AttacherType = Attacher::AttachEngine3D
  Height = 20
  Placement = pos=(0,0,36.15) rot=(0,0,1;0rad)
  Radius = 10.3
FEATURE [Part::Cylinder] Cylinder045
  Angle = 360
  AttacherType = Attacher::AttachEngine3D
  Height = 10
  Placement = pos=(0,0,36.15) rot=(0,0,1;0rad)
  Radius = 4
FEATURE [Part::MultiFuse] Fusion104  label="removeToCreteHoleForPlugHousing040"
  Placement = pos=(70,19,36) rot=(0,1,0;1.5708rad)
  Shapes = -> [Cylinder044,Cylinder045]
FEATURE [Part::Cut] Cut046  label="plugHousingTab003"
  Base = -> Box028
  Tool = -> Fusion104
FEATURE [Part::MultiFuse] Fusion105  label="plugHousing062"
  Shapes = -> [Fusion103,Cut046]
FEATURE [Part::Fillet] Fillet042
  Base = -> Fusion105
  Edges = 1 edges r=2: [Edge25]
FEATURE [Part::Fillet] Fillet043  label="plugHousing063"
  Base = -> Fillet042
  Edges = 1 edges r=2: [Edge8]
  Placement = pos=(7,0,0) rot=(0,0,1;0rad)
FEATURE [Part::Feature] Face127
  shape: bbox 10 x 16.5 x 2e-07 mm, 1 faces, 0 solids (baked)
FEATURE [Part::Feature] Face128
  shape: bbox 10 x 16.5 x 2e-07 mm, 1 faces, 0 solids (baked)
FEATURE [Part::Revolution] Revolve137  label="plugHousing070"
  Angle = 360
  Axis = (0,1,0)
  Base = (0,0,0)
  FaceMakerClass = Part::FaceMakerBullseye
  Placement = pos=(0,0,36.15) rot=(0,0,1;0rad)
  Solid = false
  Source = -> Face127
  Symmetric = false
FEATURE [Part::Revolution] Revolve140  label="plugHousing073"
  Angle = 360
  Axis = (0,1,0)
  Base = (0,0,0)
  FaceMakerClass = Part::FaceMakerBullseye
  Placement = pos=(0,0,36.15) rot=(0,0,1;0rad)
  Solid = false
  Source = -> Face128
  Symmetric = false
FEATURE [Part::Feature] Face129
  shape: bbox 10 x 16.5 x 2e-07 mm, 1 faces, 0 solids (baked)
FEATURE [Part::Revolution] Revolve138  label="plugHousing071"
  Angle = 360
  Axis = (0,1,0)
  Base = (0,0,0)
  FaceMakerClass = Part::FaceMakerBullseye
  Placement = pos=(0,0,36.15) rot=(0,0,1;0rad)
  Solid = false
  Source = -> Face129
  Symmetric = false
FEATURE [Part::Feature] Face130
  shape: bbox 10 x 16.5 x 2e-07 mm, 1 faces, 0 solids (baked)
FEATURE [Part::Revolution] Revolve139  label="plugHousing072"
  Angle = 360
  Axis = (0,1,0)
  Base = (0,0,0)
  FaceMakerClass = Part::FaceMakerBullseye
  Placement = pos=(0,0,36.15) rot=(0,0,1;0rad)
  Solid = false
  Source = -> Face130
  Symmetric = false
FEATURE [Part::Feature] Face131
  shape: bbox 10 x 16.5 x 2e-07 mm, 1 faces, 0 solids (baked)
FEATURE [Part::Revolution] Revolve135  label="plugHousing068"
  Angle = 360
  Axis = (0,1,0)
  Base = (0,0,0)
  FaceMakerClass = Part::FaceMakerBullseye
  Placement = pos=(0,0,36.15) rot=(0,0,1;0rad)
  Solid = false
  Source = -> Face131
  Symmetric = false
FEATURE [Part::MultiFuse] Fusion112  label="plugHousing078"
  Placement = pos=(0,0,0) rot=(0,0,1;1.5708rad)
  Shapes = -> [Revolve135,Revolve139]
FEATURE [Part::Feature] Face132
  shape: bbox 10 x 16.5 x 2e-07 mm, 1 faces, 0 solids (baked)
FEATURE [Part::Revolution] Revolve141  label="plugHousing074"
  Angle = 360
  Axis = (0,1,0)
  Base = (0,0,0)
  FaceMakerClass = Part::FaceMakerBullseye
  Placement = pos=(0,0,36.15) rot=(0,0,1;0rad)
  Solid = false
  Source = -> Face132
  Symmetric = false
FEATURE [Part::MultiFuse] Fusion110  label="plugHousing076"
  Placement = pos=(0,0,0) rot=(0,0,1;1.5708rad)
  Shapes = -> [Revolve141,Revolve140]
FEATURE [Part::Feature] Face133
  shape: bbox 10 x 16.5 x 2e-07 mm, 1 faces, 0 solids (baked)
FEATURE [Part::Revolution] Revolve136  label="plugHousing069"
  Angle = 360
  Axis = (0,1,0)
  Base = (0,0,0)
  FaceMakerClass = Part::FaceMakerBullseye
  Placement = pos=(0,0,36.15) rot=(0,0,1;0rad)
  Solid = false
  Source = -> Face133
  Symmetric = false
FEATURE [Part::MultiFuse] Fusion106  label="plugHousing064"
  Placement = pos=(0,0,0) rot=(0,0,1;1.5708rad)
  Shapes = -> [Revolve138,Revolve136]
FEATURE [Part::MultiFuse] Fusion108  label="plugHousing066"
  Placement = pos=(0,19,0) rot=(0,0,1;3.14159rad)
  Shapes = -> [Fusion106,Fusion112]
FEATURE [Part::Feature] Face134
  shape: bbox 10 x 16.5 x 2e-07 mm, 1 faces, 0 solids (baked)
FEATURE [Part::Revolution] Revolve142  label="plugHousing075"
  Angle = 360
  Axis = (0,1,0)
  Base = (0,0,0)
  FaceMakerClass = Part::FaceMakerBullseye
  Placement = pos=(0,0,36.15) rot=(0,0,1;0rad)
  Solid = false
  Source = -> Face134
  Symmetric = false
FEATURE [Part::MultiFuse] Fusion107  label="plugHousing065"
  Placement = pos=(0,0,0) rot=(0,0,1;1.5708rad)
  Shapes = -> [Revolve137,Revolve142]
FEATURE [Part::MultiFuse] Fusion111  label="plugHousing077"
  Placement = pos=(0,19,0) rot=(0,0,1;3.14159rad)
  Shapes = -> [Fusion110,Fusion107]
FEATURE [Part::MultiFuse] Fusion109  label="plugHousing067"
  Placement = pos=(131.236,0,-0.15) rot=(0,0,1;0rad)
  Shapes = -> [Fusion108,Fusion111]
FEATURE [Part::MultiFuse] Fusion113  label="plugHousing079"
  Shapes = -> [Fillet043,Fusion109]
FEATURE [Part::Feature] Face135
  shape: bbox 3.5 x 17.8 x 2e-07 mm, 1 faces, 0 solids (baked)
FEATURE [Part::Revolution] Revolve143  label="removeToCreateScrewAndThreadedInsertHole049"
  Angle = 360
  Axis = (0,1,0)
  Base = (0,0,0)
  FaceMakerClass = Part::FaceMakerBullseye
  Placement = pos=(12.5,0,10) rot=(0,0,1;0rad)
  Solid = false
  Source = -> Face135
  Symmetric = false
FEATURE [Part::Feature] Face136
  shape: bbox 3.5 x 17.8 x 2e-07 mm, 1 faces, 0 solids (baked)
FEATURE [Part::Revolution] Revolve144  label="removeToCreateScrewAndThreadedInsertHole050"
  Angle = 360
  Axis = (0,1,0)
  Base = (0,0,0)
  FaceMakerClass = Part::FaceMakerBullseye
  Placement = pos=(12.5,0,62) rot=(0,0,1;0rad)
  Solid = false
  Source = -> Face136
  Symmetric = false
FEATURE [Part::Feature] Face137
  shape: bbox 3.5 x 17.8 x 2e-07 mm, 1 faces, 0 solids (baked)
FEATURE [Part::Revolution] Revolve145  label="removeToCreateScrewAndThreadedInsertHole051"
  Angle = 360
  Axis = (0,1,0)
  Base = (0,0,0)
  FaceMakerClass = Part::FaceMakerBullseye
  Placement = pos=(89.5,0,68.5) rot=(0,0,1;0rad)
  Solid = false
  Source = -> Face137
  Symmetric = false
FEATURE [Part::Feature] Face138
  shape: bbox 3.5 x 17.8 x 2e-07 mm, 1 faces, 0 solids (baked)
FEATURE [Part::Revolution] Revolve146  label="removeToCreateScrewAndThreadedInsertHole052"
  Angle = 360
  Axis = (0,1,0)
  Base = (0,0,0)
  FaceMakerClass = Part::FaceMakerBullseye
  Placement = pos=(89.5,0,3.5) rot=(0,0,1;0rad)
  Solid = false
  Source = -> Face138
  Symmetric = false
FEATURE [Part::Feature] Face139
  shape: bbox 3.5 x 17.8 x 2e-07 mm, 1 faces, 0 solids (baked)
FEATURE [Part::Revolution] Revolve147  label="removeToCreateScrewAndThreadedInsertHole053"
  Angle = 360
  Axis = (0,1,0)
  Base = (0,0,0)
  FaceMakerClass = Part::FaceMakerBullseye
  Placement = pos=(109.5,4.7,3.5) rot=(0,0,1;0rad)
  Solid = false
  Source = -> Face139
  Symmetric = false
FEATURE [Part::Feature] Face140
  shape: bbox 3.5 x 17.8 x 2e-07 mm, 1 faces, 0 solids (baked)
FEATURE [Part::Revolution] Revolve148  label="removeToCreateScrewAndThreadedInsertHole054"
  Angle = 360
  Axis = (0,1,0)
  Base = (0,0,0)
  FaceMakerClass = Part::FaceMakerBullseye
  Placement = pos=(109.5,4.7,68.5) rot=(0,0,1;0rad)
  Solid = false
  Source = -> Face140
  Symmetric = false
FEATURE [Part::MultiFuse] Fusion114  label="removeToCreateScrewAndThreadedInsertHole055"
  Shapes = -> [Revolve148,Revolve147,Revolve146,Revolve145,Revolve144,Revolve143]
FEATURE [Part::Cut] Cut047  label="casePillars004"
  Base = -> Cut037
  Tool = -> Fusion114
FEATURE [Part::Feature] Face141
  shape: bbox 3.5 x 17.8 x 2e-07 mm, 1 faces, 0 solids (baked)
FEATURE [Part::Feature] Face142
  shape: bbox 3.5 x 17.8 x 2e-07 mm, 1 faces, 0 solids (baked)
FEATURE [Part::Feature] Face143
  shape: bbox 3.5 x 17.8 x 2e-07 mm, 1 faces, 0 solids (baked)
FEATURE [Part::Revolution] Revolve149  label="removeToCreateScrewAndThreadedInsertHole057"
  Angle = 360
  Axis = (0,1,0)
  Base = (0,0,0)
  FaceMakerClass = Part::FaceMakerBullseye
  Placement = pos=(12.5,0,10) rot=(0,0,1;0rad)
  Solid = false
  Source = -> Face141
  Symmetric = false
FEATURE [Part::Feature] Face144
  shape: bbox 3.5 x 17.8 x 2e-07 mm, 1 faces, 0 solids (baked)
FEATURE [Part::Feature] Face145
  shape: bbox 3.5 x 17.8 x 2e-07 mm, 1 faces, 0 solids (baked)
FEATURE [Part::Feature] Face146
  shape: bbox 3.5 x 17.8 x 2e-07 mm, 1 faces, 0 solids (baked)
FEATURE [Part::Revolution] Revolve150  label="removeToCreateScrewAndThreadedInsertHole058"
  Angle = 360
  Axis = (0,1,0)
  Base = (0,0,0)
  FaceMakerClass = Part::FaceMakerBullseye
  Placement = pos=(12.5,0,62) rot=(0,0,1;0rad)
  Solid = false
  Source = -> Face146
  Symmetric = false
FEATURE [Part::Revolution] Revolve151  label="removeToCreateScrewAndThreadedInsertHole059"
  Angle = 360
  Axis = (0,1,0)
  Base = (0,0,0)
  FaceMakerClass = Part::FaceMakerBullseye
  Placement = pos=(89.5,0,68.5) rot=(0,0,1;0rad)
  Solid = false
  Source = -> Face143
  Symmetric = false
FEATURE [Part::Revolution] Revolve152  label="removeToCreateScrewAndThreadedInsertHole060"
  Angle = 360
  Axis = (0,1,0)
  Base = (0,0,0)
  FaceMakerClass = Part::FaceMakerBullseye
  Placement = pos=(89.5,0,3.5) rot=(0,0,1;0rad)
  Solid = false
  Source = -> Face142
  Symmetric = false
FEATURE [Part::Revolution] Revolve153  label="removeToCreateScrewAndThreadedInsertHole061"
  Angle = 360
  Axis = (0,1,0)
  Base = (0,0,0)
  FaceMakerClass = Part::FaceMakerBullseye
  Placement = pos=(109.5,4.7,3.5) rot=(0,0,1;0rad)
  Solid = false
  Source = -> Face145
  Symmetric = false
FEATURE [Part::Revolution] Revolve154  label="removeToCreateScrewAndThreadedInsertHole062"
  Angle = 360
  Axis = (0,1,0)
  Base = (0,0,0)
  FaceMakerClass = Part::FaceMakerBullseye
  Placement = pos=(109.5,4.7,68.5) rot=(0,0,1;0rad)
  Solid = false
  Source = -> Face144
  Symmetric = false
FEATURE [Part::MultiFuse] Fusion115  label="removeToCreateScrewAndThreadedInsertHole056"
  Shapes = -> [Revolve154,Revolve153,Revolve152,Revolve151,Revolve150,Revolve149]
FEATURE [Part::Feature] Face147
  shape: bbox 9.8 x 26.5 x 2e-07 mm, 1 faces, 0 solids (baked)
FEATURE [Part::Revolution] Revolve155
  Angle = 360
  Axis = (0,1,0)
  Base = (0,0,0)
  FaceMakerClass = Part::FaceMakerBullseye
  Placement = pos=(0,0,0) rot=(0,0,1;1.5708rad)
  Solid = false
  Source = -> Face147
  Symmetric = false
FEATURE [Part::Feature] Face148
  shape: bbox 9.8 x 26.5 x 2e-07 mm, 1 faces, 0 solids (baked)
FEATURE [Part::Revolution] Revolve156
  Angle = 360
  Axis = (0,1,0)
  Base = (0,0,0)
  FaceMakerClass = Part::FaceMakerBullseye
  Placement = pos=(0,0,0) rot=(0,0,1;1.5708rad)
  Solid = false
  Source = -> Face148
  Symmetric = false
FEATURE [Part::MultiFuse] Fusion116
  Placement = pos=(-18,19,36) rot=(0,0,1;0rad)
  Shapes = -> [Revolve156,Revolve155]
FEATURE [Part::Box] Box029  label="Cube016"
  AttacherType = Attacher::AttachEngine3D
  Height = 28
  Length = 3
  Placement = pos=(110.7,19,22) rot=(0,0,1;0rad)
  Width = 15.7
FEATURE [Part::Cylinder] Cylinder046
  Angle = 360
  AttacherType = Attacher::AttachEngine3D
  Height = 10
  Placement = pos=(0,0,36.15) rot=(0,0,1;0rad)
  Radius = 4
FEATURE [Part::Cylinder] Cylinder047
  Angle = 360
  AttacherType = Attacher::AttachEngine3D
  Height = 20
  Placement = pos=(0,0,36.15) rot=(0,0,1;0rad)
  Radius = 10.3
FEATURE [Part::MultiFuse] Fusion117  label="removeToCreteHoleForPlugHousing041"
  Placement = pos=(70,19,36) rot=(0,1,0;1.5708rad)
  Shapes = -> [Cylinder047,Cylinder046]
FEATURE [Part::Cut] Cut049  label="plugHousingTab004"
  Base = -> Box029
  Placement = pos=(-107.4,-14,0) rot=(0,0,1;0rad)
  Tool = -> Fusion117
FEATURE [Part::Box] Box030  label="Cube017"
  AttacherType = Attacher::AttachEngine3D
  Height = 28
  Length = 3
  Placement = pos=(110.7,19,22) rot=(0,0,1;0rad)
  Width = 15.7
FEATURE [Part::Cylinder] Cylinder048
  Angle = 360
  AttacherType = Attacher::AttachEngine3D
  Height = 10
  Placement = pos=(0,0,36.15) rot=(0,0,1;0rad)
  Radius = 4
FEATURE [Part::Cylinder] Cylinder049
  Angle = 360
  AttacherType = Attacher::AttachEngine3D
  Height = 20
  Placement = pos=(0,0,36.15) rot=(0,0,1;0rad)
  Radius = 10.3
FEATURE [Part::MultiFuse] Fusion118  label="removeToCreteHoleForPlugHousing042"
  Placement = pos=(70,19,36) rot=(0,1,0;1.5708rad)
  Shapes = -> [Cylinder049,Cylinder048]
FEATURE [Part::Cut] Cut050  label="plugHousingTab005"
  Base = -> Box030
  Placement = pos=(-107.4,-14,0) rot=(0,0,1;0rad)
  Tool = -> Fusion118
FEATURE [Part::MultiFuse] Fusion119
  Placement = pos=(9.6,23,0) rot=(0,0,1;3.14159rad)
  Shapes = -> [Cut049,Cut050]
FEATURE [Part::Box] Box031  label="Cube018"
  AttacherType = Attacher::AttachEngine3D
  Height = 10
  Length = 3
  Placement = pos=(3.3,4,12) rot=(0,0,1;0rad)
  Width = 10
FEATURE [Part::Fillet] Fillet044
  Base = -> Box031
  Edges = 1 edges r=2: [Edge11]
FEATURE [Part::Box] Box032  label="Cube019"
  AttacherType = Attacher::AttachEngine3D
  Height = 10
  Length = 3
  Placement = pos=(3.3,4,50) rot=(0,0,1;0rad)
  Width = 10
FEATURE [Part::Fillet] Fillet045
  Base = -> Box032
  Edges = 1 edges r=2: [Edge12]
FEATURE [Part::Box] Box033  label="Cube020"
  AttacherType = Attacher::AttachEngine3D
  Height = 28
  Length = 4
  Placement = pos=(5,0,22) rot=(0,0,1;0rad)
  Width = 10
FEATURE [Part::Fillet] Fillet046
  Base = -> Box033
  Edges = 1 edges r=1: [Edge7]
FEATURE [Part::Fillet] Fillet047
  Base = -> Fillet046
  Edges = 1 edges r=2: [Edge5]
FEATURE [Part::Fillet] Fillet048
  Base = -> Fillet047
  Edges = 1 edges r=2: [Edge2]
FEATURE [Part::Cylinder] Cylinder050
  Angle = 360
  AttacherType = Attacher::AttachEngine3D
  Height = 20
  Placement = pos=(0,0,36.15) rot=(0,0,1;0rad)
  Radius = 8.2
FEATURE [Part::Cylinder] Cylinder051
  Angle = 360
  AttacherType = Attacher::AttachEngine3D
  Height = 10
  Placement = pos=(0,0,36.15) rot=(0,0,1;0rad)
  Radius = 4
FEATURE [Part::MultiFuse] Fusion120  label="removeToCreteHoleForPlugHousing043"
  Placement = pos=(-42,19,36) rot=(0,1,0;1.5708rad)
  Shapes = -> [Cylinder050,Cylinder051]
FEATURE [Sketcher::SketchObject] Sketch067  label="topSketch018"
  FullyConstrained = true
  sketch-geometry (4):
    g0: LineSegment StartX=16.8446 StartY=31.512 StartZ=0 EndX=16.3251 EndY=34.4666 EndZ=0
    g1: ArcOfCircle CenterX=19 CenterY=19.2524 CenterZ=0 NormalX=0 NormalY=0 NormalZ=1 AngleXU=0 Radius=15.4476 StartAngle=1.74483 EndAngle=2.72717
    g2: ArcOfCircle CenterX=19 CenterY=19.2524 CenterZ=0 NormalX=0 NormalY=0 NormalZ=1 AngleXU=0 Radius=12.4476 StartAngle=1.74483 EndAngle=2.73189
    g3: LineSegment StartX=4.86004 StartY=25.4725 StartZ=0 EndX=7.58253 EndY=24.2107 EndZ=0
  constraints (7):
    c: Block(g0)
    c: Coincident(g1,g0)
    c: Coincident(g2,g0)
    c: Coincident(g3,g1)
    c: Coincident(g3,g2)
    c: Block(g1)
    c: Block(g2)
FEATURE [Part::Extrusion] Extrude058
  Base = -> Sketch067
  Dir = (0,0,1)
  DirMode = 2
  FaceMakerClass = Part::FaceMakerBullseye
  LengthFwd = 10
  LengthRev = 0
  Placement = pos=(0,0,31) rot=(0,0,1;0rad)
  Solid = true
  Symmetric = false
FEATURE [Part::Cut] Cut051
  Base = -> Extrude058
  Tool = -> Fusion120
FEATURE [Part::Fillet] Fillet049
  Base = -> Cut051
  Edges = 1 edges r=2: [Edge1]
FEATURE [Part::Fillet] Fillet050
  Base = -> Fillet049
  Edges = 1 edges r=2.5: [Edge1]
FEATURE [Part::Fillet] Fillet051
  Base = -> Fillet050
  Edges = 1 edges r=2.5: [Edge2]
FEATURE [Part::MultiFuse] Fusion121  label="wireHolder003"
  Shapes = -> [Fusion116,Fillet051]
FEATURE [Part::MultiFuse] Fusion122
  Shapes = -> [Fillet045,Fusion121]
FEATURE [Part::MultiFuse] Fusion123  label="wireHolder004"
  Shapes = -> [Fusion122,Fillet048]
FEATURE [Part::MultiFuse] Fusion124  label="wireHolder005"
  Shapes = -> [Fillet044,Fusion119,Fusion123]
FEATURE [Sketcher::SketchObject] Sketch068  label="topSketch019"
  FullyConstrained = true
  sketch-geometry (6):
    g0: LineSegment StartX=19 StartY=38 StartZ=0 EndX=117 EndY=38 EndZ=0
    g1: ArcOfCircle CenterX=19 CenterY=19 CenterZ=0 NormalX=0 NormalY=0 NormalZ=1 AngleXU=0 Radius=19 StartAngle=1.5708 EndAngle=3.14159
    g2: LineSegment StartX=117 StartY=38 StartZ=0 EndX=117 EndY=19 EndZ=0
    g3: LineSegment StartX=98 StartY=1.0161e-12 StartZ=0 EndX=5.22862e-06 EndY=1.0161e-12 EndZ=0
    g4: LineSegment StartX=5.22862e-06 StartY=19 StartZ=0 EndX=5.22862e-06 EndY=1.0161e-12 EndZ=0
    g5: ArcOfCircle CenterX=98 CenterY=19 CenterZ=0 NormalX=0 NormalY=0 NormalZ=1 AngleXU=0 Radius=19 StartAngle=4.71239 EndAngle=6.28319
  constraints (16):
    c: Horizontal(g0)
    c: Distance(g0) = 98
    c: Coincident(g1,g0)
    c: Block(g1)
    c: Coincident(g2,g0)
    c: Vertical(g2)
    c: Distance(g2) = 19
    c: Horizontal(g3)
    c: Coincident(g4,g1)
    c: Vertical(g4)
    c: Coincident(g3,g4)
    c: Block(g3)
    c: Coincident(g5,g2)
    c: Coincident(g5,g3)
    c: Block(g0)
    c: Block(g5)
FEATURE [Part::Extrusion] Extrude059  label="sideA002"
  Base = -> Sketch068
  Dir = (0,0,1)
  DirMode = 2
  FaceMakerClass = Part::FaceMakerBullseye
  LengthFwd = 3
  LengthRev = 0
  Placement = pos=(0,0,-2.7) rot=(0,0,1;0rad)
  Solid = true
  Symmetric = false
FEATURE [Sketcher::SketchObject] Sketch069  label="topSketch020"
  FullyConstrained = true
  sketch-geometry (6):
    g0: LineSegment StartX=19 StartY=38 StartZ=0 EndX=117 EndY=38 EndZ=0
    g1: ArcOfCircle CenterX=19 CenterY=19 CenterZ=0 NormalX=0 NormalY=0 NormalZ=1 AngleXU=0 Radius=19 StartAngle=1.5708 EndAngle=3.14159
    g2: LineSegment StartX=117 StartY=38 StartZ=0 EndX=117 EndY=19 EndZ=0
    g3: LineSegment StartX=98 StartY=1.0161e-12 StartZ=0 EndX=5.22862e-06 EndY=1.0161e-12 EndZ=0
    g4: LineSegment StartX=5.22862e-06 StartY=19 StartZ=0 EndX=5.22862e-06 EndY=1.0161e-12 EndZ=0
    g5: ArcOfCircle CenterX=98 CenterY=19 CenterZ=0 NormalX=0 NormalY=0 NormalZ=1 AngleXU=0 Radius=19 StartAngle=4.71239 EndAngle=6.28319
  constraints (16):
    c: Horizontal(g0)
    c: Distance(g0) = 98
    c: Coincident(g1,g0)
    c: Block(g1)
    c: Coincident(g2,g0)
    c: Vertical(g2)
    c: Distance(g2) = 19
    c: Horizontal(g3)
    c: Coincident(g4,g1)
    c: Vertical(g4)
    c: Coincident(g3,g4)
    c: Block(g3)
    c: Coincident(g5,g2)
    c: Coincident(g5,g3)
    c: Block(g0)
    c: Block(g5)
FEATURE [Part::Extrusion] Extrude060  label="sideB002"
  Base = -> Sketch069
  Dir = (0,0,1)
  DirMode = 2
  FaceMakerClass = Part::FaceMakerBullseye
  LengthFwd = 3
  LengthRev = 0
  Placement = pos=(0,0,71.7) rot=(0,0,1;0rad)
  Solid = true
  Symmetric = false
FEATURE [Part::MultiFuse] Fusion127  label="removeFromBottom001"
  Placement = pos=(2,0,0) rot=(0,0,1;0rad)
  Shapes = -> [Extrude059,Extrude060]
FEATURE [Part::Cylinder] Cylinder052
  Angle = 360
  AttacherType = Attacher::AttachEngine3D
  Height = 20
  Placement = pos=(0,0,36.15) rot=(0,0,1;0rad)
  Radius = 14
FEATURE [Part::Cylinder] Cylinder053
  Angle = 360
  AttacherType = Attacher::AttachEngine3D
  Height = 10
  Placement = pos=(0,0,36.15) rot=(0,0,1;0rad)
  Radius = 4
FEATURE [Part::MultiFuse] Fusion128  label="removeToCreteHoleForPlugHousing044"
  Placement = pos=(70,19,36) rot=(0,1,0;1.5708rad)
  Shapes = -> [Cylinder052,Cylinder053]
FEATURE [Part::Cut] Cut052  label="bottom011"
  Base = -> Extrude043
  Tool = -> Fusion128
FEATURE [Part::Cut] Cut054  label="bottom012"
  Base = -> Cut052
  Tool = -> Fusion115
FEATURE [Sketcher::SketchObject] Sketch070
  FullyConstrained = true
  Placement = pos=(117,19,0) rot=(0.57735,0.57735,0.57735;2.0944rad)
  sketch-geometry (48):
    g0: LineSegment StartX=-49.19 StartY=69.25 StartZ=0 EndX=-49.19 EndY=66.25 EndZ=0
    g1: LineSegment StartX=-49.19 StartY=63.5 StartZ=0 EndX=-49.19 EndY=60.5 EndZ=0
    g2: LineSegment StartX=-49.19 StartY=57.75 StartZ=0 EndX=-49.19 EndY=54.75 EndZ=0
    g3: LineSegment StartX=-49.19 StartY=52 StartZ=0 EndX=-49.19 EndY=49 EndZ=0
    g4: LineSegment StartX=-49.19 StartY=46.25 StartZ=0 EndX=-49.19 EndY=43.25 EndZ=0
    g5: LineSegment StartX=-49.19 StartY=40.5 StartZ=0 EndX=-49.19 EndY=37.5 EndZ=0
    g6: LineSegment StartX=-49.19 StartY=34.5 StartZ=0 EndX=-49.19 EndY=31.5 EndZ=0
    g7: LineSegment StartX=-49.19 StartY=28.75 StartZ=0 EndX=-49.19 EndY=25.75 EndZ=0
    g8: LineSegment StartX=-49.19 StartY=23 StartZ=0 EndX=-49.19 EndY=20 EndZ=0
    g9: LineSegment StartX=-49.19 StartY=17.25 StartZ=0 EndX=-49.19 EndY=14.25 EndZ=0
    g10: LineSegment StartX=-49.19 StartY=11.5 StartZ=0 EndX=-49.19 EndY=8.5 EndZ=0
    g11: LineSegment StartX=-49.19 StartY=5.75 StartZ=0 EndX=-49.19 EndY=2.75 EndZ=0
    g12: ArcOfCircle CenterX=-1.5 CenterY=67.75 CenterZ=0 NormalX=0 NormalY=0 NormalZ=1 AngleXU=0 Radius=1.5 StartAngle=4.71239 EndAngle=7.85398
    g13: ArcOfCircle CenterX=-1.5 CenterY=62 CenterZ=0 NormalX=0 NormalY=0 NormalZ=1 AngleXU=0 Radius=1.5 StartAngle=4.71239 EndAngle=7.85398
    g14: ArcOfCircle CenterX=-1.5 CenterY=56.25 CenterZ=0 NormalX=0 NormalY=0 NormalZ=1 AngleXU=0 Radius=1.5 StartAngle=4.71239 EndAngle=7.85398
    g15: ArcOfCircle CenterX=-11.49 CenterY=50.5 CenterZ=0 NormalX=0 NormalY=0 NormalZ=1 AngleXU=0 Radius=1.5 StartAngle=4.71239 EndAngle=7.85398
    g16: ArcOfCircle CenterX=-16.28 CenterY=44.75 CenterZ=0 NormalX=0 NormalY=0 NormalZ=1 AngleXU=0 Radius=1.5 StartAngle=4.71239 EndAngle=7.85398
    g17: ArcOfCircle CenterX=-18.2337 CenterY=39 CenterZ=0 NormalX=0 NormalY=0 NormalZ=1 AngleXU=0 Radius=1.5 StartAngle=4.71485 EndAngle=7.85398
    g18: ArcOfCircle CenterX=-16.2837 CenterY=27.25 CenterZ=0 NormalX=0 NormalY=0 NormalZ=1 AngleXU=0 Radius=1.5 StartAngle=4.71485 EndAngle=7.85398
    g19: ArcOfCircle CenterX=-18.2337 CenterY=33 CenterZ=0 NormalX=0 NormalY=0 NormalZ=1 AngleXU=0 Radius=1.5 StartAngle=4.71485 EndAngle=7.85398
    g20: ArcOfCircle CenterX=-11.49 CenterY=21.5 CenterZ=0 NormalX=0 NormalY=0 NormalZ=1 AngleXU=0 Radius=1.5 StartAngle=4.71239 EndAngle=7.85398
    g21: ArcOfCircle CenterX=-1.5 CenterY=4.25 CenterZ=0 NormalX=0 NormalY=0 NormalZ=1 AngleXU=0 Radius=1.5 StartAngle=4.71239 EndAngle=7.85398
    g22: ArcOfCircle CenterX=-1.5 CenterY=10 CenterZ=0 NormalX=0 NormalY=0 NormalZ=1 AngleXU=0 Radius=1.5 StartAngle=4.71239 EndAngle=7.85398
    g23: ArcOfCircle CenterX=-1.5 CenterY=15.75 CenterZ=0 NormalX=0 NormalY=0 NormalZ=1 AngleXU=0 Radius=1.5 StartAngle=4.71239 EndAngle=7.85398
    g24: LineSegment StartX=-49.19 StartY=69.25 StartZ=0 EndX=-1.5 EndY=69.25 EndZ=0
    g25: LineSegment StartX=-49.19 StartY=66.25 StartZ=0 EndX=-1.5 EndY=66.25 EndZ=0
    g26: LineSegment StartX=-49.19 StartY=63.5 StartZ=0 EndX=-1.5 EndY=63.5 EndZ=0
    g27: LineSegment StartX=-49.19 StartY=60.5 StartZ=0 EndX=-1.5 EndY=60.5 EndZ=0
    g28: LineSegment StartX=-49.19 StartY=57.75 StartZ=0 EndX=-1.5 EndY=57.75 EndZ=0
    g29: LineSegment StartX=-49.19 StartY=54.75 StartZ=0 EndX=-1.5 EndY=54.75 EndZ=0
    g30: LineSegment StartX=-49.19 StartY=52 StartZ=0 EndX=-11.49 EndY=52 EndZ=0
    g31: LineSegment StartX=-49.19 StartY=49 StartZ=0 EndX=-11.49 EndY=49 EndZ=0
    g32: LineSegment StartX=-49.19 StartY=46.25 StartZ=0 EndX=-16.28 EndY=46.25 EndZ=0
    g33: LineSegment StartX=-49.19 StartY=43.25 StartZ=0 EndX=-16.28 EndY=43.25 EndZ=0
    g34: LineSegment StartX=-49.19 StartY=40.5 StartZ=0 EndX=-18.2337 EndY=40.5 EndZ=0
    g35: LineSegment StartX=-49.19 StartY=37.5 StartZ=0 EndX=-18.23 EndY=37.5 EndZ=0
    g36: LineSegment StartX=-49.19 StartY=34.5 StartZ=0 EndX=-18.2337 EndY=34.5 EndZ=0
    g37: LineSegment StartX=-49.19 StartY=31.5 StartZ=0 EndX=-18.23 EndY=31.5 EndZ=0
    g38: LineSegment StartX=-49.19 StartY=28.75 StartZ=0 EndX=-16.2837 EndY=28.75 EndZ=0
    g39: LineSegment StartX=-49.19 StartY=25.75 StartZ=0 EndX=-16.28 EndY=25.75 EndZ=0
    g40: LineSegment StartX=-49.19 StartY=23 StartZ=0 EndX=-11.49 EndY=23 EndZ=0
    g41: LineSegment StartX=-49.19 StartY=20 StartZ=0 EndX=-11.49 EndY=20 EndZ=0
    g42: LineSegment StartX=-49.19 StartY=17.25 StartZ=0 EndX=-1.5 EndY=17.25 EndZ=0
    g43: LineSegment StartX=-49.19 StartY=14.25 StartZ=0 EndX=-1.5 EndY=14.25 EndZ=0
    g44: LineSegment StartX=-49.19 StartY=11.5 StartZ=0 EndX=-1.5 EndY=11.5 EndZ=0
    g45: LineSegment StartX=-49.19 StartY=8.5 StartZ=0 EndX=-1.5 EndY=8.5 EndZ=0
    g46: LineSegment StartX=-49.19 StartY=5.75 StartZ=0 EndX=-1.5 EndY=5.75 EndZ=0
    g47: LineSegment StartX=-49.19 StartY=2.75 StartZ=0 EndX=-1.5 EndY=2.75 EndZ=0
  constraints (120):
    c: Vertical(g0)
    c: Distance(g0) = 3
    c: Block(g0)
    c: Vertical(g1)
    c: Distance(g1) = 3
    c: Vertical(g2)
    c: Equal(g0,g2) = 3
    c: Block(g2)
    c: Vertical(g3)
    c: Equal(g1,g3) = 3
    c: Vertical(g4)
    c: Equal(g0,g4) = 3
    c: Block(g4)
    c: Vertical(g5)
    c: Equal(g1,g5) = 3
    c: Vertical(g6)
    c: Equal(g0,g6) = 3
    c: Block(g6)
    c: Vertical(g7)
    c: Equal(g1,g7) = 3
    c: Vertical(g8)
    c: Equal(g0,g8) = 3
    c: Block(g8)
    c: Vertical(g9)
    c: Equal(g1,g9) = 3
    c: Vertical(g10)
    c: Equal(g0,g10) = 3
    c: Block(g10)
    c: Vertical(g11)
    c: Equal(g1,g11) = 3
    c: Block(g12)
    c: Block(g13)
    c: Block(g14)
    c: Block(g15)
    c: Block(g16)
    c: Block(g17)
    c: Block(g18)
    c: Block(g19)
    c: Block(g20)
    c: Block(g21)
    c: Block(g22)
    c: Block(g23)
    c: Block(g11)
    c: Block(g9)
    c: Block(g7)
    c: Block(g5)
    c: Block(g3)
    c: Block(g1)
    c: Coincident(g24,g0)
    c: Coincident(g24,g12)
    c: Horizontal(g24)
    c: Coincident(g25,g0)
    c: Coincident(g25,g12)
    c: Horizontal(g25)
    c: Coincident(g26,g1)
    c: Coincident(g26,g13)
    c: Horizontal(g26)
    c: Coincident(g27,g1)
    c: Coincident(g27,g13)
    c: Horizontal(g27)
    c: Coincident(g28,g2)
    c: Coincident(g28,g14)
    c: Horizontal(g28)
    c: Coincident(g29,g2)
    c: Coincident(g29,g14)
    c: Horizontal(g29)
    c: Coincident(g30,g3)
    c: Coincident(g30,g15)
    c: Horizontal(g30)
    c: Coincident(g31,g3)
    c: Coincident(g31,g15)
    c: Horizontal(g31)
    c: Coincident(g32,g4)
    c: Coincident(g32,g16)
    c: Horizontal(g32)
    c: Coincident(g33,g4)
    c: Coincident(g33,g16)
    c: Horizontal(g33)
    c: Coincident(g34,g5)
    c: Coincident(g34,g17)
    c: Horizontal(g34)
    c: Coincident(g35,g5)
    c: Coincident(g35,g17)
    c: Horizontal(g35)
    c: Coincident(g36,g6)
    c: Coincident(g36,g19)
    c: Horizontal(g36)
    c: Coincident(g37,g6)
    c: Coincident(g37,g19)
    c: Horizontal(g37)
    c: Coincident(g38,g7)
    c: Coincident(g38,g18)
    c: Horizontal(g38)
    c: Coincident(g39,g7)
    c: Coincident(g39,g18)
    c: Horizontal(g39)
    c: Coincident(g40,g8)
    c: Coincident(g40,g20)
    c: Horizontal(g40)
    c: Coincident(g41,g8)
    c: Coincident(g41,g20)
    c: Horizontal(g41)
    c: Coincident(g42,g9)
    c: Coincident(g42,g23)
    c: Horizontal(g42)
    c: Coincident(g43,g9)
    c: Coincident(g43,g23)
    c: Horizontal(g43)
    c: Coincident(g44,g10)
    c: Coincident(g44,g22)
    c: Horizontal(g44)
    c: Coincident(g45,g10)
    c: Coincident(g45,g22)
    c: Horizontal(g45)
    c: Coincident(g46,g11)
    c: Coincident(g46,g21)
    c: Horizontal(g46)
    c: Coincident(g47,g11)
    c: Coincident(g47,g21)
    c: Horizontal(g47)
FEATURE [Part::Extrusion] Extrude061
  Base = -> Sketch070
  Dir = (1,0,0)
  DirMode = 2
  FaceMakerClass = Part::FaceMakerBullseye
  LengthFwd = 23
  LengthRev = 0
  Placement = pos=(-19,0,0) rot=(0,0,1;0rad)
  Solid = true
  Symmetric = false
FEATURE [Part::Fillet] Fillet052  label="removeToCreateVentalationHoles002"
  Base = -> Extrude061
  Edges = <same value as first occurrence — deduplicated (x6 in doc)>
  Placement = pos=(7,0.02,0) rot=(0,0,1;0rad)
FEATURE [Part::MultiFuse] Fusion130  label="bottom013"
  Shapes = -> [Cut054,Cut034]
FEATURE [Part::Cut] Cut055
  Base = -> Fusion130
  Tool = -> Fillet052
FEATURE [Part::Cylinder] Cylinder054
  Angle = 360
  AttacherType = Attacher::AttachEngine3D
  Height = 20
  Placement = pos=(0,0,36.15) rot=(0,0,1;0rad)
  Radius = 4
FEATURE [Sketcher::SketchObject] Sketch071  label="bottomSketch002"
  FullyConstrained = true
  sketch-geometry (32):
    g0: LineSegment StartX=3.3 StartY=-6.03275e-07 StartZ=0 EndX=98 EndY=-6.03275e-07 EndZ=0
    g1: ArcOfCircle CenterX=98 CenterY=19 CenterZ=0 NormalX=0 NormalY=0 NormalZ=1 AngleXU=0 Radius=19 StartAngle=4.71239 EndAngle=5.71103
    g2: LineSegment StartX=6.3 StartY=8 StartZ=0 EndX=3.3 EndY=8 EndZ=0
    g3: LineSegment StartX=3.3 StartY=8 StartZ=0 EndX=3.3 EndY=-6.03275e-07 EndZ=0
    g4: ArcOfCircle CenterX=8.3 CenterY=5 CenterZ=0 NormalX=0 NormalY=0 NormalZ=1 AngleXU=0 Radius=2 StartAngle=3.14159 EndAngle=4.71239
    g5: LineSegment StartX=6.3 StartY=8 StartZ=0 EndX=6.3 EndY=5 EndZ=0
    g6: ArcOfCircle CenterX=98 CenterY=19 CenterZ=0 NormalX=0 NormalY=0 NormalZ=1 AngleXU=0 Radius=12.7 StartAngle=4.71239 EndAngle=6.28319
    g7: LineSegment StartX=94.7 StartY=3 StartZ=0 EndX=8.3 EndY=3 EndZ=0
    g8-g12: Circle x5 (B-spline internal-alignment scaffolding for g13; pole/knot coordinates omitted)
    g13: BSplineCurve PolesCount=5 KnotsCount=3 Degree=3 IsPeriodic=0
    g14: GeomPoint X=98 Y=6.3 Z=0
    g15: GeomPoint X=96.3938 Y=4.71946 Z=0
    g16: GeomPoint X=94.7 Y=3 Z=0
    g17-g23: Circle x7 (B-spline internal-alignment scaffolding for g24; pole/knot coordinates omitted)
    g24: BSplineCurve PolesCount=7 KnotsCount=5 Degree=3 IsPeriodic=0
    g25-g29: GeomPoint x5 (B-spline internal-alignment scaffolding for g24; pole/knot coordinates omitted)
    g30: ArcOfCircle CenterX=98 CenterY=19 CenterZ=0 NormalX=0 NormalY=0 NormalZ=1 AngleXU=0 Radius=15.7 StartAngle=5.81226 EndAngle=6.28319
    g31: LineSegment StartX=110.7 StartY=19 StartZ=0 EndX=113.7 EndY=19 EndZ=0
  constraints (41):
    c: Horizontal(g0)
    c: Coincident(g1,g0)
    c: Block(g1)
    c: Horizontal(g2)
    c: Distance(g2) = 3
    c: Coincident(g3,g2)
    c: Vertical(g3)
    c: Coincident(g3,g0)
    c: Block(g4)
    c: Block(g2)
    c: Coincident(g5,g2)
    c: Coincident(g5,g4)
    c: Vertical(g5)
    c: Coincident(g6,g1)
    c: Block(g6)
    c: Coincident(g7,g4)
    c: Horizontal(g7)
    c: Block(g0)
    c: Block(g7)
    c: Block(g3)
    c: Coincident(g13,g6)
    c: Weight(g8) = 1
    c: Equal(g8, g9-g12) x4
    c: Coincident(g13,g7)
    c: InternalAlignment(g8-g12 -> g13) x5
    c: InternalAlignment(g14,g13)
    c: InternalAlignment(g15,g13)
    c: InternalAlignment(g16,g13)
    c: Block(g13)
    c: Weight(g17) = 1
    c: Equal(g17, g18-g23) x6
    c: Coincident(g24,g1)
    c: InternalAlignment(g17-g23 -> g24) x7
    c: InternalAlignment(g25-g29 -> g24) x5
    c: Block(g24)
    c: Coincident(g30,g24)
    c: Coincident(g31,g6)
    c: Coincident(g31,g30)
    c: Horizontal(g31)
    c: Block(g31)
    c: Block(g30)
FEATURE [Part::Extrusion] Extrude062  label="bottom014"
  Base = -> Sketch071
  Dir = (0,0,1)
  DirMode = 2
  FaceMakerClass = Part::FaceMakerBullseye
  LengthFwd = 71.4
  LengthRev = 0
  Placement = pos=(0,0,0.3) rot=(0,0,1;0rad)
  Solid = true
  Symmetric = false
FEATURE [Part::Fillet] Fillet054
  Base = -> Extrude062
  Edges = 1 edges r=2.4: [Edge17]
FEATURE [Part::Fillet] Fillet055  label="bottom015"
  Base = -> Fillet054
  Edges = 1 edges r=2.4: [Edge36]
FEATURE [Part::Cylinder] Cylinder055
  Angle = 360
  AttacherType = Attacher::AttachEngine3D
  Height = 10
  Placement = pos=(0,0,36.15) rot=(0,0,1;0rad)
  Radius = 4
FEATURE [Part::MultiFuse] Fusion131  label="removeToCreateHoleForPlugHousing002"
  Placement = pos=(70,19,36.15) rot=(0,1,0;1.5708rad)
  Shapes = -> [Cylinder054,Cylinder055]
FEATURE [Part::Cut] Cut056  label="Bottom001"
  Base = -> Fillet055
  Placement = pos=(9,0,0) rot=(0,0,1;0rad)
  Tool = -> Fusion131
FEATURE [Part::Cut] Cut057
  Base = -> Cut055
  Tool = -> Cut056
FEATURE [Sketcher::SketchObject] Sketch072  label="topSketch021"
  FullyConstrained = true
  sketch-geometry (4):
    g0: ArcOfCircle CenterX=105 CenterY=19 CenterZ=0 NormalX=0 NormalY=0 NormalZ=1 AngleXU=0 Radius=20.6155 StartAngle=5.54125 EndAngle=6.28319
    g1: ArcOfCircle CenterX=105 CenterY=19 CenterZ=0 NormalX=0 NormalY=0 NormalZ=1 AngleXU=0 Radius=13 StartAngle=5.54125 EndAngle=6.28319
    g2: LineSegment StartX=118 StartY=19 StartZ=0 EndX=125.616 EndY=19 EndZ=0
    g3: LineSegment StartX=114.583 StartY=10.2157 StartZ=0 EndX=120.197 EndY=5.06982 EndZ=0
  constraints (7):
    c: Block(g0)
    c: Block(g1)
    c: Coincident(g2,g1)
    c: Coincident(g2,g0)
    c: Horizontal(g2)
    c: Coincident(g3,g1)
    c: Coincident(g3,g0)
FEATURE [Part::Extrusion] Extrude063  label="bottomPlugHousingBit003"
  Base = -> Sketch072
  Dir = (0,0,1)
  DirMode = 2
  FaceMakerClass = Part::FaceMakerBullseye
  LengthFwd = 72
  LengthRev = 0
  Solid = true
  Symmetric = false
FEATURE [Part::Cylinder] Cylinder056
  Angle = 360
  AttacherType = Attacher::AttachEngine3D
  Height = 20
  Placement = pos=(0,0,36.15) rot=(0,0,1;0rad)
  Radius = 14.3
FEATURE [Part::Cylinder] Cylinder057
  Angle = 360
  AttacherType = Attacher::AttachEngine3D
  Height = 10
  Placement = pos=(0,0,36.15) rot=(0,0,1;0rad)
  Radius = 4
FEATURE [Part::Box] Box034  label="removeToCreteHoleForPlugHousing047"
  AttacherType = Attacher::AttachEngine3D
  Height = 28.6
  Length = 20
  Placement = pos=(106.15,0,21.7) rot=(0,0,1;0rad)
  Width = 19
FEATURE [Part::Cylinder] Cylinder058
  Angle = 360
  AttacherType = Attacher::AttachEngine3D
  Height = 20
  Placement = pos=(0,0,36.15) rot=(0,0,1;0rad)
  Radius = 14.3
FEATURE [Part::Cylinder] Cylinder059
  Angle = 360
  AttacherType = Attacher::AttachEngine3D
  Height = 10
  Placement = pos=(0,0,36.15) rot=(0,0,1;0rad)
  Radius = 4
FEATURE [Part::MultiFuse] Fusion134  label="removeToCreteHoleForPlugHousing046"
  Placement = pos=(70,19,36) rot=(0,1,0;1.5708rad)
  Shapes = -> [Cylinder058,Cylinder059]
FEATURE [Part::Cylinder] Cylinder060
  Angle = 360
  AttacherType = Attacher::AttachEngine3D
  Height = 20
  Placement = pos=(0,0,36.15) rot=(0,0,1;0rad)
  Radius = 14
FEATURE [Part::Cylinder] Cylinder061
  Angle = 360
  AttacherType = Attacher::AttachEngine3D
  Height = 10
  Placement = pos=(0,0,36.15) rot=(0,0,1;0rad)
  Radius = 4
FEATURE [Part::MultiFuse] Fusion135  label="removeToCreteHoleForPlugHousing048"
  Placement = pos=(70,19,36) rot=(0,1,0;1.5708rad)
  Shapes = -> [Cylinder060,Cylinder061]
FEATURE [Part::Box] Box035  label="removeToCreteHoleForPlugHousing049"
  AttacherType = Attacher::AttachEngine3D
  Height = 28.6
  Length = 20
  Placement = pos=(106.15,0,21.7) rot=(0,0,1;0rad)
  Width = 19
FEATURE [Part::MultiFuse] Fusion133  label="removeToCreteHoleForPlugHousing045"
  Placement = pos=(0,0,-28.3) rot=(0,0,1;0rad)
  Shapes = -> [Box035,Fusion134]
FEATURE [Part::MultiFuse] Fusion138  label="removeToCreteHoleForPlugHousing051"
  Placement = pos=(70,19,36) rot=(0,1,0;1.5708rad)
  Shapes = -> [Cylinder056,Cylinder057]
FEATURE [Part::MultiFuse] Fusion137  label="removeToCreteHoleForPlugHousing050"
  Placement = pos=(0,0,28.3) rot=(0,0,1;0rad)
  Shapes = -> [Box034,Fusion138]
FEATURE [Part::MultiFuse] Fusion132  label="removeToCreatePlugHousingBottomBit002"
  Shapes = -> [Fusion133,Fusion137]
FEATURE [Part::MultiFuse] Fusion136  label="removeToCreatePlugHousingBottomBit003"
  Shapes = -> [Fusion135,Fusion132]
FEATURE [Part::Cut] Cut058  label="bottomPlugHousingBit002"
  Base = -> Extrude063
  Placement = pos=(-0.09,0,0) rot=(0,0,1;0rad)
  Tool = -> Fusion136
FEATURE [Sketcher::SketchObject] Sketch073  label="bottomSketch003"
  FullyConstrained = true
  sketch-geometry (45):
    g0: LineSegment StartX=6.29999 StartY=8 StartZ=0 EndX=3.29999 EndY=8 EndZ=0
    g1: LineSegment StartX=3.29999 StartY=8 StartZ=0 EndX=3.29999 EndY=-6.03275e-07 EndZ=0
    g2: ArcOfCircle CenterX=8.29999 CenterY=5 CenterZ=0 NormalX=0 NormalY=0 NormalZ=1 AngleXU=0 Radius=2 StartAngle=3.14159 EndAngle=4.71239
    g3: LineSegment StartX=6.29999 StartY=8 StartZ=0 EndX=6.29999 EndY=5 EndZ=0
    g4: ArcOfCircle CenterX=105 CenterY=19 CenterZ=0 NormalX=0 NormalY=0 NormalZ=1 AngleXU=0 Radius=12.7 StartAngle=4.71239 EndAngle=5.94289
    g5-g11: Circle x7 (B-spline internal-alignment scaffolding for g12; pole/knot coordinates omitted)
    g12: BSplineCurve PolesCount=7 KnotsCount=5 Degree=3 IsPeriodic=0
    g13-g17: GeomPoint x5 (B-spline internal-alignment scaffolding for g12; pole/knot coordinates omitted)
    g18: ArcOfCircle CenterX=105 CenterY=19 CenterZ=0 NormalX=0 NormalY=0 NormalZ=1 AngleXU=0 Radius=15.7 StartAngle=5.81226 EndAngle=6.28319
    g19: BSplineCurve PolesCount=5 KnotsCount=3 Degree=3 IsPeriodic=0
    g20: LineSegment StartX=8.29999 StartY=3 StartZ=0 EndX=101.7 EndY=3 EndZ=0
    g21: LineSegment StartX=3.29999 StartY=-6.03275e-07 StartZ=0 EndX=105 EndY=-6.03275e-07 EndZ=0
    g22: LineSegment StartX=120.974 StartY=8.71251 StartZ=0 EndX=122.332 EndY=7.83778 EndZ=0
    g23: LineSegment StartX=105 StartY=-6.03274e-07 StartZ=0 EndX=113 EndY=-6.03274e-07 EndZ=0
    g24: ArcOfCircle CenterX=105 CenterY=19 CenterZ=0 NormalX=0 NormalY=0 NormalZ=1 AngleXU=0 Radius=20.6155 StartAngle=5.11091 EndAngle=5.71103
    g25: ArcOfCircle CenterX=117.7 CenterY=19 CenterZ=0 NormalX=0 NormalY=0 NormalZ=1 AngleXU=0 Radius=3 StartAngle=1.2e-15 EndAngle=2.10468
    g26: Circle CenterX=116.345 CenterY=16.3232 CenterZ=0 NormalX=0 NormalY=0 NormalZ=1 AngleXU=0 Radius=1
    g27: Circle CenterX=117.24 CenterY=15.7584 CenterZ=0 NormalX=0 NormalY=0 NormalZ=1 AngleXU=0 Radius=1
    g28: Circle CenterX=116.972 CenterY=14.7612 CenterZ=0 NormalX=0 NormalY=0 NormalZ=1 AngleXU=0 Radius=1
    g29: BSplineCurve PolesCount=3 KnotsCount=2 Degree=2 IsPeriodic=0
    g30: GeomPoint X=116.345 Y=16.3232 Z=0
    g31: GeomPoint X=116.972 Y=14.7612 Z=0
    g32: Circle CenterX=115.828 CenterY=17.157 CenterZ=0 NormalX=0 NormalY=0 NormalZ=1 AngleXU=0 Radius=1
    g33: Circle CenterX=115.841 CenterY=16.639 CenterZ=0 NormalX=0 NormalY=0 NormalZ=1 AngleXU=0 Radius=1
    g34: Circle CenterX=116.345 CenterY=16.3232 CenterZ=0 NormalX=0 NormalY=0 NormalZ=1 AngleXU=0 Radius=1
    g35: BSplineCurve PolesCount=3 KnotsCount=2 Degree=2 IsPeriodic=0
    g36: GeomPoint X=115.828 Y=17.157 Z=0
    g37: GeomPoint X=116.345 Y=16.3232 Z=0
    g38: LineSegment StartX=115.828 StartY=17.157 StartZ=0 EndX=115.828 EndY=20.8307 EndZ=0
    g39: Circle CenterX=115.828 CenterY=20.8307 CenterZ=0 NormalX=0 NormalY=0 NormalZ=1 AngleXU=0 Radius=1
    g40: Circle CenterX=115.831 CenterY=21.3396 CenterZ=0 NormalX=0 NormalY=0 NormalZ=1 AngleXU=0 Radius=1
    g41: Circle CenterX=116.173 CenterY=21.5825 CenterZ=0 NormalX=0 NormalY=0 NormalZ=1 AngleXU=0 Radius=1
    g42: BSplineCurve PolesCount=3 KnotsCount=2 Degree=2 IsPeriodic=0
    g43: GeomPoint X=115.828 Y=20.8307 Z=0
    g44: GeomPoint X=116.173 Y=21.5825 Z=0
  constraints (70):
    c: Horizontal(g0)
    c: Distance(g0) = 3
    c: Coincident(g1,g0)
    c: Vertical(g1)
    c: Block(g2)
    c: Block(g0)
    c: Coincident(g3,g0)
    c: Coincident(g3,g2)
    c: Vertical(g3)
    c: Block(g1)
    c: Block(g4)
    c: Coincident(g19,g4)
    c: Block(g19)
    c: Equal(g5, g6-g11) x6
    c: InternalAlignment(g5-g11 -> g12) x7
    c: InternalAlignment(g13-g17 -> g12) x5
    c: Block(g12)
    c: Coincident(g18,g12)
    c: Block(g18)
    c: Coincident(g20,g2)
    c: Coincident(g20,g19)
    c: Horizontal(g20)
    c: Distance(g20) = 93.4
    c: Coincident(g21,g1)
    c: Horizontal(g21)
    c: Distance(g21) = 101.7
    c: Horizontal(g23)
    c: Distance(g23) = 8
    c: Coincident(g24,g23)
    c: Block(g23)
    c: Coincident(g22,g24)
    c: Block(g24)
    c: Block(g22)
    c: Distance(g22) = 1.61553
    c: Coincident(g25,g18)
    c: Block(g25)
    c: Weight(g26) = 1
    c: Equal(g26,g27)
    c: Equal(g26,g28)
    c: Coincident(g29,g4)
    c: InternalAlignment(g26,g29)
    c: InternalAlignment(g27,g29)
    c: InternalAlignment(g28,g29)
    c: InternalAlignment(g30,g29)
    c: InternalAlignment(g31,g29)
    c: Block(g29)
    c: Weight(g32) = 1
    c: Equal(g32,g33)
    c: Equal(g32,g34)
    c: Coincident(g35,g29)
    c: InternalAlignment(g32,g35)
    c: InternalAlignment(g33,g35)
    c: InternalAlignment(g34,g35)
    c: InternalAlignment(g36,g35)
    c: InternalAlignment(g37,g35)
    c: Block(g35)
    c: Coincident(g38,g35)
    c: Vertical(g38)
    c: Block(g38)
    c: Coincident(g42,g38)
    c: Weight(g39) = 1
    c: Equal(g39,g40)
    c: Equal(g39,g41)
    c: Coincident(g42,g25)
    c: InternalAlignment(g39,g42)
    c: InternalAlignment(g40,g42)
    c: InternalAlignment(g41,g42)
    c: InternalAlignment(g43,g42)
    c: InternalAlignment(g44,g42)
    c: Block(g42)
FEATURE [Part::Extrusion] Extrude064  label="bottom016"
  Base = -> Sketch073
  Dir = (0,0,1)
  DirMode = 2
  FaceMakerClass = Part::FaceMakerBullseye
  LengthFwd = 71.4
  LengthRev = 0
  Placement = pos=(0,0,0.3) rot=(0,0,1;0rad)
  Solid = true
  Symmetric = false
FEATURE [Part::Revolution] Revolve157  label="removeToCreateScrewAndThreadedInsertHole063"
  Angle = 360
  Axis = (0,1,0)
  Base = (0,0,0)
  FaceMakerClass = Part::FaceMakerBullseye
  Placement = pos=(12.5,0,10) rot=(0,0,1;0rad)
  Solid = false
  Source = -> Face141
  Symmetric = false
FEATURE [Sketcher::SketchObject] Sketch074
  FullyConstrained = true
  Placement = pos=(117,19,0) rot=(0.57735,0.57735,0.57735;2.0944rad)
  sketch-geometry (48):
    g0: LineSegment StartX=-49.19 StartY=69.25 StartZ=0 EndX=-49.19 EndY=66.25 EndZ=0
    g1: LineSegment StartX=-49.19 StartY=63.5 StartZ=0 EndX=-49.19 EndY=60.5 EndZ=0
    g2: LineSegment StartX=-49.19 StartY=57.75 StartZ=0 EndX=-49.19 EndY=54.75 EndZ=0
    g3: LineSegment StartX=-49.19 StartY=52 StartZ=0 EndX=-49.19 EndY=49 EndZ=0
    g4: LineSegment StartX=-49.19 StartY=46.25 StartZ=0 EndX=-49.19 EndY=43.25 EndZ=0
    g5: LineSegment StartX=-49.19 StartY=40.5 StartZ=0 EndX=-49.19 EndY=37.5 EndZ=0
    g6: LineSegment StartX=-49.19 StartY=34.5 StartZ=0 EndX=-49.19 EndY=31.5 EndZ=0
    g7: LineSegment StartX=-49.19 StartY=28.75 StartZ=0 EndX=-49.19 EndY=25.75 EndZ=0
    g8: LineSegment StartX=-49.19 StartY=23 StartZ=0 EndX=-49.19 EndY=20 EndZ=0
    g9: LineSegment StartX=-49.19 StartY=17.25 StartZ=0 EndX=-49.19 EndY=14.25 EndZ=0
    g10: LineSegment StartX=-49.19 StartY=11.5 StartZ=0 EndX=-49.19 EndY=8.5 EndZ=0
    g11: LineSegment StartX=-49.19 StartY=5.75 StartZ=0 EndX=-49.19 EndY=2.75 EndZ=0
    g12: ArcOfCircle CenterX=-1.5 CenterY=67.75 CenterZ=0 NormalX=0 NormalY=0 NormalZ=1 AngleXU=0 Radius=1.5 StartAngle=4.71239 EndAngle=7.85398
    g13: ArcOfCircle CenterX=-1.5 CenterY=62 CenterZ=0 NormalX=0 NormalY=0 NormalZ=1 AngleXU=0 Radius=1.5 StartAngle=4.71239 EndAngle=7.85398
    g14: ArcOfCircle CenterX=-1.5 CenterY=56.25 CenterZ=0 NormalX=0 NormalY=0 NormalZ=1 AngleXU=0 Radius=1.5 StartAngle=4.71239 EndAngle=7.85398
    g15: ArcOfCircle CenterX=-11.49 CenterY=50.5 CenterZ=0 NormalX=0 NormalY=0 NormalZ=1 AngleXU=0 Radius=1.5 StartAngle=4.71239 EndAngle=7.85398
    g16: ArcOfCircle CenterX=-16.28 CenterY=44.75 CenterZ=0 NormalX=0 NormalY=0 NormalZ=1 AngleXU=0 Radius=1.5 StartAngle=4.71239 EndAngle=7.85398
    g17: ArcOfCircle CenterX=-18.2337 CenterY=39 CenterZ=0 NormalX=0 NormalY=0 NormalZ=1 AngleXU=0 Radius=1.5 StartAngle=4.71485 EndAngle=7.85398
    g18: ArcOfCircle CenterX=-16.2837 CenterY=27.25 CenterZ=0 NormalX=0 NormalY=0 NormalZ=1 AngleXU=0 Radius=1.5 StartAngle=4.71485 EndAngle=7.85398
    g19: ArcOfCircle CenterX=-18.2337 CenterY=33 CenterZ=0 NormalX=0 NormalY=0 NormalZ=1 AngleXU=0 Radius=1.5 StartAngle=4.71485 EndAngle=7.85398
    g20: ArcOfCircle CenterX=-11.49 CenterY=21.5 CenterZ=0 NormalX=0 NormalY=0 NormalZ=1 AngleXU=0 Radius=1.5 StartAngle=4.71239 EndAngle=7.85398
    g21: ArcOfCircle CenterX=-1.5 CenterY=4.25 CenterZ=0 NormalX=0 NormalY=0 NormalZ=1 AngleXU=0 Radius=1.5 StartAngle=4.71239 EndAngle=7.85398
    g22: ArcOfCircle CenterX=-1.5 CenterY=10 CenterZ=0 NormalX=0 NormalY=0 NormalZ=1 AngleXU=0 Radius=1.5 StartAngle=4.71239 EndAngle=7.85398
    g23: ArcOfCircle CenterX=-1.5 CenterY=15.75 CenterZ=0 NormalX=0 NormalY=0 NormalZ=1 AngleXU=0 Radius=1.5 StartAngle=4.71239 EndAngle=7.85398
    g24: LineSegment StartX=-49.19 StartY=69.25 StartZ=0 EndX=-1.5 EndY=69.25 EndZ=0
    g25: LineSegment StartX=-49.19 StartY=66.25 StartZ=0 EndX=-1.5 EndY=66.25 EndZ=0
    g26: LineSegment StartX=-49.19 StartY=63.5 StartZ=0 EndX=-1.5 EndY=63.5 EndZ=0
    g27: LineSegment StartX=-49.19 StartY=60.5 StartZ=0 EndX=-1.5 EndY=60.5 EndZ=0
    g28: LineSegment StartX=-49.19 StartY=57.75 StartZ=0 EndX=-1.5 EndY=57.75 EndZ=0
    g29: LineSegment StartX=-49.19 StartY=54.75 StartZ=0 EndX=-1.5 EndY=54.75 EndZ=0
    g30: LineSegment StartX=-49.19 StartY=52 StartZ=0 EndX=-11.49 EndY=52 EndZ=0
    g31: LineSegment StartX=-49.19 StartY=49 StartZ=0 EndX=-11.49 EndY=49 EndZ=0
    g32: LineSegment StartX=-49.19 StartY=46.25 StartZ=0 EndX=-16.28 EndY=46.25 EndZ=0
    g33: LineSegment StartX=-49.19 StartY=43.25 StartZ=0 EndX=-16.28 EndY=43.25 EndZ=0
    g34: LineSegment StartX=-49.19 StartY=40.5 StartZ=0 EndX=-18.2337 EndY=40.5 EndZ=0
    g35: LineSegment StartX=-49.19 StartY=37.5 StartZ=0 EndX=-18.23 EndY=37.5 EndZ=0
    g36: LineSegment StartX=-49.19 StartY=34.5 StartZ=0 EndX=-18.2337 EndY=34.5 EndZ=0
    g37: LineSegment StartX=-49.19 StartY=31.5 StartZ=0 EndX=-18.23 EndY=31.5 EndZ=0
    g38: LineSegment StartX=-49.19 StartY=28.75 StartZ=0 EndX=-16.2837 EndY=28.75 EndZ=0
    g39: LineSegment StartX=-49.19 StartY=25.75 StartZ=0 EndX=-16.28 EndY=25.75 EndZ=0
    g40: LineSegment StartX=-49.19 StartY=23 StartZ=0 EndX=-11.49 EndY=23 EndZ=0
    g41: LineSegment StartX=-49.19 StartY=20 StartZ=0 EndX=-11.49 EndY=20 EndZ=0
    g42: LineSegment StartX=-49.19 StartY=17.25 StartZ=0 EndX=-1.5 EndY=17.25 EndZ=0
    g43: LineSegment StartX=-49.19 StartY=14.25 StartZ=0 EndX=-1.5 EndY=14.25 EndZ=0
    g44: LineSegment StartX=-49.19 StartY=11.5 StartZ=0 EndX=-1.5 EndY=11.5 EndZ=0
    g45: LineSegment StartX=-49.19 StartY=8.5 StartZ=0 EndX=-1.5 EndY=8.5 EndZ=0
    g46: LineSegment StartX=-49.19 StartY=5.75 StartZ=0 EndX=-1.5 EndY=5.75 EndZ=0
    g47: LineSegment StartX=-49.19 StartY=2.75 StartZ=0 EndX=-1.5 EndY=2.75 EndZ=0
  constraints (120):
    c: Vertical(g0)
    c: Distance(g0) = 3
    c: Block(g0)
    c: Vertical(g1)
    c: Distance(g1) = 3
    c: Vertical(g2)
    c: Equal(g0,g2) = 3
    c: Block(g2)
    c: Vertical(g3)
    c: Equal(g1,g3) = 3
    c: Vertical(g4)
    c: Equal(g0,g4) = 3
    c: Block(g4)
    c: Vertical(g5)
    c: Equal(g1,g5) = 3
    c: Vertical(g6)
    c: Equal(g0,g6) = 3
    c: Block(g6)
    c: Vertical(g7)
    c: Equal(g1,g7) = 3
    c: Vertical(g8)
    c: Equal(g0,g8) = 3
    c: Block(g8)
    c: Vertical(g9)
    c: Equal(g1,g9) = 3
    c: Vertical(g10)
    c: Equal(g0,g10) = 3
    c: Block(g10)
    c: Vertical(g11)
    c: Equal(g1,g11) = 3
    c: Block(g12)
    c: Block(g13)
    c: Block(g14)
    c: Block(g15)
    c: Block(g16)
    c: Block(g17)
    c: Block(g18)
    c: Block(g19)
    c: Block(g20)
    c: Block(g21)
    c: Block(g22)
    c: Block(g23)
    c: Block(g11)
    c: Block(g9)
    c: Block(g7)
    c: Block(g5)
    c: Block(g3)
    c: Block(g1)
    c: Coincident(g24,g0)
    c: Coincident(g24,g12)
    c: Horizontal(g24)
    c: Coincident(g25,g0)
    c: Coincident(g25,g12)
    c: Horizontal(g25)
    c: Coincident(g26,g1)
    c: Coincident(g26,g13)
    c: Horizontal(g26)
    c: Coincident(g27,g1)
    c: Coincident(g27,g13)
    c: Horizontal(g27)
    c: Coincident(g28,g2)
    c: Coincident(g28,g14)
    c: Horizontal(g28)
    c: Coincident(g29,g2)
    c: Coincident(g29,g14)
    c: Horizontal(g29)
    c: Coincident(g30,g3)
    c: Coincident(g30,g15)
    c: Horizontal(g30)
    c: Coincident(g31,g3)
    c: Coincident(g31,g15)
    c: Horizontal(g31)
    c: Coincident(g32,g4)
    c: Coincident(g32,g16)
    c: Horizontal(g32)
    c: Coincident(g33,g4)
    c: Coincident(g33,g16)
    c: Horizontal(g33)
    c: Coincident(g34,g5)
    c: Coincident(g34,g17)
    c: Horizontal(g34)
    c: Coincident(g35,g5)
    c: Coincident(g35,g17)
    c: Horizontal(g35)
    c: Coincident(g36,g6)
    c: Coincident(g36,g19)
    c: Horizontal(g36)
    c: Coincident(g37,g6)
    c: Coincident(g37,g19)
    c: Horizontal(g37)
    c: Coincident(g38,g7)
    c: Coincident(g38,g18)
    c: Horizontal(g38)
    c: Coincident(g39,g7)
    c: Coincident(g39,g18)
    c: Horizontal(g39)
    c: Coincident(g40,g8)
    c: Coincident(g40,g20)
    c: Horizontal(g40)
    c: Coincident(g41,g8)
    c: Coincident(g41,g20)
    c: Horizontal(g41)
    c: Coincident(g42,g9)
    c: Coincident(g42,g23)
    c: Horizontal(g42)
    c: Coincident(g43,g9)
    c: Coincident(g43,g23)
    c: Horizontal(g43)
    c: Coincident(g44,g10)
    c: Coincident(g44,g22)
    c: Horizontal(g44)
    c: Coincident(g45,g10)
    c: Coincident(g45,g22)
    c: Horizontal(g45)
    c: Coincident(g46,g11)
    c: Coincident(g46,g21)
    c: Horizontal(g46)
    c: Coincident(g47,g11)
    c: Coincident(g47,g21)
    c: Horizontal(g47)
FEATURE [Part::Extrusion] Extrude065
  Base = -> Sketch074
  Dir = (1,0,0)
  DirMode = 2
  FaceMakerClass = Part::FaceMakerBullseye
  LengthFwd = 23
  LengthRev = 0
  Placement = pos=(-19,0,0) rot=(0,0,1;0rad)
  Solid = true
  Symmetric = false
FEATURE [Part::Fillet] Fillet056  label="removeToCreateVentalationHoles003"
  Base = -> Extrude065
  Edges = <same value as first occurrence — deduplicated (x6 in doc)>
  Placement = pos=(7,0.02,0) rot=(0,0,1;0rad)
FEATURE [Part::Revolution] Revolve158  label="removeToCreateScrewAndThreadedInsertHole065"
  Angle = 360
  Axis = (0,1,0)
  Base = (0,0,0)
  FaceMakerClass = Part::FaceMakerBullseye
  Placement = pos=(12.5,0,62) rot=(0,0,1;0rad)
  Solid = false
  Source = -> Face146
  Symmetric = false
FEATURE [Part::Revolution] Revolve159  label="removeToCreateScrewAndThreadedInsertHole066"
  Angle = 360
  Axis = (0,1,0)
  Base = (0,0,0)
  FaceMakerClass = Part::FaceMakerBullseye
  Placement = pos=(89.5,0,68.5) rot=(0,0,1;0rad)
  Solid = false
  Source = -> Face143
  Symmetric = false
FEATURE [Part::Revolution] Revolve160  label="removeToCreateScrewAndThreadedInsertHole067"
  Angle = 360
  Axis = (0,1,0)
  Base = (0,0,0)
  FaceMakerClass = Part::FaceMakerBullseye
  Placement = pos=(89.5,0,3.5) rot=(0,0,1;0rad)
  Solid = false
  Source = -> Face142
  Symmetric = false
FEATURE [Part::Revolution] Revolve161  label="removeToCreateScrewAndThreadedInsertHole068"
  Angle = 360
  Axis = (0,1,0)
  Base = (0,0,0)
  FaceMakerClass = Part::FaceMakerBullseye
  Placement = pos=(109.5,4.7,3.5) rot=(0,0,1;0rad)
  Solid = false
  Source = -> Face145
  Symmetric = false
FEATURE [Part::Revolution] Revolve162  label="removeToCreateScrewAndThreadedInsertHole069"
  Angle = 360
  Axis = (0,1,0)
  Base = (0,0,0)
  FaceMakerClass = Part::FaceMakerBullseye
  Placement = pos=(109.5,4.7,68.5) rot=(0,0,1;0rad)
  Solid = false
  Source = -> Face144
  Symmetric = false
FEATURE [Part::MultiFuse] Fusion141  label="removeToCreateScrewAndThreadedInsertHole064"
  Shapes = -> [Revolve162,Revolve161,Revolve160,Revolve159,Revolve158,Revolve157]
FEATURE [Part::Cylinder] Cylinder062
  Angle = 360
  AttacherType = Attacher::AttachEngine3D
  Height = 20
  Placement = pos=(0,0,36.15) rot=(0,0,1;0rad)
  Radius = 14
FEATURE [Part::Cylinder] Cylinder063
  Angle = 360
  AttacherType = Attacher::AttachEngine3D
  Height = 10
  Placement = pos=(0,0,36.15) rot=(0,0,1;0rad)
  Radius = 4
FEATURE [Part::MultiFuse] Fusion139  label="removeToCreteHoleForPlugHousing052"
  Placement = pos=(70,19,36) rot=(0,1,0;1.5708rad)
  Shapes = -> [Cylinder062,Cylinder063]
FEATURE [Part::Cut] Cut060  label="bottom017"
  Base = -> Extrude064
  Tool = -> Fusion139
FEATURE [Part::Cut] Cut061  label="bottom019"
  Base = -> Cut060
  Tool = -> Fusion141
FEATURE [Part::MultiFuse] Fusion140  label="bottom018"
  Shapes = -> [Cut061,Cut058]
FEATURE [Part::Cut] Cut059  label="bottom020"
  Base = -> Fusion140
  Tool = -> Fillet056
FEATURE [Part::Box] Box036  label="Cube021"
  AttacherType = Attacher::AttachEngine3D
  Height = 80
  Length = 26
  Placement = pos=(0,-1,-5) rot=(0,0,1;0rad)
  Width = 11
FEATURE [Part::Cut] Cut062  label="removeFromBottom002"
  Base = -> Cut057
  Tool = -> Box036
FEATURE [Part::Cut] Cut063
  Base = -> Cut059
  Tool = -> Cut062
FEATURE [Part::Cut] Cut064  label="pcbStands"
  Base = -> Fusion095
  Tool = -> Fusion127
FEATURE [Sketcher::SketchObject] Sketch075  label="topSketch022"
  FullyConstrained = true
  sketch-geometry (6):
    g0: LineSegment StartX=19 StartY=38 StartZ=0 EndX=117 EndY=38 EndZ=0
    g1: ArcOfCircle CenterX=19 CenterY=19 CenterZ=0 NormalX=0 NormalY=0 NormalZ=1 AngleXU=0 Radius=19 StartAngle=1.5708 EndAngle=3.14159
    g2: LineSegment StartX=117 StartY=38 StartZ=0 EndX=117 EndY=19 EndZ=0
    g3: LineSegment StartX=98 StartY=1.0161e-12 StartZ=0 EndX=5.22862e-06 EndY=1.0161e-12 EndZ=0
    g4: LineSegment StartX=5.22862e-06 StartY=19 StartZ=0 EndX=5.22862e-06 EndY=1.0161e-12 EndZ=0
    g5: ArcOfCircle CenterX=98 CenterY=19 CenterZ=0 NormalX=0 NormalY=0 NormalZ=1 AngleXU=0 Radius=19 StartAngle=4.71239 EndAngle=6.28319
  constraints (16):
    c: Horizontal(g0)
    c: Distance(g0) = 98
    c: Coincident(g1,g0)
    c: Block(g1)
    c: Coincident(g2,g0)
    c: Vertical(g2)
    c: Distance(g2) = 19
    c: Horizontal(g3)
    c: Coincident(g4,g1)
    c: Vertical(g4)
    c: Coincident(g3,g4)
    c: Block(g3)
    c: Coincident(g5,g2)
    c: Coincident(g5,g3)
    c: Block(g0)
    c: Block(g5)
FEATURE [Part::Extrusion] Extrude067  label="sideB003"
  Base = -> Sketch075
  Dir = (0,0,1)
  DirMode = 2
  FaceMakerClass = Part::FaceMakerBullseye
  LengthFwd = 3
  LengthRev = 0
  Placement = pos=(0,0,71.7) rot=(0,0,1;0rad)
  Solid = true
  Symmetric = false
FEATURE [Sketcher::SketchObject] Sketch076  label="topSketch023"
  FullyConstrained = true
  sketch-geometry (6):
    g0: LineSegment StartX=19 StartY=38 StartZ=0 EndX=117 EndY=38 EndZ=0
    g1: ArcOfCircle CenterX=19 CenterY=19 CenterZ=0 NormalX=0 NormalY=0 NormalZ=1 AngleXU=0 Radius=19 StartAngle=1.5708 EndAngle=3.14159
    g2: LineSegment StartX=117 StartY=38 StartZ=0 EndX=117 EndY=19 EndZ=0
    g3: LineSegment StartX=98 StartY=1.0161e-12 StartZ=0 EndX=5.22862e-06 EndY=1.0161e-12 EndZ=0
    g4: LineSegment StartX=5.22862e-06 StartY=19 StartZ=0 EndX=5.22862e-06 EndY=1.0161e-12 EndZ=0
    g5: ArcOfCircle CenterX=98 CenterY=19 CenterZ=0 NormalX=0 NormalY=0 NormalZ=1 AngleXU=0 Radius=19 StartAngle=4.71239 EndAngle=6.28319
  constraints (16):
    c: Horizontal(g0)
    c: Distance(g0) = 98
    c: Coincident(g1,g0)
    c: Block(g1)
    c: Coincident(g2,g0)
    c: Vertical(g2)
    c: Distance(g2) = 19
    c: Horizontal(g3)
    c: Coincident(g4,g1)
    c: Vertical(g4)
    c: Coincident(g3,g4)
    c: Block(g3)
    c: Coincident(g5,g2)
    c: Coincident(g5,g3)
    c: Block(g0)
    c: Block(g5)
FEATURE [Part::Extrusion] Extrude066  label="sideA003"
  Base = -> Sketch076
  Dir = (0,0,1)
  DirMode = 2
  FaceMakerClass = Part::FaceMakerBullseye
  LengthFwd = 3
  LengthRev = 0
  Placement = pos=(0,0,-2.7) rot=(0,0,1;0rad)
  Solid = true
  Symmetric = false
FEATURE [Part::MultiFuse] Fusion142  label="removeFromBottom003"
  Placement = pos=(2,0,0) rot=(0,0,1;0rad)
  Shapes = -> [Extrude066,Extrude067]
FEATURE [Part::Cut] Cut065  label="screwRetainers002"
  Base = -> Fusion096
  Tool = -> Fusion142
FEATURE [Sketcher::SketchObject] Sketch077
  FullyConstrained = true
  Placement = pos=(117,19,0) rot=(0.57735,0.57735,0.57735;2.0944rad)
  sketch-geometry (8):
    g0: LineSegment StartX=-49.19 StartY=63.5 StartZ=0 EndX=-49.19 EndY=60.5 EndZ=0
    g1: LineSegment StartX=-49.19 StartY=11.5 StartZ=0 EndX=-49.19 EndY=8.5 EndZ=0
    g2: ArcOfCircle CenterX=-1.5 CenterY=62 CenterZ=0 NormalX=0 NormalY=0 NormalZ=1 AngleXU=0 Radius=1.5 StartAngle=4.71239 EndAngle=7.85398
    g3: ArcOfCircle CenterX=-1.5 CenterY=10 CenterZ=0 NormalX=0 NormalY=0 NormalZ=1 AngleXU=0 Radius=1.5 StartAngle=4.71239 EndAngle=7.85398
    g4: LineSegment StartX=-49.19 StartY=63.5 StartZ=0 EndX=-1.5 EndY=63.5 EndZ=0
    g5: LineSegment StartX=-49.19 StartY=60.5 StartZ=0 EndX=-1.5 EndY=60.5 EndZ=0
    g6: LineSegment StartX=-49.19 StartY=11.5 StartZ=0 EndX=-1.5 EndY=11.5 EndZ=0
    g7: LineSegment StartX=-49.19 StartY=8.5 StartZ=0 EndX=-1.5 EndY=8.5 EndZ=0
  constraints (19):
    c: Vertical(g0)
    c: Distance(g0) = 3
    c: Vertical(g1)
    c: Block(g1)
    c: Block(g2)
    c: Block(g3)
    c: Block(g0)
    c: Coincident(g4,g0)
    c: Coincident(g4,g2)
    c: Horizontal(g4)
    c: Coincident(g5,g0)
    c: Coincident(g5,g2)
    c: Horizontal(g5)
    c: Coincident(g6,g1)
    c: Coincident(g6,g3)
    c: Horizontal(g6)
    c: Coincident(g7,g1)
    c: Coincident(g7,g3)
    c: Horizontal(g7)
FEATURE [Part::Extrusion] Extrude068
  Base = -> Sketch077
  Dir = (1,0,0)
  DirMode = 2
  FaceMakerClass = Part::FaceMakerBullseye
  LengthFwd = 10
  LengthRev = 0
  Solid = true
  Symmetric = false
FEATURE [Part::Fillet] Fillet057  label="removeFromtMoreFrontCaseScrewRetainers002"
  Base = -> Extrude068
  Edges = 4 edges r=1.49: [Edge6,Edge11,Edge18,Edge23]
  Placement = pos=(-12,0,0) rot=(0,0,1;0rad)
FEATURE [Sketcher::SketchObject] Sketch078
  FullyConstrained = true
  Placement = pos=(117,19,0) rot=(0.57735,0.57735,0.57735;2.0944rad)
  sketch-geometry (8):
    g0: LineSegment StartX=-49.19 StartY=69.25 StartZ=0 EndX=-49.19 EndY=66.25 EndZ=0
    g1: LineSegment StartX=-49.19 StartY=5.75 StartZ=0 EndX=-49.19 EndY=2.75 EndZ=0
    g2: ArcOfCircle CenterX=-1.5 CenterY=67.75 CenterZ=0 NormalX=0 NormalY=0 NormalZ=1 AngleXU=0 Radius=1.5 StartAngle=4.71239 EndAngle=7.85398
    g3: ArcOfCircle CenterX=-1.5 CenterY=4.25 CenterZ=0 NormalX=0 NormalY=0 NormalZ=1 AngleXU=0 Radius=1.5 StartAngle=4.71239 EndAngle=7.85398
    g4: LineSegment StartX=-49.19 StartY=69.25 StartZ=0 EndX=-1.5 EndY=69.25 EndZ=0
    g5: LineSegment StartX=-49.19 StartY=66.25 StartZ=0 EndX=-1.5 EndY=66.25 EndZ=0
    g6: LineSegment StartX=-49.19 StartY=5.75 StartZ=0 EndX=-1.5 EndY=5.75 EndZ=0
    g7: LineSegment StartX=-49.19 StartY=2.75 StartZ=0 EndX=-1.5 EndY=2.75 EndZ=0
  constraints (19):
    c: Vertical(g0)
    c: Distance(g0) = 3
    c: Block(g0)
    c: Vertical(g1)
    c: Block(g2)
    c: Block(g3)
    c: Block(g1)
    c: Coincident(g4,g0)
    c: Coincident(g4,g2)
    c: Horizontal(g4)
    c: Coincident(g5,g0)
    c: Coincident(g5,g2)
    c: Horizontal(g5)
    c: Coincident(g6,g1)
    c: Coincident(g6,g3)
    c: Horizontal(g6)
    c: Coincident(g7,g1)
    c: Coincident(g7,g3)
    c: Horizontal(g7)
FEATURE [Part::Extrusion] Extrude069
  Base = -> Sketch078
  Dir = (1,0,0)
  DirMode = 2
  FaceMakerClass = Part::FaceMakerBullseye
  LengthFwd = 10
  LengthRev = 0
  Solid = true
  Symmetric = false
FEATURE [Part::Fillet] Fillet058  label="removeFromtMoreFrontCaseScrewRetainers003"
  Base = -> Extrude069
  Edges = 4 edges r=1.49: [Edge6,Edge11,Edge18,Edge23]
  Placement = pos=(-4,0,0) rot=(0,0,1;0rad)
FEATURE [Part::Cut] Cut066
  Base = -> Cut065
  Tool = -> Fillet058
FEATURE [Part::Cut] Cut067  label="screwPillars"
  Base = -> Cut066
  Tool = -> Fillet057
FEATURE [Part::MultiFuse] Fusion143  label="bottom021"
  Shapes = -> [Cut031,Cut063]
FEATURE [Part::Cylinder] Cylinder
  Angle = 360
  AttacherType = Attacher::AttachEngine3D
  Height = 10
  Placement = pos=(20.65,12,4.68) rot=(1,0,0;1.5708rad)
  Radius = 2
FEATURE [Part::Cylinder] Cylinder064
  Angle = 360
  AttacherType = Attacher::AttachEngine3D
  Height = 10
  Placement = pos=(20.65,12,67.38) rot=(1,0,0;1.5708rad)
  Radius = 2
FEATURE [Part::Cylinder] Cylinder065
  Angle = 360
  AttacherType = Attacher::AttachEngine3D
  Height = 10
  Placement = pos=(77.15,12,67.38) rot=(1,0,0;1.5708rad)
  Radius = 2
FEATURE [Part::Cylinder] Cylinder066
  Angle = 360
  AttacherType = Attacher::AttachEngine3D
  Height = 10
  Placement = pos=(77.15,12,4.68) rot=(1,0,0;1.5708rad)
  Radius = 2
FEATURE [Part::MultiFuse] Fusion144  label="removeFromThreadedInsertHousing"
  Shapes = -> [Cylinder065,Cylinder064,Cylinder,Cylinder066]
FEATURE [Part::Cut] Cut068  label="pcbStands001"
  Base = -> Cut064
  Tool = -> Fusion144
FEATURE [Part::MultiFuse] Fusion145
  Shapes = -> [Cut068,Fusion143]
FEATURE [Part::MultiFuse] Fusion146
  Shapes = -> [Fusion145]
FEATURE [Part::MultiFuse] Fusion147  label="bottom022"
  Shapes = -> [Cut067,Fusion146]
FEATURE [Part::MultiFuse] Fusion148  label="casePillars005"
  Shapes = -> [Cut047,Fusion092]
FEATURE [Part::MultiFuse] Fusion149  label="bottom023"
  Shapes = -> [Fusion124,Fusion113,Fusion147]
FEATURE [Part::MultiFuse] Fusion150  label="topBits"
  Shapes = -> [Cut025,Fusion148,Cut030,Fillet034]
FEATURE [Part::Feature] Face149 .. Face152  x4 (patterned run collapsed; names and placements below)
  shape: bbox 3.2 x 1.5 x 2e-07 mm, 1 faces, 0 solids (baked)
FEATURE [Part::Feature] Face153
  shape: bbox 3.6 x 3.2 x 2e-07 mm, 1 faces, 0 solids (baked)
FEATURE [Part::Feature] Face154
  shape: bbox 3.6 x 3.2 x 2e-07 mm, 1 faces, 0 solids (baked)
FEATURE [Sketcher::SketchObject] Sketch079  label="topSketch024"
  FullyConstrained = true
  sketch-geometry (6):
    g0: LineSegment StartX=19 StartY=38 StartZ=0 EndX=117 EndY=38 EndZ=0
    g1: ArcOfCircle CenterX=19 CenterY=19 CenterZ=0 NormalX=0 NormalY=0 NormalZ=1 AngleXU=0 Radius=19 StartAngle=1.5708 EndAngle=3.14159
    g2: LineSegment StartX=117 StartY=38 StartZ=0 EndX=117 EndY=19 EndZ=0
    g3: LineSegment StartX=98 StartY=1.0161e-12 StartZ=0 EndX=5.22862e-06 EndY=1.0161e-12 EndZ=0
    g4: LineSegment StartX=5.22862e-06 StartY=19 StartZ=0 EndX=5.22862e-06 EndY=1.0161e-12 EndZ=0
    g5: ArcOfCircle CenterX=98 CenterY=19 CenterZ=0 NormalX=0 NormalY=0 NormalZ=1 AngleXU=0 Radius=19 StartAngle=4.71239 EndAngle=6.28319
  constraints (16):
    c: Horizontal(g0)
    c: Distance(g0) = 98
    c: Coincident(g1,g0)
    c: Block(g1)
    c: Coincident(g2,g0)
    c: Vertical(g2)
    c: Distance(g2) = 19
    c: Horizontal(g3)
    c: Coincident(g4,g1)
    c: Vertical(g4)
    c: Coincident(g3,g4)
    c: Block(g3)
    c: Coincident(g5,g2)
    c: Coincident(g5,g3)
    c: Block(g0)
    c: Block(g5)
FEATURE [Sketcher::SketchObject] Sketch080  label="topSketch025"
  FullyConstrained = true
  sketch-geometry (6):
    g0: LineSegment StartX=19 StartY=38 StartZ=0 EndX=117 EndY=38 EndZ=0
    g1: ArcOfCircle CenterX=19 CenterY=19 CenterZ=0 NormalX=0 NormalY=0 NormalZ=1 AngleXU=0 Radius=19 StartAngle=1.5708 EndAngle=3.14159
    g2: LineSegment StartX=117 StartY=38 StartZ=0 EndX=117 EndY=19 EndZ=0
    g3: LineSegment StartX=98 StartY=1.0161e-12 StartZ=0 EndX=5.22862e-06 EndY=1.0161e-12 EndZ=0
    g4: LineSegment StartX=5.22862e-06 StartY=19 StartZ=0 EndX=5.22862e-06 EndY=1.0161e-12 EndZ=0
    g5: ArcOfCircle CenterX=98 CenterY=19 CenterZ=0 NormalX=0 NormalY=0 NormalZ=1 AngleXU=0 Radius=19 StartAngle=4.71239 EndAngle=6.28319
  constraints (16):
    c: Horizontal(g0)
    c: Distance(g0) = 98
    c: Coincident(g1,g0)
    c: Block(g1)
    c: Coincident(g2,g0)
    c: Vertical(g2)
    c: Distance(g2) = 19
    c: Horizontal(g3)
    c: Coincident(g4,g1)
    c: Vertical(g4)
    c: Coincident(g3,g4)
    c: Block(g3)
    c: Coincident(g5,g2)
    c: Coincident(g5,g3)
    c: Block(g0)
    c: Block(g5)
FEATURE [Part::Extrusion] Extrude070  label="sideA004"
  Base = -> Sketch080
  Dir = (0,0,1)
  DirMode = 2
  FaceMakerClass = Part::FaceMakerBullseye
  LengthFwd = 3
  LengthRev = 0
  Placement = pos=(0,0,-2.7) rot=(0,0,1;0rad)
  Solid = true
  Symmetric = false
FEATURE [Sketcher::SketchObject] Sketch081
  FullyConstrained = true
  Placement = pos=(117,19,0) rot=(0.57735,0.57735,0.57735;2.0944rad)
  sketch-geometry (8):
    g0: LineSegment StartX=-49.19 StartY=63.5 StartZ=0 EndX=-49.19 EndY=60.5 EndZ=0
    g1: LineSegment StartX=-49.19 StartY=11.5 StartZ=0 EndX=-49.19 EndY=8.5 EndZ=0
    g2: ArcOfCircle CenterX=-1.5 CenterY=62 CenterZ=0 NormalX=0 NormalY=0 NormalZ=1 AngleXU=0 Radius=1.5 StartAngle=4.71239 EndAngle=7.85398
    g3: ArcOfCircle CenterX=-1.5 CenterY=10 CenterZ=0 NormalX=0 NormalY=0 NormalZ=1 AngleXU=0 Radius=1.5 StartAngle=4.71239 EndAngle=7.85398
    g4: LineSegment StartX=-49.19 StartY=63.5 StartZ=0 EndX=-1.5 EndY=63.5 EndZ=0
    g5: LineSegment StartX=-49.19 StartY=60.5 StartZ=0 EndX=-1.5 EndY=60.5 EndZ=0
    g6: LineSegment StartX=-49.19 StartY=11.5 StartZ=0 EndX=-1.5 EndY=11.5 EndZ=0
    g7: LineSegment StartX=-49.19 StartY=8.5 StartZ=0 EndX=-1.5 EndY=8.5 EndZ=0
  constraints (19):
    c: Vertical(g0)
    c: Distance(g0) = 3
    c: Vertical(g1)
    c: Block(g1)
    c: Block(g2)
    c: Block(g3)
    c: Block(g0)
    c: Coincident(g4,g0)
    c: Coincident(g4,g2)
    c: Horizontal(g4)
    c: Coincident(g5,g0)
    c: Coincident(g5,g2)
    c: Horizontal(g5)
    c: Coincident(g6,g1)
    c: Coincident(g6,g3)
    c: Horizontal(g6)
    c: Coincident(g7,g1)
    c: Coincident(g7,g3)
    c: Horizontal(g7)
FEATURE [Part::Extrusion] Extrude071  label="sideB004"
  Base = -> Sketch079
  Dir = (0,0,1)
  DirMode = 2
  FaceMakerClass = Part::FaceMakerBullseye
  LengthFwd = 3
  LengthRev = 0
  Placement = pos=(0,0,71.7) rot=(0,0,1;0rad)
  Solid = true
  Symmetric = false
FEATURE [Part::MultiFuse] Fusion152  label="removeFromBottom004"
  Placement = pos=(2,0,0) rot=(0,0,1;0rad)
  Shapes = -> [Extrude070,Extrude071]
FEATURE [Part::Extrusion] Extrude072
  Base = -> Sketch081
  Dir = (1,0,0)
  DirMode = 2
  FaceMakerClass = Part::FaceMakerBullseye
  LengthFwd = 10
  LengthRev = 0
  Solid = true
  Symmetric = false
FEATURE [Part::Fillet] Fillet059  label="removeFromtMoreFrontCaseScrewRetainers004"
  Base = -> Extrude072
  Edges = 4 edges r=1.49: [Edge6,Edge11,Edge18,Edge23]
  Placement = pos=(-12,0,0) rot=(0,0,1;0rad)
FEATURE [Sketcher::SketchObject] Sketch082
  FullyConstrained = true
  Placement = pos=(117,19,0) rot=(0.57735,0.57735,0.57735;2.0944rad)
  sketch-geometry (8):
    g0: LineSegment StartX=-49.19 StartY=69.25 StartZ=0 EndX=-49.19 EndY=66.25 EndZ=0
    g1: LineSegment StartX=-49.19 StartY=5.75 StartZ=0 EndX=-49.19 EndY=2.75 EndZ=0
    g2: ArcOfCircle CenterX=-1.5 CenterY=67.75 CenterZ=0 NormalX=0 NormalY=0 NormalZ=1 AngleXU=0 Radius=1.5 StartAngle=4.71239 EndAngle=7.85398
    g3: ArcOfCircle CenterX=-1.5 CenterY=4.25 CenterZ=0 NormalX=0 NormalY=0 NormalZ=1 AngleXU=0 Radius=1.5 StartAngle=4.71239 EndAngle=7.85398
    g4: LineSegment StartX=-49.19 StartY=69.25 StartZ=0 EndX=-1.5 EndY=69.25 EndZ=0
    g5: LineSegment StartX=-49.19 StartY=66.25 StartZ=0 EndX=-1.5 EndY=66.25 EndZ=0
    g6: LineSegment StartX=-49.19 StartY=5.75 StartZ=0 EndX=-1.5 EndY=5.75 EndZ=0
    g7: LineSegment StartX=-49.19 StartY=2.75 StartZ=0 EndX=-1.5 EndY=2.75 EndZ=0
  constraints (19):
    c: Vertical(g0)
    c: Distance(g0) = 3
    c: Block(g0)
    c: Vertical(g1)
    c: Block(g2)
    c: Block(g3)
    c: Block(g1)
    c: Coincident(g4,g0)
    c: Coincident(g4,g2)
    c: Horizontal(g4)
    c: Coincident(g5,g0)
    c: Coincident(g5,g2)
    c: Horizontal(g5)
    c: Coincident(g6,g1)
    c: Coincident(g6,g3)
    c: Horizontal(g6)
    c: Coincident(g7,g1)
    c: Coincident(g7,g3)
    c: Horizontal(g7)
FEATURE [Part::Extrusion] Extrude073
  Base = -> Sketch082
  Dir = (1,0,0)
  DirMode = 2
  FaceMakerClass = Part::FaceMakerBullseye
  LengthFwd = 10
  LengthRev = 0
  Solid = true
  Symmetric = false
FEATURE [Part::Fillet] Fillet060  label="removeFromtMoreFrontCaseScrewRetainers005"
  Base = -> Extrude073
  Edges = 4 edges r=1.49: [Edge6,Edge11,Edge18,Edge23]
  Placement = pos=(-4,0,0) rot=(0,0,1;0rad)
FEATURE [Part::Revolution] Revolve163  label="backCaseScrewRetainer004"
  Angle = 360
  Axis = (0,1,0)
  Base = (0,0,0)
  FaceMakerClass = Part::FaceMakerBullseye
  Placement = pos=(12.5,3,62) rot=(0,0,1;0rad)
  Solid = false
  Source = -> Face149
  Symmetric = false
FEATURE [Part::Revolution] Revolve164  label="frontCaseScrewRetainer006"
  Angle = 360
  Axis = (0,1,0)
  Base = (0,0,0)
  FaceMakerClass = Part::FaceMakerBullseye
  Placement = pos=(89.5,3,68.5) rot=(0,0,1;0rad)
  Solid = false
  Source = -> Face151
  Symmetric = false
FEATURE [Part::Revolution] Revolve165  label="frontCaseScrewRetainer007"
  Angle = 360
  Axis = (0,1,0)
  Base = (0,0,0)
  FaceMakerClass = Part::FaceMakerBullseye
  Placement = pos=(89.5,3,3.5) rot=(0,0,1;0rad)
  Solid = false
  Source = -> Face152
  Symmetric = false
FEATURE [Part::Revolution] Revolve166  label="backCaseScrewRetainer005"
  Angle = 360
  Axis = (0,1,0)
  Base = (0,0,0)
  FaceMakerClass = Part::FaceMakerBullseye
  Placement = pos=(12.5,3,10) rot=(0,0,1;0rad)
  Solid = false
  Source = -> Face150
  Symmetric = false
FEATURE [Part::Revolution] Revolve167  label="moreFrontCaseScrewRetainer006"
  Angle = 360
  Axis = (0,1,0)
  Base = (0,0,0)
  FaceMakerClass = Part::FaceMakerBullseye
  Placement = pos=(109.5,4.5,68.5) rot=(0,0,1;0rad)
  Solid = false
  Source = -> Face153
  Symmetric = false
FEATURE [Part::Revolution] Revolve168  label="moreFrontCaseScrewRetainer007"
  Angle = 360
  Axis = (0,1,0)
  Base = (0,0,0)
  FaceMakerClass = Part::FaceMakerBullseye
  Placement = pos=(109.5,4.5,3.5) rot=(0,0,1;0rad)
  Solid = false
  Source = -> Face154
  Symmetric = false
FEATURE [Part::MultiFuse] Fusion151  label="screwRetainers003"
  Shapes = -> [Revolve168,Revolve167,Revolve166,Revolve165,Revolve164,Revolve163]
FEATURE [Part::Cut] Cut069  label="screwRetainers004"
  Base = -> Fusion151
  Tool = -> Fusion152
FEATURE [Part::Cut] Cut070
  Base = -> Cut069
  Tool = -> Fillet060
FEATURE [Part::Cut] Cut071  label="screwPillars001"
  Base = -> Cut070
  Tool = -> Fillet059
FEATURE [Part::MultiFuse] Fusion153  label="bottom024"
  Shapes = -> [Fusion149,Cut071]
FEATURE [Part::Cylinder] Cylinder067
  Angle = 360
  AttacherType = Attacher::AttachEngine3D
  Height = 10
  Placement = pos=(20.65,12,4.68) rot=(1,0,0;1.5708rad)
  Radius = 2
FEATURE [Part::Cylinder] Cylinder068
  Angle = 360
  AttacherType = Attacher::AttachEngine3D
  Height = 10
  Placement = pos=(20.65,12,67.38) rot=(1,0,0;1.5708rad)
  Radius = 2
FEATURE [Part::Cylinder] Cylinder069
  Angle = 360
  AttacherType = Attacher::AttachEngine3D
  Height = 10
  Placement = pos=(77.15,12,67.38) rot=(1,0,0;1.5708rad)
  Radius = 2
FEATURE [Part::Cylinder] Cylinder070
  Angle = 360
  AttacherType = Attacher::AttachEngine3D
  Height = 10
  Placement = pos=(77.15,12,4.68) rot=(1,0,0;1.5708rad)
  Radius = 2
FEATURE [Part::MultiFuse] Fusion154  label="removeFromThreadedInsertHousing001"
  Shapes = -> [Cylinder069,Cylinder068,Cylinder067,Cylinder070]
FEATURE [Part::Cut] Cut072  label="bottom025"
  Base = -> Fusion153
  Tool = -> Fusion154
FEATURE [Image::ImagePlane] ImagePlane
  XSize = 339
  YSize = 72
FEATURE [Sketcher::SketchObject] Sketch083
  FullyConstrained = false
  MapMode = 5
  Support = -> [XY_Plane]
  sketch-geometry (119):
    g0: LineSegment StartX=-151.619 StartY=28.8932 StartZ=0 EndX=-140.819 EndY=28.8932 EndZ=0
    g1: LineSegment StartX=-151.619 StartY=24.0313 StartZ=0 EndX=-151.619 EndY=28.8932 EndZ=0
    g2: LineSegment StartX=-140.819 StartY=17.7713 StartZ=0 EndX=-151.619 EndY=17.7713 EndZ=0
    g3: LineSegment StartX=-151.619 StartY=17.7713 StartZ=0 EndX=-151.619 EndY=22.6313 EndZ=0
    g4: LineSegment StartX=-151.619 StartY=22.6313 StartZ=0 EndX=-145.128 EndY=22.6313 EndZ=0
    g5: LineSegment StartX=-145.128 StartY=24.0313 StartZ=0 EndX=-140.819 EndY=28.8932 EndZ=0
    g6: LineSegment StartX=-145.128 StartY=22.6313 StartZ=0 EndX=-140.819 EndY=17.7713 EndZ=0
    g7: ArcOfCircle CenterX=-155.157 CenterY=23.3323 CenterZ=0 NormalX=0 NormalY=0 NormalZ=1 AngleXU=0 Radius=6.92354 StartAngle=1.03434 EndAngle=5.24885
    g8: ArcOfCircle CenterX=-155.157 CenterY=23.3323 CenterZ=0 NormalX=0 NormalY=0 NormalZ=1 AngleXU=0 Radius=12.6269 StartAngle=1.28675 EndAngle=4.99643
    g9: LineSegment StartX=-151.619 StartY=35.4532 StartZ=0 EndX=-151.619 EndY=29.2832 EndZ=0
    g10: LineSegment StartX=-151.619 StartY=17.3813 StartZ=0 EndX=-151.619 EndY=11.2113 EndZ=0
    g11-g21: Circle x11 (B-spline internal-alignment scaffolding for g22; pole/knot coordinates omitted)
    g22: BSplineCurve PolesCount=11 KnotsCount=9 Degree=3 IsPeriodic=0
    g23-g31: GeomPoint x9 (B-spline internal-alignment scaffolding for g22; pole/knot coordinates omitted)
    g32-g49: Circle x18 (B-spline internal-alignment scaffolding for g50; pole/knot coordinates omitted)
    g50: BSplineCurve PolesCount=18 KnotsCount=16 Degree=3 IsPeriodic=0
    g51-g66: GeomPoint x16 (B-spline internal-alignment scaffolding for g50; pole/knot coordinates omitted)
    g67: LineSegment StartX=-117.124 StartY=30.093 StartZ=0 EndX=-117.603 EndY=26.5272 EndZ=0
    g68: LineSegment StartX=-117.603 StartY=17.8472 StartZ=0 EndX=-117.124 EndY=14.2659 EndZ=0
    g69: Ellipse CenterX=-109.671 CenterY=20.025 CenterZ=0 NormalX=0 NormalY=0 NormalZ=1 MajorRadius=3.34798 MinorRadius=2.71052 AngleXU=-1.56793
    g70: GeomPoint X=-109.666 Y=18.0598 Z=0
    g71: GeomPoint X=-109.677 Y=21.9902 Z=0
    g72: Ellipse CenterX=-109.671 CenterY=20.0123 CenterZ=0 NormalX=0 NormalY=0 NormalZ=1 MajorRadius=6.93002 MinorRadius=6.36273 AngleXU=-3.13976
    g73: GeomPoint X=-112.417 Y=20.0073 Z=0
    g74: GeomPoint X=-106.925 Y=20.0173 Z=0
    g75: Ellipse CenterX=-51.7682 CenterY=20.1463 CenterZ=0 NormalX=0 NormalY=0 NormalZ=1 MajorRadius=3.19279 MinorRadius=2.71052 AngleXU=-1.52774
    g76: GeomPoint X=-51.6955 Y=18.4606 Z=0
    g77: GeomPoint X=-51.8408 Y=21.832 Z=0
    g78: GeomPoint X=-54.5142 Y=20.1413 Z=0
    g79: GeomPoint X=-49.0221 Y=20.1513 Z=0
    g80: Ellipse CenterX=-51.7682 CenterY=20.1463 CenterZ=0 NormalX=0 NormalY=0 NormalZ=1 MajorRadius=6.93002 MinorRadius=6.36273 AngleXU=-3.13976
    g81: Ellipse CenterX=-22.8436 CenterY=20.1783 CenterZ=0 NormalX=0 NormalY=0 NormalZ=1 MajorRadius=3.31512 MinorRadius=2.71052 AngleXU=-1.60214
    g82: GeomPoint X=-22.9034 Y=18.2706 Z=0
    g83: GeomPoint X=-22.7838 Y=22.0861 Z=0
    g84: GeomPoint X=-25.5897 Y=20.1733 Z=0
    g85: GeomPoint X=-20.0976 Y=20.1833 Z=0
    g86: Ellipse CenterX=-22.8436 CenterY=20.1783 CenterZ=0 NormalX=0 NormalY=0 NormalZ=1 MajorRadius=6.93002 MinorRadius=6.36273 AngleXU=-3.13976
    g87: LineSegment StartX=-101.889 StartY=14.1107 StartZ=0 EndX=-97.7455 EndY=14.1107 EndZ=0
    g88: LineSegment StartX=-93.8155 StartY=14.1107 StartZ=0 EndX=-89.6755 EndY=14.1107 EndZ=0
    g89: LineSegment StartX=-85.7455 StartY=14.1107 StartZ=0 EndX=-81.6055 EndY=14.1107 EndZ=0
    g90: LineSegment StartX=-101.889 StartY=14.1107 StartZ=0 EndX=-101.889 EndY=25.9907 EndZ=0
    g91: LineSegment StartX=-101.889 StartY=25.9907 StartZ=0 EndX=-97.8594 EndY=25.9907 EndZ=0
    g92: LineSegment StartX=-97.8594 StartY=25.9907 StartZ=0 EndX=-97.8594 EndY=24.0907 EndZ=0
    g93: LineSegment StartX=-97.7455 StartY=14.1107 StartZ=0 EndX=-97.7455 EndY=19.9107 EndZ=0
    g94: LineSegment StartX=-89.6755 StartY=14.1107 StartZ=0 EndX=-89.6755 EndY=19.9107 EndZ=0
    g95: LineSegment StartX=-85.7455 StartY=14.1107 StartZ=0 EndX=-85.7455 EndY=21.0107 EndZ=0
    g96: LineSegment StartX=-93.8155 StartY=14.1107 StartZ=0 EndX=-93.8155 EndY=21.0107 EndZ=0
    g97-g107: Circle x11 (B-spline internal-alignment scaffolding for g108; pole/knot coordinates omitted)
    g108: BSplineCurve PolesCount=11 KnotsCount=9 Degree=3 IsPeriodic=0
    g109-g117: GeomPoint x9 (B-spline internal-alignment scaffolding for g108; pole/knot coordinates omitted)
    g118: BSplineCurve PolesCount=11 KnotsCount=9 Degree=3 IsPeriodic=0
  constraints (94):
    c: Coincident(g1,g0)
    c: Horizontal(g0)
    c: Vertical(g1)
    c: Coincident(g2,g3)
    c: Coincident(g3,g4)
    c: Horizontal(g4)
    c: Horizontal(g2)
    c: Vertical(g3)
    c: Block(g1)
    c: Distance(g3) = 4.86
    c: Block(g4)
    c: Distance(g0) = 10.8
    c: Distance(g2) = 10.8
    c: Coincident(g5,g0)
    c: Coincident(g6,g4)
    c: Coincident(g6,g2)
    c: Block(g8)
    c: Block(g7)
    c: Coincident(g9,g8)
    c: Coincident(g9,g7)
    c: Vertical(g9)
    c: Coincident(g10,g7)
    c: Coincident(g10,g8)
    c: Vertical(g10)
    c: Weight(g11) = 1
    c: Equal(g11, g12-g21) x10
    c: InternalAlignment(g11-g21 -> g22) x11
    c: InternalAlignment(g23-g31 -> g22) x9
    c: Block(g22)
    c: Weight(g32) = 1
    c: Equal(g32, g33-g49) x17
    c: InternalAlignment(g32-g49 -> g50) x18
    c: InternalAlignment(g51-g66 -> g50) x16
    c: Block(g50)
    c: Coincident(g67,g50)
    c: Coincident(g67,g22)
    c: Coincident(g68,g22)
    c: Coincident(g68,g50)
    c: InternalAlignment(g70,g69)
    c: InternalAlignment(g71,g69)
    c: Block(g69)
    c: InternalAlignment(g73,g72)
    c: InternalAlignment(g74,g72)
    c: Block(g72)
    c: InternalAlignment(g76,g75)
    c: InternalAlignment(g77,g75)
    c: InternalAlignment(g78,g80)
    c: InternalAlignment(g79,g80)
    c: Block(g80)
    c: Coincident(g75,g80)
    c: Block(g75)
    c: InternalAlignment(g82,g81)
    c: InternalAlignment(g83,g81)
    c: InternalAlignment(g84,g86)
    c: InternalAlignment(g85,g86)
    c: Block(g86)
    c: Coincident(g81,g86)
    c: Block(g81)
    c: Horizontal(g87)
    c: Block(g87)
    c: Horizontal(g88)
    c: Distance(g88) = 4.14
    c: Horizontal(g89)
    c: Equal(g88,g89) = 4.14
    c: Block(g89)
    c: Block(g88)
    c: Coincident(g90,g87)
    c: Vertical(g90)
    c: Distance(g90) = 11.88
    c: Coincident(g91,g90)
    c: Horizontal(g91)
    c: Coincident(g92,g91)
    c: Vertical(g92)
    c: Distance(g91) = 4.03
    c: Distance(g92) = 1.9
    c: Coincident(g93,g87)
    c: Vertical(g93)
    c: Vertical(g94)
    c: Coincident(g94,g88)
    c: Distance(g93) = 5.8
    c: Distance(g94) = 5.8
    c: Coincident(g95,g89)
    c: Vertical(g95)
    c: Vertical(g96)
    c: Coincident(g96,g88)
    c: Distance(g96) = 6.9
    c: Distance(g95) = 6.9
    c: Coincident(g108,g92)
    c: Weight(g97) = 1
    c: Equal(g97, g98-g107) x10
    c: InternalAlignment(g97-g107 -> g108) x11
    c: InternalAlignment(g109-g117 -> g108) x9
    c: Block(g108)
    c: Block(g118)
FEATURE [PartDesign::Body] Body
  Group = -> [Sketch083]
  Origin = -> Origin
FEATURE [Sketcher::SketchObject] Sketch084
  FullyConstrained = true
  MapMode = 5
  Support = -> [XY_Plane001]
FEATURE [PartDesign::Body] Body001
  Group = -> [Sketch084]
  Origin = -> Origin001
